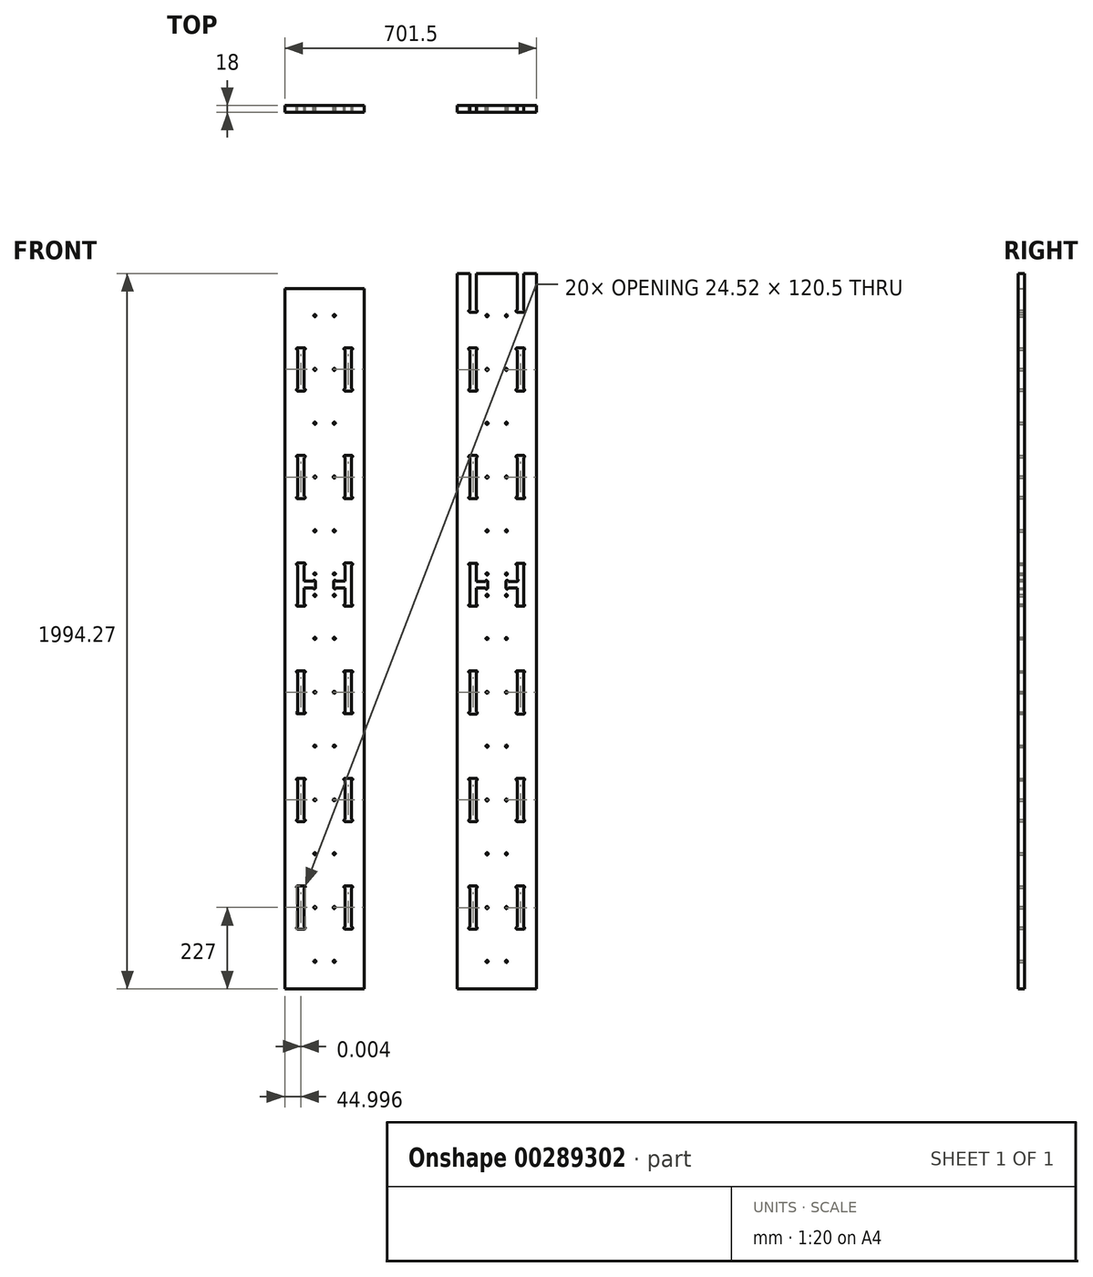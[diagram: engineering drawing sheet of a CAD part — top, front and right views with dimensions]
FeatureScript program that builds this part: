
annotation { "Feature Type Name" : "Feature", "Feature Type Description" : "" }
export const myFeature = defineFeature(function(context is Context, id is Id, definition is map)
    precondition{}
    {
        {
            var Q0;
            Q0=qCreatedBy(makeId("Front.planeOp"),FACE);
            var sketch = newSketch(context, id + "F0", { "sketchPlane" : qUnion([Q0])});
            skLineSegment(sketch, "E0", {"start": v(-600, -1200) * mm, "end": v(600, -1200) * mm});
            skLineSegment(sketch, "E1", {"start": v(600, -1200) * mm, "end": v(600, 1200) * mm});
            skLineSegment(sketch, "E2", {"start": v(600, 1200) * mm, "end": v(-600, 1200) * mm});
            skLineSegment(sketch, "E3", {"start": v(-600, 1200) * mm, "end": v(-600, -1200) * mm});
            skLineSegment(sketch, "E4", {"start": v(366, 819.27) * mm, "end": v(330.5, 819.27) * mm});
            skLineSegment(sketch, "E5", {"start": v(330.5, 819.27) * mm, "end": v(330.5, 717.52) * mm});
            skArc(sketch, "E6", {"start": v(330.5, 717.52) * mm, "mid": v(333.51, 714.51) * mm, "end": v(330.5, 711.5) * mm});
            skLineSegment(sketch, "E7", {"start": v(330.5, 711.5) * mm, "end": v(312, 711.5) * mm});
            skArc(sketch, "E8", {"start": v(312, 711.5) * mm, "mid": v(309, 714.51) * mm, "end": v(312, 717.52) * mm});
            skLineSegment(sketch, "E9", {"start": v(312, 717.52) * mm, "end": v(312, 819.27) * mm});
            skLineSegment(sketch, "E10", {"start": v(312, 819.27) * mm, "end": v(198.5, 819.27) * mm});
            skLineSegment(sketch, "E11", {"start": v(198.5, 819.27) * mm, "end": v(198.5, 717.52) * mm});
            skArc(sketch, "E12", {"start": v(198.5, 717.52) * mm, "mid": v(201.51, 714.51) * mm, "end": v(198.5, 711.5) * mm});
            skLineSegment(sketch, "E13", {"start": v(198.5, 711.5) * mm, "end": v(180, 711.5) * mm});
            skArc(sketch, "E14", {"start": v(180, 711.5) * mm, "mid": v(177, 714.51) * mm, "end": v(180, 717.52) * mm});
            skLineSegment(sketch, "E15", {"start": v(180, 717.52) * mm, "end": v(180, 819.27) * mm});
            skLineSegment(sketch, "E16", {"start": v(180, 819.27) * mm, "end": v(144.5, 819.27) * mm});
            skLineSegment(sketch, "E17", {"start": v(144.5, 819.27) * mm, "end": v(144.5, -1175) * mm});
            skLineSegment(sketch, "E18", {"start": v(144.5, -1175) * mm, "end": v(366, -1175) * mm});
            skLineSegment(sketch, "E19", {"start": v(366, -1175) * mm, "end": v(366, 819.27) * mm});
            skLineSegment(sketch, "E20", {"start": v(126.5, 819.27) * mm, "end": v(91, 819.27) * mm});
            skLineSegment(sketch, "E21", {"start": v(91, 819.27) * mm, "end": v(91, 717.52) * mm});
            skArc(sketch, "E22", {"start": v(91, 717.52) * mm, "mid": v(94.01, 714.51) * mm, "end": v(91, 711.5) * mm});
            skLineSegment(sketch, "E23", {"start": v(91, 711.5) * mm, "end": v(72.5, 711.5) * mm});
            skArc(sketch, "E24", {"start": v(72.5, 711.5) * mm, "mid": v(69.5, 714.51) * mm, "end": v(72.5, 717.52) * mm});
            skLineSegment(sketch, "E25", {"start": v(72.5, 717.52) * mm, "end": v(72.5, 819.27) * mm});
            skLineSegment(sketch, "E26", {"start": v(72.5, 819.27) * mm, "end": v(-41, 819.27) * mm});
            skLineSegment(sketch, "E27", {"start": v(-41, 819.27) * mm, "end": v(-41, 717.52) * mm});
            skArc(sketch, "E28", {"start": v(-41, 717.52) * mm, "mid": v(-37.99, 714.51) * mm, "end": v(-41, 711.5) * mm});
            skLineSegment(sketch, "E29", {"start": v(-41, 711.5) * mm, "end": v(-59.5, 711.5) * mm});
            skArc(sketch, "E30", {"start": v(-59.5, 711.5) * mm, "mid": v(-62.5, 714.51) * mm, "end": v(-59.5, 717.52) * mm});
            skLineSegment(sketch, "E31", {"start": v(-59.5, 717.52) * mm, "end": v(-59.5, 819.27) * mm});
            skLineSegment(sketch, "E32", {"start": v(-59.5, 819.27) * mm, "end": v(-95, 819.27) * mm});
            skLineSegment(sketch, "E33", {"start": v(-95, 819.27) * mm, "end": v(-95, -1175) * mm});
            skLineSegment(sketch, "E34", {"start": v(-95, -1175) * mm, "end": v(126.5, -1175) * mm});
            skLineSegment(sketch, "E35", {"start": v(126.5, -1175) * mm, "end": v(126.5, 819.27) * mm});
            skLineSegment(sketch, "E36", {"start": v(-353, 777.5) * mm, "end": v(-575, 777.5) * mm});
            skLineSegment(sketch, "E37", {"start": v(-575, 777.5) * mm, "end": v(-575, -1175) * mm});
            skLineSegment(sketch, "E38", {"start": v(-575, -1175) * mm, "end": v(-353, -1175) * mm});
            skLineSegment(sketch, "E39", {"start": v(-353, -1175) * mm, "end": v(-353, 777.5) * mm});
            skLineSegment(sketch, "E40", {"start": v(-113, 777.5) * mm, "end": v(-335, 777.5) * mm});
            skLineSegment(sketch, "E41", {"start": v(-335, 777.5) * mm, "end": v(-335, -1175) * mm});
            skLineSegment(sketch, "E42", {"start": v(-335, -1175) * mm, "end": v(-113, -1175) * mm});
            skLineSegment(sketch, "E43", {"start": v(-113, -1175) * mm, "end": v(-113, 777.5) * mm});
            skLineSegment(sketch, "E44", {"start": v(198.5, -888) * mm, "end": v(180, -888) * mm});
            skArc(sketch, "E45", {"start": v(180, -888) * mm, "mid": v(177, -891) * mm, "end": v(180, -894.02) * mm});
            skLineSegment(sketch, "E46", {"start": v(180, -894.02) * mm, "end": v(180, -1002.48) * mm});
            skArc(sketch, "E47", {"start": v(180, -1002.48) * mm, "mid": v(177, -1005.49) * mm, "end": v(180, -1008.5) * mm});
            skLineSegment(sketch, "E48", {"start": v(180, -1008.5) * mm, "end": v(198.5, -1008.5) * mm});
            skArc(sketch, "E49", {"start": v(198.5, -1008.5) * mm, "mid": v(201.51, -1005.49) * mm, "end": v(198.5, -1002.48) * mm});
            skLineSegment(sketch, "E50", {"start": v(198.5, -1002.48) * mm, "end": v(198.5, -894.02) * mm});
            skArc(sketch, "E51", {"start": v(198.5, -894.02) * mm, "mid": v(201.51, -891) * mm, "end": v(198.5, -888) * mm});
            skLineSegment(sketch, "E52", {"start": v(312, -948.25) * mm, "end": v(312, -1002.48) * mm});
            skArc(sketch, "E53", {"start": v(312, -1002.48) * mm, "mid": v(309, -1005.49) * mm, "end": v(312, -1008.5) * mm});
            skLineSegment(sketch, "E54", {"start": v(312, -1008.5) * mm, "end": v(330.5, -1008.5) * mm});
            skArc(sketch, "E55", {"start": v(330.5, -1008.5) * mm, "mid": v(333.51, -1005.49) * mm, "end": v(330.5, -1002.48) * mm});
            skLineSegment(sketch, "E56", {"start": v(330.5, -1002.48) * mm, "end": v(330.5, -894.02) * mm});
            skArc(sketch, "E57", {"start": v(330.5, -894.02) * mm, "mid": v(333.51, -891) * mm, "end": v(330.5, -888) * mm});
            skLineSegment(sketch, "E58", {"start": v(330.5, -888) * mm, "end": v(312, -888) * mm});
            skArc(sketch, "E59", {"start": v(312, -888) * mm, "mid": v(309, -891) * mm, "end": v(312, -894.02) * mm});
            skLineSegment(sketch, "E60", {"start": v(312, -894.02) * mm, "end": v(312, -948.25) * mm});
            skLineSegment(sketch, "E61", {"start": v(312, -594.02) * mm, "end": v(312, -702.48) * mm});
            skArc(sketch, "E62", {"start": v(312, -702.48) * mm, "mid": v(309, -705.49) * mm, "end": v(312, -708.5) * mm});
            skLineSegment(sketch, "E63", {"start": v(312, -708.5) * mm, "end": v(330.5, -708.5) * mm});
            skArc(sketch, "E64", {"start": v(330.5, -708.5) * mm, "mid": v(333.51, -705.49) * mm, "end": v(330.5, -702.48) * mm});
            skLineSegment(sketch, "E65", {"start": v(330.5, -702.48) * mm, "end": v(330.5, -594.02) * mm});
            skArc(sketch, "E66", {"start": v(330.5, -594.02) * mm, "mid": v(333.51, -591) * mm, "end": v(330.5, -588) * mm});
            skLineSegment(sketch, "E67", {"start": v(330.5, -588) * mm, "end": v(312, -588) * mm});
            skArc(sketch, "E68", {"start": v(312, -588) * mm, "mid": v(309, -591) * mm, "end": v(312, -594.02) * mm});
            skLineSegment(sketch, "E69", {"start": v(330.5, -402.48) * mm, "end": v(330.5, -294.02) * mm});
            skArc(sketch, "E70", {"start": v(330.5, -294.02) * mm, "mid": v(333.51, -291) * mm, "end": v(330.5, -288) * mm});
            skLineSegment(sketch, "E71", {"start": v(330.5, -288) * mm, "end": v(312, -288) * mm});
            skArc(sketch, "E72", {"start": v(312, -288) * mm, "mid": v(309, -291) * mm, "end": v(312, -294.02) * mm});
            skLineSegment(sketch, "E73", {"start": v(312, -294.02) * mm, "end": v(312, -402.48) * mm});
            skArc(sketch, "E74", {"start": v(312, -402.48) * mm, "mid": v(309, -405.49) * mm, "end": v(312, -408.5) * mm});
            skLineSegment(sketch, "E75", {"start": v(312, -408.5) * mm, "end": v(330.5, -408.5) * mm});
            skArc(sketch, "E76", {"start": v(330.5, -408.5) * mm, "mid": v(333.51, -405.49) * mm, "end": v(330.5, -402.48) * mm});
            skLineSegment(sketch, "E77", {"start": v(330.5, -102.48) * mm, "end": v(330.5, 5.98) * mm});
            skArc(sketch, "E78", {"start": v(330.5, 5.98) * mm, "mid": v(333.51, 9) * mm, "end": v(330.5, 12) * mm});
            skLineSegment(sketch, "E79", {"start": v(330.5, 12) * mm, "end": v(312, 12) * mm});
            skArc(sketch, "E80", {"start": v(312, 12) * mm, "mid": v(309, 9) * mm, "end": v(312, 5.98) * mm});
            skLineSegment(sketch, "E81", {"start": v(312, 5.98) * mm, "end": v(312, -32.98) * mm});
            skArc(sketch, "E82", {"start": v(312, -32.98) * mm, "mid": v(315.01, -35.99) * mm, "end": v(312, -39) * mm});
            skLineSegment(sketch, "E83", {"start": v(312, -39) * mm, "end": v(287.02, -39) * mm});
            skArc(sketch, "E84", {"start": v(287.02, -39) * mm, "mid": v(284.01, -35.99) * mm, "end": v(281, -39) * mm});
            skLineSegment(sketch, "E85", {"start": v(281, -39) * mm, "end": v(281, -57.5) * mm});
            skArc(sketch, "E86", {"start": v(281, -57.5) * mm, "mid": v(284.01, -60.5) * mm, "end": v(287.02, -57.5) * mm});
            skLineSegment(sketch, "E87", {"start": v(287.02, -57.5) * mm, "end": v(312, -57.5) * mm});
            skLineSegment(sketch, "E88", {"start": v(312, -57.5) * mm, "end": v(312, -102.48) * mm});
            skArc(sketch, "E89", {"start": v(312, -102.48) * mm, "mid": v(309, -105.49) * mm, "end": v(312, -108.5) * mm});
            skLineSegment(sketch, "E90", {"start": v(312, -108.5) * mm, "end": v(330.5, -108.5) * mm});
            skArc(sketch, "E91", {"start": v(330.5, -108.5) * mm, "mid": v(333.51, -105.49) * mm, "end": v(330.5, -102.48) * mm});
            skLineSegment(sketch, "E92", {"start": v(312, 305.98) * mm, "end": v(312, 197.52) * mm});
            skArc(sketch, "E93", {"start": v(312, 197.52) * mm, "mid": v(309, 194.51) * mm, "end": v(312, 191.5) * mm});
            skLineSegment(sketch, "E94", {"start": v(312, 191.5) * mm, "end": v(330.5, 191.5) * mm});
            skArc(sketch, "E95", {"start": v(330.5, 191.5) * mm, "mid": v(333.51, 194.51) * mm, "end": v(330.5, 197.52) * mm});
            skLineSegment(sketch, "E96", {"start": v(330.5, 197.52) * mm, "end": v(330.5, 305.98) * mm});
            skArc(sketch, "E97", {"start": v(330.5, 305.98) * mm, "mid": v(333.51, 309) * mm, "end": v(330.5, 312) * mm});
            skLineSegment(sketch, "E98", {"start": v(330.5, 312) * mm, "end": v(312, 312) * mm});
            skArc(sketch, "E99", {"start": v(312, 312) * mm, "mid": v(309, 309) * mm, "end": v(312, 305.98) * mm});
            skLineSegment(sketch, "E100", {"start": v(330.5, 497.52) * mm, "end": v(330.5, 605.98) * mm});
            skArc(sketch, "E101", {"start": v(330.5, 605.98) * mm, "mid": v(333.51, 609) * mm, "end": v(330.5, 612) * mm});
            skLineSegment(sketch, "E102", {"start": v(330.5, 612) * mm, "end": v(312, 612) * mm});
            skArc(sketch, "E103", {"start": v(312, 612) * mm, "mid": v(309, 609) * mm, "end": v(312, 605.98) * mm});
            skLineSegment(sketch, "E104", {"start": v(312, 605.98) * mm, "end": v(312, 497.52) * mm});
            skArc(sketch, "E105", {"start": v(312, 497.52) * mm, "mid": v(309, 494.51) * mm, "end": v(312, 491.5) * mm});
            skLineSegment(sketch, "E106", {"start": v(312, 491.5) * mm, "end": v(330.5, 491.5) * mm});
            skArc(sketch, "E107", {"start": v(330.5, 491.5) * mm, "mid": v(333.51, 494.51) * mm, "end": v(330.5, 497.52) * mm});
            skLineSegment(sketch, "E108", {"start": v(180, 605.98) * mm, "end": v(180, 497.52) * mm});
            skArc(sketch, "E109", {"start": v(180, 497.52) * mm, "mid": v(177, 494.51) * mm, "end": v(180, 491.5) * mm});
            skLineSegment(sketch, "E110", {"start": v(180, 491.5) * mm, "end": v(198.5, 491.5) * mm});
            skArc(sketch, "E111", {"start": v(198.5, 491.5) * mm, "mid": v(201.51, 494.51) * mm, "end": v(198.5, 497.52) * mm});
            skLineSegment(sketch, "E112", {"start": v(198.5, 497.52) * mm, "end": v(198.5, 605.98) * mm});
            skArc(sketch, "E113", {"start": v(198.5, 605.98) * mm, "mid": v(201.51, 609) * mm, "end": v(198.5, 612) * mm});
            skLineSegment(sketch, "E114", {"start": v(198.5, 612) * mm, "end": v(180, 612) * mm});
            skArc(sketch, "E115", {"start": v(180, 612) * mm, "mid": v(177, 609) * mm, "end": v(180, 605.98) * mm});
            skLineSegment(sketch, "E116", {"start": v(198.5, -702.48) * mm, "end": v(198.5, -594.02) * mm});
            skArc(sketch, "E117", {"start": v(198.5, -594.02) * mm, "mid": v(201.51, -591.01) * mm, "end": v(198.5, -588) * mm});
            skLineSegment(sketch, "E118", {"start": v(198.5, -588) * mm, "end": v(180, -588) * mm});
            skArc(sketch, "E119", {"start": v(180, -588) * mm, "mid": v(177, -591.01) * mm, "end": v(180, -594.02) * mm});
            skLineSegment(sketch, "E120", {"start": v(180, -594.02) * mm, "end": v(180, -702.48) * mm});
            skArc(sketch, "E121", {"start": v(180, -702.48) * mm, "mid": v(177, -705.5) * mm, "end": v(180, -708.5) * mm});
            skLineSegment(sketch, "E122", {"start": v(180, -708.5) * mm, "end": v(198.5, -708.5) * mm});
            skArc(sketch, "E123", {"start": v(198.5, -708.5) * mm, "mid": v(201.51, -705.5) * mm, "end": v(198.5, -702.48) * mm});
            skLineSegment(sketch, "E124", {"start": v(180, -294.02) * mm, "end": v(180, -402.48) * mm});
            skArc(sketch, "E125", {"start": v(180, -402.48) * mm, "mid": v(177, -405.5) * mm, "end": v(180, -408.5) * mm});
            skLineSegment(sketch, "E126", {"start": v(180, -408.5) * mm, "end": v(198.5, -408.5) * mm});
            skArc(sketch, "E127", {"start": v(198.5, -408.5) * mm, "mid": v(201.51, -405.5) * mm, "end": v(198.5, -402.48) * mm});
            skLineSegment(sketch, "E128", {"start": v(198.5, -402.48) * mm, "end": v(198.5, -294.02) * mm});
            skArc(sketch, "E129", {"start": v(198.5, -294.02) * mm, "mid": v(201.51, -291.01) * mm, "end": v(198.5, -288) * mm});
            skLineSegment(sketch, "E130", {"start": v(198.5, -288) * mm, "end": v(180, -288) * mm});
            skArc(sketch, "E131", {"start": v(180, -288) * mm, "mid": v(177, -291.01) * mm, "end": v(180, -294.02) * mm});
            skLineSegment(sketch, "E132", {"start": v(198.5, -39) * mm, "end": v(198.5, 5.98) * mm});
            skArc(sketch, "E133", {"start": v(198.5, 5.98) * mm, "mid": v(201.51, 9) * mm, "end": v(198.5, 12) * mm});
            skLineSegment(sketch, "E134", {"start": v(198.5, 12) * mm, "end": v(180, 12) * mm});
            skArc(sketch, "E135", {"start": v(180, 12) * mm, "mid": v(177, 9) * mm, "end": v(180, 5.98) * mm});
            skLineSegment(sketch, "E136", {"start": v(180, 5.98) * mm, "end": v(180, -102.48) * mm});
            skArc(sketch, "E137", {"start": v(180, -102.48) * mm, "mid": v(177, -105.49) * mm, "end": v(180, -108.5) * mm});
            skLineSegment(sketch, "E138", {"start": v(180, -108.5) * mm, "end": v(198.5, -108.5) * mm});
            skArc(sketch, "E139", {"start": v(198.5, -108.5) * mm, "mid": v(201.51, -105.49) * mm, "end": v(198.5, -102.48) * mm});
            skLineSegment(sketch, "E140", {"start": v(198.5, -102.48) * mm, "end": v(198.5, -57.5) * mm});
            skLineSegment(sketch, "E141", {"start": v(198.5, -57.5) * mm, "end": v(223.48, -57.5) * mm});
            skArc(sketch, "E142", {"start": v(223.48, -57.5) * mm, "mid": v(226.5, -60.5) * mm, "end": v(229.5, -57.5) * mm});
            skLineSegment(sketch, "E143", {"start": v(229.5, -57.5) * mm, "end": v(229.5, -39) * mm});
            skArc(sketch, "E144", {"start": v(229.5, -39) * mm, "mid": v(226.5, -35.99) * mm, "end": v(223.48, -39) * mm});
            skLineSegment(sketch, "E145", {"start": v(223.48, -39) * mm, "end": v(198.5, -39) * mm});
            skLineSegment(sketch, "E146", {"start": v(198.5, 197.52) * mm, "end": v(198.5, 305.98) * mm});
            skArc(sketch, "E147", {"start": v(198.5, 305.98) * mm, "mid": v(201.51, 309) * mm, "end": v(198.5, 312) * mm});
            skLineSegment(sketch, "E148", {"start": v(198.5, 312) * mm, "end": v(180, 312) * mm});
            skArc(sketch, "E149", {"start": v(180, 312) * mm, "mid": v(177, 309) * mm, "end": v(180, 305.98) * mm});
            skLineSegment(sketch, "E150", {"start": v(180, 305.98) * mm, "end": v(180, 197.52) * mm});
            skArc(sketch, "E151", {"start": v(180, 197.52) * mm, "mid": v(177, 194.51) * mm, "end": v(180, 191.5) * mm});
            skLineSegment(sketch, "E152", {"start": v(180, 191.5) * mm, "end": v(198.5, 191.5) * mm});
            skArc(sketch, "E153", {"start": v(198.5, 191.5) * mm, "mid": v(201.51, 194.51) * mm, "end": v(198.5, 197.52) * mm});
            skLineSegment(sketch, "E154", {"start": v(-41, -888) * mm, "end": v(-59.5, -888) * mm});
            skArc(sketch, "E155", {"start": v(-59.5, -888) * mm, "mid": v(-62.5, -891) * mm, "end": v(-59.5, -894.02) * mm});
            skLineSegment(sketch, "E156", {"start": v(-59.5, -894.02) * mm, "end": v(-59.5, -1002.48) * mm});
            skArc(sketch, "E157", {"start": v(-59.5, -1002.48) * mm, "mid": v(-62.5, -1005.49) * mm, "end": v(-59.5, -1008.5) * mm});
            skLineSegment(sketch, "E158", {"start": v(-59.5, -1008.5) * mm, "end": v(-41, -1008.5) * mm});
            skArc(sketch, "E159", {"start": v(-41, -1008.5) * mm, "mid": v(-37.99, -1005.49) * mm, "end": v(-41, -1002.48) * mm});
            skLineSegment(sketch, "E160", {"start": v(-41, -1002.48) * mm, "end": v(-41, -894.02) * mm});
            skArc(sketch, "E161", {"start": v(-41, -894.02) * mm, "mid": v(-37.99, -891) * mm, "end": v(-41, -888) * mm});
            skLineSegment(sketch, "E162", {"start": v(72.5, -948.25) * mm, "end": v(72.5, -1002.48) * mm});
            skArc(sketch, "E163", {"start": v(72.5, -1002.48) * mm, "mid": v(69.5, -1005.49) * mm, "end": v(72.5, -1008.5) * mm});
            skLineSegment(sketch, "E164", {"start": v(72.5, -1008.5) * mm, "end": v(91, -1008.5) * mm});
            skArc(sketch, "E165", {"start": v(91, -1008.5) * mm, "mid": v(94.01, -1005.49) * mm, "end": v(91, -1002.48) * mm});
            skLineSegment(sketch, "E166", {"start": v(91, -1002.48) * mm, "end": v(91, -894.02) * mm});
            skArc(sketch, "E167", {"start": v(91, -894.02) * mm, "mid": v(94.01, -891) * mm, "end": v(91, -888) * mm});
            skLineSegment(sketch, "E168", {"start": v(91, -888) * mm, "end": v(72.5, -888) * mm});
            skArc(sketch, "E169", {"start": v(72.5, -888) * mm, "mid": v(69.5, -891) * mm, "end": v(72.5, -894.02) * mm});
            skLineSegment(sketch, "E170", {"start": v(72.5, -894.02) * mm, "end": v(72.5, -948.25) * mm});
            skLineSegment(sketch, "E171", {"start": v(72.5, -594.02) * mm, "end": v(72.5, -702.48) * mm});
            skArc(sketch, "E172", {"start": v(72.5, -702.48) * mm, "mid": v(69.5, -705.49) * mm, "end": v(72.5, -708.5) * mm});
            skLineSegment(sketch, "E173", {"start": v(72.5, -708.5) * mm, "end": v(91, -708.5) * mm});
            skArc(sketch, "E174", {"start": v(91, -708.5) * mm, "mid": v(94.01, -705.49) * mm, "end": v(91, -702.48) * mm});
            skLineSegment(sketch, "E175", {"start": v(91, -702.48) * mm, "end": v(91, -594.02) * mm});
            skArc(sketch, "E176", {"start": v(91, -594.02) * mm, "mid": v(94.01, -591) * mm, "end": v(91, -588) * mm});
            skLineSegment(sketch, "E177", {"start": v(91, -588) * mm, "end": v(72.5, -588) * mm});
            skArc(sketch, "E178", {"start": v(72.5, -588) * mm, "mid": v(69.5, -591) * mm, "end": v(72.5, -594.02) * mm});
            skLineSegment(sketch, "E179", {"start": v(91, -402.48) * mm, "end": v(91, -294.02) * mm});
            skArc(sketch, "E180", {"start": v(91, -294.02) * mm, "mid": v(94.01, -291) * mm, "end": v(91, -288) * mm});
            skLineSegment(sketch, "E181", {"start": v(91, -288) * mm, "end": v(72.5, -288) * mm});
            skArc(sketch, "E182", {"start": v(72.5, -288) * mm, "mid": v(69.5, -291) * mm, "end": v(72.5, -294.02) * mm});
            skLineSegment(sketch, "E183", {"start": v(72.5, -294.02) * mm, "end": v(72.5, -402.48) * mm});
            skArc(sketch, "E184", {"start": v(72.5, -402.48) * mm, "mid": v(69.5, -405.49) * mm, "end": v(72.5, -408.5) * mm});
            skLineSegment(sketch, "E185", {"start": v(72.5, -408.5) * mm, "end": v(91, -408.5) * mm});
            skArc(sketch, "E186", {"start": v(91, -408.5) * mm, "mid": v(94.01, -405.49) * mm, "end": v(91, -402.48) * mm});
            skLineSegment(sketch, "E187", {"start": v(91, -102.48) * mm, "end": v(91, 5.98) * mm});
            skArc(sketch, "E188", {"start": v(91, 5.98) * mm, "mid": v(94.01, 9) * mm, "end": v(91, 12) * mm});
            skLineSegment(sketch, "E189", {"start": v(91, 12) * mm, "end": v(72.5, 12) * mm});
            skArc(sketch, "E190", {"start": v(72.5, 12) * mm, "mid": v(69.5, 9) * mm, "end": v(72.5, 5.98) * mm});
            skLineSegment(sketch, "E191", {"start": v(72.5, 5.98) * mm, "end": v(72.5, -32.98) * mm});
            skArc(sketch, "E192", {"start": v(72.5, -32.98) * mm, "mid": v(75.51, -35.99) * mm, "end": v(72.5, -39) * mm});
            skLineSegment(sketch, "E193", {"start": v(72.5, -39) * mm, "end": v(47.52, -39) * mm});
            skArc(sketch, "E194", {"start": v(47.52, -39) * mm, "mid": v(44.51, -35.99) * mm, "end": v(41.5, -39) * mm});
            skLineSegment(sketch, "E195", {"start": v(41.5, -39) * mm, "end": v(41.5, -57.5) * mm});
            skArc(sketch, "E196", {"start": v(41.5, -57.5) * mm, "mid": v(44.51, -60.5) * mm, "end": v(47.52, -57.5) * mm});
            skLineSegment(sketch, "E197", {"start": v(47.52, -57.5) * mm, "end": v(72.5, -57.5) * mm});
            skLineSegment(sketch, "E198", {"start": v(72.5, -57.5) * mm, "end": v(72.5, -102.48) * mm});
            skArc(sketch, "E199", {"start": v(72.5, -102.48) * mm, "mid": v(69.5, -105.49) * mm, "end": v(72.5, -108.5) * mm});
            skLineSegment(sketch, "E200", {"start": v(72.5, -108.5) * mm, "end": v(91, -108.5) * mm});
            skArc(sketch, "E201", {"start": v(91, -108.5) * mm, "mid": v(94.01, -105.49) * mm, "end": v(91, -102.48) * mm});
            skLineSegment(sketch, "E202", {"start": v(72.5, 305.98) * mm, "end": v(72.5, 197.52) * mm});
            skArc(sketch, "E203", {"start": v(72.5, 197.52) * mm, "mid": v(69.5, 194.51) * mm, "end": v(72.5, 191.5) * mm});
            skLineSegment(sketch, "E204", {"start": v(72.5, 191.5) * mm, "end": v(91, 191.5) * mm});
            skArc(sketch, "E205", {"start": v(91, 191.5) * mm, "mid": v(94.01, 194.51) * mm, "end": v(91, 197.52) * mm});
            skLineSegment(sketch, "E206", {"start": v(91, 197.52) * mm, "end": v(91, 305.98) * mm});
            skArc(sketch, "E207", {"start": v(91, 305.98) * mm, "mid": v(94.01, 309) * mm, "end": v(91, 312) * mm});
            skLineSegment(sketch, "E208", {"start": v(91, 312) * mm, "end": v(72.5, 312) * mm});
            skArc(sketch, "E209", {"start": v(72.5, 312) * mm, "mid": v(69.5, 309) * mm, "end": v(72.5, 305.98) * mm});
            skLineSegment(sketch, "E210", {"start": v(91, 497.52) * mm, "end": v(91, 605.98) * mm});
            skArc(sketch, "E211", {"start": v(91, 605.98) * mm, "mid": v(94.01, 609) * mm, "end": v(91, 612) * mm});
            skLineSegment(sketch, "E212", {"start": v(91, 612) * mm, "end": v(72.5, 612) * mm});
            skArc(sketch, "E213", {"start": v(72.5, 612) * mm, "mid": v(69.5, 609) * mm, "end": v(72.5, 605.98) * mm});
            skLineSegment(sketch, "E214", {"start": v(72.5, 605.98) * mm, "end": v(72.5, 497.52) * mm});
            skArc(sketch, "E215", {"start": v(72.5, 497.52) * mm, "mid": v(69.5, 494.51) * mm, "end": v(72.5, 491.5) * mm});
            skLineSegment(sketch, "E216", {"start": v(72.5, 491.5) * mm, "end": v(91, 491.5) * mm});
            skArc(sketch, "E217", {"start": v(91, 491.5) * mm, "mid": v(94.01, 494.51) * mm, "end": v(91, 497.52) * mm});
            skLineSegment(sketch, "E218", {"start": v(-59.5, 605.98) * mm, "end": v(-59.5, 497.52) * mm});
            skArc(sketch, "E219", {"start": v(-59.5, 497.52) * mm, "mid": v(-62.5, 494.51) * mm, "end": v(-59.5, 491.5) * mm});
            skLineSegment(sketch, "E220", {"start": v(-59.5, 491.5) * mm, "end": v(-41, 491.5) * mm});
            skArc(sketch, "E221", {"start": v(-41, 491.5) * mm, "mid": v(-37.99, 494.51) * mm, "end": v(-41, 497.52) * mm});
            skLineSegment(sketch, "E222", {"start": v(-41, 497.52) * mm, "end": v(-41, 605.98) * mm});
            skArc(sketch, "E223", {"start": v(-41, 605.98) * mm, "mid": v(-37.99, 609) * mm, "end": v(-41, 612) * mm});
            skLineSegment(sketch, "E224", {"start": v(-41, 612) * mm, "end": v(-59.5, 612) * mm});
            skArc(sketch, "E225", {"start": v(-59.5, 612) * mm, "mid": v(-62.5, 609) * mm, "end": v(-59.5, 605.98) * mm});
            skLineSegment(sketch, "E226", {"start": v(-41, -702.48) * mm, "end": v(-41, -594.02) * mm});
            skArc(sketch, "E227", {"start": v(-41, -594.02) * mm, "mid": v(-37.99, -591.01) * mm, "end": v(-41, -588) * mm});
            skLineSegment(sketch, "E228", {"start": v(-41, -588) * mm, "end": v(-59.5, -588) * mm});
            skArc(sketch, "E229", {"start": v(-59.5, -588) * mm, "mid": v(-62.5, -591.01) * mm, "end": v(-59.5, -594.02) * mm});
            skLineSegment(sketch, "E230", {"start": v(-59.5, -594.02) * mm, "end": v(-59.5, -702.48) * mm});
            skArc(sketch, "E231", {"start": v(-59.5, -702.48) * mm, "mid": v(-62.5, -705.5) * mm, "end": v(-59.5, -708.5) * mm});
            skLineSegment(sketch, "E232", {"start": v(-59.5, -708.5) * mm, "end": v(-41, -708.5) * mm});
            skArc(sketch, "E233", {"start": v(-41, -708.5) * mm, "mid": v(-37.99, -705.5) * mm, "end": v(-41, -702.48) * mm});
            skLineSegment(sketch, "E234", {"start": v(-59.5, -294.02) * mm, "end": v(-59.5, -402.48) * mm});
            skArc(sketch, "E235", {"start": v(-59.5, -402.48) * mm, "mid": v(-62.5, -405.5) * mm, "end": v(-59.5, -408.5) * mm});
            skLineSegment(sketch, "E236", {"start": v(-59.5, -408.5) * mm, "end": v(-41, -408.5) * mm});
            skArc(sketch, "E237", {"start": v(-41, -408.5) * mm, "mid": v(-37.99, -405.5) * mm, "end": v(-41, -402.48) * mm});
            skLineSegment(sketch, "E238", {"start": v(-41, -402.48) * mm, "end": v(-41, -294.02) * mm});
            skArc(sketch, "E239", {"start": v(-41, -294.02) * mm, "mid": v(-37.99, -291.01) * mm, "end": v(-41, -288) * mm});
            skLineSegment(sketch, "E240", {"start": v(-41, -288) * mm, "end": v(-59.5, -288) * mm});
            skArc(sketch, "E241", {"start": v(-59.5, -288) * mm, "mid": v(-62.5, -291.01) * mm, "end": v(-59.5, -294.02) * mm});
            skLineSegment(sketch, "E242", {"start": v(-41, -39) * mm, "end": v(-41, 5.98) * mm});
            skArc(sketch, "E243", {"start": v(-41, 5.98) * mm, "mid": v(-37.99, 9) * mm, "end": v(-41, 12) * mm});
            skLineSegment(sketch, "E244", {"start": v(-41, 12) * mm, "end": v(-59.5, 12) * mm});
            skArc(sketch, "E245", {"start": v(-59.5, 12) * mm, "mid": v(-62.5, 9) * mm, "end": v(-59.5, 5.98) * mm});
            skLineSegment(sketch, "E246", {"start": v(-59.5, 5.98) * mm, "end": v(-59.5, -102.48) * mm});
            skArc(sketch, "E247", {"start": v(-59.5, -102.48) * mm, "mid": v(-62.5, -105.49) * mm, "end": v(-59.5, -108.5) * mm});
            skLineSegment(sketch, "E248", {"start": v(-59.5, -108.5) * mm, "end": v(-41, -108.5) * mm});
            skArc(sketch, "E249", {"start": v(-41, -108.5) * mm, "mid": v(-37.99, -105.49) * mm, "end": v(-41, -102.48) * mm});
            skLineSegment(sketch, "E250", {"start": v(-41, -102.48) * mm, "end": v(-41, -57.5) * mm});
            skLineSegment(sketch, "E251", {"start": v(-41, -57.5) * mm, "end": v(-16.02, -57.5) * mm});
            skArc(sketch, "E252", {"start": v(-16.02, -57.5) * mm, "mid": v(-13, -60.5) * mm, "end": v(-10, -57.5) * mm});
            skLineSegment(sketch, "E253", {"start": v(-10, -57.5) * mm, "end": v(-10, -39) * mm});
            skArc(sketch, "E254", {"start": v(-10, -39) * mm, "mid": v(-13, -35.99) * mm, "end": v(-16.02, -39) * mm});
            skLineSegment(sketch, "E255", {"start": v(-16.02, -39) * mm, "end": v(-41, -39) * mm});
            skLineSegment(sketch, "E256", {"start": v(-41, 197.52) * mm, "end": v(-41, 305.98) * mm});
            skArc(sketch, "E257", {"start": v(-41, 305.98) * mm, "mid": v(-37.99, 309) * mm, "end": v(-41, 312) * mm});
            skLineSegment(sketch, "E258", {"start": v(-41, 312) * mm, "end": v(-59.5, 312) * mm});
            skArc(sketch, "E259", {"start": v(-59.5, 312) * mm, "mid": v(-62.5, 309) * mm, "end": v(-59.5, 305.98) * mm});
            skLineSegment(sketch, "E260", {"start": v(-59.5, 305.98) * mm, "end": v(-59.5, 197.52) * mm});
            skArc(sketch, "E261", {"start": v(-59.5, 197.52) * mm, "mid": v(-62.5, 194.51) * mm, "end": v(-59.5, 191.5) * mm});
            skLineSegment(sketch, "E262", {"start": v(-59.5, 191.5) * mm, "end": v(-41, 191.5) * mm});
            skArc(sketch, "E263", {"start": v(-41, 191.5) * mm, "mid": v(-37.99, 194.51) * mm, "end": v(-41, 197.52) * mm});
            skLineSegment(sketch, "E264", {"start": v(-388.75, -1002.23) * mm, "end": v(-388.75, -893.77) * mm});
            skArc(sketch, "E265", {"start": v(-388.75, -893.77) * mm, "mid": v(-385.74, -890.76) * mm, "end": v(-388.75, -887.75) * mm});
            skLineSegment(sketch, "E266", {"start": v(-388.75, -887.75) * mm, "end": v(-407.25, -887.75) * mm});
            skArc(sketch, "E267", {"start": v(-407.25, -887.75) * mm, "mid": v(-410.26, -890.76) * mm, "end": v(-407.25, -893.77) * mm});
            skLineSegment(sketch, "E268", {"start": v(-407.25, -893.77) * mm, "end": v(-407.25, -1002.23) * mm});
            skArc(sketch, "E269", {"start": v(-407.25, -1002.23) * mm, "mid": v(-410.26, -1005.24) * mm, "end": v(-407.25, -1008.25) * mm});
            skLineSegment(sketch, "E270", {"start": v(-407.25, -1008.25) * mm, "end": v(-388.75, -1008.25) * mm});
            skArc(sketch, "E271", {"start": v(-388.75, -1008.25) * mm, "mid": v(-385.74, -1005.24) * mm, "end": v(-388.75, -1002.23) * mm});
            skLineSegment(sketch, "E272", {"start": v(-388.75, 497.78) * mm, "end": v(-388.75, 606.24) * mm});
            skArc(sketch, "E273", {"start": v(-388.75, 606.24) * mm, "mid": v(-385.74, 609.25) * mm, "end": v(-388.75, 612.26) * mm});
            skLineSegment(sketch, "E274", {"start": v(-388.75, 612.26) * mm, "end": v(-407.25, 612.26) * mm});
            skArc(sketch, "E275", {"start": v(-407.25, 612.26) * mm, "mid": v(-410.26, 609.25) * mm, "end": v(-407.25, 606.24) * mm});
            skLineSegment(sketch, "E276", {"start": v(-407.25, 606.24) * mm, "end": v(-407.25, 497.78) * mm});
            skArc(sketch, "E277", {"start": v(-407.25, 497.78) * mm, "mid": v(-410.26, 494.77) * mm, "end": v(-407.25, 491.76) * mm});
            skLineSegment(sketch, "E278", {"start": v(-407.25, 491.76) * mm, "end": v(-388.75, 491.76) * mm});
            skArc(sketch, "E279", {"start": v(-388.75, 491.76) * mm, "mid": v(-385.74, 494.77) * mm, "end": v(-388.75, 497.78) * mm});
            skLineSegment(sketch, "E280", {"start": v(-539.25, 606.23) * mm, "end": v(-539.25, 497.77) * mm});
            skArc(sketch, "E281", {"start": v(-539.25, 497.77) * mm, "mid": v(-542.26, 494.76) * mm, "end": v(-539.25, 491.75) * mm});
            skLineSegment(sketch, "E282", {"start": v(-539.25, 491.75) * mm, "end": v(-520.75, 491.75) * mm});
            skArc(sketch, "E283", {"start": v(-520.75, 491.75) * mm, "mid": v(-517.74, 494.76) * mm, "end": v(-520.75, 497.77) * mm});
            skLineSegment(sketch, "E284", {"start": v(-520.75, 497.77) * mm, "end": v(-520.75, 606.23) * mm});
            skArc(sketch, "E285", {"start": v(-520.75, 606.23) * mm, "mid": v(-517.74, 609.24) * mm, "end": v(-520.75, 612.25) * mm});
            skLineSegment(sketch, "E286", {"start": v(-520.75, 612.25) * mm, "end": v(-539.25, 612.25) * mm});
            skArc(sketch, "E287", {"start": v(-539.25, 612.25) * mm, "mid": v(-542.26, 609.24) * mm, "end": v(-539.25, 606.23) * mm});
            skLineSegment(sketch, "E288", {"start": v(-520.75, 197.77) * mm, "end": v(-520.75, 306.23) * mm});
            skArc(sketch, "E289", {"start": v(-520.75, 306.23) * mm, "mid": v(-517.74, 309.24) * mm, "end": v(-520.75, 312.25) * mm});
            skLineSegment(sketch, "E290", {"start": v(-520.75, 312.25) * mm, "end": v(-539.25, 312.25) * mm});
            skArc(sketch, "E291", {"start": v(-539.25, 312.25) * mm, "mid": v(-542.26, 309.24) * mm, "end": v(-539.25, 306.23) * mm});
            skLineSegment(sketch, "E292", {"start": v(-539.25, 306.23) * mm, "end": v(-539.25, 197.77) * mm});
            skArc(sketch, "E293", {"start": v(-539.25, 197.77) * mm, "mid": v(-542.26, 194.76) * mm, "end": v(-539.25, 191.75) * mm});
            skLineSegment(sketch, "E294", {"start": v(-539.25, 191.75) * mm, "end": v(-520.75, 191.75) * mm});
            skArc(sketch, "E295", {"start": v(-520.75, 191.75) * mm, "mid": v(-517.74, 194.76) * mm, "end": v(-520.75, 197.77) * mm});
            skLineSegment(sketch, "E296", {"start": v(-520.75, -38.74) * mm, "end": v(-520.75, 6.24) * mm});
            skArc(sketch, "E297", {"start": v(-520.75, 6.24) * mm, "mid": v(-517.74, 9.25) * mm, "end": v(-520.75, 12.26) * mm});
            skLineSegment(sketch, "E298", {"start": v(-520.75, 12.26) * mm, "end": v(-539.25, 12.26) * mm});
            skArc(sketch, "E299", {"start": v(-539.25, 12.26) * mm, "mid": v(-542.26, 9.25) * mm, "end": v(-539.25, 6.24) * mm});
            skLineSegment(sketch, "E300", {"start": v(-539.25, 6.24) * mm, "end": v(-539.25, -102.22) * mm});
            skArc(sketch, "E301", {"start": v(-539.25, -102.22) * mm, "mid": v(-542.26, -105.23) * mm, "end": v(-539.25, -108.24) * mm});
            skLineSegment(sketch, "E302", {"start": v(-539.25, -108.24) * mm, "end": v(-520.75, -108.24) * mm});
            skArc(sketch, "E303", {"start": v(-520.75, -108.24) * mm, "mid": v(-517.74, -105.23) * mm, "end": v(-520.75, -102.22) * mm});
            skLineSegment(sketch, "E304", {"start": v(-520.75, -102.22) * mm, "end": v(-520.75, -57.24) * mm});
            skLineSegment(sketch, "E305", {"start": v(-520.75, -57.24) * mm, "end": v(-495.77, -57.24) * mm});
            skArc(sketch, "E306", {"start": v(-495.77, -57.24) * mm, "mid": v(-492.76, -60.25) * mm, "end": v(-489.75, -57.24) * mm});
            skLineSegment(sketch, "E307", {"start": v(-489.75, -57.24) * mm, "end": v(-489.75, -38.74) * mm});
            skArc(sketch, "E308", {"start": v(-489.75, -38.74) * mm, "mid": v(-492.76, -35.73) * mm, "end": v(-495.77, -38.74) * mm});
            skLineSegment(sketch, "E309", {"start": v(-495.77, -38.74) * mm, "end": v(-520.75, -38.74) * mm});
            skLineSegment(sketch, "E310", {"start": v(-520.75, -402.23) * mm, "end": v(-520.75, -293.77) * mm});
            skArc(sketch, "E311", {"start": v(-520.75, -293.77) * mm, "mid": v(-517.74, -290.76) * mm, "end": v(-520.75, -287.75) * mm});
            skLineSegment(sketch, "E312", {"start": v(-520.75, -287.75) * mm, "end": v(-539.25, -287.75) * mm});
            skArc(sketch, "E313", {"start": v(-539.25, -287.75) * mm, "mid": v(-542.26, -290.76) * mm, "end": v(-539.25, -293.77) * mm});
            skLineSegment(sketch, "E314", {"start": v(-539.25, -293.77) * mm, "end": v(-539.25, -402.23) * mm});
            skArc(sketch, "E315", {"start": v(-539.25, -402.23) * mm, "mid": v(-542.26, -405.24) * mm, "end": v(-539.25, -408.25) * mm});
            skLineSegment(sketch, "E316", {"start": v(-539.25, -408.25) * mm, "end": v(-520.75, -408.25) * mm});
            skArc(sketch, "E317", {"start": v(-520.75, -408.25) * mm, "mid": v(-517.74, -405.24) * mm, "end": v(-520.75, -402.23) * mm});
            skLineSegment(sketch, "E318", {"start": v(-520.75, -702.23) * mm, "end": v(-520.75, -593.77) * mm});
            skArc(sketch, "E319", {"start": v(-520.75, -593.77) * mm, "mid": v(-517.74, -590.76) * mm, "end": v(-520.75, -587.75) * mm});
            skLineSegment(sketch, "E320", {"start": v(-520.75, -587.75) * mm, "end": v(-539.25, -587.75) * mm});
            skArc(sketch, "E321", {"start": v(-539.25, -587.75) * mm, "mid": v(-542.26, -590.76) * mm, "end": v(-539.25, -593.77) * mm});
            skLineSegment(sketch, "E322", {"start": v(-539.25, -593.77) * mm, "end": v(-539.25, -702.23) * mm});
            skArc(sketch, "E323", {"start": v(-539.25, -702.23) * mm, "mid": v(-542.26, -705.24) * mm, "end": v(-539.25, -708.25) * mm});
            skLineSegment(sketch, "E324", {"start": v(-539.25, -708.25) * mm, "end": v(-520.75, -708.25) * mm});
            skArc(sketch, "E325", {"start": v(-520.75, -708.25) * mm, "mid": v(-517.74, -705.24) * mm, "end": v(-520.75, -702.23) * mm});
            skLineSegment(sketch, "E326", {"start": v(-388.75, -702.23) * mm, "end": v(-388.75, -593.77) * mm});
            skArc(sketch, "E327", {"start": v(-388.75, -593.77) * mm, "mid": v(-385.74, -590.76) * mm, "end": v(-388.75, -587.75) * mm});
            skLineSegment(sketch, "E328", {"start": v(-388.75, -587.75) * mm, "end": v(-407.25, -587.75) * mm});
            skArc(sketch, "E329", {"start": v(-407.25, -587.75) * mm, "mid": v(-410.26, -590.76) * mm, "end": v(-407.25, -593.77) * mm});
            skLineSegment(sketch, "E330", {"start": v(-407.25, -593.77) * mm, "end": v(-407.25, -702.23) * mm});
            skArc(sketch, "E331", {"start": v(-407.25, -702.23) * mm, "mid": v(-410.26, -705.24) * mm, "end": v(-407.25, -708.25) * mm});
            skLineSegment(sketch, "E332", {"start": v(-407.25, -708.25) * mm, "end": v(-388.75, -708.25) * mm});
            skArc(sketch, "E333", {"start": v(-388.75, -708.25) * mm, "mid": v(-385.74, -705.24) * mm, "end": v(-388.75, -702.23) * mm});
            skLineSegment(sketch, "E334", {"start": v(-407.25, -293.76) * mm, "end": v(-407.25, -402.23) * mm});
            skArc(sketch, "E335", {"start": v(-407.25, -402.23) * mm, "mid": v(-410.26, -405.24) * mm, "end": v(-407.25, -408.25) * mm});
            skLineSegment(sketch, "E336", {"start": v(-407.25, -408.25) * mm, "end": v(-388.75, -408.25) * mm});
            skArc(sketch, "E337", {"start": v(-388.75, -408.25) * mm, "mid": v(-385.74, -405.24) * mm, "end": v(-388.75, -402.23) * mm});
            skLineSegment(sketch, "E338", {"start": v(-388.75, -402.23) * mm, "end": v(-388.75, -293.76) * mm});
            skArc(sketch, "E339", {"start": v(-388.75, -293.76) * mm, "mid": v(-385.74, -290.75) * mm, "end": v(-388.75, -287.74) * mm});
            skLineSegment(sketch, "E340", {"start": v(-388.75, -287.74) * mm, "end": v(-407.25, -287.74) * mm});
            skArc(sketch, "E341", {"start": v(-407.25, -287.74) * mm, "mid": v(-410.26, -290.75) * mm, "end": v(-407.25, -293.76) * mm});
            skLineSegment(sketch, "E342", {"start": v(-407.25, 306.24) * mm, "end": v(-407.25, 197.78) * mm});
            skArc(sketch, "E343", {"start": v(-407.25, 197.78) * mm, "mid": v(-410.26, 194.77) * mm, "end": v(-407.25, 191.76) * mm});
            skLineSegment(sketch, "E344", {"start": v(-407.25, 191.76) * mm, "end": v(-388.75, 191.76) * mm});
            skArc(sketch, "E345", {"start": v(-388.75, 191.76) * mm, "mid": v(-385.74, 194.77) * mm, "end": v(-388.75, 197.78) * mm});
            skLineSegment(sketch, "E346", {"start": v(-388.75, 197.78) * mm, "end": v(-388.75, 306.24) * mm});
            skArc(sketch, "E347", {"start": v(-388.75, 306.24) * mm, "mid": v(-385.74, 309.25) * mm, "end": v(-388.75, 312.26) * mm});
            skLineSegment(sketch, "E348", {"start": v(-388.75, 312.26) * mm, "end": v(-407.25, 312.26) * mm});
            skArc(sketch, "E349", {"start": v(-407.25, 312.26) * mm, "mid": v(-410.26, 309.25) * mm, "end": v(-407.25, 306.24) * mm});
            skLineSegment(sketch, "E350", {"start": v(-539.25, -1008.25) * mm, "end": v(-520.75, -1008.25) * mm});
            skArc(sketch, "E351", {"start": v(-520.75, -1008.25) * mm, "mid": v(-517.74, -1005.24) * mm, "end": v(-520.75, -1002.23) * mm});
            skLineSegment(sketch, "E352", {"start": v(-520.75, -1002.23) * mm, "end": v(-520.75, -893.77) * mm});
            skArc(sketch, "E353", {"start": v(-520.75, -893.77) * mm, "mid": v(-517.74, -890.76) * mm, "end": v(-520.75, -887.75) * mm});
            skLineSegment(sketch, "E354", {"start": v(-520.75, -887.75) * mm, "end": v(-539.25, -887.75) * mm});
            skArc(sketch, "E355", {"start": v(-539.25, -887.75) * mm, "mid": v(-542.26, -890.76) * mm, "end": v(-539.25, -893.77) * mm});
            skLineSegment(sketch, "E356", {"start": v(-539.25, -893.77) * mm, "end": v(-539.25, -1002.23) * mm});
            skArc(sketch, "E357", {"start": v(-539.25, -1002.23) * mm, "mid": v(-542.26, -1005.24) * mm, "end": v(-539.25, -1008.25) * mm});
            skLineSegment(sketch, "E358", {"start": v(-388.75, -102.22) * mm, "end": v(-388.75, 6.24) * mm});
            skArc(sketch, "E359", {"start": v(-388.75, 6.24) * mm, "mid": v(-385.74, 9.25) * mm, "end": v(-388.75, 12.26) * mm});
            skLineSegment(sketch, "E360", {"start": v(-388.75, 12.26) * mm, "end": v(-407.25, 12.26) * mm});
            skArc(sketch, "E361", {"start": v(-407.25, 12.26) * mm, "mid": v(-410.26, 9.25) * mm, "end": v(-407.25, 6.24) * mm});
            skLineSegment(sketch, "E362", {"start": v(-407.25, 6.24) * mm, "end": v(-407.25, -38.74) * mm});
            skLineSegment(sketch, "E363", {"start": v(-407.25, -38.74) * mm, "end": v(-432.23, -38.74) * mm});
            skArc(sketch, "E364", {"start": v(-432.23, -38.74) * mm, "mid": v(-435.24, -35.73) * mm, "end": v(-438.25, -38.74) * mm});
            skLineSegment(sketch, "E365", {"start": v(-438.25, -38.74) * mm, "end": v(-438.25, -57.24) * mm});
            skArc(sketch, "E366", {"start": v(-438.25, -57.24) * mm, "mid": v(-435.24, -60.25) * mm, "end": v(-432.23, -57.24) * mm});
            skLineSegment(sketch, "E367", {"start": v(-432.23, -57.24) * mm, "end": v(-407.25, -57.24) * mm});
            skLineSegment(sketch, "E368", {"start": v(-407.25, -57.24) * mm, "end": v(-407.25, -102.22) * mm});
            skArc(sketch, "E369", {"start": v(-407.25, -102.22) * mm, "mid": v(-410.26, -105.23) * mm, "end": v(-407.25, -108.24) * mm});
            skLineSegment(sketch, "E370", {"start": v(-407.25, -108.24) * mm, "end": v(-388.75, -108.24) * mm});
            skArc(sketch, "E371", {"start": v(-388.75, -108.24) * mm, "mid": v(-385.74, -105.23) * mm, "end": v(-388.75, -102.22) * mm});
            skLineSegment(sketch, "E372", {"start": v(-148.75, -1002.23) * mm, "end": v(-148.75, -893.77) * mm});
            skArc(sketch, "E373", {"start": v(-148.75, -893.77) * mm, "mid": v(-145.74, -890.76) * mm, "end": v(-148.75, -887.75) * mm});
            skLineSegment(sketch, "E374", {"start": v(-148.75, -887.75) * mm, "end": v(-167.25, -887.75) * mm});
            skArc(sketch, "E375", {"start": v(-167.25, -887.75) * mm, "mid": v(-170.26, -890.76) * mm, "end": v(-167.25, -893.77) * mm});
            skLineSegment(sketch, "E376", {"start": v(-167.25, -893.77) * mm, "end": v(-167.25, -1002.23) * mm});
            skArc(sketch, "E377", {"start": v(-167.25, -1002.23) * mm, "mid": v(-170.26, -1005.24) * mm, "end": v(-167.25, -1008.25) * mm});
            skLineSegment(sketch, "E378", {"start": v(-167.25, -1008.25) * mm, "end": v(-148.75, -1008.25) * mm});
            skArc(sketch, "E379", {"start": v(-148.75, -1008.25) * mm, "mid": v(-145.74, -1005.24) * mm, "end": v(-148.75, -1002.23) * mm});
            skLineSegment(sketch, "E380", {"start": v(-148.75, 497.78) * mm, "end": v(-148.75, 606.24) * mm});
            skArc(sketch, "E381", {"start": v(-148.75, 606.24) * mm, "mid": v(-145.74, 609.25) * mm, "end": v(-148.75, 612.26) * mm});
            skLineSegment(sketch, "E382", {"start": v(-148.75, 612.26) * mm, "end": v(-167.25, 612.26) * mm});
            skArc(sketch, "E383", {"start": v(-167.25, 612.26) * mm, "mid": v(-170.26, 609.25) * mm, "end": v(-167.25, 606.24) * mm});
            skLineSegment(sketch, "E384", {"start": v(-167.25, 606.24) * mm, "end": v(-167.25, 497.78) * mm});
            skArc(sketch, "E385", {"start": v(-167.25, 497.78) * mm, "mid": v(-170.26, 494.77) * mm, "end": v(-167.25, 491.76) * mm});
            skLineSegment(sketch, "E386", {"start": v(-167.25, 491.76) * mm, "end": v(-148.75, 491.76) * mm});
            skArc(sketch, "E387", {"start": v(-148.75, 491.76) * mm, "mid": v(-145.74, 494.77) * mm, "end": v(-148.75, 497.78) * mm});
            skLineSegment(sketch, "E388", {"start": v(-299.25, 606.23) * mm, "end": v(-299.25, 497.77) * mm});
            skArc(sketch, "E389", {"start": v(-299.25, 497.77) * mm, "mid": v(-302.26, 494.76) * mm, "end": v(-299.25, 491.75) * mm});
            skLineSegment(sketch, "E390", {"start": v(-299.25, 491.75) * mm, "end": v(-280.75, 491.75) * mm});
            skArc(sketch, "E391", {"start": v(-280.75, 491.75) * mm, "mid": v(-277.74, 494.76) * mm, "end": v(-280.75, 497.77) * mm});
            skLineSegment(sketch, "E392", {"start": v(-280.75, 497.77) * mm, "end": v(-280.75, 606.23) * mm});
            skArc(sketch, "E393", {"start": v(-280.75, 606.23) * mm, "mid": v(-277.74, 609.24) * mm, "end": v(-280.75, 612.25) * mm});
            skLineSegment(sketch, "E394", {"start": v(-280.75, 612.25) * mm, "end": v(-299.25, 612.25) * mm});
            skArc(sketch, "E395", {"start": v(-299.25, 612.25) * mm, "mid": v(-302.26, 609.24) * mm, "end": v(-299.25, 606.23) * mm});
            skLineSegment(sketch, "E396", {"start": v(-280.75, 197.77) * mm, "end": v(-280.75, 306.23) * mm});
            skArc(sketch, "E397", {"start": v(-280.75, 306.23) * mm, "mid": v(-277.74, 309.24) * mm, "end": v(-280.75, 312.25) * mm});
            skLineSegment(sketch, "E398", {"start": v(-280.75, 312.25) * mm, "end": v(-299.25, 312.25) * mm});
            skArc(sketch, "E399", {"start": v(-299.25, 312.25) * mm, "mid": v(-302.26, 309.24) * mm, "end": v(-299.25, 306.23) * mm});
            skLineSegment(sketch, "E400", {"start": v(-299.25, 306.23) * mm, "end": v(-299.25, 197.77) * mm});
            skArc(sketch, "E401", {"start": v(-299.25, 197.77) * mm, "mid": v(-302.26, 194.76) * mm, "end": v(-299.25, 191.75) * mm});
            skLineSegment(sketch, "E402", {"start": v(-299.25, 191.75) * mm, "end": v(-280.75, 191.75) * mm});
            skArc(sketch, "E403", {"start": v(-280.75, 191.75) * mm, "mid": v(-277.74, 194.76) * mm, "end": v(-280.75, 197.77) * mm});
            skLineSegment(sketch, "E404", {"start": v(-280.75, -38.74) * mm, "end": v(-280.75, 6.24) * mm});
            skArc(sketch, "E405", {"start": v(-280.75, 6.24) * mm, "mid": v(-277.74, 9.25) * mm, "end": v(-280.75, 12.26) * mm});
            skLineSegment(sketch, "E406", {"start": v(-280.75, 12.26) * mm, "end": v(-299.25, 12.26) * mm});
            skArc(sketch, "E407", {"start": v(-299.25, 12.26) * mm, "mid": v(-302.26, 9.25) * mm, "end": v(-299.25, 6.24) * mm});
            skLineSegment(sketch, "E408", {"start": v(-299.25, 6.24) * mm, "end": v(-299.25, -102.22) * mm});
            skArc(sketch, "E409", {"start": v(-299.25, -102.22) * mm, "mid": v(-302.26, -105.23) * mm, "end": v(-299.25, -108.24) * mm});
            skLineSegment(sketch, "E410", {"start": v(-299.25, -108.24) * mm, "end": v(-280.75, -108.24) * mm});
            skArc(sketch, "E411", {"start": v(-280.75, -108.24) * mm, "mid": v(-277.74, -105.23) * mm, "end": v(-280.75, -102.22) * mm});
            skLineSegment(sketch, "E412", {"start": v(-280.75, -102.22) * mm, "end": v(-280.75, -57.24) * mm});
            skLineSegment(sketch, "E413", {"start": v(-280.75, -57.24) * mm, "end": v(-255.77, -57.24) * mm});
            skArc(sketch, "E414", {"start": v(-255.77, -57.24) * mm, "mid": v(-252.76, -60.25) * mm, "end": v(-249.75, -57.24) * mm});
            skLineSegment(sketch, "E415", {"start": v(-249.75, -57.24) * mm, "end": v(-249.75, -38.74) * mm});
            skArc(sketch, "E416", {"start": v(-249.75, -38.74) * mm, "mid": v(-252.76, -35.73) * mm, "end": v(-255.77, -38.74) * mm});
            skLineSegment(sketch, "E417", {"start": v(-255.77, -38.74) * mm, "end": v(-280.75, -38.74) * mm});
            skLineSegment(sketch, "E418", {"start": v(-280.75, -402.23) * mm, "end": v(-280.75, -293.77) * mm});
            skArc(sketch, "E419", {"start": v(-280.75, -293.77) * mm, "mid": v(-277.74, -290.76) * mm, "end": v(-280.75, -287.75) * mm});
            skLineSegment(sketch, "E420", {"start": v(-280.75, -287.75) * mm, "end": v(-299.25, -287.75) * mm});
            skArc(sketch, "E421", {"start": v(-299.25, -287.75) * mm, "mid": v(-302.26, -290.76) * mm, "end": v(-299.25, -293.77) * mm});
            skLineSegment(sketch, "E422", {"start": v(-299.25, -293.77) * mm, "end": v(-299.25, -402.23) * mm});
            skArc(sketch, "E423", {"start": v(-299.25, -402.23) * mm, "mid": v(-302.26, -405.24) * mm, "end": v(-299.25, -408.25) * mm});
            skLineSegment(sketch, "E424", {"start": v(-299.25, -408.25) * mm, "end": v(-280.75, -408.25) * mm});
            skArc(sketch, "E425", {"start": v(-280.75, -408.25) * mm, "mid": v(-277.74, -405.24) * mm, "end": v(-280.75, -402.23) * mm});
            skLineSegment(sketch, "E426", {"start": v(-280.75, -702.23) * mm, "end": v(-280.75, -593.77) * mm});
            skArc(sketch, "E427", {"start": v(-280.75, -593.77) * mm, "mid": v(-277.74, -590.76) * mm, "end": v(-280.75, -587.75) * mm});
            skLineSegment(sketch, "E428", {"start": v(-280.75, -587.75) * mm, "end": v(-299.25, -587.75) * mm});
            skArc(sketch, "E429", {"start": v(-299.25, -587.75) * mm, "mid": v(-302.26, -590.76) * mm, "end": v(-299.25, -593.77) * mm});
            skLineSegment(sketch, "E430", {"start": v(-299.25, -593.77) * mm, "end": v(-299.25, -702.23) * mm});
            skArc(sketch, "E431", {"start": v(-299.25, -702.23) * mm, "mid": v(-302.26, -705.24) * mm, "end": v(-299.25, -708.25) * mm});
            skLineSegment(sketch, "E432", {"start": v(-299.25, -708.25) * mm, "end": v(-280.75, -708.25) * mm});
            skArc(sketch, "E433", {"start": v(-280.75, -708.25) * mm, "mid": v(-277.74, -705.24) * mm, "end": v(-280.75, -702.23) * mm});
            skLineSegment(sketch, "E434", {"start": v(-148.75, -702.23) * mm, "end": v(-148.75, -593.77) * mm});
            skArc(sketch, "E435", {"start": v(-148.75, -593.77) * mm, "mid": v(-145.74, -590.76) * mm, "end": v(-148.75, -587.75) * mm});
            skLineSegment(sketch, "E436", {"start": v(-148.75, -587.75) * mm, "end": v(-167.25, -587.75) * mm});
            skArc(sketch, "E437", {"start": v(-167.25, -587.75) * mm, "mid": v(-170.26, -590.76) * mm, "end": v(-167.25, -593.77) * mm});
            skLineSegment(sketch, "E438", {"start": v(-167.25, -593.77) * mm, "end": v(-167.25, -702.23) * mm});
            skArc(sketch, "E439", {"start": v(-167.25, -702.23) * mm, "mid": v(-170.26, -705.24) * mm, "end": v(-167.25, -708.25) * mm});
            skLineSegment(sketch, "E440", {"start": v(-167.25, -708.25) * mm, "end": v(-148.75, -708.25) * mm});
            skArc(sketch, "E441", {"start": v(-148.75, -708.25) * mm, "mid": v(-145.74, -705.24) * mm, "end": v(-148.75, -702.23) * mm});
            skLineSegment(sketch, "E442", {"start": v(-167.25, -293.76) * mm, "end": v(-167.25, -402.23) * mm});
            skArc(sketch, "E443", {"start": v(-167.25, -402.23) * mm, "mid": v(-170.26, -405.24) * mm, "end": v(-167.25, -408.25) * mm});
            skLineSegment(sketch, "E444", {"start": v(-167.25, -408.25) * mm, "end": v(-148.75, -408.25) * mm});
            skArc(sketch, "E445", {"start": v(-148.75, -408.25) * mm, "mid": v(-145.74, -405.24) * mm, "end": v(-148.75, -402.23) * mm});
            skLineSegment(sketch, "E446", {"start": v(-148.75, -402.23) * mm, "end": v(-148.75, -293.76) * mm});
            skArc(sketch, "E447", {"start": v(-148.75, -293.76) * mm, "mid": v(-145.74, -290.75) * mm, "end": v(-148.75, -287.74) * mm});
            skLineSegment(sketch, "E448", {"start": v(-148.75, -287.74) * mm, "end": v(-167.25, -287.74) * mm});
            skArc(sketch, "E449", {"start": v(-167.25, -287.74) * mm, "mid": v(-170.26, -290.75) * mm, "end": v(-167.25, -293.76) * mm});
            skLineSegment(sketch, "E450", {"start": v(-167.25, 306.24) * mm, "end": v(-167.25, 197.78) * mm});
            skArc(sketch, "E451", {"start": v(-167.25, 197.78) * mm, "mid": v(-170.26, 194.77) * mm, "end": v(-167.25, 191.76) * mm});
            skLineSegment(sketch, "E452", {"start": v(-167.25, 191.76) * mm, "end": v(-148.75, 191.76) * mm});
            skArc(sketch, "E453", {"start": v(-148.75, 191.76) * mm, "mid": v(-145.74, 194.77) * mm, "end": v(-148.75, 197.78) * mm});
            skLineSegment(sketch, "E454", {"start": v(-148.75, 197.78) * mm, "end": v(-148.75, 306.24) * mm});
            skArc(sketch, "E455", {"start": v(-148.75, 306.24) * mm, "mid": v(-145.74, 309.25) * mm, "end": v(-148.75, 312.26) * mm});
            skLineSegment(sketch, "E456", {"start": v(-148.75, 312.26) * mm, "end": v(-167.25, 312.26) * mm});
            skArc(sketch, "E457", {"start": v(-167.25, 312.26) * mm, "mid": v(-170.26, 309.25) * mm, "end": v(-167.25, 306.24) * mm});
            skLineSegment(sketch, "E458", {"start": v(-299.25, -1008.25) * mm, "end": v(-280.75, -1008.25) * mm});
            skArc(sketch, "E459", {"start": v(-280.75, -1008.25) * mm, "mid": v(-277.74, -1005.24) * mm, "end": v(-280.75, -1002.23) * mm});
            skLineSegment(sketch, "E460", {"start": v(-280.75, -1002.23) * mm, "end": v(-280.75, -893.77) * mm});
            skArc(sketch, "E461", {"start": v(-280.75, -893.77) * mm, "mid": v(-277.74, -890.76) * mm, "end": v(-280.75, -887.75) * mm});
            skLineSegment(sketch, "E462", {"start": v(-280.75, -887.75) * mm, "end": v(-299.25, -887.75) * mm});
            skArc(sketch, "E463", {"start": v(-299.25, -887.75) * mm, "mid": v(-302.26, -890.76) * mm, "end": v(-299.25, -893.77) * mm});
            skLineSegment(sketch, "E464", {"start": v(-299.25, -893.77) * mm, "end": v(-299.25, -1002.23) * mm});
            skArc(sketch, "E465", {"start": v(-299.25, -1002.23) * mm, "mid": v(-302.26, -1005.24) * mm, "end": v(-299.25, -1008.25) * mm});
            skLineSegment(sketch, "E466", {"start": v(-148.75, -102.22) * mm, "end": v(-148.75, 6.24) * mm});
            skArc(sketch, "E467", {"start": v(-148.75, 6.24) * mm, "mid": v(-145.74, 9.25) * mm, "end": v(-148.75, 12.26) * mm});
            skLineSegment(sketch, "E468", {"start": v(-148.75, 12.26) * mm, "end": v(-167.25, 12.26) * mm});
            skArc(sketch, "E469", {"start": v(-167.25, 12.26) * mm, "mid": v(-170.26, 9.25) * mm, "end": v(-167.25, 6.24) * mm});
            skLineSegment(sketch, "E470", {"start": v(-167.25, 6.24) * mm, "end": v(-167.25, -38.74) * mm});
            skLineSegment(sketch, "E471", {"start": v(-167.25, -38.74) * mm, "end": v(-192.23, -38.74) * mm});
            skArc(sketch, "E472", {"start": v(-192.23, -38.74) * mm, "mid": v(-195.24, -35.73) * mm, "end": v(-198.25, -38.74) * mm});
            skLineSegment(sketch, "E473", {"start": v(-198.25, -38.74) * mm, "end": v(-198.25, -57.24) * mm});
            skArc(sketch, "E474", {"start": v(-198.25, -57.24) * mm, "mid": v(-195.24, -60.25) * mm, "end": v(-192.23, -57.24) * mm});
            skLineSegment(sketch, "E475", {"start": v(-192.23, -57.24) * mm, "end": v(-167.25, -57.24) * mm});
            skLineSegment(sketch, "E476", {"start": v(-167.25, -57.24) * mm, "end": v(-167.25, -102.22) * mm});
            skArc(sketch, "E477", {"start": v(-167.25, -102.22) * mm, "mid": v(-170.26, -105.23) * mm, "end": v(-167.25, -108.24) * mm});
            skLineSegment(sketch, "E478", {"start": v(-167.25, -108.24) * mm, "end": v(-148.75, -108.24) * mm});
            skArc(sketch, "E479", {"start": v(-148.75, -108.24) * mm, "mid": v(-145.74, -105.23) * mm, "end": v(-148.75, -102.22) * mm});
            skLineSegment(sketch, "E480", {"start": v(-286.06, 637.6) * mm, "end": v(-286.06, 672.56) * mm});
            skLineSegment(sketch, "E481", {"start": v(-286.06, 672.56) * mm, "end": v(-270.7, 672.56) * mm});
            skLineSegment(sketch, "E482", {"start": v(-270.7, 672.56) * mm, "end": v(-270.27, 672.56) * mm});
            skLineSegment(sketch, "E483", {"start": v(-270.27, 672.56) * mm, "end": v(-269.84, 672.53) * mm});
            skLineSegment(sketch, "E484", {"start": v(-269.84, 672.53) * mm, "end": v(-269.41, 672.48) * mm});
            skLineSegment(sketch, "E485", {"start": v(-269.41, 672.48) * mm, "end": v(-268.99, 672.42) * mm});
            skLineSegment(sketch, "E486", {"start": v(-268.99, 672.42) * mm, "end": v(-268.57, 672.33) * mm});
            skLineSegment(sketch, "E487", {"start": v(-268.57, 672.33) * mm, "end": v(-268.16, 672.21) * mm});
            skLineSegment(sketch, "E488", {"start": v(-268.16, 672.21) * mm, "end": v(-267.75, 672.08) * mm});
            skLineSegment(sketch, "E489", {"start": v(-267.75, 672.08) * mm, "end": v(-267.35, 671.93) * mm});
            skLineSegment(sketch, "E490", {"start": v(-267.35, 671.93) * mm, "end": v(-266.97, 671.76) * mm});
            skLineSegment(sketch, "E491", {"start": v(-266.97, 671.76) * mm, "end": v(-266.58, 671.57) * mm});
            skLineSegment(sketch, "E492", {"start": v(-266.58, 671.57) * mm, "end": v(-266.21, 671.35) * mm});
            skLineSegment(sketch, "E493", {"start": v(-266.21, 671.35) * mm, "end": v(-265.85, 671.12) * mm});
            skLineSegment(sketch, "E494", {"start": v(-265.85, 671.12) * mm, "end": v(-265.5, 670.88) * mm});
            skLineSegment(sketch, "E495", {"start": v(-265.5, 670.88) * mm, "end": v(-265.17, 670.6) * mm});
            skLineSegment(sketch, "E496", {"start": v(-265.17, 670.6) * mm, "end": v(-264.85, 670.32) * mm});
            skLineSegment(sketch, "E497", {"start": v(-264.85, 670.32) * mm, "end": v(-264.54, 670.02) * mm});
            skLineSegment(sketch, "E498", {"start": v(-264.54, 670.02) * mm, "end": v(-264.24, 669.71) * mm});
            skLineSegment(sketch, "E499", {"start": v(-264.24, 669.71) * mm, "end": v(-263.96, 669.4) * mm});
            skLineSegment(sketch, "E500", {"start": v(-263.96, 669.4) * mm, "end": v(-263.7, 669.06) * mm});
            skLineSegment(sketch, "E501", {"start": v(-263.7, 669.06) * mm, "end": v(-263.45, 668.71) * mm});
            skLineSegment(sketch, "E502", {"start": v(-263.45, 668.71) * mm, "end": v(-263.22, 668.36) * mm});
            skLineSegment(sketch, "E503", {"start": v(-263.22, 668.36) * mm, "end": v(-263.01, 667.99) * mm});
            skLineSegment(sketch, "E504", {"start": v(-263.01, 667.99) * mm, "end": v(-262.82, 667.61) * mm});
            skLineSegment(sketch, "E505", {"start": v(-262.82, 667.61) * mm, "end": v(-262.65, 667.23) * mm});
            skLineSegment(sketch, "E506", {"start": v(-262.65, 667.23) * mm, "end": v(-262.5, 666.83) * mm});
            skLineSegment(sketch, "E507", {"start": v(-262.5, 666.83) * mm, "end": v(-262.36, 666.43) * mm});
            skLineSegment(sketch, "E508", {"start": v(-262.36, 666.43) * mm, "end": v(-262.25, 666.02) * mm});
            skLineSegment(sketch, "E509", {"start": v(-262.25, 666.02) * mm, "end": v(-262.15, 665.61) * mm});
            skLineSegment(sketch, "E510", {"start": v(-262.15, 665.61) * mm, "end": v(-262.08, 665.2) * mm});
            skLineSegment(sketch, "E511", {"start": v(-262.08, 665.2) * mm, "end": v(-262.03, 664.77) * mm});
            skLineSegment(sketch, "E512", {"start": v(-262.03, 664.77) * mm, "end": v(-262, 664.35) * mm});
            skLineSegment(sketch, "E513", {"start": v(-262, 664.35) * mm, "end": v(-261.98, 663.92) * mm});
            skLineSegment(sketch, "E514", {"start": v(-261.98, 663.92) * mm, "end": v(-261.98, 663.48) * mm});
            skLineSegment(sketch, "E515", {"start": v(-261.98, 663.48) * mm, "end": v(-262, 663.04) * mm});
            skLineSegment(sketch, "E516", {"start": v(-262, 663.04) * mm, "end": v(-262.04, 662.6) * mm});
            skLineSegment(sketch, "E517", {"start": v(-262.04, 662.6) * mm, "end": v(-262.1, 662.18) * mm});
            skLineSegment(sketch, "E518", {"start": v(-262.1, 662.18) * mm, "end": v(-262.2, 661.75) * mm});
            skLineSegment(sketch, "E519", {"start": v(-262.2, 661.75) * mm, "end": v(-262.3, 661.33) * mm});
            skLineSegment(sketch, "E520", {"start": v(-262.3, 661.33) * mm, "end": v(-262.43, 660.92) * mm});
            skLineSegment(sketch, "E521", {"start": v(-262.43, 660.92) * mm, "end": v(-262.58, 660.51) * mm});
            skLineSegment(sketch, "E522", {"start": v(-262.58, 660.51) * mm, "end": v(-262.75, 660.12) * mm});
            skLineSegment(sketch, "E523", {"start": v(-262.75, 660.12) * mm, "end": v(-262.93, 659.73) * mm});
            skLineSegment(sketch, "E524", {"start": v(-262.93, 659.73) * mm, "end": v(-263.14, 659.35) * mm});
            skLineSegment(sketch, "E525", {"start": v(-263.14, 659.35) * mm, "end": v(-263.37, 658.98) * mm});
            skLineSegment(sketch, "E526", {"start": v(-263.37, 658.98) * mm, "end": v(-263.62, 658.62) * mm});
            skLineSegment(sketch, "E527", {"start": v(-263.62, 658.62) * mm, "end": v(-263.88, 658.27) * mm});
            skLineSegment(sketch, "E528", {"start": v(-263.88, 658.27) * mm, "end": v(-264.17, 657.94) * mm});
            skLineSegment(sketch, "E529", {"start": v(-264.17, 657.94) * mm, "end": v(-264.47, 657.62) * mm});
            skLineSegment(sketch, "E530", {"start": v(-264.47, 657.62) * mm, "end": v(-264.78, 657.32) * mm});
            skLineSegment(sketch, "E531", {"start": v(-264.78, 657.32) * mm, "end": v(-265.11, 657.04) * mm});
            skLineSegment(sketch, "E532", {"start": v(-265.11, 657.04) * mm, "end": v(-265.45, 656.77) * mm});
            skLineSegment(sketch, "E533", {"start": v(-265.45, 656.77) * mm, "end": v(-265.8, 656.52) * mm});
            skLineSegment(sketch, "E534", {"start": v(-265.8, 656.52) * mm, "end": v(-266.17, 656.3) * mm});
            skLineSegment(sketch, "E535", {"start": v(-266.17, 656.3) * mm, "end": v(-266.55, 656.08) * mm});
            skLineSegment(sketch, "E536", {"start": v(-266.55, 656.08) * mm, "end": v(-266.93, 655.9) * mm});
            skLineSegment(sketch, "E537", {"start": v(-266.93, 655.9) * mm, "end": v(-267.33, 655.72) * mm});
            skLineSegment(sketch, "E538", {"start": v(-267.33, 655.72) * mm, "end": v(-267.73, 655.57) * mm});
            skLineSegment(sketch, "E539", {"start": v(-267.73, 655.57) * mm, "end": v(-268.14, 655.44) * mm});
            skLineSegment(sketch, "E540", {"start": v(-268.14, 655.44) * mm, "end": v(-268.55, 655.33) * mm});
            skLineSegment(sketch, "E541", {"start": v(-268.55, 655.33) * mm, "end": v(-268.97, 655.24) * mm});
            skLineSegment(sketch, "E542", {"start": v(-268.97, 655.24) * mm, "end": v(-269.4, 655.17) * mm});
            skLineSegment(sketch, "E543", {"start": v(-269.4, 655.17) * mm, "end": v(-269.83, 655.12) * mm});
            skLineSegment(sketch, "E544", {"start": v(-269.83, 655.12) * mm, "end": v(-270.26, 655.1) * mm});
            skLineSegment(sketch, "E545", {"start": v(-270.26, 655.1) * mm, "end": v(-270.7, 655.09) * mm});
            skLineSegment(sketch, "E546", {"start": v(-270.7, 655.09) * mm, "end": v(-286.06, 655.09) * mm});
            skLineSegment(sketch, "E547", {"start": v(-270.7, 655.09) * mm, "end": v(-270.34, 655.08) * mm});
            skLineSegment(sketch, "E548", {"start": v(-270.34, 655.08) * mm, "end": v(-269.98, 655.06) * mm});
            skLineSegment(sketch, "E549", {"start": v(-269.98, 655.06) * mm, "end": v(-269.63, 655.03) * mm});
            skLineSegment(sketch, "E550", {"start": v(-269.63, 655.03) * mm, "end": v(-269.28, 654.97) * mm});
            skLineSegment(sketch, "E551", {"start": v(-269.28, 654.97) * mm, "end": v(-268.93, 654.9) * mm});
            skLineSegment(sketch, "E552", {"start": v(-268.93, 654.9) * mm, "end": v(-268.6, 654.8) * mm});
            skLineSegment(sketch, "E553", {"start": v(-268.6, 654.8) * mm, "end": v(-268.25, 654.7) * mm});
            skLineSegment(sketch, "E554", {"start": v(-268.25, 654.7) * mm, "end": v(-267.92, 654.57) * mm});
            skLineSegment(sketch, "E555", {"start": v(-267.92, 654.57) * mm, "end": v(-267.6, 654.43) * mm});
            skLineSegment(sketch, "E556", {"start": v(-267.6, 654.43) * mm, "end": v(-267.28, 654.27) * mm});
            skLineSegment(sketch, "E557", {"start": v(-267.28, 654.27) * mm, "end": v(-266.98, 654.1) * mm});
            skLineSegment(sketch, "E558", {"start": v(-266.98, 654.1) * mm, "end": v(-266.68, 653.9) * mm});
            skLineSegment(sketch, "E559", {"start": v(-266.68, 653.9) * mm, "end": v(-266.39, 653.7) * mm});
            skLineSegment(sketch, "E560", {"start": v(-266.39, 653.7) * mm, "end": v(-266.1, 653.48) * mm});
            skLineSegment(sketch, "E561", {"start": v(-266.1, 653.48) * mm, "end": v(-265.84, 653.25) * mm});
            skLineSegment(sketch, "E562", {"start": v(-265.84, 653.25) * mm, "end": v(-265.58, 653) * mm});
            skLineSegment(sketch, "E563", {"start": v(-265.58, 653) * mm, "end": v(-265.28, 652.56) * mm});
            skLineSegment(sketch, "E564", {"start": v(-265.28, 652.56) * mm, "end": v(-265, 652.11) * mm});
            skLineSegment(sketch, "E565", {"start": v(-265, 652.11) * mm, "end": v(-264.75, 651.65) * mm});
            skLineSegment(sketch, "E566", {"start": v(-264.75, 651.65) * mm, "end": v(-264.51, 651.18) * mm});
            skLineSegment(sketch, "E567", {"start": v(-264.51, 651.18) * mm, "end": v(-264.3, 650.7) * mm});
            skLineSegment(sketch, "E568", {"start": v(-264.3, 650.7) * mm, "end": v(-264.1, 650.22) * mm});
            skLineSegment(sketch, "E569", {"start": v(-264.1, 650.22) * mm, "end": v(-263.94, 649.72) * mm});
            skLineSegment(sketch, "E570", {"start": v(-263.94, 649.72) * mm, "end": v(-263.79, 649.22) * mm});
            skLineSegment(sketch, "E571", {"start": v(-263.79, 649.22) * mm, "end": v(-263.66, 648.71) * mm});
            skLineSegment(sketch, "E572", {"start": v(-263.66, 648.71) * mm, "end": v(-263.56, 648.2) * mm});
            skLineSegment(sketch, "E573", {"start": v(-263.56, 648.2) * mm, "end": v(-263.48, 647.68) * mm});
            skLineSegment(sketch, "E574", {"start": v(-263.48, 647.68) * mm, "end": v(-263.42, 647.16) * mm});
            skLineSegment(sketch, "E575", {"start": v(-263.42, 647.16) * mm, "end": v(-263.39, 646.63) * mm});
            skLineSegment(sketch, "E576", {"start": v(-263.39, 646.63) * mm, "end": v(-263.38, 646.1) * mm});
            skLineSegment(sketch, "E577", {"start": v(-263.38, 646.1) * mm, "end": v(-263.39, 645.58) * mm});
            skLineSegment(sketch, "E578", {"start": v(-263.39, 645.58) * mm, "end": v(-263.43, 645.05) * mm});
            skLineSegment(sketch, "E579", {"start": v(-263.43, 645.05) * mm, "end": v(-263.43, 644.58) * mm});
            skLineSegment(sketch, "E580", {"start": v(-263.43, 644.58) * mm, "end": v(-263.43, 644.1) * mm});
            skLineSegment(sketch, "E581", {"start": v(-263.43, 644.1) * mm, "end": v(-263.42, 643.64) * mm});
            skLineSegment(sketch, "E582", {"start": v(-263.42, 643.64) * mm, "end": v(-263.4, 643.17) * mm});
            skLineSegment(sketch, "E583", {"start": v(-263.4, 643.17) * mm, "end": v(-263.38, 642.7) * mm});
            skLineSegment(sketch, "E584", {"start": v(-263.38, 642.7) * mm, "end": v(-263.34, 642.23) * mm});
            skLineSegment(sketch, "E585", {"start": v(-263.34, 642.23) * mm, "end": v(-263.3, 641.76) * mm});
            skLineSegment(sketch, "E586", {"start": v(-263.3, 641.76) * mm, "end": v(-263.24, 641.3) * mm});
            skLineSegment(sketch, "E587", {"start": v(-263.24, 641.3) * mm, "end": v(-263.18, 640.82) * mm});
            skLineSegment(sketch, "E588", {"start": v(-263.18, 640.82) * mm, "end": v(-263.11, 640.36) * mm});
            skLineSegment(sketch, "E589", {"start": v(-263.11, 640.36) * mm, "end": v(-263.04, 639.9) * mm});
            skLineSegment(sketch, "E590", {"start": v(-263.04, 639.9) * mm, "end": v(-262.95, 639.43) * mm});
            skLineSegment(sketch, "E591", {"start": v(-262.95, 639.43) * mm, "end": v(-262.86, 638.97) * mm});
            skLineSegment(sketch, "E592", {"start": v(-262.86, 638.97) * mm, "end": v(-262.75, 638.5) * mm});
            skLineSegment(sketch, "E593", {"start": v(-262.75, 638.5) * mm, "end": v(-262.64, 638.05) * mm});
            skLineSegment(sketch, "E594", {"start": v(-262.64, 638.05) * mm, "end": v(-262.52, 637.6) * mm});
            skLineSegment(sketch, "E595", {"start": v(-239.86, 637.1) * mm, "end": v(-240.22, 637.1) * mm});
            skLineSegment(sketch, "E596", {"start": v(-240.22, 637.1) * mm, "end": v(-240.6, 637.1) * mm});
            skLineSegment(sketch, "E597", {"start": v(-240.6, 637.1) * mm, "end": v(-240.96, 637.12) * mm});
            skLineSegment(sketch, "E598", {"start": v(-240.96, 637.12) * mm, "end": v(-241.32, 637.15) * mm});
            skLineSegment(sketch, "E599", {"start": v(-241.32, 637.15) * mm, "end": v(-241.68, 637.18) * mm});
            skLineSegment(sketch, "E600", {"start": v(-241.68, 637.18) * mm, "end": v(-242.05, 637.23) * mm});
            skLineSegment(sketch, "E601", {"start": v(-242.05, 637.23) * mm, "end": v(-242.4, 637.28) * mm});
            skLineSegment(sketch, "E602", {"start": v(-242.4, 637.28) * mm, "end": v(-242.77, 637.34) * mm});
            skLineSegment(sketch, "E603", {"start": v(-242.77, 637.34) * mm, "end": v(-243.12, 637.4) * mm});
            skLineSegment(sketch, "E604", {"start": v(-243.12, 637.4) * mm, "end": v(-243.48, 637.49) * mm});
            skLineSegment(sketch, "E605", {"start": v(-243.48, 637.49) * mm, "end": v(-243.83, 637.57) * mm});
            skLineSegment(sketch, "E606", {"start": v(-243.83, 637.57) * mm, "end": v(-244.18, 637.67) * mm});
            skLineSegment(sketch, "E607", {"start": v(-244.18, 637.67) * mm, "end": v(-244.52, 637.77) * mm});
            skLineSegment(sketch, "E608", {"start": v(-244.52, 637.77) * mm, "end": v(-244.87, 637.89) * mm});
            skLineSegment(sketch, "E609", {"start": v(-244.87, 637.89) * mm, "end": v(-245.2, 638) * mm});
            skLineSegment(sketch, "E610", {"start": v(-245.2, 638) * mm, "end": v(-245.55, 638.14) * mm});
            skLineSegment(sketch, "E611", {"start": v(-245.55, 638.14) * mm, "end": v(-245.88, 638.28) * mm});
            skLineSegment(sketch, "E612", {"start": v(-245.88, 638.28) * mm, "end": v(-246.21, 638.42) * mm});
            skLineSegment(sketch, "E613", {"start": v(-246.21, 638.42) * mm, "end": v(-246.54, 638.58) * mm});
            skLineSegment(sketch, "E614", {"start": v(-246.54, 638.58) * mm, "end": v(-246.86, 638.74) * mm});
            skLineSegment(sketch, "E615", {"start": v(-246.86, 638.74) * mm, "end": v(-247.18, 638.91) * mm});
            skLineSegment(sketch, "E616", {"start": v(-247.18, 638.91) * mm, "end": v(-247.5, 639.09) * mm});
            skLineSegment(sketch, "E617", {"start": v(-247.5, 639.09) * mm, "end": v(-247.8, 639.28) * mm});
            skLineSegment(sketch, "E618", {"start": v(-247.8, 639.28) * mm, "end": v(-248.12, 639.47) * mm});
            skLineSegment(sketch, "E619", {"start": v(-248.12, 639.47) * mm, "end": v(-248.42, 639.67) * mm});
            skLineSegment(sketch, "E620", {"start": v(-248.42, 639.67) * mm, "end": v(-248.72, 639.88) * mm});
            skLineSegment(sketch, "E621", {"start": v(-248.72, 639.88) * mm, "end": v(-249, 640.1) * mm});
            skLineSegment(sketch, "E622", {"start": v(-249, 640.1) * mm, "end": v(-249.3, 640.33) * mm});
            skLineSegment(sketch, "E623", {"start": v(-249.3, 640.33) * mm, "end": v(-249.58, 640.56) * mm});
            skLineSegment(sketch, "E624", {"start": v(-249.58, 640.56) * mm, "end": v(-249.85, 640.8) * mm});
            skLineSegment(sketch, "E625", {"start": v(-249.85, 640.8) * mm, "end": v(-250.12, 641.05) * mm});
            skLineSegment(sketch, "E626", {"start": v(-250.12, 641.05) * mm, "end": v(-250.39, 641.3) * mm});
            skLineSegment(sketch, "E627", {"start": v(-250.39, 641.3) * mm, "end": v(-250.7, 641.63) * mm});
            skLineSegment(sketch, "E628", {"start": v(-250.7, 641.63) * mm, "end": v(-251, 641.97) * mm});
            skLineSegment(sketch, "E629", {"start": v(-251, 641.97) * mm, "end": v(-251.28, 642.32) * mm});
            skLineSegment(sketch, "E630", {"start": v(-251.28, 642.32) * mm, "end": v(-251.56, 642.67) * mm});
            skLineSegment(sketch, "E631", {"start": v(-251.56, 642.67) * mm, "end": v(-251.83, 643.03) * mm});
            skLineSegment(sketch, "E632", {"start": v(-251.83, 643.03) * mm, "end": v(-252.09, 643.4) * mm});
            skLineSegment(sketch, "E633", {"start": v(-252.09, 643.4) * mm, "end": v(-252.34, 643.77) * mm});
            skLineSegment(sketch, "E634", {"start": v(-252.34, 643.77) * mm, "end": v(-252.58, 644.14) * mm});
            skLineSegment(sketch, "E635", {"start": v(-252.58, 644.14) * mm, "end": v(-252.81, 644.53) * mm});
            skLineSegment(sketch, "E636", {"start": v(-252.81, 644.53) * mm, "end": v(-253.03, 644.91) * mm});
            skLineSegment(sketch, "E637", {"start": v(-253.03, 644.91) * mm, "end": v(-253.24, 645.3) * mm});
            skLineSegment(sketch, "E638", {"start": v(-253.24, 645.3) * mm, "end": v(-253.45, 645.7) * mm});
            skLineSegment(sketch, "E639", {"start": v(-253.45, 645.7) * mm, "end": v(-253.64, 646.1) * mm});
            skLineSegment(sketch, "E640", {"start": v(-253.64, 646.1) * mm, "end": v(-253.82, 646.51) * mm});
            skLineSegment(sketch, "E641", {"start": v(-253.82, 646.51) * mm, "end": v(-254, 646.93) * mm});
            skLineSegment(sketch, "E642", {"start": v(-254, 646.93) * mm, "end": v(-254.16, 647.34) * mm});
            skLineSegment(sketch, "E643", {"start": v(-254.16, 647.34) * mm, "end": v(-254.3, 647.76) * mm});
            skLineSegment(sketch, "E644", {"start": v(-254.3, 647.76) * mm, "end": v(-254.45, 648.18) * mm});
            skLineSegment(sketch, "E645", {"start": v(-254.45, 648.18) * mm, "end": v(-254.58, 648.6) * mm});
            skLineSegment(sketch, "E646", {"start": v(-254.58, 648.6) * mm, "end": v(-254.7, 649.04) * mm});
            skLineSegment(sketch, "E647", {"start": v(-254.7, 649.04) * mm, "end": v(-254.81, 649.47) * mm});
            skLineSegment(sketch, "E648", {"start": v(-254.81, 649.47) * mm, "end": v(-254.91, 649.9) * mm});
            skLineSegment(sketch, "E649", {"start": v(-254.91, 649.9) * mm, "end": v(-255, 650.34) * mm});
            skLineSegment(sketch, "E650", {"start": v(-255, 650.34) * mm, "end": v(-255.08, 650.78) * mm});
            skLineSegment(sketch, "E651", {"start": v(-255.08, 650.78) * mm, "end": v(-255.15, 651.22) * mm});
            skLineSegment(sketch, "E652", {"start": v(-255.15, 651.22) * mm, "end": v(-255.2, 651.67) * mm});
            skLineSegment(sketch, "E653", {"start": v(-255.2, 651.67) * mm, "end": v(-255.25, 652.11) * mm});
            skLineSegment(sketch, "E654", {"start": v(-255.25, 652.11) * mm, "end": v(-255.29, 652.56) * mm});
            skLineSegment(sketch, "E655", {"start": v(-255.29, 652.56) * mm, "end": v(-255.3, 653.01) * mm});
            skLineSegment(sketch, "E656", {"start": v(-255.3, 653.01) * mm, "end": v(-255.32, 653.46) * mm});
            skLineSegment(sketch, "E657", {"start": v(-255.32, 653.46) * mm, "end": v(-255.32, 653.91) * mm});
            skLineSegment(sketch, "E658", {"start": v(-255.32, 653.91) * mm, "end": v(-255.31, 654.37) * mm});
            skLineSegment(sketch, "E659", {"start": v(-255.31, 654.37) * mm, "end": v(-255.33, 654.86) * mm});
            skLineSegment(sketch, "E660", {"start": v(-255.33, 654.86) * mm, "end": v(-255.33, 655.35) * mm});
            skLineSegment(sketch, "E661", {"start": v(-255.33, 655.35) * mm, "end": v(-255.32, 655.84) * mm});
            skLineSegment(sketch, "E662", {"start": v(-255.32, 655.84) * mm, "end": v(-255.3, 656.32) * mm});
            skLineSegment(sketch, "E663", {"start": v(-255.3, 656.32) * mm, "end": v(-255.26, 656.8) * mm});
            skLineSegment(sketch, "E664", {"start": v(-255.26, 656.8) * mm, "end": v(-255.2, 657.3) * mm});
            skLineSegment(sketch, "E665", {"start": v(-255.2, 657.3) * mm, "end": v(-255.15, 657.78) * mm});
            skLineSegment(sketch, "E666", {"start": v(-255.15, 657.78) * mm, "end": v(-255.08, 658.26) * mm});
            skLineSegment(sketch, "E667", {"start": v(-255.08, 658.26) * mm, "end": v(-255, 658.74) * mm});
            skLineSegment(sketch, "E668", {"start": v(-255, 658.74) * mm, "end": v(-254.9, 659.21) * mm});
            skLineSegment(sketch, "E669", {"start": v(-254.9, 659.21) * mm, "end": v(-254.8, 659.68) * mm});
            skLineSegment(sketch, "E670", {"start": v(-254.8, 659.68) * mm, "end": v(-254.67, 660.15) * mm});
            skLineSegment(sketch, "E671", {"start": v(-254.67, 660.15) * mm, "end": v(-254.54, 660.62) * mm});
            skLineSegment(sketch, "E672", {"start": v(-254.54, 660.62) * mm, "end": v(-254.4, 661.08) * mm});
            skLineSegment(sketch, "E673", {"start": v(-254.4, 661.08) * mm, "end": v(-254.25, 661.54) * mm});
            skLineSegment(sketch, "E674", {"start": v(-254.25, 661.54) * mm, "end": v(-254.08, 662) * mm});
            skLineSegment(sketch, "E675", {"start": v(-254.08, 662) * mm, "end": v(-253.9, 662.45) * mm});
            skLineSegment(sketch, "E676", {"start": v(-253.9, 662.45) * mm, "end": v(-253.72, 662.9) * mm});
            skLineSegment(sketch, "E677", {"start": v(-253.72, 662.9) * mm, "end": v(-253.52, 663.33) * mm});
            skLineSegment(sketch, "E678", {"start": v(-253.52, 663.33) * mm, "end": v(-253.31, 663.77) * mm});
            skLineSegment(sketch, "E679", {"start": v(-253.31, 663.77) * mm, "end": v(-253.1, 664.2) * mm});
            skLineSegment(sketch, "E680", {"start": v(-253.1, 664.2) * mm, "end": v(-252.86, 664.63) * mm});
            skLineSegment(sketch, "E681", {"start": v(-252.86, 664.63) * mm, "end": v(-252.62, 665.05) * mm});
            skLineSegment(sketch, "E682", {"start": v(-252.62, 665.05) * mm, "end": v(-252.37, 665.46) * mm});
            skLineSegment(sketch, "E683", {"start": v(-252.37, 665.46) * mm, "end": v(-252.1, 665.87) * mm});
            skLineSegment(sketch, "E684", {"start": v(-252.1, 665.87) * mm, "end": v(-251.83, 666.28) * mm});
            skLineSegment(sketch, "E685", {"start": v(-251.83, 666.28) * mm, "end": v(-251.55, 666.67) * mm});
            skLineSegment(sketch, "E686", {"start": v(-251.55, 666.67) * mm, "end": v(-251.26, 667.06) * mm});
            skLineSegment(sketch, "E687", {"start": v(-251.26, 667.06) * mm, "end": v(-250.95, 667.44) * mm});
            skLineSegment(sketch, "E688", {"start": v(-250.95, 667.44) * mm, "end": v(-250.64, 667.82) * mm});
            skLineSegment(sketch, "E689", {"start": v(-250.64, 667.82) * mm, "end": v(-250.32, 668.19) * mm});
            skLineSegment(sketch, "E690", {"start": v(-250.32, 668.19) * mm, "end": v(-249.98, 668.55) * mm});
            skLineSegment(sketch, "E691", {"start": v(-249.98, 668.55) * mm, "end": v(-249.73, 668.8) * mm});
            skLineSegment(sketch, "E692", {"start": v(-249.73, 668.8) * mm, "end": v(-249.48, 669.05) * mm});
            skLineSegment(sketch, "E693", {"start": v(-249.48, 669.05) * mm, "end": v(-249.21, 669.29) * mm});
            skLineSegment(sketch, "E694", {"start": v(-249.21, 669.29) * mm, "end": v(-248.95, 669.52) * mm});
            skLineSegment(sketch, "E695", {"start": v(-248.95, 669.52) * mm, "end": v(-248.67, 669.75) * mm});
            skLineSegment(sketch, "E696", {"start": v(-248.67, 669.75) * mm, "end": v(-248.4, 669.96) * mm});
            skLineSegment(sketch, "E697", {"start": v(-248.4, 669.96) * mm, "end": v(-248.11, 670.17) * mm});
            skLineSegment(sketch, "E698", {"start": v(-248.11, 670.17) * mm, "end": v(-247.82, 670.38) * mm});
            skLineSegment(sketch, "E699", {"start": v(-247.82, 670.38) * mm, "end": v(-247.53, 670.57) * mm});
            skLineSegment(sketch, "E700", {"start": v(-247.53, 670.57) * mm, "end": v(-247.23, 670.76) * mm});
            skLineSegment(sketch, "E701", {"start": v(-247.23, 670.76) * mm, "end": v(-246.93, 670.94) * mm});
            skLineSegment(sketch, "E702", {"start": v(-246.93, 670.94) * mm, "end": v(-246.62, 671.1) * mm});
            skLineSegment(sketch, "E703", {"start": v(-246.62, 671.1) * mm, "end": v(-246.31, 671.27) * mm});
            skLineSegment(sketch, "E704", {"start": v(-246.31, 671.27) * mm, "end": v(-246, 671.43) * mm});
            skLineSegment(sketch, "E705", {"start": v(-246, 671.43) * mm, "end": v(-245.68, 671.58) * mm});
            skLineSegment(sketch, "E706", {"start": v(-245.68, 671.58) * mm, "end": v(-245.36, 671.71) * mm});
            skLineSegment(sketch, "E707", {"start": v(-245.36, 671.71) * mm, "end": v(-245.03, 671.85) * mm});
            skLineSegment(sketch, "E708", {"start": v(-245.03, 671.85) * mm, "end": v(-244.7, 671.97) * mm});
            skLineSegment(sketch, "E709", {"start": v(-244.7, 671.97) * mm, "end": v(-244.37, 672.08) * mm});
            skLineSegment(sketch, "E710", {"start": v(-244.37, 672.08) * mm, "end": v(-244.03, 672.19) * mm});
            skLineSegment(sketch, "E711", {"start": v(-244.03, 672.19) * mm, "end": v(-243.7, 672.29) * mm});
            skLineSegment(sketch, "E712", {"start": v(-243.7, 672.29) * mm, "end": v(-243.36, 672.37) * mm});
            skLineSegment(sketch, "E713", {"start": v(-243.36, 672.37) * mm, "end": v(-243.01, 672.45) * mm});
            skLineSegment(sketch, "E714", {"start": v(-243.01, 672.45) * mm, "end": v(-242.67, 672.52) * mm});
            skLineSegment(sketch, "E715", {"start": v(-242.67, 672.52) * mm, "end": v(-242.32, 672.59) * mm});
            skLineSegment(sketch, "E716", {"start": v(-242.32, 672.59) * mm, "end": v(-241.97, 672.64) * mm});
            skLineSegment(sketch, "E717", {"start": v(-241.97, 672.64) * mm, "end": v(-241.62, 672.69) * mm});
            skLineSegment(sketch, "E718", {"start": v(-241.62, 672.69) * mm, "end": v(-241.27, 672.72) * mm});
            skLineSegment(sketch, "E719", {"start": v(-241.27, 672.72) * mm, "end": v(-240.92, 672.75) * mm});
            skLineSegment(sketch, "E720", {"start": v(-240.92, 672.75) * mm, "end": v(-240.56, 672.76) * mm});
            skLineSegment(sketch, "E721", {"start": v(-240.56, 672.76) * mm, "end": v(-240.2, 672.77) * mm});
            skLineSegment(sketch, "E722", {"start": v(-240.2, 672.77) * mm, "end": v(-239.85, 672.77) * mm});
            skLineSegment(sketch, "E723", {"start": v(-239.85, 672.77) * mm, "end": v(-239.49, 672.77) * mm});
            skLineSegment(sketch, "E724", {"start": v(-239.49, 672.77) * mm, "end": v(-239.13, 672.75) * mm});
            skLineSegment(sketch, "E725", {"start": v(-239.13, 672.75) * mm, "end": v(-238.77, 672.73) * mm});
            skLineSegment(sketch, "E726", {"start": v(-238.77, 672.73) * mm, "end": v(-238.4, 672.7) * mm});
            skLineSegment(sketch, "E727", {"start": v(-238.4, 672.7) * mm, "end": v(-238.05, 672.66) * mm});
            skLineSegment(sketch, "E728", {"start": v(-238.05, 672.66) * mm, "end": v(-237.7, 672.61) * mm});
            skLineSegment(sketch, "E729", {"start": v(-237.7, 672.61) * mm, "end": v(-237.34, 672.55) * mm});
            skLineSegment(sketch, "E730", {"start": v(-237.34, 672.55) * mm, "end": v(-236.99, 672.48) * mm});
            skLineSegment(sketch, "E731", {"start": v(-236.99, 672.48) * mm, "end": v(-236.64, 672.4) * mm});
            skLineSegment(sketch, "E732", {"start": v(-236.64, 672.4) * mm, "end": v(-236.3, 672.32) * mm});
            skLineSegment(sketch, "E733", {"start": v(-236.3, 672.32) * mm, "end": v(-235.95, 672.23) * mm});
            skLineSegment(sketch, "E734", {"start": v(-235.95, 672.23) * mm, "end": v(-235.6, 672.12) * mm});
            skLineSegment(sketch, "E735", {"start": v(-235.6, 672.12) * mm, "end": v(-235.27, 672.01) * mm});
            skLineSegment(sketch, "E736", {"start": v(-235.27, 672.01) * mm, "end": v(-234.93, 671.9) * mm});
            skLineSegment(sketch, "E737", {"start": v(-234.93, 671.9) * mm, "end": v(-234.6, 671.76) * mm});
            skLineSegment(sketch, "E738", {"start": v(-234.6, 671.76) * mm, "end": v(-234.27, 671.63) * mm});
            skLineSegment(sketch, "E739", {"start": v(-234.27, 671.63) * mm, "end": v(-233.94, 671.48) * mm});
            skLineSegment(sketch, "E740", {"start": v(-233.94, 671.48) * mm, "end": v(-233.62, 671.33) * mm});
            skLineSegment(sketch, "E741", {"start": v(-233.62, 671.33) * mm, "end": v(-233.3, 671.17) * mm});
            skLineSegment(sketch, "E742", {"start": v(-233.3, 671.17) * mm, "end": v(-232.99, 671) * mm});
            skLineSegment(sketch, "E743", {"start": v(-232.99, 671) * mm, "end": v(-232.68, 670.82) * mm});
            skLineSegment(sketch, "E744", {"start": v(-232.68, 670.82) * mm, "end": v(-232.37, 670.63) * mm});
            skLineSegment(sketch, "E745", {"start": v(-232.37, 670.63) * mm, "end": v(-232.07, 670.44) * mm});
            skLineSegment(sketch, "E746", {"start": v(-232.07, 670.44) * mm, "end": v(-231.78, 670.24) * mm});
            skLineSegment(sketch, "E747", {"start": v(-231.78, 670.24) * mm, "end": v(-231.49, 670.03) * mm});
            skLineSegment(sketch, "E748", {"start": v(-231.49, 670.03) * mm, "end": v(-231.2, 669.81) * mm});
            skLineSegment(sketch, "E749", {"start": v(-231.2, 669.81) * mm, "end": v(-230.92, 669.59) * mm});
            skLineSegment(sketch, "E750", {"start": v(-230.92, 669.59) * mm, "end": v(-230.65, 669.35) * mm});
            skLineSegment(sketch, "E751", {"start": v(-230.65, 669.35) * mm, "end": v(-230.38, 669.11) * mm});
            skLineSegment(sketch, "E752", {"start": v(-230.38, 669.11) * mm, "end": v(-230.11, 668.87) * mm});
            skLineSegment(sketch, "E753", {"start": v(-230.11, 668.87) * mm, "end": v(-229.86, 668.61) * mm});
            skLineSegment(sketch, "E754", {"start": v(-229.86, 668.61) * mm, "end": v(-229.6, 668.35) * mm});
            skLineSegment(sketch, "E755", {"start": v(-229.6, 668.35) * mm, "end": v(-229.28, 668) * mm});
            skLineSegment(sketch, "E756", {"start": v(-229.28, 668) * mm, "end": v(-228.97, 667.63) * mm});
            skLineSegment(sketch, "E757", {"start": v(-228.97, 667.63) * mm, "end": v(-228.66, 667.25) * mm});
            skLineSegment(sketch, "E758", {"start": v(-228.66, 667.25) * mm, "end": v(-228.37, 666.87) * mm});
            skLineSegment(sketch, "E759", {"start": v(-228.37, 666.87) * mm, "end": v(-228.08, 666.49) * mm});
            skLineSegment(sketch, "E760", {"start": v(-228.08, 666.49) * mm, "end": v(-227.8, 666.1) * mm});
            skLineSegment(sketch, "E761", {"start": v(-227.8, 666.1) * mm, "end": v(-227.55, 665.7) * mm});
            skLineSegment(sketch, "E762", {"start": v(-227.55, 665.7) * mm, "end": v(-227.3, 665.3) * mm});
            skLineSegment(sketch, "E763", {"start": v(-227.3, 665.3) * mm, "end": v(-227.05, 664.88) * mm});
            skLineSegment(sketch, "E764", {"start": v(-227.05, 664.88) * mm, "end": v(-226.82, 664.46) * mm});
            skLineSegment(sketch, "E765", {"start": v(-226.82, 664.46) * mm, "end": v(-226.6, 664.04) * mm});
            skLineSegment(sketch, "E766", {"start": v(-226.6, 664.04) * mm, "end": v(-226.38, 663.62) * mm});
            skLineSegment(sketch, "E767", {"start": v(-226.38, 663.62) * mm, "end": v(-226.18, 663.18) * mm});
            skLineSegment(sketch, "E768", {"start": v(-226.18, 663.18) * mm, "end": v(-226, 662.75) * mm});
            skLineSegment(sketch, "E769", {"start": v(-226, 662.75) * mm, "end": v(-225.81, 662.3) * mm});
            skLineSegment(sketch, "E770", {"start": v(-225.81, 662.3) * mm, "end": v(-225.64, 661.86) * mm});
            skLineSegment(sketch, "E771", {"start": v(-225.64, 661.86) * mm, "end": v(-225.49, 661.41) * mm});
            skLineSegment(sketch, "E772", {"start": v(-225.49, 661.41) * mm, "end": v(-225.34, 660.96) * mm});
            skLineSegment(sketch, "E773", {"start": v(-225.34, 660.96) * mm, "end": v(-225.2, 660.5) * mm});
            skLineSegment(sketch, "E774", {"start": v(-225.2, 660.5) * mm, "end": v(-225.08, 660.04) * mm});
            skLineSegment(sketch, "E775", {"start": v(-225.08, 660.04) * mm, "end": v(-224.97, 659.58) * mm});
            skLineSegment(sketch, "E776", {"start": v(-224.97, 659.58) * mm, "end": v(-224.87, 659.11) * mm});
            skLineSegment(sketch, "E777", {"start": v(-224.87, 659.11) * mm, "end": v(-224.78, 658.65) * mm});
            skLineSegment(sketch, "E778", {"start": v(-224.78, 658.65) * mm, "end": v(-224.7, 658.17) * mm});
            skLineSegment(sketch, "E779", {"start": v(-224.7, 658.17) * mm, "end": v(-224.63, 657.7) * mm});
            skLineSegment(sketch, "E780", {"start": v(-224.63, 657.7) * mm, "end": v(-224.58, 657.23) * mm});
            skLineSegment(sketch, "E781", {"start": v(-224.58, 657.23) * mm, "end": v(-224.53, 656.75) * mm});
            skLineSegment(sketch, "E782", {"start": v(-224.53, 656.75) * mm, "end": v(-224.5, 656.27) * mm});
            skLineSegment(sketch, "E783", {"start": v(-224.5, 656.27) * mm, "end": v(-224.48, 655.79) * mm});
            skLineSegment(sketch, "E784", {"start": v(-224.48, 655.79) * mm, "end": v(-224.48, 655.3) * mm});
            skLineSegment(sketch, "E785", {"start": v(-224.48, 655.3) * mm, "end": v(-224.48, 654.83) * mm});
            skLineSegment(sketch, "E786", {"start": v(-224.48, 654.83) * mm, "end": v(-224.5, 654.34) * mm});
            skLineSegment(sketch, "E787", {"start": v(-224.5, 654.34) * mm, "end": v(-224.5, 653.9) * mm});
            skLineSegment(sketch, "E788", {"start": v(-224.5, 653.9) * mm, "end": v(-224.5, 653.44) * mm});
            skLineSegment(sketch, "E789", {"start": v(-224.5, 653.44) * mm, "end": v(-224.51, 653) * mm});
            skLineSegment(sketch, "E790", {"start": v(-224.51, 653) * mm, "end": v(-224.54, 652.55) * mm});
            skLineSegment(sketch, "E791", {"start": v(-224.54, 652.55) * mm, "end": v(-224.58, 652.1) * mm});
            skLineSegment(sketch, "E792", {"start": v(-224.58, 652.1) * mm, "end": v(-224.63, 651.66) * mm});
            skLineSegment(sketch, "E793", {"start": v(-224.63, 651.66) * mm, "end": v(-224.69, 651.22) * mm});
            skLineSegment(sketch, "E794", {"start": v(-224.69, 651.22) * mm, "end": v(-224.76, 650.78) * mm});
            skLineSegment(sketch, "E795", {"start": v(-224.76, 650.78) * mm, "end": v(-224.84, 650.34) * mm});
            skLineSegment(sketch, "E796", {"start": v(-224.84, 650.34) * mm, "end": v(-224.93, 649.9) * mm});
            skLineSegment(sketch, "E797", {"start": v(-224.93, 649.9) * mm, "end": v(-225.03, 649.47) * mm});
            skLineSegment(sketch, "E798", {"start": v(-225.03, 649.47) * mm, "end": v(-225.15, 649.04) * mm});
            skLineSegment(sketch, "E799", {"start": v(-225.15, 649.04) * mm, "end": v(-225.27, 648.62) * mm});
            skLineSegment(sketch, "E800", {"start": v(-225.27, 648.62) * mm, "end": v(-225.4, 648.2) * mm});
            skLineSegment(sketch, "E801", {"start": v(-225.4, 648.2) * mm, "end": v(-225.55, 647.77) * mm});
            skLineSegment(sketch, "E802", {"start": v(-225.55, 647.77) * mm, "end": v(-225.7, 647.36) * mm});
            skLineSegment(sketch, "E803", {"start": v(-225.7, 647.36) * mm, "end": v(-225.88, 646.95) * mm});
            skLineSegment(sketch, "E804", {"start": v(-225.88, 646.95) * mm, "end": v(-226.05, 646.54) * mm});
            skLineSegment(sketch, "E805", {"start": v(-226.05, 646.54) * mm, "end": v(-226.24, 646.14) * mm});
            skLineSegment(sketch, "E806", {"start": v(-226.24, 646.14) * mm, "end": v(-226.43, 645.74) * mm});
            skLineSegment(sketch, "E807", {"start": v(-226.43, 645.74) * mm, "end": v(-226.64, 645.34) * mm});
            skLineSegment(sketch, "E808", {"start": v(-226.64, 645.34) * mm, "end": v(-226.86, 644.96) * mm});
            skLineSegment(sketch, "E809", {"start": v(-226.86, 644.96) * mm, "end": v(-227.08, 644.57) * mm});
            skLineSegment(sketch, "E810", {"start": v(-227.08, 644.57) * mm, "end": v(-227.32, 644.2) * mm});
            skLineSegment(sketch, "E811", {"start": v(-227.32, 644.2) * mm, "end": v(-227.56, 643.82) * mm});
            skLineSegment(sketch, "E812", {"start": v(-227.56, 643.82) * mm, "end": v(-227.82, 643.46) * mm});
            skLineSegment(sketch, "E813", {"start": v(-227.82, 643.46) * mm, "end": v(-228.08, 643.1) * mm});
            skLineSegment(sketch, "E814", {"start": v(-228.08, 643.1) * mm, "end": v(-228.36, 642.74) * mm});
            skLineSegment(sketch, "E815", {"start": v(-228.36, 642.74) * mm, "end": v(-228.64, 642.4) * mm});
            skLineSegment(sketch, "E816", {"start": v(-228.64, 642.4) * mm, "end": v(-228.93, 642.05) * mm});
            skLineSegment(sketch, "E817", {"start": v(-228.93, 642.05) * mm, "end": v(-229.23, 641.72) * mm});
            skLineSegment(sketch, "E818", {"start": v(-229.23, 641.72) * mm, "end": v(-229.54, 641.4) * mm});
            skLineSegment(sketch, "E819", {"start": v(-229.54, 641.4) * mm, "end": v(-229.8, 641.14) * mm});
            skLineSegment(sketch, "E820", {"start": v(-229.8, 641.14) * mm, "end": v(-230.06, 640.89) * mm});
            skLineSegment(sketch, "E821", {"start": v(-230.06, 640.89) * mm, "end": v(-230.33, 640.65) * mm});
            skLineSegment(sketch, "E822", {"start": v(-230.33, 640.65) * mm, "end": v(-230.6, 640.42) * mm});
            skLineSegment(sketch, "E823", {"start": v(-230.6, 640.42) * mm, "end": v(-230.88, 640.19) * mm});
            skLineSegment(sketch, "E824", {"start": v(-230.88, 640.19) * mm, "end": v(-231.17, 639.97) * mm});
            skLineSegment(sketch, "E825", {"start": v(-231.17, 639.97) * mm, "end": v(-231.46, 639.76) * mm});
            skLineSegment(sketch, "E826", {"start": v(-231.46, 639.76) * mm, "end": v(-231.75, 639.56) * mm});
            skLineSegment(sketch, "E827", {"start": v(-231.75, 639.56) * mm, "end": v(-232.05, 639.36) * mm});
            skLineSegment(sketch, "E828", {"start": v(-232.05, 639.36) * mm, "end": v(-232.36, 639.17) * mm});
            skLineSegment(sketch, "E829", {"start": v(-232.36, 639.17) * mm, "end": v(-232.67, 639) * mm});
            skLineSegment(sketch, "E830", {"start": v(-232.67, 639) * mm, "end": v(-232.98, 638.82) * mm});
            skLineSegment(sketch, "E831", {"start": v(-232.98, 638.82) * mm, "end": v(-233.3, 638.65) * mm});
            skLineSegment(sketch, "E832", {"start": v(-233.3, 638.65) * mm, "end": v(-233.61, 638.5) * mm});
            skLineSegment(sketch, "E833", {"start": v(-233.61, 638.5) * mm, "end": v(-233.94, 638.35) * mm});
            skLineSegment(sketch, "E834", {"start": v(-233.94, 638.35) * mm, "end": v(-234.27, 638.2) * mm});
            skLineSegment(sketch, "E835", {"start": v(-234.27, 638.2) * mm, "end": v(-234.6, 638.07) * mm});
            skLineSegment(sketch, "E836", {"start": v(-234.6, 638.07) * mm, "end": v(-234.93, 637.95) * mm});
            skLineSegment(sketch, "E837", {"start": v(-234.93, 637.95) * mm, "end": v(-235.27, 637.83) * mm});
            skLineSegment(sketch, "E838", {"start": v(-235.27, 637.83) * mm, "end": v(-235.6, 637.72) * mm});
            skLineSegment(sketch, "E839", {"start": v(-235.6, 637.72) * mm, "end": v(-235.95, 637.63) * mm});
            skLineSegment(sketch, "E840", {"start": v(-235.95, 637.63) * mm, "end": v(-236.3, 637.53) * mm});
            skLineSegment(sketch, "E841", {"start": v(-236.3, 637.53) * mm, "end": v(-236.65, 637.45) * mm});
            skLineSegment(sketch, "E842", {"start": v(-236.65, 637.45) * mm, "end": v(-237, 637.38) * mm});
            skLineSegment(sketch, "E843", {"start": v(-237, 637.38) * mm, "end": v(-237.35, 637.31) * mm});
            skLineSegment(sketch, "E844", {"start": v(-237.35, 637.31) * mm, "end": v(-237.7, 637.26) * mm});
            skLineSegment(sketch, "E845", {"start": v(-237.7, 637.26) * mm, "end": v(-238.06, 637.2) * mm});
            skLineSegment(sketch, "E846", {"start": v(-238.06, 637.2) * mm, "end": v(-238.42, 637.17) * mm});
            skLineSegment(sketch, "E847", {"start": v(-238.42, 637.17) * mm, "end": v(-238.77, 637.14) * mm});
            skLineSegment(sketch, "E848", {"start": v(-238.77, 637.14) * mm, "end": v(-239.13, 637.12) * mm});
            skLineSegment(sketch, "E849", {"start": v(-239.13, 637.12) * mm, "end": v(-239.5, 637.1) * mm});
            skLineSegment(sketch, "E850", {"start": v(-239.5, 637.1) * mm, "end": v(-239.86, 637.1) * mm});
            skLineSegment(sketch, "E851", {"start": v(-201.14, 637.1) * mm, "end": v(-201.51, 637.1) * mm});
            skLineSegment(sketch, "E852", {"start": v(-201.51, 637.1) * mm, "end": v(-201.88, 637.1) * mm});
            skLineSegment(sketch, "E853", {"start": v(-201.88, 637.1) * mm, "end": v(-202.24, 637.12) * mm});
            skLineSegment(sketch, "E854", {"start": v(-202.24, 637.12) * mm, "end": v(-202.6, 637.15) * mm});
            skLineSegment(sketch, "E855", {"start": v(-202.6, 637.15) * mm, "end": v(-202.97, 637.18) * mm});
            skLineSegment(sketch, "E856", {"start": v(-202.97, 637.18) * mm, "end": v(-203.33, 637.23) * mm});
            skLineSegment(sketch, "E857", {"start": v(-203.33, 637.23) * mm, "end": v(-203.7, 637.28) * mm});
            skLineSegment(sketch, "E858", {"start": v(-203.7, 637.28) * mm, "end": v(-204.05, 637.34) * mm});
            skLineSegment(sketch, "E859", {"start": v(-204.05, 637.34) * mm, "end": v(-204.4, 637.4) * mm});
            skLineSegment(sketch, "E860", {"start": v(-204.4, 637.4) * mm, "end": v(-204.76, 637.49) * mm});
            skLineSegment(sketch, "E861", {"start": v(-204.76, 637.49) * mm, "end": v(-205.11, 637.57) * mm});
            skLineSegment(sketch, "E862", {"start": v(-205.11, 637.57) * mm, "end": v(-205.46, 637.67) * mm});
            skLineSegment(sketch, "E863", {"start": v(-205.46, 637.67) * mm, "end": v(-205.8, 637.77) * mm});
            skLineSegment(sketch, "E864", {"start": v(-205.8, 637.77) * mm, "end": v(-206.15, 637.89) * mm});
            skLineSegment(sketch, "E865", {"start": v(-206.15, 637.89) * mm, "end": v(-206.5, 638) * mm});
            skLineSegment(sketch, "E866", {"start": v(-206.5, 638) * mm, "end": v(-206.83, 638.14) * mm});
            skLineSegment(sketch, "E867", {"start": v(-206.83, 638.14) * mm, "end": v(-207.17, 638.28) * mm});
            skLineSegment(sketch, "E868", {"start": v(-207.17, 638.28) * mm, "end": v(-207.5, 638.42) * mm});
            skLineSegment(sketch, "E869", {"start": v(-207.5, 638.42) * mm, "end": v(-207.83, 638.58) * mm});
            skLineSegment(sketch, "E870", {"start": v(-207.83, 638.58) * mm, "end": v(-208.15, 638.74) * mm});
            skLineSegment(sketch, "E871", {"start": v(-208.15, 638.74) * mm, "end": v(-208.47, 638.91) * mm});
            skLineSegment(sketch, "E872", {"start": v(-208.47, 638.91) * mm, "end": v(-208.78, 639.09) * mm});
            skLineSegment(sketch, "E873", {"start": v(-208.78, 639.09) * mm, "end": v(-209.1, 639.28) * mm});
            skLineSegment(sketch, "E874", {"start": v(-209.1, 639.28) * mm, "end": v(-209.4, 639.47) * mm});
            skLineSegment(sketch, "E875", {"start": v(-209.4, 639.47) * mm, "end": v(-209.7, 639.67) * mm});
            skLineSegment(sketch, "E876", {"start": v(-209.7, 639.67) * mm, "end": v(-210, 639.88) * mm});
            skLineSegment(sketch, "E877", {"start": v(-210, 639.88) * mm, "end": v(-210.3, 640.1) * mm});
            skLineSegment(sketch, "E878", {"start": v(-210.3, 640.1) * mm, "end": v(-210.58, 640.33) * mm});
            skLineSegment(sketch, "E879", {"start": v(-210.58, 640.33) * mm, "end": v(-210.86, 640.56) * mm});
            skLineSegment(sketch, "E880", {"start": v(-210.86, 640.56) * mm, "end": v(-211.14, 640.8) * mm});
            skLineSegment(sketch, "E881", {"start": v(-211.14, 640.8) * mm, "end": v(-211.4, 641.05) * mm});
            skLineSegment(sketch, "E882", {"start": v(-211.4, 641.05) * mm, "end": v(-211.67, 641.3) * mm});
            skLineSegment(sketch, "E883", {"start": v(-211.67, 641.3) * mm, "end": v(-211.98, 641.63) * mm});
            skLineSegment(sketch, "E884", {"start": v(-211.98, 641.63) * mm, "end": v(-212.28, 641.97) * mm});
            skLineSegment(sketch, "E885", {"start": v(-212.28, 641.97) * mm, "end": v(-212.56, 642.32) * mm});
            skLineSegment(sketch, "E886", {"start": v(-212.56, 642.32) * mm, "end": v(-212.84, 642.67) * mm});
            skLineSegment(sketch, "E887", {"start": v(-212.84, 642.67) * mm, "end": v(-213.11, 643.03) * mm});
            skLineSegment(sketch, "E888", {"start": v(-213.11, 643.03) * mm, "end": v(-213.37, 643.4) * mm});
            skLineSegment(sketch, "E889", {"start": v(-213.37, 643.4) * mm, "end": v(-213.62, 643.77) * mm});
            skLineSegment(sketch, "E890", {"start": v(-213.62, 643.77) * mm, "end": v(-213.86, 644.14) * mm});
            skLineSegment(sketch, "E891", {"start": v(-213.86, 644.14) * mm, "end": v(-214.1, 644.53) * mm});
            skLineSegment(sketch, "E892", {"start": v(-214.1, 644.53) * mm, "end": v(-214.32, 644.91) * mm});
            skLineSegment(sketch, "E893", {"start": v(-214.32, 644.91) * mm, "end": v(-214.53, 645.3) * mm});
            skLineSegment(sketch, "E894", {"start": v(-214.53, 645.3) * mm, "end": v(-214.73, 645.7) * mm});
            skLineSegment(sketch, "E895", {"start": v(-214.73, 645.7) * mm, "end": v(-214.92, 646.1) * mm});
            skLineSegment(sketch, "E896", {"start": v(-214.92, 646.1) * mm, "end": v(-215.1, 646.51) * mm});
            skLineSegment(sketch, "E897", {"start": v(-215.1, 646.51) * mm, "end": v(-215.28, 646.93) * mm});
            skLineSegment(sketch, "E898", {"start": v(-215.28, 646.93) * mm, "end": v(-215.44, 647.34) * mm});
            skLineSegment(sketch, "E899", {"start": v(-215.44, 647.34) * mm, "end": v(-215.6, 647.76) * mm});
            skLineSegment(sketch, "E900", {"start": v(-215.6, 647.76) * mm, "end": v(-215.74, 648.18) * mm});
            skLineSegment(sketch, "E901", {"start": v(-215.74, 648.18) * mm, "end": v(-215.87, 648.6) * mm});
            skLineSegment(sketch, "E902", {"start": v(-215.87, 648.6) * mm, "end": v(-215.99, 649.04) * mm});
            skLineSegment(sketch, "E903", {"start": v(-215.99, 649.04) * mm, "end": v(-216.1, 649.47) * mm});
            skLineSegment(sketch, "E904", {"start": v(-216.1, 649.47) * mm, "end": v(-216.2, 649.9) * mm});
            skLineSegment(sketch, "E905", {"start": v(-216.2, 649.9) * mm, "end": v(-216.29, 650.34) * mm});
            skLineSegment(sketch, "E906", {"start": v(-216.29, 650.34) * mm, "end": v(-216.37, 650.78) * mm});
            skLineSegment(sketch, "E907", {"start": v(-216.37, 650.78) * mm, "end": v(-216.43, 651.22) * mm});
            skLineSegment(sketch, "E908", {"start": v(-216.43, 651.22) * mm, "end": v(-216.5, 651.67) * mm});
            skLineSegment(sketch, "E909", {"start": v(-216.5, 651.67) * mm, "end": v(-216.54, 652.11) * mm});
            skLineSegment(sketch, "E910", {"start": v(-216.54, 652.11) * mm, "end": v(-216.57, 652.56) * mm});
            skLineSegment(sketch, "E911", {"start": v(-216.57, 652.56) * mm, "end": v(-216.6, 653.01) * mm});
            skLineSegment(sketch, "E912", {"start": v(-216.6, 653.01) * mm, "end": v(-216.6, 653.46) * mm});
            skLineSegment(sketch, "E913", {"start": v(-216.6, 653.46) * mm, "end": v(-216.6, 653.91) * mm});
            skLineSegment(sketch, "E914", {"start": v(-216.6, 653.91) * mm, "end": v(-216.6, 654.37) * mm});
            skLineSegment(sketch, "E915", {"start": v(-216.6, 654.37) * mm, "end": v(-216.61, 654.86) * mm});
            skLineSegment(sketch, "E916", {"start": v(-216.61, 654.86) * mm, "end": v(-216.61, 655.35) * mm});
            skLineSegment(sketch, "E917", {"start": v(-216.61, 655.35) * mm, "end": v(-216.6, 655.84) * mm});
            skLineSegment(sketch, "E918", {"start": v(-216.6, 655.84) * mm, "end": v(-216.58, 656.32) * mm});
            skLineSegment(sketch, "E919", {"start": v(-216.58, 656.32) * mm, "end": v(-216.54, 656.8) * mm});
            skLineSegment(sketch, "E920", {"start": v(-216.54, 656.8) * mm, "end": v(-216.5, 657.3) * mm});
            skLineSegment(sketch, "E921", {"start": v(-216.5, 657.3) * mm, "end": v(-216.44, 657.78) * mm});
            skLineSegment(sketch, "E922", {"start": v(-216.44, 657.78) * mm, "end": v(-216.36, 658.26) * mm});
            skLineSegment(sketch, "E923", {"start": v(-216.36, 658.26) * mm, "end": v(-216.28, 658.74) * mm});
            skLineSegment(sketch, "E924", {"start": v(-216.28, 658.74) * mm, "end": v(-216.18, 659.21) * mm});
            skLineSegment(sketch, "E925", {"start": v(-216.18, 659.21) * mm, "end": v(-216.08, 659.68) * mm});
            skLineSegment(sketch, "E926", {"start": v(-216.08, 659.68) * mm, "end": v(-215.96, 660.15) * mm});
            skLineSegment(sketch, "E927", {"start": v(-215.96, 660.15) * mm, "end": v(-215.83, 660.62) * mm});
            skLineSegment(sketch, "E928", {"start": v(-215.83, 660.62) * mm, "end": v(-215.69, 661.08) * mm});
            skLineSegment(sketch, "E929", {"start": v(-215.69, 661.08) * mm, "end": v(-215.53, 661.54) * mm});
            skLineSegment(sketch, "E930", {"start": v(-215.53, 661.54) * mm, "end": v(-215.37, 662) * mm});
            skLineSegment(sketch, "E931", {"start": v(-215.37, 662) * mm, "end": v(-215.2, 662.45) * mm});
            skLineSegment(sketch, "E932", {"start": v(-215.2, 662.45) * mm, "end": v(-215, 662.9) * mm});
            skLineSegment(sketch, "E933", {"start": v(-215, 662.9) * mm, "end": v(-214.8, 663.33) * mm});
            skLineSegment(sketch, "E934", {"start": v(-214.8, 663.33) * mm, "end": v(-214.6, 663.77) * mm});
            skLineSegment(sketch, "E935", {"start": v(-214.6, 663.77) * mm, "end": v(-214.38, 664.2) * mm});
            skLineSegment(sketch, "E936", {"start": v(-214.38, 664.2) * mm, "end": v(-214.15, 664.63) * mm});
            skLineSegment(sketch, "E937", {"start": v(-214.15, 664.63) * mm, "end": v(-213.9, 665.05) * mm});
            skLineSegment(sketch, "E938", {"start": v(-213.9, 665.05) * mm, "end": v(-213.66, 665.46) * mm});
            skLineSegment(sketch, "E939", {"start": v(-213.66, 665.46) * mm, "end": v(-213.4, 665.87) * mm});
            skLineSegment(sketch, "E940", {"start": v(-213.4, 665.87) * mm, "end": v(-213.12, 666.28) * mm});
            skLineSegment(sketch, "E941", {"start": v(-213.12, 666.28) * mm, "end": v(-212.84, 666.67) * mm});
            skLineSegment(sketch, "E942", {"start": v(-212.84, 666.67) * mm, "end": v(-212.54, 667.06) * mm});
            skLineSegment(sketch, "E943", {"start": v(-212.54, 667.06) * mm, "end": v(-212.24, 667.44) * mm});
            skLineSegment(sketch, "E944", {"start": v(-212.24, 667.44) * mm, "end": v(-211.92, 667.82) * mm});
            skLineSegment(sketch, "E945", {"start": v(-211.92, 667.82) * mm, "end": v(-211.6, 668.19) * mm});
            skLineSegment(sketch, "E946", {"start": v(-211.6, 668.19) * mm, "end": v(-211.27, 668.55) * mm});
            skLineSegment(sketch, "E947", {"start": v(-211.27, 668.55) * mm, "end": v(-211.02, 668.8) * mm});
            skLineSegment(sketch, "E948", {"start": v(-211.02, 668.8) * mm, "end": v(-210.76, 669.05) * mm});
            skLineSegment(sketch, "E949", {"start": v(-210.76, 669.05) * mm, "end": v(-210.5, 669.29) * mm});
            skLineSegment(sketch, "E950", {"start": v(-210.5, 669.29) * mm, "end": v(-210.23, 669.52) * mm});
            skLineSegment(sketch, "E951", {"start": v(-210.23, 669.52) * mm, "end": v(-209.96, 669.75) * mm});
            skLineSegment(sketch, "E952", {"start": v(-209.96, 669.75) * mm, "end": v(-209.68, 669.96) * mm});
            skLineSegment(sketch, "E953", {"start": v(-209.68, 669.96) * mm, "end": v(-209.4, 670.17) * mm});
            skLineSegment(sketch, "E954", {"start": v(-209.4, 670.17) * mm, "end": v(-209.1, 670.38) * mm});
            skLineSegment(sketch, "E955", {"start": v(-209.1, 670.38) * mm, "end": v(-208.81, 670.57) * mm});
            skLineSegment(sketch, "E956", {"start": v(-208.81, 670.57) * mm, "end": v(-208.52, 670.76) * mm});
            skLineSegment(sketch, "E957", {"start": v(-208.52, 670.76) * mm, "end": v(-208.21, 670.94) * mm});
            skLineSegment(sketch, "E958", {"start": v(-208.21, 670.94) * mm, "end": v(-207.9, 671.1) * mm});
            skLineSegment(sketch, "E959", {"start": v(-207.9, 671.1) * mm, "end": v(-207.6, 671.27) * mm});
            skLineSegment(sketch, "E960", {"start": v(-207.6, 671.27) * mm, "end": v(-207.28, 671.43) * mm});
            skLineSegment(sketch, "E961", {"start": v(-207.28, 671.43) * mm, "end": v(-206.96, 671.58) * mm});
            skLineSegment(sketch, "E962", {"start": v(-206.96, 671.58) * mm, "end": v(-206.64, 671.71) * mm});
            skLineSegment(sketch, "E963", {"start": v(-206.64, 671.71) * mm, "end": v(-206.32, 671.85) * mm});
            skLineSegment(sketch, "E964", {"start": v(-206.32, 671.85) * mm, "end": v(-205.99, 671.97) * mm});
            skLineSegment(sketch, "E965", {"start": v(-205.99, 671.97) * mm, "end": v(-205.66, 672.08) * mm});
            skLineSegment(sketch, "E966", {"start": v(-205.66, 672.08) * mm, "end": v(-205.32, 672.19) * mm});
            skLineSegment(sketch, "E967", {"start": v(-205.32, 672.19) * mm, "end": v(-204.98, 672.29) * mm});
            skLineSegment(sketch, "E968", {"start": v(-204.98, 672.29) * mm, "end": v(-204.64, 672.37) * mm});
            skLineSegment(sketch, "E969", {"start": v(-204.64, 672.37) * mm, "end": v(-204.3, 672.45) * mm});
            skLineSegment(sketch, "E970", {"start": v(-204.3, 672.45) * mm, "end": v(-203.95, 672.52) * mm});
            skLineSegment(sketch, "E971", {"start": v(-203.95, 672.52) * mm, "end": v(-203.6, 672.59) * mm});
            skLineSegment(sketch, "E972", {"start": v(-203.6, 672.59) * mm, "end": v(-203.26, 672.64) * mm});
            skLineSegment(sketch, "E973", {"start": v(-203.26, 672.64) * mm, "end": v(-202.9, 672.69) * mm});
            skLineSegment(sketch, "E974", {"start": v(-202.9, 672.69) * mm, "end": v(-202.56, 672.72) * mm});
            skLineSegment(sketch, "E975", {"start": v(-202.56, 672.72) * mm, "end": v(-202.2, 672.75) * mm});
            skLineSegment(sketch, "E976", {"start": v(-202.2, 672.75) * mm, "end": v(-201.85, 672.76) * mm});
            skLineSegment(sketch, "E977", {"start": v(-201.85, 672.76) * mm, "end": v(-201.5, 672.77) * mm});
            skLineSegment(sketch, "E978", {"start": v(-201.5, 672.77) * mm, "end": v(-201.14, 672.77) * mm});
            skLineSegment(sketch, "E979", {"start": v(-201.14, 672.77) * mm, "end": v(-200.77, 672.77) * mm});
            skLineSegment(sketch, "E980", {"start": v(-200.77, 672.77) * mm, "end": v(-200.41, 672.75) * mm});
            skLineSegment(sketch, "E981", {"start": v(-200.41, 672.75) * mm, "end": v(-200.05, 672.73) * mm});
            skLineSegment(sketch, "E982", {"start": v(-200.05, 672.73) * mm, "end": v(-199.7, 672.7) * mm});
            skLineSegment(sketch, "E983", {"start": v(-199.7, 672.7) * mm, "end": v(-199.34, 672.66) * mm});
            skLineSegment(sketch, "E984", {"start": v(-199.34, 672.66) * mm, "end": v(-198.98, 672.61) * mm});
            skLineSegment(sketch, "E985", {"start": v(-198.98, 672.61) * mm, "end": v(-198.63, 672.55) * mm});
            skLineSegment(sketch, "E986", {"start": v(-198.63, 672.55) * mm, "end": v(-198.27, 672.48) * mm});
            skLineSegment(sketch, "E987", {"start": v(-198.27, 672.48) * mm, "end": v(-197.92, 672.4) * mm});
            skLineSegment(sketch, "E988", {"start": v(-197.92, 672.4) * mm, "end": v(-197.58, 672.32) * mm});
            skLineSegment(sketch, "E989", {"start": v(-197.58, 672.32) * mm, "end": v(-197.23, 672.23) * mm});
            skLineSegment(sketch, "E990", {"start": v(-197.23, 672.23) * mm, "end": v(-196.89, 672.12) * mm});
            skLineSegment(sketch, "E991", {"start": v(-196.89, 672.12) * mm, "end": v(-196.55, 672.01) * mm});
            skLineSegment(sketch, "E992", {"start": v(-196.55, 672.01) * mm, "end": v(-196.21, 671.9) * mm});
            skLineSegment(sketch, "E993", {"start": v(-196.21, 671.9) * mm, "end": v(-195.88, 671.76) * mm});
            skLineSegment(sketch, "E994", {"start": v(-195.88, 671.76) * mm, "end": v(-195.55, 671.63) * mm});
            skLineSegment(sketch, "E995", {"start": v(-195.55, 671.63) * mm, "end": v(-195.23, 671.48) * mm});
            skLineSegment(sketch, "E996", {"start": v(-195.23, 671.48) * mm, "end": v(-194.9, 671.33) * mm});
            skLineSegment(sketch, "E997", {"start": v(-194.9, 671.33) * mm, "end": v(-194.59, 671.17) * mm});
            skLineSegment(sketch, "E998", {"start": v(-194.59, 671.17) * mm, "end": v(-194.27, 671) * mm});
            skLineSegment(sketch, "E999", {"start": v(-194.27, 671) * mm, "end": v(-193.96, 670.82) * mm});
            skLineSegment(sketch, "E1000", {"start": v(-193.96, 670.82) * mm, "end": v(-193.66, 670.63) * mm});
            skLineSegment(sketch, "E1001", {"start": v(-193.66, 670.63) * mm, "end": v(-193.36, 670.44) * mm});
            skLineSegment(sketch, "E1002", {"start": v(-193.36, 670.44) * mm, "end": v(-193.06, 670.24) * mm});
            skLineSegment(sketch, "E1003", {"start": v(-193.06, 670.24) * mm, "end": v(-192.77, 670.03) * mm});
            skLineSegment(sketch, "E1004", {"start": v(-192.77, 670.03) * mm, "end": v(-192.49, 669.81) * mm});
            skLineSegment(sketch, "E1005", {"start": v(-192.49, 669.81) * mm, "end": v(-192.2, 669.59) * mm});
            skLineSegment(sketch, "E1006", {"start": v(-192.2, 669.59) * mm, "end": v(-191.93, 669.35) * mm});
            skLineSegment(sketch, "E1007", {"start": v(-191.93, 669.35) * mm, "end": v(-191.66, 669.11) * mm});
            skLineSegment(sketch, "E1008", {"start": v(-191.66, 669.11) * mm, "end": v(-191.4, 668.87) * mm});
            skLineSegment(sketch, "E1009", {"start": v(-191.4, 668.87) * mm, "end": v(-191.14, 668.61) * mm});
            skLineSegment(sketch, "E1010", {"start": v(-191.14, 668.61) * mm, "end": v(-190.9, 668.35) * mm});
            skLineSegment(sketch, "E1011", {"start": v(-190.9, 668.35) * mm, "end": v(-190.57, 668) * mm});
            skLineSegment(sketch, "E1012", {"start": v(-190.57, 668) * mm, "end": v(-190.25, 667.63) * mm});
            skLineSegment(sketch, "E1013", {"start": v(-190.25, 667.63) * mm, "end": v(-189.95, 667.25) * mm});
            skLineSegment(sketch, "E1014", {"start": v(-189.95, 667.25) * mm, "end": v(-189.65, 666.87) * mm});
            skLineSegment(sketch, "E1015", {"start": v(-189.65, 666.87) * mm, "end": v(-189.37, 666.49) * mm});
            skLineSegment(sketch, "E1016", {"start": v(-189.37, 666.49) * mm, "end": v(-189.1, 666.1) * mm});
            skLineSegment(sketch, "E1017", {"start": v(-189.1, 666.1) * mm, "end": v(-188.83, 665.7) * mm});
            skLineSegment(sketch, "E1018", {"start": v(-188.83, 665.7) * mm, "end": v(-188.58, 665.3) * mm});
            skLineSegment(sketch, "E1019", {"start": v(-188.58, 665.3) * mm, "end": v(-188.33, 664.88) * mm});
            skLineSegment(sketch, "E1020", {"start": v(-188.33, 664.88) * mm, "end": v(-188.1, 664.46) * mm});
            skLineSegment(sketch, "E1021", {"start": v(-188.1, 664.46) * mm, "end": v(-187.88, 664.04) * mm});
            skLineSegment(sketch, "E1022", {"start": v(-187.88, 664.04) * mm, "end": v(-187.67, 663.62) * mm});
            skLineSegment(sketch, "E1023", {"start": v(-187.67, 663.62) * mm, "end": v(-187.47, 663.18) * mm});
            skLineSegment(sketch, "E1024", {"start": v(-187.47, 663.18) * mm, "end": v(-187.28, 662.75) * mm});
            skLineSegment(sketch, "E1025", {"start": v(-187.28, 662.75) * mm, "end": v(-187.1, 662.3) * mm});
            skLineSegment(sketch, "E1026", {"start": v(-187.1, 662.3) * mm, "end": v(-186.93, 661.86) * mm});
            skLineSegment(sketch, "E1027", {"start": v(-186.93, 661.86) * mm, "end": v(-186.77, 661.41) * mm});
            skLineSegment(sketch, "E1028", {"start": v(-186.77, 661.41) * mm, "end": v(-186.62, 660.96) * mm});
            skLineSegment(sketch, "E1029", {"start": v(-186.62, 660.96) * mm, "end": v(-186.49, 660.5) * mm});
            skLineSegment(sketch, "E1030", {"start": v(-186.49, 660.5) * mm, "end": v(-186.37, 660.04) * mm});
            skLineSegment(sketch, "E1031", {"start": v(-186.37, 660.04) * mm, "end": v(-186.25, 659.58) * mm});
            skLineSegment(sketch, "E1032", {"start": v(-186.25, 659.58) * mm, "end": v(-186.15, 659.11) * mm});
            skLineSegment(sketch, "E1033", {"start": v(-186.15, 659.11) * mm, "end": v(-186.06, 658.65) * mm});
            skLineSegment(sketch, "E1034", {"start": v(-186.06, 658.65) * mm, "end": v(-185.98, 658.17) * mm});
            skLineSegment(sketch, "E1035", {"start": v(-185.98, 658.17) * mm, "end": v(-185.92, 657.7) * mm});
            skLineSegment(sketch, "E1036", {"start": v(-185.92, 657.7) * mm, "end": v(-185.86, 657.23) * mm});
            skLineSegment(sketch, "E1037", {"start": v(-185.86, 657.23) * mm, "end": v(-185.82, 656.75) * mm});
            skLineSegment(sketch, "E1038", {"start": v(-185.82, 656.75) * mm, "end": v(-185.79, 656.27) * mm});
            skLineSegment(sketch, "E1039", {"start": v(-185.79, 656.27) * mm, "end": v(-185.77, 655.79) * mm});
            skLineSegment(sketch, "E1040", {"start": v(-185.77, 655.79) * mm, "end": v(-185.76, 655.3) * mm});
            skLineSegment(sketch, "E1041", {"start": v(-185.76, 655.3) * mm, "end": v(-185.77, 654.83) * mm});
            skLineSegment(sketch, "E1042", {"start": v(-185.77, 654.83) * mm, "end": v(-185.78, 654.34) * mm});
            skLineSegment(sketch, "E1043", {"start": v(-185.78, 654.34) * mm, "end": v(-185.78, 653.9) * mm});
            skLineSegment(sketch, "E1044", {"start": v(-185.78, 653.9) * mm, "end": v(-185.78, 653.44) * mm});
            skLineSegment(sketch, "E1045", {"start": v(-185.78, 653.44) * mm, "end": v(-185.8, 653) * mm});
            skLineSegment(sketch, "E1046", {"start": v(-185.8, 653) * mm, "end": v(-185.82, 652.55) * mm});
            skLineSegment(sketch, "E1047", {"start": v(-185.82, 652.55) * mm, "end": v(-185.86, 652.1) * mm});
            skLineSegment(sketch, "E1048", {"start": v(-185.86, 652.1) * mm, "end": v(-185.91, 651.66) * mm});
            skLineSegment(sketch, "E1049", {"start": v(-185.91, 651.66) * mm, "end": v(-185.97, 651.22) * mm});
            skLineSegment(sketch, "E1050", {"start": v(-185.97, 651.22) * mm, "end": v(-186.04, 650.78) * mm});
            skLineSegment(sketch, "E1051", {"start": v(-186.04, 650.78) * mm, "end": v(-186.12, 650.34) * mm});
            skLineSegment(sketch, "E1052", {"start": v(-186.12, 650.34) * mm, "end": v(-186.22, 649.9) * mm});
            skLineSegment(sketch, "E1053", {"start": v(-186.22, 649.9) * mm, "end": v(-186.32, 649.47) * mm});
            skLineSegment(sketch, "E1054", {"start": v(-186.32, 649.47) * mm, "end": v(-186.43, 649.04) * mm});
            skLineSegment(sketch, "E1055", {"start": v(-186.43, 649.04) * mm, "end": v(-186.56, 648.62) * mm});
            skLineSegment(sketch, "E1056", {"start": v(-186.56, 648.62) * mm, "end": v(-186.7, 648.2) * mm});
            skLineSegment(sketch, "E1057", {"start": v(-186.7, 648.2) * mm, "end": v(-186.84, 647.77) * mm});
            skLineSegment(sketch, "E1058", {"start": v(-186.84, 647.77) * mm, "end": v(-187, 647.36) * mm});
            skLineSegment(sketch, "E1059", {"start": v(-187, 647.36) * mm, "end": v(-187.16, 646.95) * mm});
            skLineSegment(sketch, "E1060", {"start": v(-187.16, 646.95) * mm, "end": v(-187.34, 646.54) * mm});
            skLineSegment(sketch, "E1061", {"start": v(-187.34, 646.54) * mm, "end": v(-187.52, 646.14) * mm});
            skLineSegment(sketch, "E1062", {"start": v(-187.52, 646.14) * mm, "end": v(-187.72, 645.74) * mm});
            skLineSegment(sketch, "E1063", {"start": v(-187.72, 645.74) * mm, "end": v(-187.93, 645.34) * mm});
            skLineSegment(sketch, "E1064", {"start": v(-187.93, 645.34) * mm, "end": v(-188.14, 644.96) * mm});
            skLineSegment(sketch, "E1065", {"start": v(-188.14, 644.96) * mm, "end": v(-188.37, 644.57) * mm});
            skLineSegment(sketch, "E1066", {"start": v(-188.37, 644.57) * mm, "end": v(-188.6, 644.2) * mm});
            skLineSegment(sketch, "E1067", {"start": v(-188.6, 644.2) * mm, "end": v(-188.85, 643.82) * mm});
            skLineSegment(sketch, "E1068", {"start": v(-188.85, 643.82) * mm, "end": v(-189.1, 643.46) * mm});
            skLineSegment(sketch, "E1069", {"start": v(-189.1, 643.46) * mm, "end": v(-189.37, 643.1) * mm});
            skLineSegment(sketch, "E1070", {"start": v(-189.37, 643.1) * mm, "end": v(-189.64, 642.74) * mm});
            skLineSegment(sketch, "E1071", {"start": v(-189.64, 642.74) * mm, "end": v(-189.92, 642.4) * mm});
            skLineSegment(sketch, "E1072", {"start": v(-189.92, 642.4) * mm, "end": v(-190.22, 642.05) * mm});
            skLineSegment(sketch, "E1073", {"start": v(-190.22, 642.05) * mm, "end": v(-190.52, 641.72) * mm});
            skLineSegment(sketch, "E1074", {"start": v(-190.52, 641.72) * mm, "end": v(-190.83, 641.4) * mm});
            skLineSegment(sketch, "E1075", {"start": v(-190.83, 641.4) * mm, "end": v(-191.08, 641.14) * mm});
            skLineSegment(sketch, "E1076", {"start": v(-191.08, 641.14) * mm, "end": v(-191.35, 640.89) * mm});
            skLineSegment(sketch, "E1077", {"start": v(-191.35, 640.89) * mm, "end": v(-191.62, 640.65) * mm});
            skLineSegment(sketch, "E1078", {"start": v(-191.62, 640.65) * mm, "end": v(-191.9, 640.42) * mm});
            skLineSegment(sketch, "E1079", {"start": v(-191.9, 640.42) * mm, "end": v(-192.17, 640.19) * mm});
            skLineSegment(sketch, "E1080", {"start": v(-192.17, 640.19) * mm, "end": v(-192.45, 639.97) * mm});
            skLineSegment(sketch, "E1081", {"start": v(-192.45, 639.97) * mm, "end": v(-192.74, 639.76) * mm});
            skLineSegment(sketch, "E1082", {"start": v(-192.74, 639.76) * mm, "end": v(-193.04, 639.56) * mm});
            skLineSegment(sketch, "E1083", {"start": v(-193.04, 639.56) * mm, "end": v(-193.34, 639.36) * mm});
            skLineSegment(sketch, "E1084", {"start": v(-193.34, 639.36) * mm, "end": v(-193.64, 639.17) * mm});
            skLineSegment(sketch, "E1085", {"start": v(-193.64, 639.17) * mm, "end": v(-193.95, 639) * mm});
            skLineSegment(sketch, "E1086", {"start": v(-193.95, 639) * mm, "end": v(-194.26, 638.82) * mm});
            skLineSegment(sketch, "E1087", {"start": v(-194.26, 638.82) * mm, "end": v(-194.58, 638.65) * mm});
            skLineSegment(sketch, "E1088", {"start": v(-194.58, 638.65) * mm, "end": v(-194.9, 638.5) * mm});
            skLineSegment(sketch, "E1089", {"start": v(-194.9, 638.5) * mm, "end": v(-195.22, 638.35) * mm});
            skLineSegment(sketch, "E1090", {"start": v(-195.22, 638.35) * mm, "end": v(-195.55, 638.2) * mm});
            skLineSegment(sketch, "E1091", {"start": v(-195.55, 638.2) * mm, "end": v(-195.88, 638.07) * mm});
            skLineSegment(sketch, "E1092", {"start": v(-195.88, 638.07) * mm, "end": v(-196.22, 637.95) * mm});
            skLineSegment(sketch, "E1093", {"start": v(-196.22, 637.95) * mm, "end": v(-196.55, 637.83) * mm});
            skLineSegment(sketch, "E1094", {"start": v(-196.55, 637.83) * mm, "end": v(-196.9, 637.72) * mm});
            skLineSegment(sketch, "E1095", {"start": v(-196.9, 637.72) * mm, "end": v(-197.24, 637.63) * mm});
            skLineSegment(sketch, "E1096", {"start": v(-197.24, 637.63) * mm, "end": v(-197.58, 637.53) * mm});
            skLineSegment(sketch, "E1097", {"start": v(-197.58, 637.53) * mm, "end": v(-197.93, 637.45) * mm});
            skLineSegment(sketch, "E1098", {"start": v(-197.93, 637.45) * mm, "end": v(-198.28, 637.38) * mm});
            skLineSegment(sketch, "E1099", {"start": v(-198.28, 637.38) * mm, "end": v(-198.63, 637.31) * mm});
            skLineSegment(sketch, "E1100", {"start": v(-198.63, 637.31) * mm, "end": v(-198.99, 637.26) * mm});
            skLineSegment(sketch, "E1101", {"start": v(-198.99, 637.26) * mm, "end": v(-199.34, 637.2) * mm});
            skLineSegment(sketch, "E1102", {"start": v(-199.34, 637.2) * mm, "end": v(-199.7, 637.17) * mm});
            skLineSegment(sketch, "E1103", {"start": v(-199.7, 637.17) * mm, "end": v(-200.06, 637.14) * mm});
            skLineSegment(sketch, "E1104", {"start": v(-200.06, 637.14) * mm, "end": v(-200.42, 637.12) * mm});
            skLineSegment(sketch, "E1105", {"start": v(-200.42, 637.12) * mm, "end": v(-200.78, 637.1) * mm});
            skLineSegment(sketch, "E1106", {"start": v(-200.78, 637.1) * mm, "end": v(-201.14, 637.1) * mm});
            skLineSegment(sketch, "E1107", {"start": v(-177.89, 637.57) * mm, "end": v(-177.89, 672.57) * mm});
            skLineSegment(sketch, "E1108", {"start": v(-177.89, 672.57) * mm, "end": v(-156.13, 672.57) * mm});
            skLineSegment(sketch, "E1109", {"start": v(-177.89, 655.85) * mm, "end": v(-157.7, 655.85) * mm});
            skLineSegment(sketch, "E1110", {"start": v(304.8, 662.71) * mm, "end": v(304.67, 663.1) * mm});
            skLineSegment(sketch, "E1111", {"start": v(304.67, 663.1) * mm, "end": v(304.53, 663.49) * mm});
            skLineSegment(sketch, "E1112", {"start": v(304.53, 663.49) * mm, "end": v(304.38, 663.87) * mm});
            skLineSegment(sketch, "E1113", {"start": v(304.38, 663.87) * mm, "end": v(304.2, 664.25) * mm});
            skLineSegment(sketch, "E1114", {"start": v(304.2, 664.25) * mm, "end": v(304.03, 664.62) * mm});
            skLineSegment(sketch, "E1115", {"start": v(304.03, 664.62) * mm, "end": v(303.84, 664.99) * mm});
            skLineSegment(sketch, "E1116", {"start": v(303.84, 664.99) * mm, "end": v(303.63, 665.34) * mm});
            skLineSegment(sketch, "E1117", {"start": v(303.63, 665.34) * mm, "end": v(303.42, 665.7) * mm});
            skLineSegment(sketch, "E1118", {"start": v(303.42, 665.7) * mm, "end": v(303.2, 666.04) * mm});
            skLineSegment(sketch, "E1119", {"start": v(303.2, 666.04) * mm, "end": v(302.96, 666.38) * mm});
            skLineSegment(sketch, "E1120", {"start": v(302.96, 666.38) * mm, "end": v(302.71, 666.71) * mm});
            skLineSegment(sketch, "E1121", {"start": v(302.71, 666.71) * mm, "end": v(302.46, 667.03) * mm});
            skLineSegment(sketch, "E1122", {"start": v(302.46, 667.03) * mm, "end": v(302.19, 667.35) * mm});
            skLineSegment(sketch, "E1123", {"start": v(302.19, 667.35) * mm, "end": v(301.91, 667.65) * mm});
            skLineSegment(sketch, "E1124", {"start": v(301.91, 667.65) * mm, "end": v(301.63, 667.95) * mm});
            skLineSegment(sketch, "E1125", {"start": v(301.63, 667.95) * mm, "end": v(301.33, 668.24) * mm});
            skLineSegment(sketch, "E1126", {"start": v(301.33, 668.24) * mm, "end": v(301.08, 668.47) * mm});
            skLineSegment(sketch, "E1127", {"start": v(301.08, 668.47) * mm, "end": v(300.83, 668.7) * mm});
            skLineSegment(sketch, "E1128", {"start": v(300.83, 668.7) * mm, "end": v(300.57, 668.9) * mm});
            skLineSegment(sketch, "E1129", {"start": v(300.57, 668.9) * mm, "end": v(300.31, 669.12) * mm});
            skLineSegment(sketch, "E1130", {"start": v(300.31, 669.12) * mm, "end": v(300.04, 669.32) * mm});
            skLineSegment(sketch, "E1131", {"start": v(300.04, 669.32) * mm, "end": v(299.77, 669.51) * mm});
            skLineSegment(sketch, "E1132", {"start": v(299.77, 669.51) * mm, "end": v(299.5, 669.7) * mm});
            skLineSegment(sketch, "E1133", {"start": v(299.5, 669.7) * mm, "end": v(299.22, 669.88) * mm});
            skLineSegment(sketch, "E1134", {"start": v(299.22, 669.88) * mm, "end": v(298.93, 670.05) * mm});
            skLineSegment(sketch, "E1135", {"start": v(298.93, 670.05) * mm, "end": v(298.64, 670.22) * mm});
            skLineSegment(sketch, "E1136", {"start": v(298.64, 670.22) * mm, "end": v(298.35, 670.37) * mm});
            skLineSegment(sketch, "E1137", {"start": v(298.35, 670.37) * mm, "end": v(298.05, 670.52) * mm});
            skLineSegment(sketch, "E1138", {"start": v(298.05, 670.52) * mm, "end": v(297.75, 670.67) * mm});
            skLineSegment(sketch, "E1139", {"start": v(297.75, 670.67) * mm, "end": v(297.45, 670.8) * mm});
            skLineSegment(sketch, "E1140", {"start": v(297.45, 670.8) * mm, "end": v(297.14, 670.93) * mm});
            skLineSegment(sketch, "E1141", {"start": v(297.14, 670.93) * mm, "end": v(296.83, 671.05) * mm});
            skLineSegment(sketch, "E1142", {"start": v(296.83, 671.05) * mm, "end": v(296.52, 671.16) * mm});
            skLineSegment(sketch, "E1143", {"start": v(296.52, 671.16) * mm, "end": v(296.2, 671.26) * mm});
            skLineSegment(sketch, "E1144", {"start": v(296.2, 671.26) * mm, "end": v(295.89, 671.35) * mm});
            skLineSegment(sketch, "E1145", {"start": v(295.89, 671.35) * mm, "end": v(295.57, 671.44) * mm});
            skLineSegment(sketch, "E1146", {"start": v(295.57, 671.44) * mm, "end": v(295.24, 671.52) * mm});
            skLineSegment(sketch, "E1147", {"start": v(295.24, 671.52) * mm, "end": v(294.92, 671.59) * mm});
            skLineSegment(sketch, "E1148", {"start": v(294.92, 671.59) * mm, "end": v(294.6, 671.65) * mm});
            skLineSegment(sketch, "E1149", {"start": v(294.6, 671.65) * mm, "end": v(294.26, 671.7) * mm});
            skLineSegment(sketch, "E1150", {"start": v(294.26, 671.7) * mm, "end": v(293.93, 671.75) * mm});
            skLineSegment(sketch, "E1151", {"start": v(293.93, 671.75) * mm, "end": v(293.6, 671.79) * mm});
            skLineSegment(sketch, "E1152", {"start": v(293.6, 671.79) * mm, "end": v(293.27, 671.82) * mm});
            skLineSegment(sketch, "E1153", {"start": v(293.27, 671.82) * mm, "end": v(292.93, 671.84) * mm});
            skLineSegment(sketch, "E1154", {"start": v(292.93, 671.84) * mm, "end": v(292.6, 671.85) * mm});
            skLineSegment(sketch, "E1155", {"start": v(292.6, 671.85) * mm, "end": v(292.26, 671.85) * mm});
            skLineSegment(sketch, "E1156", {"start": v(292.26, 671.85) * mm, "end": v(291.93, 671.84) * mm});
            skLineSegment(sketch, "E1157", {"start": v(291.93, 671.84) * mm, "end": v(291.59, 671.83) * mm});
            skLineSegment(sketch, "E1158", {"start": v(291.59, 671.83) * mm, "end": v(291.28, 671.84) * mm});
            skLineSegment(sketch, "E1159", {"start": v(291.28, 671.84) * mm, "end": v(290.97, 671.84) * mm});
            skLineSegment(sketch, "E1160", {"start": v(290.97, 671.84) * mm, "end": v(290.66, 671.83) * mm});
            skLineSegment(sketch, "E1161", {"start": v(290.66, 671.83) * mm, "end": v(290.35, 671.82) * mm});
            skLineSegment(sketch, "E1162", {"start": v(290.35, 671.82) * mm, "end": v(290.05, 671.8) * mm});
            skLineSegment(sketch, "E1163", {"start": v(290.05, 671.8) * mm, "end": v(289.74, 671.76) * mm});
            skLineSegment(sketch, "E1164", {"start": v(289.74, 671.76) * mm, "end": v(289.44, 671.73) * mm});
            skLineSegment(sketch, "E1165", {"start": v(289.44, 671.73) * mm, "end": v(289.14, 671.68) * mm});
            skLineSegment(sketch, "E1166", {"start": v(289.14, 671.68) * mm, "end": v(288.83, 671.63) * mm});
            skLineSegment(sketch, "E1167", {"start": v(288.83, 671.63) * mm, "end": v(288.54, 671.56) * mm});
            skLineSegment(sketch, "E1168", {"start": v(288.54, 671.56) * mm, "end": v(288.24, 671.5) * mm});
            skLineSegment(sketch, "E1169", {"start": v(288.24, 671.5) * mm, "end": v(287.94, 671.42) * mm});
            skLineSegment(sketch, "E1170", {"start": v(287.94, 671.42) * mm, "end": v(287.65, 671.33) * mm});
            skLineSegment(sketch, "E1171", {"start": v(287.65, 671.33) * mm, "end": v(287.36, 671.24) * mm});
            skLineSegment(sketch, "E1172", {"start": v(287.36, 671.24) * mm, "end": v(287.07, 671.14) * mm});
            skLineSegment(sketch, "E1173", {"start": v(287.07, 671.14) * mm, "end": v(286.78, 671.04) * mm});
            skLineSegment(sketch, "E1174", {"start": v(286.78, 671.04) * mm, "end": v(286.5, 670.92) * mm});
            skLineSegment(sketch, "E1175", {"start": v(286.5, 670.92) * mm, "end": v(286.22, 670.8) * mm});
            skLineSegment(sketch, "E1176", {"start": v(286.22, 670.8) * mm, "end": v(285.94, 670.68) * mm});
            skLineSegment(sketch, "E1177", {"start": v(285.94, 670.68) * mm, "end": v(285.67, 670.54) * mm});
            skLineSegment(sketch, "E1178", {"start": v(285.67, 670.54) * mm, "end": v(285.4, 670.4) * mm});
            skLineSegment(sketch, "E1179", {"start": v(285.4, 670.4) * mm, "end": v(285.13, 670.25) * mm});
            skLineSegment(sketch, "E1180", {"start": v(285.13, 670.25) * mm, "end": v(284.87, 670.1) * mm});
            skLineSegment(sketch, "E1181", {"start": v(284.87, 670.1) * mm, "end": v(284.61, 669.93) * mm});
            skLineSegment(sketch, "E1182", {"start": v(284.61, 669.93) * mm, "end": v(284.36, 669.76) * mm});
            skLineSegment(sketch, "E1183", {"start": v(284.36, 669.76) * mm, "end": v(284.1, 669.59) * mm});
            skLineSegment(sketch, "E1184", {"start": v(284.1, 669.59) * mm, "end": v(283.86, 669.4) * mm});
            skLineSegment(sketch, "E1185", {"start": v(283.86, 669.4) * mm, "end": v(283.61, 669.22) * mm});
            skLineSegment(sketch, "E1186", {"start": v(283.61, 669.22) * mm, "end": v(283.38, 669.02) * mm});
            skLineSegment(sketch, "E1187", {"start": v(283.38, 669.02) * mm, "end": v(283.14, 668.82) * mm});
            skLineSegment(sketch, "E1188", {"start": v(283.14, 668.82) * mm, "end": v(282.92, 668.6) * mm});
            skLineSegment(sketch, "E1189", {"start": v(282.92, 668.6) * mm, "end": v(282.7, 668.4) * mm});
            skLineSegment(sketch, "E1190", {"start": v(282.7, 668.4) * mm, "end": v(282.4, 668.1) * mm});
            skLineSegment(sketch, "E1191", {"start": v(282.4, 668.1) * mm, "end": v(282.1, 667.78) * mm});
            skLineSegment(sketch, "E1192", {"start": v(282.1, 667.78) * mm, "end": v(281.84, 667.46) * mm});
            skLineSegment(sketch, "E1193", {"start": v(281.84, 667.46) * mm, "end": v(281.59, 667.13) * mm});
            skLineSegment(sketch, "E1194", {"start": v(281.59, 667.13) * mm, "end": v(281.35, 666.8) * mm});
            skLineSegment(sketch, "E1195", {"start": v(281.35, 666.8) * mm, "end": v(281.14, 666.44) * mm});
            skLineSegment(sketch, "E1196", {"start": v(281.14, 666.44) * mm, "end": v(280.94, 666.09) * mm});
            skLineSegment(sketch, "E1197", {"start": v(280.94, 666.09) * mm, "end": v(280.76, 665.72) * mm});
            skLineSegment(sketch, "E1198", {"start": v(280.76, 665.72) * mm, "end": v(280.6, 665.35) * mm});
            skLineSegment(sketch, "E1199", {"start": v(280.6, 665.35) * mm, "end": v(280.45, 664.97) * mm});
            skLineSegment(sketch, "E1200", {"start": v(280.45, 664.97) * mm, "end": v(280.32, 664.6) * mm});
            skLineSegment(sketch, "E1201", {"start": v(280.32, 664.6) * mm, "end": v(280.21, 664.2) * mm});
            skLineSegment(sketch, "E1202", {"start": v(280.21, 664.2) * mm, "end": v(280.12, 663.81) * mm});
            skLineSegment(sketch, "E1203", {"start": v(280.12, 663.81) * mm, "end": v(280.05, 663.42) * mm});
            skLineSegment(sketch, "E1204", {"start": v(280.05, 663.42) * mm, "end": v(280, 663.02) * mm});
            skLineSegment(sketch, "E1205", {"start": v(280, 663.02) * mm, "end": v(279.96, 662.62) * mm});
            skLineSegment(sketch, "E1206", {"start": v(279.96, 662.62) * mm, "end": v(279.94, 662.22) * mm});
            skLineSegment(sketch, "E1207", {"start": v(279.94, 662.22) * mm, "end": v(279.93, 661.82) * mm});
            skLineSegment(sketch, "E1208", {"start": v(279.93, 661.82) * mm, "end": v(279.95, 661.42) * mm});
            skLineSegment(sketch, "E1209", {"start": v(279.95, 661.42) * mm, "end": v(279.98, 661.02) * mm});
            skLineSegment(sketch, "E1210", {"start": v(279.98, 661.02) * mm, "end": v(280.04, 660.62) * mm});
            skLineSegment(sketch, "E1211", {"start": v(280.04, 660.62) * mm, "end": v(280.1, 660.23) * mm});
            skLineSegment(sketch, "E1212", {"start": v(280.1, 660.23) * mm, "end": v(280.2, 659.83) * mm});
            skLineSegment(sketch, "E1213", {"start": v(280.2, 659.83) * mm, "end": v(280.3, 659.44) * mm});
            skLineSegment(sketch, "E1214", {"start": v(280.3, 659.44) * mm, "end": v(280.43, 659.05) * mm});
            skLineSegment(sketch, "E1215", {"start": v(280.43, 659.05) * mm, "end": v(280.58, 658.67) * mm});
            skLineSegment(sketch, "E1216", {"start": v(280.58, 658.67) * mm, "end": v(280.74, 658.3) * mm});
            skLineSegment(sketch, "E1217", {"start": v(280.74, 658.3) * mm, "end": v(280.92, 657.93) * mm});
            skLineSegment(sketch, "E1218", {"start": v(280.92, 657.93) * mm, "end": v(281.12, 657.56) * mm});
            skLineSegment(sketch, "E1219", {"start": v(281.12, 657.56) * mm, "end": v(281.34, 657.2) * mm});
            skLineSegment(sketch, "E1220", {"start": v(281.34, 657.2) * mm, "end": v(281.58, 656.86) * mm});
            skLineSegment(sketch, "E1221", {"start": v(281.58, 656.86) * mm, "end": v(281.83, 656.52) * mm});
            skLineSegment(sketch, "E1222", {"start": v(281.83, 656.52) * mm, "end": v(282.1, 656.25) * mm});
            skLineSegment(sketch, "E1223", {"start": v(282.1, 656.25) * mm, "end": v(282.36, 656) * mm});
            skLineSegment(sketch, "E1224", {"start": v(282.36, 656) * mm, "end": v(282.63, 655.75) * mm});
            skLineSegment(sketch, "E1225", {"start": v(282.63, 655.75) * mm, "end": v(282.9, 655.51) * mm});
            skLineSegment(sketch, "E1226", {"start": v(282.9, 655.51) * mm, "end": v(283.19, 655.28) * mm});
            skLineSegment(sketch, "E1227", {"start": v(283.19, 655.28) * mm, "end": v(283.47, 655.06) * mm});
            skLineSegment(sketch, "E1228", {"start": v(283.47, 655.06) * mm, "end": v(283.77, 654.84) * mm});
            skLineSegment(sketch, "E1229", {"start": v(283.77, 654.84) * mm, "end": v(284.07, 654.64) * mm});
            skLineSegment(sketch, "E1230", {"start": v(284.07, 654.64) * mm, "end": v(284.37, 654.44) * mm});
            skLineSegment(sketch, "E1231", {"start": v(284.37, 654.44) * mm, "end": v(284.68, 654.25) * mm});
            skLineSegment(sketch, "E1232", {"start": v(284.68, 654.25) * mm, "end": v(285, 654.07) * mm});
            skLineSegment(sketch, "E1233", {"start": v(285, 654.07) * mm, "end": v(285.31, 653.9) * mm});
            skLineSegment(sketch, "E1234", {"start": v(285.31, 653.9) * mm, "end": v(285.64, 653.73) * mm});
            skLineSegment(sketch, "E1235", {"start": v(285.64, 653.73) * mm, "end": v(285.96, 653.58) * mm});
            skLineSegment(sketch, "E1236", {"start": v(285.96, 653.58) * mm, "end": v(286.3, 653.43) * mm});
            skLineSegment(sketch, "E1237", {"start": v(286.3, 653.43) * mm, "end": v(286.63, 653.3) * mm});
            skLineSegment(sketch, "E1238", {"start": v(286.63, 653.3) * mm, "end": v(286.97, 653.16) * mm});
            skLineSegment(sketch, "E1239", {"start": v(286.97, 653.16) * mm, "end": v(287.3, 653.05) * mm});
            skLineSegment(sketch, "E1240", {"start": v(287.3, 653.05) * mm, "end": v(287.65, 652.93) * mm});
            skLineSegment(sketch, "E1241", {"start": v(287.65, 652.93) * mm, "end": v(288, 652.83) * mm});
            skLineSegment(sketch, "E1242", {"start": v(288, 652.83) * mm, "end": v(288.35, 652.74) * mm});
            skLineSegment(sketch, "E1243", {"start": v(288.35, 652.74) * mm, "end": v(288.7, 652.66) * mm});
            skLineSegment(sketch, "E1244", {"start": v(288.7, 652.66) * mm, "end": v(289.06, 652.59) * mm});
            skLineSegment(sketch, "E1245", {"start": v(289.06, 652.59) * mm, "end": v(289.42, 652.52) * mm});
            skLineSegment(sketch, "E1246", {"start": v(289.42, 652.52) * mm, "end": v(289.78, 652.47) * mm});
            skLineSegment(sketch, "E1247", {"start": v(289.78, 652.47) * mm, "end": v(290.14, 652.42) * mm});
            skLineSegment(sketch, "E1248", {"start": v(290.14, 652.42) * mm, "end": v(290.5, 652.39) * mm});
            skLineSegment(sketch, "E1249", {"start": v(290.5, 652.39) * mm, "end": v(290.87, 652.36) * mm});
            skLineSegment(sketch, "E1250", {"start": v(290.87, 652.36) * mm, "end": v(291.23, 652.35) * mm});
            skLineSegment(sketch, "E1251", {"start": v(291.23, 652.35) * mm, "end": v(291.6, 652.34) * mm});
            skLineSegment(sketch, "E1252", {"start": v(291.6, 652.34) * mm, "end": v(291.97, 652.35) * mm});
            skLineSegment(sketch, "E1253", {"start": v(291.97, 652.35) * mm, "end": v(292.33, 652.36) * mm});
            skLineSegment(sketch, "E1254", {"start": v(292.33, 652.36) * mm, "end": v(292.83, 652.42) * mm});
            skLineSegment(sketch, "E1255", {"start": v(292.83, 652.42) * mm, "end": v(293.31, 652.45) * mm});
            skLineSegment(sketch, "E1256", {"start": v(293.31, 652.45) * mm, "end": v(293.8, 652.46) * mm});
            skLineSegment(sketch, "E1257", {"start": v(293.8, 652.46) * mm, "end": v(294.28, 652.44) * mm});
            skLineSegment(sketch, "E1258", {"start": v(294.28, 652.44) * mm, "end": v(294.76, 652.4) * mm});
            skLineSegment(sketch, "E1259", {"start": v(294.76, 652.4) * mm, "end": v(295.23, 652.34) * mm});
            skLineSegment(sketch, "E1260", {"start": v(295.23, 652.34) * mm, "end": v(295.7, 652.25) * mm});
            skLineSegment(sketch, "E1261", {"start": v(295.7, 652.25) * mm, "end": v(296.16, 652.15) * mm});
            skLineSegment(sketch, "E1262", {"start": v(296.16, 652.15) * mm, "end": v(296.6, 652.02) * mm});
            skLineSegment(sketch, "E1263", {"start": v(296.6, 652.02) * mm, "end": v(297.05, 651.87) * mm});
            skLineSegment(sketch, "E1264", {"start": v(297.05, 651.87) * mm, "end": v(297.49, 651.7) * mm});
            skLineSegment(sketch, "E1265", {"start": v(297.49, 651.7) * mm, "end": v(297.91, 651.52) * mm});
            skLineSegment(sketch, "E1266", {"start": v(297.91, 651.52) * mm, "end": v(298.33, 651.31) * mm});
            skLineSegment(sketch, "E1267", {"start": v(298.33, 651.31) * mm, "end": v(298.74, 651.08) * mm});
            skLineSegment(sketch, "E1268", {"start": v(298.74, 651.08) * mm, "end": v(299.13, 650.84) * mm});
            skLineSegment(sketch, "E1269", {"start": v(299.13, 650.84) * mm, "end": v(299.52, 650.58) * mm});
            skLineSegment(sketch, "E1270", {"start": v(299.52, 650.58) * mm, "end": v(299.89, 650.3) * mm});
            skLineSegment(sketch, "E1271", {"start": v(299.89, 650.3) * mm, "end": v(300.25, 650) * mm});
            skLineSegment(sketch, "E1272", {"start": v(300.25, 650) * mm, "end": v(300.6, 649.7) * mm});
            skLineSegment(sketch, "E1273", {"start": v(300.6, 649.7) * mm, "end": v(300.92, 649.36) * mm});
            skLineSegment(sketch, "E1274", {"start": v(300.92, 649.36) * mm, "end": v(301.24, 649.02) * mm});
            skLineSegment(sketch, "E1275", {"start": v(301.24, 649.02) * mm, "end": v(301.54, 648.66) * mm});
            skLineSegment(sketch, "E1276", {"start": v(301.54, 648.66) * mm, "end": v(301.82, 648.29) * mm});
            skLineSegment(sketch, "E1277", {"start": v(301.82, 648.29) * mm, "end": v(302.08, 647.9) * mm});
            skLineSegment(sketch, "E1278", {"start": v(302.08, 647.9) * mm, "end": v(302.33, 647.5) * mm});
            skLineSegment(sketch, "E1279", {"start": v(302.33, 647.5) * mm, "end": v(302.56, 647.08) * mm});
            skLineSegment(sketch, "E1280", {"start": v(302.56, 647.08) * mm, "end": v(302.77, 646.66) * mm});
            skLineSegment(sketch, "E1281", {"start": v(302.77, 646.66) * mm, "end": v(302.96, 646.22) * mm});
            skLineSegment(sketch, "E1282", {"start": v(302.96, 646.22) * mm, "end": v(303.13, 645.77) * mm});
            skLineSegment(sketch, "E1283", {"start": v(303.13, 645.77) * mm, "end": v(303.28, 645.3) * mm});
            skLineSegment(sketch, "E1284", {"start": v(303.28, 645.3) * mm, "end": v(303.41, 644.83) * mm});
            skLineSegment(sketch, "E1285", {"start": v(303.41, 644.83) * mm, "end": v(303.52, 644.35) * mm});
            skLineSegment(sketch, "E1286", {"start": v(303.52, 644.35) * mm, "end": v(303.52, 643.95) * mm});
            skLineSegment(sketch, "E1287", {"start": v(303.52, 643.95) * mm, "end": v(303.5, 643.55) * mm});
            skLineSegment(sketch, "E1288", {"start": v(303.5, 643.55) * mm, "end": v(303.45, 643.16) * mm});
            skLineSegment(sketch, "E1289", {"start": v(303.45, 643.16) * mm, "end": v(303.38, 642.77) * mm});
            skLineSegment(sketch, "E1290", {"start": v(303.38, 642.77) * mm, "end": v(303.3, 642.39) * mm});
            skLineSegment(sketch, "E1291", {"start": v(303.3, 642.39) * mm, "end": v(303.18, 642.01) * mm});
            skLineSegment(sketch, "E1292", {"start": v(303.18, 642.01) * mm, "end": v(303.05, 641.64) * mm});
            skLineSegment(sketch, "E1293", {"start": v(303.05, 641.64) * mm, "end": v(302.9, 641.28) * mm});
            skLineSegment(sketch, "E1294", {"start": v(302.9, 641.28) * mm, "end": v(302.73, 640.93) * mm});
            skLineSegment(sketch, "E1295", {"start": v(302.73, 640.93) * mm, "end": v(302.54, 640.58) * mm});
            skLineSegment(sketch, "E1296", {"start": v(302.54, 640.58) * mm, "end": v(302.33, 640.25) * mm});
            skLineSegment(sketch, "E1297", {"start": v(302.33, 640.25) * mm, "end": v(302.1, 639.93) * mm});
            skLineSegment(sketch, "E1298", {"start": v(302.1, 639.93) * mm, "end": v(301.86, 639.62) * mm});
            skLineSegment(sketch, "E1299", {"start": v(301.86, 639.62) * mm, "end": v(301.6, 639.32) * mm});
            skLineSegment(sketch, "E1300", {"start": v(301.6, 639.32) * mm, "end": v(301.31, 639.04) * mm});
            skLineSegment(sketch, "E1301", {"start": v(301.31, 639.04) * mm, "end": v(301.02, 638.77) * mm});
            skLineSegment(sketch, "E1302", {"start": v(301.02, 638.77) * mm, "end": v(300.77, 638.56) * mm});
            skLineSegment(sketch, "E1303", {"start": v(300.77, 638.56) * mm, "end": v(300.52, 638.35) * mm});
            skLineSegment(sketch, "E1304", {"start": v(300.52, 638.35) * mm, "end": v(300.27, 638.14) * mm});
            skLineSegment(sketch, "E1305", {"start": v(300.27, 638.14) * mm, "end": v(300.01, 637.95) * mm});
            skLineSegment(sketch, "E1306", {"start": v(300.01, 637.95) * mm, "end": v(299.75, 637.76) * mm});
            skLineSegment(sketch, "E1307", {"start": v(299.75, 637.76) * mm, "end": v(299.48, 637.57) * mm});
            skLineSegment(sketch, "E1308", {"start": v(299.48, 637.57) * mm, "end": v(299.2, 637.4) * mm});
            skLineSegment(sketch, "E1309", {"start": v(299.2, 637.4) * mm, "end": v(298.93, 637.23) * mm});
            skLineSegment(sketch, "E1310", {"start": v(298.93, 637.23) * mm, "end": v(298.65, 637.07) * mm});
            skLineSegment(sketch, "E1311", {"start": v(298.65, 637.07) * mm, "end": v(298.37, 636.91) * mm});
            skLineSegment(sketch, "E1312", {"start": v(298.37, 636.91) * mm, "end": v(298.08, 636.76) * mm});
            skLineSegment(sketch, "E1313", {"start": v(298.08, 636.76) * mm, "end": v(297.8, 636.62) * mm});
            skLineSegment(sketch, "E1314", {"start": v(297.8, 636.62) * mm, "end": v(297.5, 636.5) * mm});
            skLineSegment(sketch, "E1315", {"start": v(297.5, 636.5) * mm, "end": v(297.2, 636.37) * mm});
            skLineSegment(sketch, "E1316", {"start": v(297.2, 636.37) * mm, "end": v(296.9, 636.25) * mm});
            skLineSegment(sketch, "E1317", {"start": v(296.9, 636.25) * mm, "end": v(296.6, 636.14) * mm});
            skLineSegment(sketch, "E1318", {"start": v(296.6, 636.14) * mm, "end": v(296.3, 636.03) * mm});
            skLineSegment(sketch, "E1319", {"start": v(296.3, 636.03) * mm, "end": v(295.99, 635.94) * mm});
            skLineSegment(sketch, "E1320", {"start": v(295.99, 635.94) * mm, "end": v(295.68, 635.85) * mm});
            skLineSegment(sketch, "E1321", {"start": v(295.68, 635.85) * mm, "end": v(295.36, 635.77) * mm});
            skLineSegment(sketch, "E1322", {"start": v(295.36, 635.77) * mm, "end": v(295.05, 635.7) * mm});
            skLineSegment(sketch, "E1323", {"start": v(295.05, 635.7) * mm, "end": v(294.73, 635.64) * mm});
            skLineSegment(sketch, "E1324", {"start": v(294.73, 635.64) * mm, "end": v(294.42, 635.58) * mm});
            skLineSegment(sketch, "E1325", {"start": v(294.42, 635.58) * mm, "end": v(294.1, 635.53) * mm});
            skLineSegment(sketch, "E1326", {"start": v(294.1, 635.53) * mm, "end": v(293.78, 635.5) * mm});
            skLineSegment(sketch, "E1327", {"start": v(293.78, 635.5) * mm, "end": v(293.45, 635.46) * mm});
            skLineSegment(sketch, "E1328", {"start": v(293.45, 635.46) * mm, "end": v(293.13, 635.43) * mm});
            skLineSegment(sketch, "E1329", {"start": v(293.13, 635.43) * mm, "end": v(292.8, 635.42) * mm});
            skLineSegment(sketch, "E1330", {"start": v(292.8, 635.42) * mm, "end": v(292.48, 635.4) * mm});
            skLineSegment(sketch, "E1331", {"start": v(292.48, 635.4) * mm, "end": v(292.16, 635.41) * mm});
            skLineSegment(sketch, "E1332", {"start": v(292.16, 635.41) * mm, "end": v(291.83, 635.42) * mm});
            skLineSegment(sketch, "E1333", {"start": v(291.83, 635.42) * mm, "end": v(291.5, 635.44) * mm});
            skLineSegment(sketch, "E1334", {"start": v(291.5, 635.44) * mm, "end": v(290.93, 635.44) * mm});
            skLineSegment(sketch, "E1335", {"start": v(290.93, 635.44) * mm, "end": v(290.36, 635.46) * mm});
            skLineSegment(sketch, "E1336", {"start": v(290.36, 635.46) * mm, "end": v(289.79, 635.52) * mm});
            skLineSegment(sketch, "E1337", {"start": v(289.79, 635.52) * mm, "end": v(289.23, 635.6) * mm});
            skLineSegment(sketch, "E1338", {"start": v(289.23, 635.6) * mm, "end": v(288.67, 635.71) * mm});
            skLineSegment(sketch, "E1339", {"start": v(288.67, 635.71) * mm, "end": v(288.12, 635.85) * mm});
            skLineSegment(sketch, "E1340", {"start": v(288.12, 635.85) * mm, "end": v(287.57, 636) * mm});
            skLineSegment(sketch, "E1341", {"start": v(287.57, 636) * mm, "end": v(287.04, 636.2) * mm});
            skLineSegment(sketch, "E1342", {"start": v(287.04, 636.2) * mm, "end": v(286.51, 636.4) * mm});
            skLineSegment(sketch, "E1343", {"start": v(286.51, 636.4) * mm, "end": v(286, 636.65) * mm});
            skLineSegment(sketch, "E1344", {"start": v(286, 636.65) * mm, "end": v(285.5, 636.9) * mm});
            skLineSegment(sketch, "E1345", {"start": v(285.5, 636.9) * mm, "end": v(285, 637.2) * mm});
            skLineSegment(sketch, "E1346", {"start": v(285, 637.2) * mm, "end": v(284.52, 637.5) * mm});
            skLineSegment(sketch, "E1347", {"start": v(284.52, 637.5) * mm, "end": v(284.06, 637.84) * mm});
            skLineSegment(sketch, "E1348", {"start": v(284.06, 637.84) * mm, "end": v(283.61, 638.2) * mm});
            skLineSegment(sketch, "E1349", {"start": v(283.61, 638.2) * mm, "end": v(283.18, 638.58) * mm});
            skLineSegment(sketch, "E1350", {"start": v(283.18, 638.58) * mm, "end": v(282.92, 638.86) * mm});
            skLineSegment(sketch, "E1351", {"start": v(282.92, 638.86) * mm, "end": v(282.67, 639.16) * mm});
            skLineSegment(sketch, "E1352", {"start": v(282.67, 639.16) * mm, "end": v(282.43, 639.46) * mm});
            skLineSegment(sketch, "E1353", {"start": v(282.43, 639.46) * mm, "end": v(282.2, 639.77) * mm});
            skLineSegment(sketch, "E1354", {"start": v(282.2, 639.77) * mm, "end": v(281.98, 640.1) * mm});
            skLineSegment(sketch, "E1355", {"start": v(281.98, 640.1) * mm, "end": v(281.78, 640.42) * mm});
            skLineSegment(sketch, "E1356", {"start": v(281.78, 640.42) * mm, "end": v(281.58, 640.75) * mm});
            skLineSegment(sketch, "E1357", {"start": v(281.58, 640.75) * mm, "end": v(281.4, 641.09) * mm});
            skLineSegment(sketch, "E1358", {"start": v(281.4, 641.09) * mm, "end": v(281.23, 641.43) * mm});
            skLineSegment(sketch, "E1359", {"start": v(281.23, 641.43) * mm, "end": v(281.07, 641.78) * mm});
            skLineSegment(sketch, "E1360", {"start": v(281.07, 641.78) * mm, "end": v(280.92, 642.14) * mm});
            skLineSegment(sketch, "E1361", {"start": v(280.92, 642.14) * mm, "end": v(280.79, 642.5) * mm});
            skLineSegment(sketch, "E1362", {"start": v(280.79, 642.5) * mm, "end": v(280.66, 642.87) * mm});
            skLineSegment(sketch, "E1363", {"start": v(280.66, 642.87) * mm, "end": v(280.55, 643.24) * mm});
            skLineSegment(sketch, "E1364", {"start": v(280.55, 643.24) * mm, "end": v(280.46, 643.61) * mm});
            skLineSegment(sketch, "E1365", {"start": v(280.46, 643.61) * mm, "end": v(280.37, 643.99) * mm});
            skLineSegment(sketch, "E1366", {"start": v(272.09, 671.1) * mm, "end": v(272.09, 636.15) * mm});
            skLineSegment(sketch, "E1367", {"start": v(264.39, 671.1) * mm, "end": v(264.39, 636.13) * mm});
            skLineSegment(sketch, "E1368", {"start": v(264.39, 636.13) * mm, "end": v(251.56, 636.13) * mm});
            skLineSegment(sketch, "E1369", {"start": v(251.56, 636.13) * mm, "end": v(251.26, 636.14) * mm});
            skLineSegment(sketch, "E1370", {"start": v(251.26, 636.14) * mm, "end": v(250.95, 636.17) * mm});
            skLineSegment(sketch, "E1371", {"start": v(250.95, 636.17) * mm, "end": v(250.65, 636.2) * mm});
            skLineSegment(sketch, "E1372", {"start": v(250.65, 636.2) * mm, "end": v(250.35, 636.23) * mm});
            skLineSegment(sketch, "E1373", {"start": v(250.35, 636.23) * mm, "end": v(250.05, 636.28) * mm});
            skLineSegment(sketch, "E1374", {"start": v(250.05, 636.28) * mm, "end": v(249.76, 636.33) * mm});
            skLineSegment(sketch, "E1375", {"start": v(249.76, 636.33) * mm, "end": v(249.46, 636.39) * mm});
            skLineSegment(sketch, "E1376", {"start": v(249.46, 636.39) * mm, "end": v(249.17, 636.46) * mm});
            skLineSegment(sketch, "E1377", {"start": v(249.17, 636.46) * mm, "end": v(248.88, 636.53) * mm});
            skLineSegment(sketch, "E1378", {"start": v(248.88, 636.53) * mm, "end": v(248.59, 636.61) * mm});
            skLineSegment(sketch, "E1379", {"start": v(248.59, 636.61) * mm, "end": v(248.3, 636.7) * mm});
            skLineSegment(sketch, "E1380", {"start": v(248.3, 636.7) * mm, "end": v(248.02, 636.8) * mm});
            skLineSegment(sketch, "E1381", {"start": v(248.02, 636.8) * mm, "end": v(247.46, 637.01) * mm});
            skLineSegment(sketch, "E1382", {"start": v(247.46, 637.01) * mm, "end": v(246.9, 637.25) * mm});
            skLineSegment(sketch, "E1383", {"start": v(246.9, 637.25) * mm, "end": v(246.37, 637.52) * mm});
            skLineSegment(sketch, "E1384", {"start": v(246.37, 637.52) * mm, "end": v(245.85, 637.81) * mm});
            skLineSegment(sketch, "E1385", {"start": v(245.85, 637.81) * mm, "end": v(245.6, 637.97) * mm});
            skLineSegment(sketch, "E1386", {"start": v(245.6, 637.97) * mm, "end": v(245.34, 638.13) * mm});
            skLineSegment(sketch, "E1387", {"start": v(245.34, 638.13) * mm, "end": v(245.1, 638.3) * mm});
            skLineSegment(sketch, "E1388", {"start": v(245.1, 638.3) * mm, "end": v(244.85, 638.48) * mm});
            skLineSegment(sketch, "E1389", {"start": v(244.85, 638.48) * mm, "end": v(244.61, 638.66) * mm});
            skLineSegment(sketch, "E1390", {"start": v(244.61, 638.66) * mm, "end": v(244.38, 638.85) * mm});
            skLineSegment(sketch, "E1391", {"start": v(244.38, 638.85) * mm, "end": v(244.15, 639.04) * mm});
            skLineSegment(sketch, "E1392", {"start": v(244.15, 639.04) * mm, "end": v(243.92, 639.25) * mm});
            skLineSegment(sketch, "E1393", {"start": v(243.92, 639.25) * mm, "end": v(243.7, 639.45) * mm});
            skLineSegment(sketch, "E1394", {"start": v(243.7, 639.45) * mm, "end": v(243.48, 639.66) * mm});
            skLineSegment(sketch, "E1395", {"start": v(243.48, 639.66) * mm, "end": v(243.27, 639.88) * mm});
            skLineSegment(sketch, "E1396", {"start": v(243.27, 639.88) * mm, "end": v(243.07, 640.1) * mm});
            skLineSegment(sketch, "E1397", {"start": v(243.07, 640.1) * mm, "end": v(242.72, 640.47) * mm});
            skLineSegment(sketch, "E1398", {"start": v(242.72, 640.47) * mm, "end": v(242.37, 640.84) * mm});
            skLineSegment(sketch, "E1399", {"start": v(242.37, 640.84) * mm, "end": v(242.04, 641.21) * mm});
            skLineSegment(sketch, "E1400", {"start": v(242.04, 641.21) * mm, "end": v(241.72, 641.6) * mm});
            skLineSegment(sketch, "E1401", {"start": v(241.72, 641.6) * mm, "end": v(241.41, 641.99) * mm});
            skLineSegment(sketch, "E1402", {"start": v(241.41, 641.99) * mm, "end": v(241.11, 642.39) * mm});
            skLineSegment(sketch, "E1403", {"start": v(241.11, 642.39) * mm, "end": v(240.82, 642.8) * mm});
            skLineSegment(sketch, "E1404", {"start": v(240.82, 642.8) * mm, "end": v(240.55, 643.2) * mm});
            skLineSegment(sketch, "E1405", {"start": v(240.55, 643.2) * mm, "end": v(240.28, 643.63) * mm});
            skLineSegment(sketch, "E1406", {"start": v(240.28, 643.63) * mm, "end": v(240.02, 644.05) * mm});
            skLineSegment(sketch, "E1407", {"start": v(240.02, 644.05) * mm, "end": v(239.77, 644.48) * mm});
            skLineSegment(sketch, "E1408", {"start": v(239.77, 644.48) * mm, "end": v(239.54, 644.92) * mm});
            skLineSegment(sketch, "E1409", {"start": v(239.54, 644.92) * mm, "end": v(239.32, 645.36) * mm});
            skLineSegment(sketch, "E1410", {"start": v(239.32, 645.36) * mm, "end": v(239.1, 645.8) * mm});
            skLineSegment(sketch, "E1411", {"start": v(239.1, 645.8) * mm, "end": v(238.9, 646.26) * mm});
            skLineSegment(sketch, "E1412", {"start": v(238.9, 646.26) * mm, "end": v(238.7, 646.72) * mm});
            skLineSegment(sketch, "E1413", {"start": v(238.7, 646.72) * mm, "end": v(238.53, 647.18) * mm});
            skLineSegment(sketch, "E1414", {"start": v(238.53, 647.18) * mm, "end": v(238.36, 647.65) * mm});
            skLineSegment(sketch, "E1415", {"start": v(238.36, 647.65) * mm, "end": v(238.2, 648.12) * mm});
            skLineSegment(sketch, "E1416", {"start": v(238.2, 648.12) * mm, "end": v(238.06, 648.6) * mm});
            skLineSegment(sketch, "E1417", {"start": v(238.06, 648.6) * mm, "end": v(237.93, 649.07) * mm});
            skLineSegment(sketch, "E1418", {"start": v(237.93, 649.07) * mm, "end": v(237.8, 649.55) * mm});
            skLineSegment(sketch, "E1419", {"start": v(237.8, 649.55) * mm, "end": v(237.7, 650.04) * mm});
            skLineSegment(sketch, "E1420", {"start": v(237.7, 650.04) * mm, "end": v(237.6, 650.52) * mm});
            skLineSegment(sketch, "E1421", {"start": v(237.6, 650.52) * mm, "end": v(237.52, 651.01) * mm});
            skLineSegment(sketch, "E1422", {"start": v(237.52, 651.01) * mm, "end": v(237.45, 651.5) * mm});
            skLineSegment(sketch, "E1423", {"start": v(237.45, 651.5) * mm, "end": v(237.39, 652) * mm});
            skLineSegment(sketch, "E1424", {"start": v(237.39, 652) * mm, "end": v(237.34, 652.5) * mm});
            skLineSegment(sketch, "E1425", {"start": v(237.34, 652.5) * mm, "end": v(237.3, 653) * mm});
            skLineSegment(sketch, "E1426", {"start": v(237.3, 653) * mm, "end": v(237.28, 653.5) * mm});
            skLineSegment(sketch, "E1427", {"start": v(237.28, 653.5) * mm, "end": v(237.27, 654) * mm});
            skLineSegment(sketch, "E1428", {"start": v(237.27, 654) * mm, "end": v(237.28, 654.5) * mm});
            skLineSegment(sketch, "E1429", {"start": v(237.28, 654.5) * mm, "end": v(237.27, 654.93) * mm});
            skLineSegment(sketch, "E1430", {"start": v(237.27, 654.93) * mm, "end": v(237.27, 655.35) * mm});
            skLineSegment(sketch, "E1431", {"start": v(237.27, 655.35) * mm, "end": v(237.28, 655.77) * mm});
            skLineSegment(sketch, "E1432", {"start": v(237.28, 655.77) * mm, "end": v(237.3, 656.19) * mm});
            skLineSegment(sketch, "E1433", {"start": v(237.3, 656.19) * mm, "end": v(237.33, 656.6) * mm});
            skLineSegment(sketch, "E1434", {"start": v(237.33, 656.6) * mm, "end": v(237.37, 657.02) * mm});
            skLineSegment(sketch, "E1435", {"start": v(237.37, 657.02) * mm, "end": v(237.42, 657.44) * mm});
            skLineSegment(sketch, "E1436", {"start": v(237.42, 657.44) * mm, "end": v(237.49, 657.85) * mm});
            skLineSegment(sketch, "E1437", {"start": v(237.49, 657.85) * mm, "end": v(237.56, 658.26) * mm});
            skLineSegment(sketch, "E1438", {"start": v(237.56, 658.26) * mm, "end": v(237.64, 658.67) * mm});
            skLineSegment(sketch, "E1439", {"start": v(237.64, 658.67) * mm, "end": v(237.73, 659.07) * mm});
            skLineSegment(sketch, "E1440", {"start": v(237.73, 659.07) * mm, "end": v(237.84, 659.48) * mm});
            skLineSegment(sketch, "E1441", {"start": v(237.84, 659.48) * mm, "end": v(237.95, 659.88) * mm});
            skLineSegment(sketch, "E1442", {"start": v(237.95, 659.88) * mm, "end": v(238.07, 660.28) * mm});
            skLineSegment(sketch, "E1443", {"start": v(238.07, 660.28) * mm, "end": v(238.2, 660.67) * mm});
            skLineSegment(sketch, "E1444", {"start": v(238.2, 660.67) * mm, "end": v(238.34, 661.06) * mm});
            skLineSegment(sketch, "E1445", {"start": v(238.34, 661.06) * mm, "end": v(238.5, 661.45) * mm});
            skLineSegment(sketch, "E1446", {"start": v(238.5, 661.45) * mm, "end": v(238.65, 661.83) * mm});
            skLineSegment(sketch, "E1447", {"start": v(238.65, 661.83) * mm, "end": v(238.82, 662.21) * mm});
            skLineSegment(sketch, "E1448", {"start": v(238.82, 662.21) * mm, "end": v(239, 662.59) * mm});
            skLineSegment(sketch, "E1449", {"start": v(239, 662.59) * mm, "end": v(239.19, 662.96) * mm});
            skLineSegment(sketch, "E1450", {"start": v(239.19, 662.96) * mm, "end": v(239.38, 663.33) * mm});
            skLineSegment(sketch, "E1451", {"start": v(239.38, 663.33) * mm, "end": v(239.59, 663.7) * mm});
            skLineSegment(sketch, "E1452", {"start": v(239.59, 663.7) * mm, "end": v(239.8, 664.05) * mm});
            skLineSegment(sketch, "E1453", {"start": v(239.8, 664.05) * mm, "end": v(240.03, 664.4) * mm});
            skLineSegment(sketch, "E1454", {"start": v(240.03, 664.4) * mm, "end": v(240.26, 664.75) * mm});
            skLineSegment(sketch, "E1455", {"start": v(240.26, 664.75) * mm, "end": v(240.5, 665.09) * mm});
            skLineSegment(sketch, "E1456", {"start": v(240.5, 665.09) * mm, "end": v(240.75, 665.43) * mm});
            skLineSegment(sketch, "E1457", {"start": v(240.75, 665.43) * mm, "end": v(241, 665.76) * mm});
            skLineSegment(sketch, "E1458", {"start": v(241, 665.76) * mm, "end": v(241.28, 666.08) * mm});
            skLineSegment(sketch, "E1459", {"start": v(241.28, 666.08) * mm, "end": v(241.55, 666.4) * mm});
            skLineSegment(sketch, "E1460", {"start": v(241.55, 666.4) * mm, "end": v(241.84, 666.7) * mm});
            skLineSegment(sketch, "E1461", {"start": v(241.84, 666.7) * mm, "end": v(242.08, 666.96) * mm});
            skLineSegment(sketch, "E1462", {"start": v(242.08, 666.96) * mm, "end": v(242.32, 667.2) * mm});
            skLineSegment(sketch, "E1463", {"start": v(242.32, 667.2) * mm, "end": v(242.57, 667.44) * mm});
            skLineSegment(sketch, "E1464", {"start": v(242.57, 667.44) * mm, "end": v(242.83, 667.67) * mm});
            skLineSegment(sketch, "E1465", {"start": v(242.83, 667.67) * mm, "end": v(243.09, 667.89) * mm});
            skLineSegment(sketch, "E1466", {"start": v(243.09, 667.89) * mm, "end": v(243.36, 668.1) * mm});
            skLineSegment(sketch, "E1467", {"start": v(243.36, 668.1) * mm, "end": v(243.63, 668.31) * mm});
            skLineSegment(sketch, "E1468", {"start": v(243.63, 668.31) * mm, "end": v(243.9, 668.51) * mm});
            skLineSegment(sketch, "E1469", {"start": v(243.9, 668.51) * mm, "end": v(244.18, 668.7) * mm});
            skLineSegment(sketch, "E1470", {"start": v(244.18, 668.7) * mm, "end": v(244.47, 668.9) * mm});
            skLineSegment(sketch, "E1471", {"start": v(244.47, 668.9) * mm, "end": v(244.76, 669.08) * mm});
            skLineSegment(sketch, "E1472", {"start": v(244.76, 669.08) * mm, "end": v(245.05, 669.25) * mm});
            skLineSegment(sketch, "E1473", {"start": v(245.05, 669.25) * mm, "end": v(245.35, 669.42) * mm});
            skLineSegment(sketch, "E1474", {"start": v(245.35, 669.42) * mm, "end": v(245.65, 669.58) * mm});
            skLineSegment(sketch, "E1475", {"start": v(245.65, 669.58) * mm, "end": v(245.95, 669.73) * mm});
            skLineSegment(sketch, "E1476", {"start": v(245.95, 669.73) * mm, "end": v(246.26, 669.87) * mm});
            skLineSegment(sketch, "E1477", {"start": v(246.26, 669.87) * mm, "end": v(246.58, 670) * mm});
            skLineSegment(sketch, "E1478", {"start": v(246.58, 670) * mm, "end": v(246.9, 670.14) * mm});
            skLineSegment(sketch, "E1479", {"start": v(246.9, 670.14) * mm, "end": v(247.2, 670.26) * mm});
            skLineSegment(sketch, "E1480", {"start": v(247.2, 670.26) * mm, "end": v(247.53, 670.37) * mm});
            skLineSegment(sketch, "E1481", {"start": v(247.53, 670.37) * mm, "end": v(247.85, 670.48) * mm});
            skLineSegment(sketch, "E1482", {"start": v(247.85, 670.48) * mm, "end": v(248.18, 670.58) * mm});
            skLineSegment(sketch, "E1483", {"start": v(248.18, 670.58) * mm, "end": v(248.51, 670.67) * mm});
            skLineSegment(sketch, "E1484", {"start": v(248.51, 670.67) * mm, "end": v(248.84, 670.75) * mm});
            skLineSegment(sketch, "E1485", {"start": v(248.84, 670.75) * mm, "end": v(249.18, 670.82) * mm});
            skLineSegment(sketch, "E1486", {"start": v(249.18, 670.82) * mm, "end": v(249.51, 670.89) * mm});
            skLineSegment(sketch, "E1487", {"start": v(249.51, 670.89) * mm, "end": v(249.85, 670.94) * mm});
            skLineSegment(sketch, "E1488", {"start": v(249.85, 670.94) * mm, "end": v(250.19, 671) * mm});
            skLineSegment(sketch, "E1489", {"start": v(250.19, 671) * mm, "end": v(250.53, 671.04) * mm});
            skLineSegment(sketch, "E1490", {"start": v(250.53, 671.04) * mm, "end": v(250.87, 671.07) * mm});
            skLineSegment(sketch, "E1491", {"start": v(250.87, 671.07) * mm, "end": v(251.22, 671.1) * mm});
            skLineSegment(sketch, "E1492", {"start": v(251.22, 671.1) * mm, "end": v(251.56, 671.1) * mm});
            skLineSegment(sketch, "E1493", {"start": v(251.56, 671.1) * mm, "end": v(264.39, 671.1) * mm});
            skLineSegment(sketch, "E1494", {"start": v(206.35, 671.1) * mm, "end": v(229.38, 671.1) * mm});
            skLineSegment(sketch, "E1495", {"start": v(229.38, 671.1) * mm, "end": v(229.38, 636.14) * mm});
            skLineSegment(sketch, "E1496", {"start": v(229.38, 636.14) * mm, "end": v(206.35, 636.14) * mm});
            skLineSegment(sketch, "E1497", {"start": v(229.38, 652.99) * mm, "end": v(209.24, 652.99) * mm});
            skLineSegment(sketch, "E1498", {"start": v(-522.34, 637.6) * mm, "end": v(-522.34, 672.56) * mm});
            skLineSegment(sketch, "E1499", {"start": v(-522.34, 672.56) * mm, "end": v(-506.97, 672.56) * mm});
            skLineSegment(sketch, "E1500", {"start": v(-506.97, 672.56) * mm, "end": v(-506.54, 672.56) * mm});
            skLineSegment(sketch, "E1501", {"start": v(-506.54, 672.56) * mm, "end": v(-506.11, 672.53) * mm});
            skLineSegment(sketch, "E1502", {"start": v(-506.11, 672.53) * mm, "end": v(-505.68, 672.48) * mm});
            skLineSegment(sketch, "E1503", {"start": v(-505.68, 672.48) * mm, "end": v(-505.26, 672.42) * mm});
            skLineSegment(sketch, "E1504", {"start": v(-505.26, 672.42) * mm, "end": v(-504.84, 672.33) * mm});
            skLineSegment(sketch, "E1505", {"start": v(-504.84, 672.33) * mm, "end": v(-504.43, 672.21) * mm});
            skLineSegment(sketch, "E1506", {"start": v(-504.43, 672.21) * mm, "end": v(-504.03, 672.08) * mm});
            skLineSegment(sketch, "E1507", {"start": v(-504.03, 672.08) * mm, "end": v(-503.63, 671.93) * mm});
            skLineSegment(sketch, "E1508", {"start": v(-503.63, 671.93) * mm, "end": v(-503.24, 671.76) * mm});
            skLineSegment(sketch, "E1509", {"start": v(-503.24, 671.76) * mm, "end": v(-502.86, 671.57) * mm});
            skLineSegment(sketch, "E1510", {"start": v(-502.86, 671.57) * mm, "end": v(-502.49, 671.35) * mm});
            skLineSegment(sketch, "E1511", {"start": v(-502.49, 671.35) * mm, "end": v(-502.13, 671.12) * mm});
            skLineSegment(sketch, "E1512", {"start": v(-502.13, 671.12) * mm, "end": v(-501.78, 670.88) * mm});
            skLineSegment(sketch, "E1513", {"start": v(-501.78, 670.88) * mm, "end": v(-501.44, 670.6) * mm});
            skLineSegment(sketch, "E1514", {"start": v(-501.44, 670.6) * mm, "end": v(-501.12, 670.32) * mm});
            skLineSegment(sketch, "E1515", {"start": v(-501.12, 670.32) * mm, "end": v(-500.81, 670.02) * mm});
            skLineSegment(sketch, "E1516", {"start": v(-500.81, 670.02) * mm, "end": v(-500.51, 669.71) * mm});
            skLineSegment(sketch, "E1517", {"start": v(-500.51, 669.71) * mm, "end": v(-500.23, 669.4) * mm});
            skLineSegment(sketch, "E1518", {"start": v(-500.23, 669.4) * mm, "end": v(-499.97, 669.06) * mm});
            skLineSegment(sketch, "E1519", {"start": v(-499.97, 669.06) * mm, "end": v(-499.72, 668.71) * mm});
            skLineSegment(sketch, "E1520", {"start": v(-499.72, 668.71) * mm, "end": v(-499.5, 668.36) * mm});
            skLineSegment(sketch, "E1521", {"start": v(-499.5, 668.36) * mm, "end": v(-499.28, 667.99) * mm});
            skLineSegment(sketch, "E1522", {"start": v(-499.28, 667.99) * mm, "end": v(-499.1, 667.61) * mm});
            skLineSegment(sketch, "E1523", {"start": v(-499.1, 667.61) * mm, "end": v(-498.92, 667.23) * mm});
            skLineSegment(sketch, "E1524", {"start": v(-498.92, 667.23) * mm, "end": v(-498.77, 666.83) * mm});
            skLineSegment(sketch, "E1525", {"start": v(-498.77, 666.83) * mm, "end": v(-498.63, 666.43) * mm});
            skLineSegment(sketch, "E1526", {"start": v(-498.63, 666.43) * mm, "end": v(-498.52, 666.02) * mm});
            skLineSegment(sketch, "E1527", {"start": v(-498.52, 666.02) * mm, "end": v(-498.43, 665.61) * mm});
            skLineSegment(sketch, "E1528", {"start": v(-498.43, 665.61) * mm, "end": v(-498.35, 665.2) * mm});
            skLineSegment(sketch, "E1529", {"start": v(-498.35, 665.2) * mm, "end": v(-498.3, 664.77) * mm});
            skLineSegment(sketch, "E1530", {"start": v(-498.3, 664.77) * mm, "end": v(-498.27, 664.35) * mm});
            skLineSegment(sketch, "E1531", {"start": v(-498.27, 664.35) * mm, "end": v(-498.26, 663.92) * mm});
            skLineSegment(sketch, "E1532", {"start": v(-498.26, 663.92) * mm, "end": v(-498.26, 663.48) * mm});
            skLineSegment(sketch, "E1533", {"start": v(-498.26, 663.48) * mm, "end": v(-498.28, 663.04) * mm});
            skLineSegment(sketch, "E1534", {"start": v(-498.28, 663.04) * mm, "end": v(-498.32, 662.6) * mm});
            skLineSegment(sketch, "E1535", {"start": v(-498.32, 662.6) * mm, "end": v(-498.38, 662.18) * mm});
            skLineSegment(sketch, "E1536", {"start": v(-498.38, 662.18) * mm, "end": v(-498.47, 661.75) * mm});
            skLineSegment(sketch, "E1537", {"start": v(-498.47, 661.75) * mm, "end": v(-498.58, 661.33) * mm});
            skLineSegment(sketch, "E1538", {"start": v(-498.58, 661.33) * mm, "end": v(-498.7, 660.92) * mm});
            skLineSegment(sketch, "E1539", {"start": v(-498.7, 660.92) * mm, "end": v(-498.85, 660.51) * mm});
            skLineSegment(sketch, "E1540", {"start": v(-498.85, 660.51) * mm, "end": v(-499.02, 660.12) * mm});
            skLineSegment(sketch, "E1541", {"start": v(-499.02, 660.12) * mm, "end": v(-499.2, 659.73) * mm});
            skLineSegment(sketch, "E1542", {"start": v(-499.2, 659.73) * mm, "end": v(-499.42, 659.35) * mm});
            skLineSegment(sketch, "E1543", {"start": v(-499.42, 659.35) * mm, "end": v(-499.65, 658.98) * mm});
            skLineSegment(sketch, "E1544", {"start": v(-499.65, 658.98) * mm, "end": v(-499.9, 658.62) * mm});
            skLineSegment(sketch, "E1545", {"start": v(-499.9, 658.62) * mm, "end": v(-500.16, 658.27) * mm});
            skLineSegment(sketch, "E1546", {"start": v(-500.16, 658.27) * mm, "end": v(-500.44, 657.94) * mm});
            skLineSegment(sketch, "E1547", {"start": v(-500.44, 657.94) * mm, "end": v(-500.74, 657.62) * mm});
            skLineSegment(sketch, "E1548", {"start": v(-500.74, 657.62) * mm, "end": v(-501.06, 657.32) * mm});
            skLineSegment(sketch, "E1549", {"start": v(-501.06, 657.32) * mm, "end": v(-501.39, 657.04) * mm});
            skLineSegment(sketch, "E1550", {"start": v(-501.39, 657.04) * mm, "end": v(-501.73, 656.77) * mm});
            skLineSegment(sketch, "E1551", {"start": v(-501.73, 656.77) * mm, "end": v(-502.08, 656.52) * mm});
            skLineSegment(sketch, "E1552", {"start": v(-502.08, 656.52) * mm, "end": v(-502.45, 656.3) * mm});
            skLineSegment(sketch, "E1553", {"start": v(-502.45, 656.3) * mm, "end": v(-502.82, 656.08) * mm});
            skLineSegment(sketch, "E1554", {"start": v(-502.82, 656.08) * mm, "end": v(-503.2, 655.9) * mm});
            skLineSegment(sketch, "E1555", {"start": v(-503.2, 655.9) * mm, "end": v(-503.6, 655.72) * mm});
            skLineSegment(sketch, "E1556", {"start": v(-503.6, 655.72) * mm, "end": v(-504, 655.57) * mm});
            skLineSegment(sketch, "E1557", {"start": v(-504, 655.57) * mm, "end": v(-504.41, 655.44) * mm});
            skLineSegment(sketch, "E1558", {"start": v(-504.41, 655.44) * mm, "end": v(-504.83, 655.33) * mm});
            skLineSegment(sketch, "E1559", {"start": v(-504.83, 655.33) * mm, "end": v(-505.25, 655.24) * mm});
            skLineSegment(sketch, "E1560", {"start": v(-505.25, 655.24) * mm, "end": v(-505.67, 655.17) * mm});
            skLineSegment(sketch, "E1561", {"start": v(-505.67, 655.17) * mm, "end": v(-506.1, 655.12) * mm});
            skLineSegment(sketch, "E1562", {"start": v(-506.1, 655.12) * mm, "end": v(-506.54, 655.1) * mm});
            skLineSegment(sketch, "E1563", {"start": v(-506.54, 655.1) * mm, "end": v(-506.97, 655.09) * mm});
            skLineSegment(sketch, "E1564", {"start": v(-506.97, 655.09) * mm, "end": v(-522.34, 655.09) * mm});
            skLineSegment(sketch, "E1565", {"start": v(-506.97, 655.09) * mm, "end": v(-506.62, 655.08) * mm});
            skLineSegment(sketch, "E1566", {"start": v(-506.62, 655.08) * mm, "end": v(-506.26, 655.06) * mm});
            skLineSegment(sketch, "E1567", {"start": v(-506.26, 655.06) * mm, "end": v(-505.9, 655.03) * mm});
            skLineSegment(sketch, "E1568", {"start": v(-505.9, 655.03) * mm, "end": v(-505.55, 654.97) * mm});
            skLineSegment(sketch, "E1569", {"start": v(-505.55, 654.97) * mm, "end": v(-505.2, 654.9) * mm});
            skLineSegment(sketch, "E1570", {"start": v(-505.2, 654.9) * mm, "end": v(-504.87, 654.8) * mm});
            skLineSegment(sketch, "E1571", {"start": v(-504.87, 654.8) * mm, "end": v(-504.53, 654.7) * mm});
            skLineSegment(sketch, "E1572", {"start": v(-504.53, 654.7) * mm, "end": v(-504.2, 654.57) * mm});
            skLineSegment(sketch, "E1573", {"start": v(-504.2, 654.57) * mm, "end": v(-503.88, 654.43) * mm});
            skLineSegment(sketch, "E1574", {"start": v(-503.88, 654.43) * mm, "end": v(-503.56, 654.27) * mm});
            skLineSegment(sketch, "E1575", {"start": v(-503.56, 654.27) * mm, "end": v(-503.25, 654.1) * mm});
            skLineSegment(sketch, "E1576", {"start": v(-503.25, 654.1) * mm, "end": v(-502.95, 653.9) * mm});
            skLineSegment(sketch, "E1577", {"start": v(-502.95, 653.9) * mm, "end": v(-502.66, 653.7) * mm});
            skLineSegment(sketch, "E1578", {"start": v(-502.66, 653.7) * mm, "end": v(-502.38, 653.48) * mm});
            skLineSegment(sketch, "E1579", {"start": v(-502.38, 653.48) * mm, "end": v(-502.11, 653.25) * mm});
            skLineSegment(sketch, "E1580", {"start": v(-502.11, 653.25) * mm, "end": v(-501.85, 653) * mm});
            skLineSegment(sketch, "E1581", {"start": v(-501.85, 653) * mm, "end": v(-501.56, 652.56) * mm});
            skLineSegment(sketch, "E1582", {"start": v(-501.56, 652.56) * mm, "end": v(-501.28, 652.11) * mm});
            skLineSegment(sketch, "E1583", {"start": v(-501.28, 652.11) * mm, "end": v(-501.02, 651.65) * mm});
            skLineSegment(sketch, "E1584", {"start": v(-501.02, 651.65) * mm, "end": v(-500.79, 651.18) * mm});
            skLineSegment(sketch, "E1585", {"start": v(-500.79, 651.18) * mm, "end": v(-500.57, 650.7) * mm});
            skLineSegment(sketch, "E1586", {"start": v(-500.57, 650.7) * mm, "end": v(-500.38, 650.22) * mm});
            skLineSegment(sketch, "E1587", {"start": v(-500.38, 650.22) * mm, "end": v(-500.21, 649.72) * mm});
            skLineSegment(sketch, "E1588", {"start": v(-500.21, 649.72) * mm, "end": v(-500.06, 649.22) * mm});
            skLineSegment(sketch, "E1589", {"start": v(-500.06, 649.22) * mm, "end": v(-499.94, 648.71) * mm});
            skLineSegment(sketch, "E1590", {"start": v(-499.94, 648.71) * mm, "end": v(-499.83, 648.2) * mm});
            skLineSegment(sketch, "E1591", {"start": v(-499.83, 648.2) * mm, "end": v(-499.75, 647.68) * mm});
            skLineSegment(sketch, "E1592", {"start": v(-499.75, 647.68) * mm, "end": v(-499.7, 647.16) * mm});
            skLineSegment(sketch, "E1593", {"start": v(-499.7, 647.16) * mm, "end": v(-499.66, 646.63) * mm});
            skLineSegment(sketch, "E1594", {"start": v(-499.66, 646.63) * mm, "end": v(-499.65, 646.1) * mm});
            skLineSegment(sketch, "E1595", {"start": v(-499.65, 646.1) * mm, "end": v(-499.66, 645.58) * mm});
            skLineSegment(sketch, "E1596", {"start": v(-499.66, 645.58) * mm, "end": v(-499.7, 645.05) * mm});
            skLineSegment(sketch, "E1597", {"start": v(-499.7, 645.05) * mm, "end": v(-499.7, 644.58) * mm});
            skLineSegment(sketch, "E1598", {"start": v(-499.7, 644.58) * mm, "end": v(-499.7, 644.1) * mm});
            skLineSegment(sketch, "E1599", {"start": v(-499.7, 644.1) * mm, "end": v(-499.7, 643.64) * mm});
            skLineSegment(sketch, "E1600", {"start": v(-499.7, 643.64) * mm, "end": v(-499.68, 643.17) * mm});
            skLineSegment(sketch, "E1601", {"start": v(-499.68, 643.17) * mm, "end": v(-499.65, 642.7) * mm});
            skLineSegment(sketch, "E1602", {"start": v(-499.65, 642.7) * mm, "end": v(-499.62, 642.23) * mm});
            skLineSegment(sketch, "E1603", {"start": v(-499.62, 642.23) * mm, "end": v(-499.57, 641.76) * mm});
            skLineSegment(sketch, "E1604", {"start": v(-499.57, 641.76) * mm, "end": v(-499.52, 641.3) * mm});
            skLineSegment(sketch, "E1605", {"start": v(-499.52, 641.3) * mm, "end": v(-499.46, 640.82) * mm});
            skLineSegment(sketch, "E1606", {"start": v(-499.46, 640.82) * mm, "end": v(-499.39, 640.36) * mm});
            skLineSegment(sketch, "E1607", {"start": v(-499.39, 640.36) * mm, "end": v(-499.31, 639.9) * mm});
            skLineSegment(sketch, "E1608", {"start": v(-499.31, 639.9) * mm, "end": v(-499.23, 639.43) * mm});
            skLineSegment(sketch, "E1609", {"start": v(-499.23, 639.43) * mm, "end": v(-499.13, 638.97) * mm});
            skLineSegment(sketch, "E1610", {"start": v(-499.13, 638.97) * mm, "end": v(-499.03, 638.5) * mm});
            skLineSegment(sketch, "E1611", {"start": v(-499.03, 638.5) * mm, "end": v(-498.92, 638.05) * mm});
            skLineSegment(sketch, "E1612", {"start": v(-498.92, 638.05) * mm, "end": v(-498.8, 637.6) * mm});
            skLineSegment(sketch, "E1613", {"start": v(-476.13, 637.1) * mm, "end": v(-476.5, 637.1) * mm});
            skLineSegment(sketch, "E1614", {"start": v(-476.5, 637.1) * mm, "end": v(-476.87, 637.1) * mm});
            skLineSegment(sketch, "E1615", {"start": v(-476.87, 637.1) * mm, "end": v(-477.23, 637.12) * mm});
            skLineSegment(sketch, "E1616", {"start": v(-477.23, 637.12) * mm, "end": v(-477.6, 637.15) * mm});
            skLineSegment(sketch, "E1617", {"start": v(-477.6, 637.15) * mm, "end": v(-477.96, 637.18) * mm});
            skLineSegment(sketch, "E1618", {"start": v(-477.96, 637.18) * mm, "end": v(-478.32, 637.23) * mm});
            skLineSegment(sketch, "E1619", {"start": v(-478.32, 637.23) * mm, "end": v(-478.68, 637.28) * mm});
            skLineSegment(sketch, "E1620", {"start": v(-478.68, 637.28) * mm, "end": v(-479.04, 637.34) * mm});
            skLineSegment(sketch, "E1621", {"start": v(-479.04, 637.34) * mm, "end": v(-479.4, 637.4) * mm});
            skLineSegment(sketch, "E1622", {"start": v(-479.4, 637.4) * mm, "end": v(-479.75, 637.49) * mm});
            skLineSegment(sketch, "E1623", {"start": v(-479.75, 637.49) * mm, "end": v(-480.1, 637.57) * mm});
            skLineSegment(sketch, "E1624", {"start": v(-480.1, 637.57) * mm, "end": v(-480.45, 637.67) * mm});
            skLineSegment(sketch, "E1625", {"start": v(-480.45, 637.67) * mm, "end": v(-480.8, 637.77) * mm});
            skLineSegment(sketch, "E1626", {"start": v(-480.8, 637.77) * mm, "end": v(-481.14, 637.89) * mm});
            skLineSegment(sketch, "E1627", {"start": v(-481.14, 637.89) * mm, "end": v(-481.48, 638) * mm});
            skLineSegment(sketch, "E1628", {"start": v(-481.48, 638) * mm, "end": v(-481.82, 638.14) * mm});
            skLineSegment(sketch, "E1629", {"start": v(-481.82, 638.14) * mm, "end": v(-482.16, 638.28) * mm});
            skLineSegment(sketch, "E1630", {"start": v(-482.16, 638.28) * mm, "end": v(-482.49, 638.42) * mm});
            skLineSegment(sketch, "E1631", {"start": v(-482.49, 638.42) * mm, "end": v(-482.81, 638.58) * mm});
            skLineSegment(sketch, "E1632", {"start": v(-482.81, 638.58) * mm, "end": v(-483.14, 638.74) * mm});
            skLineSegment(sketch, "E1633", {"start": v(-483.14, 638.74) * mm, "end": v(-483.46, 638.91) * mm});
            skLineSegment(sketch, "E1634", {"start": v(-483.46, 638.91) * mm, "end": v(-483.77, 639.09) * mm});
            skLineSegment(sketch, "E1635", {"start": v(-483.77, 639.09) * mm, "end": v(-484.08, 639.28) * mm});
            skLineSegment(sketch, "E1636", {"start": v(-484.08, 639.28) * mm, "end": v(-484.4, 639.47) * mm});
            skLineSegment(sketch, "E1637", {"start": v(-484.4, 639.47) * mm, "end": v(-484.7, 639.67) * mm});
            skLineSegment(sketch, "E1638", {"start": v(-484.7, 639.67) * mm, "end": v(-485, 639.88) * mm});
            skLineSegment(sketch, "E1639", {"start": v(-485, 639.88) * mm, "end": v(-485.28, 640.1) * mm});
            skLineSegment(sketch, "E1640", {"start": v(-485.28, 640.1) * mm, "end": v(-485.57, 640.33) * mm});
            skLineSegment(sketch, "E1641", {"start": v(-485.57, 640.33) * mm, "end": v(-485.85, 640.56) * mm});
            skLineSegment(sketch, "E1642", {"start": v(-485.85, 640.56) * mm, "end": v(-486.13, 640.8) * mm});
            skLineSegment(sketch, "E1643", {"start": v(-486.13, 640.8) * mm, "end": v(-486.4, 641.05) * mm});
            skLineSegment(sketch, "E1644", {"start": v(-486.4, 641.05) * mm, "end": v(-486.66, 641.3) * mm});
            skLineSegment(sketch, "E1645", {"start": v(-486.66, 641.3) * mm, "end": v(-486.97, 641.63) * mm});
            skLineSegment(sketch, "E1646", {"start": v(-486.97, 641.63) * mm, "end": v(-487.27, 641.97) * mm});
            skLineSegment(sketch, "E1647", {"start": v(-487.27, 641.97) * mm, "end": v(-487.55, 642.32) * mm});
            skLineSegment(sketch, "E1648", {"start": v(-487.55, 642.32) * mm, "end": v(-487.83, 642.67) * mm});
            skLineSegment(sketch, "E1649", {"start": v(-487.83, 642.67) * mm, "end": v(-488.1, 643.03) * mm});
            skLineSegment(sketch, "E1650", {"start": v(-488.1, 643.03) * mm, "end": v(-488.36, 643.4) * mm});
            skLineSegment(sketch, "E1651", {"start": v(-488.36, 643.4) * mm, "end": v(-488.61, 643.77) * mm});
            skLineSegment(sketch, "E1652", {"start": v(-488.61, 643.77) * mm, "end": v(-488.85, 644.14) * mm});
            skLineSegment(sketch, "E1653", {"start": v(-488.85, 644.14) * mm, "end": v(-489.09, 644.53) * mm});
            skLineSegment(sketch, "E1654", {"start": v(-489.09, 644.53) * mm, "end": v(-489.3, 644.91) * mm});
            skLineSegment(sketch, "E1655", {"start": v(-489.3, 644.91) * mm, "end": v(-489.52, 645.3) * mm});
            skLineSegment(sketch, "E1656", {"start": v(-489.52, 645.3) * mm, "end": v(-489.72, 645.7) * mm});
            skLineSegment(sketch, "E1657", {"start": v(-489.72, 645.7) * mm, "end": v(-489.91, 646.1) * mm});
            skLineSegment(sketch, "E1658", {"start": v(-489.91, 646.1) * mm, "end": v(-490.1, 646.51) * mm});
            skLineSegment(sketch, "E1659", {"start": v(-490.1, 646.51) * mm, "end": v(-490.27, 646.93) * mm});
            skLineSegment(sketch, "E1660", {"start": v(-490.27, 646.93) * mm, "end": v(-490.43, 647.34) * mm});
            skLineSegment(sketch, "E1661", {"start": v(-490.43, 647.34) * mm, "end": v(-490.58, 647.76) * mm});
            skLineSegment(sketch, "E1662", {"start": v(-490.58, 647.76) * mm, "end": v(-490.72, 648.18) * mm});
            skLineSegment(sketch, "E1663", {"start": v(-490.72, 648.18) * mm, "end": v(-490.86, 648.6) * mm});
            skLineSegment(sketch, "E1664", {"start": v(-490.86, 648.6) * mm, "end": v(-490.98, 649.04) * mm});
            skLineSegment(sketch, "E1665", {"start": v(-490.98, 649.04) * mm, "end": v(-491.09, 649.47) * mm});
            skLineSegment(sketch, "E1666", {"start": v(-491.09, 649.47) * mm, "end": v(-491.19, 649.9) * mm});
            skLineSegment(sketch, "E1667", {"start": v(-491.19, 649.9) * mm, "end": v(-491.28, 650.34) * mm});
            skLineSegment(sketch, "E1668", {"start": v(-491.28, 650.34) * mm, "end": v(-491.36, 650.78) * mm});
            skLineSegment(sketch, "E1669", {"start": v(-491.36, 650.78) * mm, "end": v(-491.42, 651.22) * mm});
            skLineSegment(sketch, "E1670", {"start": v(-491.42, 651.22) * mm, "end": v(-491.48, 651.67) * mm});
            skLineSegment(sketch, "E1671", {"start": v(-491.48, 651.67) * mm, "end": v(-491.52, 652.11) * mm});
            skLineSegment(sketch, "E1672", {"start": v(-491.52, 652.11) * mm, "end": v(-491.56, 652.56) * mm});
            skLineSegment(sketch, "E1673", {"start": v(-491.56, 652.56) * mm, "end": v(-491.58, 653.01) * mm});
            skLineSegment(sketch, "E1674", {"start": v(-491.58, 653.01) * mm, "end": v(-491.6, 653.46) * mm});
            skLineSegment(sketch, "E1675", {"start": v(-491.6, 653.46) * mm, "end": v(-491.6, 653.91) * mm});
            skLineSegment(sketch, "E1676", {"start": v(-491.6, 653.91) * mm, "end": v(-491.59, 654.37) * mm});
            skLineSegment(sketch, "E1677", {"start": v(-491.59, 654.37) * mm, "end": v(-491.6, 654.86) * mm});
            skLineSegment(sketch, "E1678", {"start": v(-491.6, 654.86) * mm, "end": v(-491.6, 655.35) * mm});
            skLineSegment(sketch, "E1679", {"start": v(-491.6, 655.35) * mm, "end": v(-491.6, 655.84) * mm});
            skLineSegment(sketch, "E1680", {"start": v(-491.6, 655.84) * mm, "end": v(-491.57, 656.32) * mm});
            skLineSegment(sketch, "E1681", {"start": v(-491.57, 656.32) * mm, "end": v(-491.53, 656.8) * mm});
            skLineSegment(sketch, "E1682", {"start": v(-491.53, 656.8) * mm, "end": v(-491.48, 657.3) * mm});
            skLineSegment(sketch, "E1683", {"start": v(-491.48, 657.3) * mm, "end": v(-491.42, 657.78) * mm});
            skLineSegment(sketch, "E1684", {"start": v(-491.42, 657.78) * mm, "end": v(-491.35, 658.26) * mm});
            skLineSegment(sketch, "E1685", {"start": v(-491.35, 658.26) * mm, "end": v(-491.27, 658.74) * mm});
            skLineSegment(sketch, "E1686", {"start": v(-491.27, 658.74) * mm, "end": v(-491.17, 659.21) * mm});
            skLineSegment(sketch, "E1687", {"start": v(-491.17, 659.21) * mm, "end": v(-491.07, 659.68) * mm});
            skLineSegment(sketch, "E1688", {"start": v(-491.07, 659.68) * mm, "end": v(-490.95, 660.15) * mm});
            skLineSegment(sketch, "E1689", {"start": v(-490.95, 660.15) * mm, "end": v(-490.82, 660.62) * mm});
            skLineSegment(sketch, "E1690", {"start": v(-490.82, 660.62) * mm, "end": v(-490.68, 661.08) * mm});
            skLineSegment(sketch, "E1691", {"start": v(-490.68, 661.08) * mm, "end": v(-490.52, 661.54) * mm});
            skLineSegment(sketch, "E1692", {"start": v(-490.52, 661.54) * mm, "end": v(-490.36, 662) * mm});
            skLineSegment(sketch, "E1693", {"start": v(-490.36, 662) * mm, "end": v(-490.18, 662.45) * mm});
            skLineSegment(sketch, "E1694", {"start": v(-490.18, 662.45) * mm, "end": v(-490, 662.9) * mm});
            skLineSegment(sketch, "E1695", {"start": v(-490, 662.9) * mm, "end": v(-489.8, 663.33) * mm});
            skLineSegment(sketch, "E1696", {"start": v(-489.8, 663.33) * mm, "end": v(-489.59, 663.77) * mm});
            skLineSegment(sketch, "E1697", {"start": v(-489.59, 663.77) * mm, "end": v(-489.37, 664.2) * mm});
            skLineSegment(sketch, "E1698", {"start": v(-489.37, 664.2) * mm, "end": v(-489.14, 664.63) * mm});
            skLineSegment(sketch, "E1699", {"start": v(-489.14, 664.63) * mm, "end": v(-488.9, 665.05) * mm});
            skLineSegment(sketch, "E1700", {"start": v(-488.9, 665.05) * mm, "end": v(-488.64, 665.46) * mm});
            skLineSegment(sketch, "E1701", {"start": v(-488.64, 665.46) * mm, "end": v(-488.38, 665.87) * mm});
            skLineSegment(sketch, "E1702", {"start": v(-488.38, 665.87) * mm, "end": v(-488.1, 666.28) * mm});
            skLineSegment(sketch, "E1703", {"start": v(-488.1, 666.28) * mm, "end": v(-487.83, 666.67) * mm});
            skLineSegment(sketch, "E1704", {"start": v(-487.83, 666.67) * mm, "end": v(-487.53, 667.06) * mm});
            skLineSegment(sketch, "E1705", {"start": v(-487.53, 667.06) * mm, "end": v(-487.23, 667.44) * mm});
            skLineSegment(sketch, "E1706", {"start": v(-487.23, 667.44) * mm, "end": v(-486.91, 667.82) * mm});
            skLineSegment(sketch, "E1707", {"start": v(-486.91, 667.82) * mm, "end": v(-486.6, 668.19) * mm});
            skLineSegment(sketch, "E1708", {"start": v(-486.6, 668.19) * mm, "end": v(-486.26, 668.55) * mm});
            skLineSegment(sketch, "E1709", {"start": v(-486.26, 668.55) * mm, "end": v(-486, 668.8) * mm});
            skLineSegment(sketch, "E1710", {"start": v(-486, 668.8) * mm, "end": v(-485.75, 669.05) * mm});
            skLineSegment(sketch, "E1711", {"start": v(-485.75, 669.05) * mm, "end": v(-485.49, 669.29) * mm});
            skLineSegment(sketch, "E1712", {"start": v(-485.49, 669.29) * mm, "end": v(-485.22, 669.52) * mm});
            skLineSegment(sketch, "E1713", {"start": v(-485.22, 669.52) * mm, "end": v(-484.95, 669.75) * mm});
            skLineSegment(sketch, "E1714", {"start": v(-484.95, 669.75) * mm, "end": v(-484.67, 669.96) * mm});
            skLineSegment(sketch, "E1715", {"start": v(-484.67, 669.96) * mm, "end": v(-484.39, 670.17) * mm});
            skLineSegment(sketch, "E1716", {"start": v(-484.39, 670.17) * mm, "end": v(-484.1, 670.38) * mm});
            skLineSegment(sketch, "E1717", {"start": v(-484.1, 670.38) * mm, "end": v(-483.8, 670.57) * mm});
            skLineSegment(sketch, "E1718", {"start": v(-483.8, 670.57) * mm, "end": v(-483.5, 670.76) * mm});
            skLineSegment(sketch, "E1719", {"start": v(-483.5, 670.76) * mm, "end": v(-483.2, 670.94) * mm});
            skLineSegment(sketch, "E1720", {"start": v(-483.2, 670.94) * mm, "end": v(-482.9, 671.1) * mm});
            skLineSegment(sketch, "E1721", {"start": v(-482.9, 671.1) * mm, "end": v(-482.59, 671.27) * mm});
            skLineSegment(sketch, "E1722", {"start": v(-482.59, 671.27) * mm, "end": v(-482.27, 671.43) * mm});
            skLineSegment(sketch, "E1723", {"start": v(-482.27, 671.43) * mm, "end": v(-481.95, 671.58) * mm});
            skLineSegment(sketch, "E1724", {"start": v(-481.95, 671.58) * mm, "end": v(-481.63, 671.71) * mm});
            skLineSegment(sketch, "E1725", {"start": v(-481.63, 671.71) * mm, "end": v(-481.3, 671.85) * mm});
            skLineSegment(sketch, "E1726", {"start": v(-481.3, 671.85) * mm, "end": v(-480.98, 671.97) * mm});
            skLineSegment(sketch, "E1727", {"start": v(-480.98, 671.97) * mm, "end": v(-480.64, 672.08) * mm});
            skLineSegment(sketch, "E1728", {"start": v(-480.64, 672.08) * mm, "end": v(-480.3, 672.19) * mm});
            skLineSegment(sketch, "E1729", {"start": v(-480.3, 672.19) * mm, "end": v(-479.97, 672.29) * mm});
            skLineSegment(sketch, "E1730", {"start": v(-479.97, 672.29) * mm, "end": v(-479.63, 672.37) * mm});
            skLineSegment(sketch, "E1731", {"start": v(-479.63, 672.37) * mm, "end": v(-479.29, 672.45) * mm});
            skLineSegment(sketch, "E1732", {"start": v(-479.29, 672.45) * mm, "end": v(-478.94, 672.52) * mm});
            skLineSegment(sketch, "E1733", {"start": v(-478.94, 672.52) * mm, "end": v(-478.6, 672.59) * mm});
            skLineSegment(sketch, "E1734", {"start": v(-478.6, 672.59) * mm, "end": v(-478.25, 672.64) * mm});
            skLineSegment(sketch, "E1735", {"start": v(-478.25, 672.64) * mm, "end": v(-477.9, 672.69) * mm});
            skLineSegment(sketch, "E1736", {"start": v(-477.9, 672.69) * mm, "end": v(-477.55, 672.72) * mm});
            skLineSegment(sketch, "E1737", {"start": v(-477.55, 672.72) * mm, "end": v(-477.2, 672.75) * mm});
            skLineSegment(sketch, "E1738", {"start": v(-477.2, 672.75) * mm, "end": v(-476.84, 672.76) * mm});
            skLineSegment(sketch, "E1739", {"start": v(-476.84, 672.76) * mm, "end": v(-476.48, 672.77) * mm});
            skLineSegment(sketch, "E1740", {"start": v(-476.48, 672.77) * mm, "end": v(-476.12, 672.77) * mm});
            skLineSegment(sketch, "E1741", {"start": v(-476.12, 672.77) * mm, "end": v(-475.76, 672.77) * mm});
            skLineSegment(sketch, "E1742", {"start": v(-475.76, 672.77) * mm, "end": v(-475.4, 672.75) * mm});
            skLineSegment(sketch, "E1743", {"start": v(-475.4, 672.75) * mm, "end": v(-475.04, 672.73) * mm});
            skLineSegment(sketch, "E1744", {"start": v(-475.04, 672.73) * mm, "end": v(-474.68, 672.7) * mm});
            skLineSegment(sketch, "E1745", {"start": v(-474.68, 672.7) * mm, "end": v(-474.32, 672.66) * mm});
            skLineSegment(sketch, "E1746", {"start": v(-474.32, 672.66) * mm, "end": v(-473.97, 672.61) * mm});
            skLineSegment(sketch, "E1747", {"start": v(-473.97, 672.61) * mm, "end": v(-473.61, 672.55) * mm});
            skLineSegment(sketch, "E1748", {"start": v(-473.61, 672.55) * mm, "end": v(-473.26, 672.48) * mm});
            skLineSegment(sketch, "E1749", {"start": v(-473.26, 672.48) * mm, "end": v(-472.91, 672.4) * mm});
            skLineSegment(sketch, "E1750", {"start": v(-472.91, 672.4) * mm, "end": v(-472.57, 672.32) * mm});
            skLineSegment(sketch, "E1751", {"start": v(-472.57, 672.32) * mm, "end": v(-472.22, 672.23) * mm});
            skLineSegment(sketch, "E1752", {"start": v(-472.22, 672.23) * mm, "end": v(-471.88, 672.12) * mm});
            skLineSegment(sketch, "E1753", {"start": v(-471.88, 672.12) * mm, "end": v(-471.54, 672.01) * mm});
            skLineSegment(sketch, "E1754", {"start": v(-471.54, 672.01) * mm, "end": v(-471.2, 671.9) * mm});
            skLineSegment(sketch, "E1755", {"start": v(-471.2, 671.9) * mm, "end": v(-470.87, 671.76) * mm});
            skLineSegment(sketch, "E1756", {"start": v(-470.87, 671.76) * mm, "end": v(-470.54, 671.63) * mm});
            skLineSegment(sketch, "E1757", {"start": v(-470.54, 671.63) * mm, "end": v(-470.22, 671.48) * mm});
            skLineSegment(sketch, "E1758", {"start": v(-470.22, 671.48) * mm, "end": v(-469.9, 671.33) * mm});
            skLineSegment(sketch, "E1759", {"start": v(-469.9, 671.33) * mm, "end": v(-469.58, 671.17) * mm});
            skLineSegment(sketch, "E1760", {"start": v(-469.58, 671.17) * mm, "end": v(-469.26, 671) * mm});
            skLineSegment(sketch, "E1761", {"start": v(-469.26, 671) * mm, "end": v(-468.95, 670.82) * mm});
            skLineSegment(sketch, "E1762", {"start": v(-468.95, 670.82) * mm, "end": v(-468.65, 670.63) * mm});
            skLineSegment(sketch, "E1763", {"start": v(-468.65, 670.63) * mm, "end": v(-468.35, 670.44) * mm});
            skLineSegment(sketch, "E1764", {"start": v(-468.35, 670.44) * mm, "end": v(-468.05, 670.24) * mm});
            skLineSegment(sketch, "E1765", {"start": v(-468.05, 670.24) * mm, "end": v(-467.76, 670.03) * mm});
            skLineSegment(sketch, "E1766", {"start": v(-467.76, 670.03) * mm, "end": v(-467.47, 669.81) * mm});
            skLineSegment(sketch, "E1767", {"start": v(-467.47, 669.81) * mm, "end": v(-467.2, 669.59) * mm});
            skLineSegment(sketch, "E1768", {"start": v(-467.2, 669.59) * mm, "end": v(-466.92, 669.35) * mm});
            skLineSegment(sketch, "E1769", {"start": v(-466.92, 669.35) * mm, "end": v(-466.65, 669.11) * mm});
            skLineSegment(sketch, "E1770", {"start": v(-466.65, 669.11) * mm, "end": v(-466.39, 668.87) * mm});
            skLineSegment(sketch, "E1771", {"start": v(-466.39, 668.87) * mm, "end": v(-466.13, 668.61) * mm});
            skLineSegment(sketch, "E1772", {"start": v(-466.13, 668.61) * mm, "end": v(-465.88, 668.35) * mm});
            skLineSegment(sketch, "E1773", {"start": v(-465.88, 668.35) * mm, "end": v(-465.56, 668) * mm});
            skLineSegment(sketch, "E1774", {"start": v(-465.56, 668) * mm, "end": v(-465.24, 667.63) * mm});
            skLineSegment(sketch, "E1775", {"start": v(-465.24, 667.63) * mm, "end": v(-464.94, 667.25) * mm});
            skLineSegment(sketch, "E1776", {"start": v(-464.94, 667.25) * mm, "end": v(-464.64, 666.87) * mm});
            skLineSegment(sketch, "E1777", {"start": v(-464.64, 666.87) * mm, "end": v(-464.36, 666.49) * mm});
            skLineSegment(sketch, "E1778", {"start": v(-464.36, 666.49) * mm, "end": v(-464.08, 666.1) * mm});
            skLineSegment(sketch, "E1779", {"start": v(-464.08, 666.1) * mm, "end": v(-463.82, 665.7) * mm});
            skLineSegment(sketch, "E1780", {"start": v(-463.82, 665.7) * mm, "end": v(-463.57, 665.3) * mm});
            skLineSegment(sketch, "E1781", {"start": v(-463.57, 665.3) * mm, "end": v(-463.32, 664.88) * mm});
            skLineSegment(sketch, "E1782", {"start": v(-463.32, 664.88) * mm, "end": v(-463.1, 664.46) * mm});
            skLineSegment(sketch, "E1783", {"start": v(-463.1, 664.46) * mm, "end": v(-462.87, 664.04) * mm});
            skLineSegment(sketch, "E1784", {"start": v(-462.87, 664.04) * mm, "end": v(-462.66, 663.62) * mm});
            skLineSegment(sketch, "E1785", {"start": v(-462.66, 663.62) * mm, "end": v(-462.46, 663.18) * mm});
            skLineSegment(sketch, "E1786", {"start": v(-462.46, 663.18) * mm, "end": v(-462.27, 662.75) * mm});
            skLineSegment(sketch, "E1787", {"start": v(-462.27, 662.75) * mm, "end": v(-462.09, 662.3) * mm});
            skLineSegment(sketch, "E1788", {"start": v(-462.09, 662.3) * mm, "end": v(-461.92, 661.86) * mm});
            skLineSegment(sketch, "E1789", {"start": v(-461.92, 661.86) * mm, "end": v(-461.76, 661.41) * mm});
            skLineSegment(sketch, "E1790", {"start": v(-461.76, 661.41) * mm, "end": v(-461.61, 660.96) * mm});
            skLineSegment(sketch, "E1791", {"start": v(-461.61, 660.96) * mm, "end": v(-461.48, 660.5) * mm});
            skLineSegment(sketch, "E1792", {"start": v(-461.48, 660.5) * mm, "end": v(-461.35, 660.04) * mm});
            skLineSegment(sketch, "E1793", {"start": v(-461.35, 660.04) * mm, "end": v(-461.24, 659.58) * mm});
            skLineSegment(sketch, "E1794", {"start": v(-461.24, 659.58) * mm, "end": v(-461.14, 659.11) * mm});
            skLineSegment(sketch, "E1795", {"start": v(-461.14, 659.11) * mm, "end": v(-461.05, 658.65) * mm});
            skLineSegment(sketch, "E1796", {"start": v(-461.05, 658.65) * mm, "end": v(-460.97, 658.17) * mm});
            skLineSegment(sketch, "E1797", {"start": v(-460.97, 658.17) * mm, "end": v(-460.9, 657.7) * mm});
            skLineSegment(sketch, "E1798", {"start": v(-460.9, 657.7) * mm, "end": v(-460.85, 657.23) * mm});
            skLineSegment(sketch, "E1799", {"start": v(-460.85, 657.23) * mm, "end": v(-460.8, 656.75) * mm});
            skLineSegment(sketch, "E1800", {"start": v(-460.8, 656.75) * mm, "end": v(-460.78, 656.27) * mm});
            skLineSegment(sketch, "E1801", {"start": v(-460.78, 656.27) * mm, "end": v(-460.76, 655.79) * mm});
            skLineSegment(sketch, "E1802", {"start": v(-460.76, 655.79) * mm, "end": v(-460.75, 655.3) * mm});
            skLineSegment(sketch, "E1803", {"start": v(-460.75, 655.3) * mm, "end": v(-460.76, 654.83) * mm});
            skLineSegment(sketch, "E1804", {"start": v(-460.76, 654.83) * mm, "end": v(-460.77, 654.34) * mm});
            skLineSegment(sketch, "E1805", {"start": v(-460.77, 654.34) * mm, "end": v(-460.77, 653.9) * mm});
            skLineSegment(sketch, "E1806", {"start": v(-460.77, 653.9) * mm, "end": v(-460.77, 653.44) * mm});
            skLineSegment(sketch, "E1807", {"start": v(-460.77, 653.44) * mm, "end": v(-460.79, 653) * mm});
            skLineSegment(sketch, "E1808", {"start": v(-460.79, 653) * mm, "end": v(-460.81, 652.55) * mm});
            skLineSegment(sketch, "E1809", {"start": v(-460.81, 652.55) * mm, "end": v(-460.85, 652.1) * mm});
            skLineSegment(sketch, "E1810", {"start": v(-460.85, 652.1) * mm, "end": v(-460.9, 651.66) * mm});
            skLineSegment(sketch, "E1811", {"start": v(-460.9, 651.66) * mm, "end": v(-460.96, 651.22) * mm});
            skLineSegment(sketch, "E1812", {"start": v(-460.96, 651.22) * mm, "end": v(-461.03, 650.78) * mm});
            skLineSegment(sketch, "E1813", {"start": v(-461.03, 650.78) * mm, "end": v(-461.11, 650.34) * mm});
            skLineSegment(sketch, "E1814", {"start": v(-461.11, 650.34) * mm, "end": v(-461.2, 649.9) * mm});
            skLineSegment(sketch, "E1815", {"start": v(-461.2, 649.9) * mm, "end": v(-461.3, 649.47) * mm});
            skLineSegment(sketch, "E1816", {"start": v(-461.3, 649.47) * mm, "end": v(-461.42, 649.04) * mm});
            skLineSegment(sketch, "E1817", {"start": v(-461.42, 649.04) * mm, "end": v(-461.55, 648.62) * mm});
            skLineSegment(sketch, "E1818", {"start": v(-461.55, 648.62) * mm, "end": v(-461.68, 648.2) * mm});
            skLineSegment(sketch, "E1819", {"start": v(-461.68, 648.2) * mm, "end": v(-461.83, 647.77) * mm});
            skLineSegment(sketch, "E1820", {"start": v(-461.83, 647.77) * mm, "end": v(-461.98, 647.36) * mm});
            skLineSegment(sketch, "E1821", {"start": v(-461.98, 647.36) * mm, "end": v(-462.15, 646.95) * mm});
            skLineSegment(sketch, "E1822", {"start": v(-462.15, 646.95) * mm, "end": v(-462.33, 646.54) * mm});
            skLineSegment(sketch, "E1823", {"start": v(-462.33, 646.54) * mm, "end": v(-462.51, 646.14) * mm});
            skLineSegment(sketch, "E1824", {"start": v(-462.51, 646.14) * mm, "end": v(-462.7, 645.74) * mm});
            skLineSegment(sketch, "E1825", {"start": v(-462.7, 645.74) * mm, "end": v(-462.92, 645.34) * mm});
            skLineSegment(sketch, "E1826", {"start": v(-462.92, 645.34) * mm, "end": v(-463.13, 644.96) * mm});
            skLineSegment(sketch, "E1827", {"start": v(-463.13, 644.96) * mm, "end": v(-463.36, 644.57) * mm});
            skLineSegment(sketch, "E1828", {"start": v(-463.36, 644.57) * mm, "end": v(-463.6, 644.2) * mm});
            skLineSegment(sketch, "E1829", {"start": v(-463.6, 644.2) * mm, "end": v(-463.84, 643.82) * mm});
            skLineSegment(sketch, "E1830", {"start": v(-463.84, 643.82) * mm, "end": v(-464.1, 643.46) * mm});
            skLineSegment(sketch, "E1831", {"start": v(-464.1, 643.46) * mm, "end": v(-464.36, 643.1) * mm});
            skLineSegment(sketch, "E1832", {"start": v(-464.36, 643.1) * mm, "end": v(-464.63, 642.74) * mm});
            skLineSegment(sketch, "E1833", {"start": v(-464.63, 642.74) * mm, "end": v(-464.91, 642.4) * mm});
            skLineSegment(sketch, "E1834", {"start": v(-464.91, 642.4) * mm, "end": v(-465.2, 642.05) * mm});
            skLineSegment(sketch, "E1835", {"start": v(-465.2, 642.05) * mm, "end": v(-465.5, 641.72) * mm});
            skLineSegment(sketch, "E1836", {"start": v(-465.5, 641.72) * mm, "end": v(-465.82, 641.4) * mm});
            skLineSegment(sketch, "E1837", {"start": v(-465.82, 641.4) * mm, "end": v(-466.07, 641.14) * mm});
            skLineSegment(sketch, "E1838", {"start": v(-466.07, 641.14) * mm, "end": v(-466.34, 640.89) * mm});
            skLineSegment(sketch, "E1839", {"start": v(-466.34, 640.89) * mm, "end": v(-466.6, 640.65) * mm});
            skLineSegment(sketch, "E1840", {"start": v(-466.6, 640.65) * mm, "end": v(-466.88, 640.42) * mm});
            skLineSegment(sketch, "E1841", {"start": v(-466.88, 640.42) * mm, "end": v(-467.16, 640.19) * mm});
            skLineSegment(sketch, "E1842", {"start": v(-467.16, 640.19) * mm, "end": v(-467.44, 639.97) * mm});
            skLineSegment(sketch, "E1843", {"start": v(-467.44, 639.97) * mm, "end": v(-467.73, 639.76) * mm});
            skLineSegment(sketch, "E1844", {"start": v(-467.73, 639.76) * mm, "end": v(-468.03, 639.56) * mm});
            skLineSegment(sketch, "E1845", {"start": v(-468.03, 639.56) * mm, "end": v(-468.33, 639.36) * mm});
            skLineSegment(sketch, "E1846", {"start": v(-468.33, 639.36) * mm, "end": v(-468.63, 639.17) * mm});
            skLineSegment(sketch, "E1847", {"start": v(-468.63, 639.17) * mm, "end": v(-468.94, 639) * mm});
            skLineSegment(sketch, "E1848", {"start": v(-468.94, 639) * mm, "end": v(-469.25, 638.82) * mm});
            skLineSegment(sketch, "E1849", {"start": v(-469.25, 638.82) * mm, "end": v(-469.57, 638.65) * mm});
            skLineSegment(sketch, "E1850", {"start": v(-469.57, 638.65) * mm, "end": v(-469.89, 638.5) * mm});
            skLineSegment(sketch, "E1851", {"start": v(-469.89, 638.5) * mm, "end": v(-470.21, 638.35) * mm});
            skLineSegment(sketch, "E1852", {"start": v(-470.21, 638.35) * mm, "end": v(-470.54, 638.2) * mm});
            skLineSegment(sketch, "E1853", {"start": v(-470.54, 638.2) * mm, "end": v(-470.87, 638.07) * mm});
            skLineSegment(sketch, "E1854", {"start": v(-470.87, 638.07) * mm, "end": v(-471.2, 637.95) * mm});
            skLineSegment(sketch, "E1855", {"start": v(-471.2, 637.95) * mm, "end": v(-471.54, 637.83) * mm});
            skLineSegment(sketch, "E1856", {"start": v(-471.54, 637.83) * mm, "end": v(-471.88, 637.72) * mm});
            skLineSegment(sketch, "E1857", {"start": v(-471.88, 637.72) * mm, "end": v(-472.23, 637.63) * mm});
            skLineSegment(sketch, "E1858", {"start": v(-472.23, 637.63) * mm, "end": v(-472.57, 637.53) * mm});
            skLineSegment(sketch, "E1859", {"start": v(-472.57, 637.53) * mm, "end": v(-472.92, 637.45) * mm});
            skLineSegment(sketch, "E1860", {"start": v(-472.92, 637.45) * mm, "end": v(-473.27, 637.38) * mm});
            skLineSegment(sketch, "E1861", {"start": v(-473.27, 637.38) * mm, "end": v(-473.62, 637.31) * mm});
            skLineSegment(sketch, "E1862", {"start": v(-473.62, 637.31) * mm, "end": v(-473.98, 637.26) * mm});
            skLineSegment(sketch, "E1863", {"start": v(-473.98, 637.26) * mm, "end": v(-474.33, 637.2) * mm});
            skLineSegment(sketch, "E1864", {"start": v(-474.33, 637.2) * mm, "end": v(-474.69, 637.17) * mm});
            skLineSegment(sketch, "E1865", {"start": v(-474.69, 637.17) * mm, "end": v(-475.05, 637.14) * mm});
            skLineSegment(sketch, "E1866", {"start": v(-475.05, 637.14) * mm, "end": v(-475.4, 637.12) * mm});
            skLineSegment(sketch, "E1867", {"start": v(-475.4, 637.12) * mm, "end": v(-475.77, 637.1) * mm});
            skLineSegment(sketch, "E1868", {"start": v(-475.77, 637.1) * mm, "end": v(-476.13, 637.1) * mm});
            skLineSegment(sketch, "E1869", {"start": v(-437.42, 637.1) * mm, "end": v(-437.78, 637.1) * mm});
            skLineSegment(sketch, "E1870", {"start": v(-437.78, 637.1) * mm, "end": v(-438.15, 637.1) * mm});
            skLineSegment(sketch, "E1871", {"start": v(-438.15, 637.1) * mm, "end": v(-438.52, 637.12) * mm});
            skLineSegment(sketch, "E1872", {"start": v(-438.52, 637.12) * mm, "end": v(-438.88, 637.15) * mm});
            skLineSegment(sketch, "E1873", {"start": v(-438.88, 637.15) * mm, "end": v(-439.24, 637.18) * mm});
            skLineSegment(sketch, "E1874", {"start": v(-439.24, 637.18) * mm, "end": v(-439.6, 637.23) * mm});
            skLineSegment(sketch, "E1875", {"start": v(-439.6, 637.23) * mm, "end": v(-439.97, 637.28) * mm});
            skLineSegment(sketch, "E1876", {"start": v(-439.97, 637.28) * mm, "end": v(-440.32, 637.34) * mm});
            skLineSegment(sketch, "E1877", {"start": v(-440.32, 637.34) * mm, "end": v(-440.68, 637.4) * mm});
            skLineSegment(sketch, "E1878", {"start": v(-440.68, 637.4) * mm, "end": v(-441.04, 637.49) * mm});
            skLineSegment(sketch, "E1879", {"start": v(-441.04, 637.49) * mm, "end": v(-441.39, 637.57) * mm});
            skLineSegment(sketch, "E1880", {"start": v(-441.39, 637.57) * mm, "end": v(-441.74, 637.67) * mm});
            skLineSegment(sketch, "E1881", {"start": v(-441.74, 637.67) * mm, "end": v(-442.08, 637.77) * mm});
            skLineSegment(sketch, "E1882", {"start": v(-442.08, 637.77) * mm, "end": v(-442.43, 637.89) * mm});
            skLineSegment(sketch, "E1883", {"start": v(-442.43, 637.89) * mm, "end": v(-442.77, 638) * mm});
            skLineSegment(sketch, "E1884", {"start": v(-442.77, 638) * mm, "end": v(-443.1, 638.14) * mm});
            skLineSegment(sketch, "E1885", {"start": v(-443.1, 638.14) * mm, "end": v(-443.44, 638.28) * mm});
            skLineSegment(sketch, "E1886", {"start": v(-443.44, 638.28) * mm, "end": v(-443.77, 638.42) * mm});
            skLineSegment(sketch, "E1887", {"start": v(-443.77, 638.42) * mm, "end": v(-444.1, 638.58) * mm});
            skLineSegment(sketch, "E1888", {"start": v(-444.1, 638.58) * mm, "end": v(-444.42, 638.74) * mm});
            skLineSegment(sketch, "E1889", {"start": v(-444.42, 638.74) * mm, "end": v(-444.74, 638.91) * mm});
            skLineSegment(sketch, "E1890", {"start": v(-444.74, 638.91) * mm, "end": v(-445.06, 639.09) * mm});
            skLineSegment(sketch, "E1891", {"start": v(-445.06, 639.09) * mm, "end": v(-445.37, 639.28) * mm});
            skLineSegment(sketch, "E1892", {"start": v(-445.37, 639.28) * mm, "end": v(-445.68, 639.47) * mm});
            skLineSegment(sketch, "E1893", {"start": v(-445.68, 639.47) * mm, "end": v(-445.98, 639.67) * mm});
            skLineSegment(sketch, "E1894", {"start": v(-445.98, 639.67) * mm, "end": v(-446.28, 639.88) * mm});
            skLineSegment(sketch, "E1895", {"start": v(-446.28, 639.88) * mm, "end": v(-446.57, 640.1) * mm});
            skLineSegment(sketch, "E1896", {"start": v(-446.57, 640.1) * mm, "end": v(-446.85, 640.33) * mm});
            skLineSegment(sketch, "E1897", {"start": v(-446.85, 640.33) * mm, "end": v(-447.14, 640.56) * mm});
            skLineSegment(sketch, "E1898", {"start": v(-447.14, 640.56) * mm, "end": v(-447.41, 640.8) * mm});
            skLineSegment(sketch, "E1899", {"start": v(-447.41, 640.8) * mm, "end": v(-447.68, 641.05) * mm});
            skLineSegment(sketch, "E1900", {"start": v(-447.68, 641.05) * mm, "end": v(-447.95, 641.3) * mm});
            skLineSegment(sketch, "E1901", {"start": v(-447.95, 641.3) * mm, "end": v(-448.25, 641.63) * mm});
            skLineSegment(sketch, "E1902", {"start": v(-448.25, 641.63) * mm, "end": v(-448.55, 641.97) * mm});
            skLineSegment(sketch, "E1903", {"start": v(-448.55, 641.97) * mm, "end": v(-448.84, 642.32) * mm});
            skLineSegment(sketch, "E1904", {"start": v(-448.84, 642.32) * mm, "end": v(-449.12, 642.67) * mm});
            skLineSegment(sketch, "E1905", {"start": v(-449.12, 642.67) * mm, "end": v(-449.39, 643.03) * mm});
            skLineSegment(sketch, "E1906", {"start": v(-449.39, 643.03) * mm, "end": v(-449.65, 643.4) * mm});
            skLineSegment(sketch, "E1907", {"start": v(-449.65, 643.4) * mm, "end": v(-449.9, 643.77) * mm});
            skLineSegment(sketch, "E1908", {"start": v(-449.9, 643.77) * mm, "end": v(-450.14, 644.14) * mm});
            skLineSegment(sketch, "E1909", {"start": v(-450.14, 644.14) * mm, "end": v(-450.37, 644.53) * mm});
            skLineSegment(sketch, "E1910", {"start": v(-450.37, 644.53) * mm, "end": v(-450.6, 644.91) * mm});
            skLineSegment(sketch, "E1911", {"start": v(-450.6, 644.91) * mm, "end": v(-450.8, 645.3) * mm});
            skLineSegment(sketch, "E1912", {"start": v(-450.8, 645.3) * mm, "end": v(-451, 645.7) * mm});
            skLineSegment(sketch, "E1913", {"start": v(-451, 645.7) * mm, "end": v(-451.2, 646.1) * mm});
            skLineSegment(sketch, "E1914", {"start": v(-451.2, 646.1) * mm, "end": v(-451.38, 646.51) * mm});
            skLineSegment(sketch, "E1915", {"start": v(-451.38, 646.51) * mm, "end": v(-451.55, 646.93) * mm});
            skLineSegment(sketch, "E1916", {"start": v(-451.55, 646.93) * mm, "end": v(-451.72, 647.34) * mm});
            skLineSegment(sketch, "E1917", {"start": v(-451.72, 647.34) * mm, "end": v(-451.87, 647.76) * mm});
            skLineSegment(sketch, "E1918", {"start": v(-451.87, 647.76) * mm, "end": v(-452.01, 648.18) * mm});
            skLineSegment(sketch, "E1919", {"start": v(-452.01, 648.18) * mm, "end": v(-452.14, 648.6) * mm});
            skLineSegment(sketch, "E1920", {"start": v(-452.14, 648.6) * mm, "end": v(-452.26, 649.04) * mm});
            skLineSegment(sketch, "E1921", {"start": v(-452.26, 649.04) * mm, "end": v(-452.37, 649.47) * mm});
            skLineSegment(sketch, "E1922", {"start": v(-452.37, 649.47) * mm, "end": v(-452.47, 649.9) * mm});
            skLineSegment(sketch, "E1923", {"start": v(-452.47, 649.9) * mm, "end": v(-452.56, 650.34) * mm});
            skLineSegment(sketch, "E1924", {"start": v(-452.56, 650.34) * mm, "end": v(-452.64, 650.78) * mm});
            skLineSegment(sketch, "E1925", {"start": v(-452.64, 650.78) * mm, "end": v(-452.7, 651.22) * mm});
            skLineSegment(sketch, "E1926", {"start": v(-452.7, 651.22) * mm, "end": v(-452.76, 651.67) * mm});
            skLineSegment(sketch, "E1927", {"start": v(-452.76, 651.67) * mm, "end": v(-452.81, 652.11) * mm});
            skLineSegment(sketch, "E1928", {"start": v(-452.81, 652.11) * mm, "end": v(-452.84, 652.56) * mm});
            skLineSegment(sketch, "E1929", {"start": v(-452.84, 652.56) * mm, "end": v(-452.87, 653.01) * mm});
            skLineSegment(sketch, "E1930", {"start": v(-452.87, 653.01) * mm, "end": v(-452.88, 653.46) * mm});
            skLineSegment(sketch, "E1931", {"start": v(-452.88, 653.46) * mm, "end": v(-452.88, 653.91) * mm});
            skLineSegment(sketch, "E1932", {"start": v(-452.88, 653.91) * mm, "end": v(-452.87, 654.37) * mm});
            skLineSegment(sketch, "E1933", {"start": v(-452.87, 654.37) * mm, "end": v(-452.88, 654.86) * mm});
            skLineSegment(sketch, "E1934", {"start": v(-452.88, 654.86) * mm, "end": v(-452.89, 655.35) * mm});
            skLineSegment(sketch, "E1935", {"start": v(-452.89, 655.35) * mm, "end": v(-452.88, 655.84) * mm});
            skLineSegment(sketch, "E1936", {"start": v(-452.88, 655.84) * mm, "end": v(-452.85, 656.32) * mm});
            skLineSegment(sketch, "E1937", {"start": v(-452.85, 656.32) * mm, "end": v(-452.82, 656.8) * mm});
            skLineSegment(sketch, "E1938", {"start": v(-452.82, 656.8) * mm, "end": v(-452.77, 657.3) * mm});
            skLineSegment(sketch, "E1939", {"start": v(-452.77, 657.3) * mm, "end": v(-452.7, 657.78) * mm});
            skLineSegment(sketch, "E1940", {"start": v(-452.7, 657.78) * mm, "end": v(-452.64, 658.26) * mm});
            skLineSegment(sketch, "E1941", {"start": v(-452.64, 658.26) * mm, "end": v(-452.55, 658.74) * mm});
            skLineSegment(sketch, "E1942", {"start": v(-452.55, 658.74) * mm, "end": v(-452.46, 659.21) * mm});
            skLineSegment(sketch, "E1943", {"start": v(-452.46, 659.21) * mm, "end": v(-452.35, 659.68) * mm});
            skLineSegment(sketch, "E1944", {"start": v(-452.35, 659.68) * mm, "end": v(-452.23, 660.15) * mm});
            skLineSegment(sketch, "E1945", {"start": v(-452.23, 660.15) * mm, "end": v(-452.1, 660.62) * mm});
            skLineSegment(sketch, "E1946", {"start": v(-452.1, 660.62) * mm, "end": v(-451.96, 661.08) * mm});
            skLineSegment(sketch, "E1947", {"start": v(-451.96, 661.08) * mm, "end": v(-451.8, 661.54) * mm});
            skLineSegment(sketch, "E1948", {"start": v(-451.8, 661.54) * mm, "end": v(-451.64, 662) * mm});
            skLineSegment(sketch, "E1949", {"start": v(-451.64, 662) * mm, "end": v(-451.47, 662.45) * mm});
            skLineSegment(sketch, "E1950", {"start": v(-451.47, 662.45) * mm, "end": v(-451.28, 662.9) * mm});
            skLineSegment(sketch, "E1951", {"start": v(-451.28, 662.9) * mm, "end": v(-451.08, 663.33) * mm});
            skLineSegment(sketch, "E1952", {"start": v(-451.08, 663.33) * mm, "end": v(-450.87, 663.77) * mm});
            skLineSegment(sketch, "E1953", {"start": v(-450.87, 663.77) * mm, "end": v(-450.65, 664.2) * mm});
            skLineSegment(sketch, "E1954", {"start": v(-450.65, 664.2) * mm, "end": v(-450.42, 664.63) * mm});
            skLineSegment(sketch, "E1955", {"start": v(-450.42, 664.63) * mm, "end": v(-450.18, 665.05) * mm});
            skLineSegment(sketch, "E1956", {"start": v(-450.18, 665.05) * mm, "end": v(-449.93, 665.46) * mm});
            skLineSegment(sketch, "E1957", {"start": v(-449.93, 665.46) * mm, "end": v(-449.67, 665.87) * mm});
            skLineSegment(sketch, "E1958", {"start": v(-449.67, 665.87) * mm, "end": v(-449.4, 666.28) * mm});
            skLineSegment(sketch, "E1959", {"start": v(-449.4, 666.28) * mm, "end": v(-449.11, 666.67) * mm});
            skLineSegment(sketch, "E1960", {"start": v(-449.11, 666.67) * mm, "end": v(-448.82, 667.06) * mm});
            skLineSegment(sketch, "E1961", {"start": v(-448.82, 667.06) * mm, "end": v(-448.51, 667.44) * mm});
            skLineSegment(sketch, "E1962", {"start": v(-448.51, 667.44) * mm, "end": v(-448.2, 667.82) * mm});
            skLineSegment(sketch, "E1963", {"start": v(-448.2, 667.82) * mm, "end": v(-447.88, 668.19) * mm});
            skLineSegment(sketch, "E1964", {"start": v(-447.88, 668.19) * mm, "end": v(-447.54, 668.55) * mm});
            skLineSegment(sketch, "E1965", {"start": v(-447.54, 668.55) * mm, "end": v(-447.3, 668.8) * mm});
            skLineSegment(sketch, "E1966", {"start": v(-447.3, 668.8) * mm, "end": v(-447.04, 669.05) * mm});
            skLineSegment(sketch, "E1967", {"start": v(-447.04, 669.05) * mm, "end": v(-446.77, 669.29) * mm});
            skLineSegment(sketch, "E1968", {"start": v(-446.77, 669.29) * mm, "end": v(-446.5, 669.52) * mm});
            skLineSegment(sketch, "E1969", {"start": v(-446.5, 669.52) * mm, "end": v(-446.23, 669.75) * mm});
            skLineSegment(sketch, "E1970", {"start": v(-446.23, 669.75) * mm, "end": v(-445.95, 669.96) * mm});
            skLineSegment(sketch, "E1971", {"start": v(-445.95, 669.96) * mm, "end": v(-445.67, 670.17) * mm});
            skLineSegment(sketch, "E1972", {"start": v(-445.67, 670.17) * mm, "end": v(-445.38, 670.38) * mm});
            skLineSegment(sketch, "E1973", {"start": v(-445.38, 670.38) * mm, "end": v(-445.09, 670.57) * mm});
            skLineSegment(sketch, "E1974", {"start": v(-445.09, 670.57) * mm, "end": v(-444.8, 670.76) * mm});
            skLineSegment(sketch, "E1975", {"start": v(-444.8, 670.76) * mm, "end": v(-444.49, 670.94) * mm});
            skLineSegment(sketch, "E1976", {"start": v(-444.49, 670.94) * mm, "end": v(-444.18, 671.1) * mm});
            skLineSegment(sketch, "E1977", {"start": v(-444.18, 671.1) * mm, "end": v(-443.87, 671.27) * mm});
            skLineSegment(sketch, "E1978", {"start": v(-443.87, 671.27) * mm, "end": v(-443.56, 671.43) * mm});
            skLineSegment(sketch, "E1979", {"start": v(-443.56, 671.43) * mm, "end": v(-443.24, 671.58) * mm});
            skLineSegment(sketch, "E1980", {"start": v(-443.24, 671.58) * mm, "end": v(-442.92, 671.71) * mm});
            skLineSegment(sketch, "E1981", {"start": v(-442.92, 671.71) * mm, "end": v(-442.6, 671.85) * mm});
            skLineSegment(sketch, "E1982", {"start": v(-442.6, 671.85) * mm, "end": v(-442.26, 671.97) * mm});
            skLineSegment(sketch, "E1983", {"start": v(-442.26, 671.97) * mm, "end": v(-441.93, 672.08) * mm});
            skLineSegment(sketch, "E1984", {"start": v(-441.93, 672.08) * mm, "end": v(-441.6, 672.19) * mm});
            skLineSegment(sketch, "E1985", {"start": v(-441.6, 672.19) * mm, "end": v(-441.26, 672.29) * mm});
            skLineSegment(sketch, "E1986", {"start": v(-441.26, 672.29) * mm, "end": v(-440.92, 672.37) * mm});
            skLineSegment(sketch, "E1987", {"start": v(-440.92, 672.37) * mm, "end": v(-440.57, 672.45) * mm});
            skLineSegment(sketch, "E1988", {"start": v(-440.57, 672.45) * mm, "end": v(-440.23, 672.52) * mm});
            skLineSegment(sketch, "E1989", {"start": v(-440.23, 672.52) * mm, "end": v(-439.88, 672.59) * mm});
            skLineSegment(sketch, "E1990", {"start": v(-439.88, 672.59) * mm, "end": v(-439.53, 672.64) * mm});
            skLineSegment(sketch, "E1991", {"start": v(-439.53, 672.64) * mm, "end": v(-439.18, 672.69) * mm});
            skLineSegment(sketch, "E1992", {"start": v(-439.18, 672.69) * mm, "end": v(-438.83, 672.72) * mm});
            skLineSegment(sketch, "E1993", {"start": v(-438.83, 672.72) * mm, "end": v(-438.48, 672.75) * mm});
            skLineSegment(sketch, "E1994", {"start": v(-438.48, 672.75) * mm, "end": v(-438.12, 672.76) * mm});
            skLineSegment(sketch, "E1995", {"start": v(-438.12, 672.76) * mm, "end": v(-437.77, 672.77) * mm});
            skLineSegment(sketch, "E1996", {"start": v(-437.77, 672.77) * mm, "end": v(-437.41, 672.77) * mm});
            skLineSegment(sketch, "E1997", {"start": v(-437.41, 672.77) * mm, "end": v(-437.05, 672.77) * mm});
            skLineSegment(sketch, "E1998", {"start": v(-437.05, 672.77) * mm, "end": v(-436.69, 672.75) * mm});
            skLineSegment(sketch, "E1999", {"start": v(-436.69, 672.75) * mm, "end": v(-436.33, 672.73) * mm});
            skLineSegment(sketch, "E2000", {"start": v(-436.33, 672.73) * mm, "end": v(-435.97, 672.7) * mm});
            skLineSegment(sketch, "E2001", {"start": v(-435.97, 672.7) * mm, "end": v(-435.6, 672.66) * mm});
            skLineSegment(sketch, "E2002", {"start": v(-435.6, 672.66) * mm, "end": v(-435.25, 672.61) * mm});
            skLineSegment(sketch, "E2003", {"start": v(-435.25, 672.61) * mm, "end": v(-434.9, 672.55) * mm});
            skLineSegment(sketch, "E2004", {"start": v(-434.9, 672.55) * mm, "end": v(-434.55, 672.48) * mm});
            skLineSegment(sketch, "E2005", {"start": v(-434.55, 672.48) * mm, "end": v(-434.2, 672.4) * mm});
            skLineSegment(sketch, "E2006", {"start": v(-434.2, 672.4) * mm, "end": v(-433.85, 672.32) * mm});
            skLineSegment(sketch, "E2007", {"start": v(-433.85, 672.32) * mm, "end": v(-433.5, 672.23) * mm});
            skLineSegment(sketch, "E2008", {"start": v(-433.5, 672.23) * mm, "end": v(-433.16, 672.12) * mm});
            skLineSegment(sketch, "E2009", {"start": v(-433.16, 672.12) * mm, "end": v(-432.83, 672.01) * mm});
            skLineSegment(sketch, "E2010", {"start": v(-432.83, 672.01) * mm, "end": v(-432.49, 671.9) * mm});
            skLineSegment(sketch, "E2011", {"start": v(-432.49, 671.9) * mm, "end": v(-432.16, 671.76) * mm});
            skLineSegment(sketch, "E2012", {"start": v(-432.16, 671.76) * mm, "end": v(-431.83, 671.63) * mm});
            skLineSegment(sketch, "E2013", {"start": v(-431.83, 671.63) * mm, "end": v(-431.5, 671.48) * mm});
            skLineSegment(sketch, "E2014", {"start": v(-431.5, 671.48) * mm, "end": v(-431.18, 671.33) * mm});
            skLineSegment(sketch, "E2015", {"start": v(-431.18, 671.33) * mm, "end": v(-430.86, 671.17) * mm});
            skLineSegment(sketch, "E2016", {"start": v(-430.86, 671.17) * mm, "end": v(-430.55, 671) * mm});
            skLineSegment(sketch, "E2017", {"start": v(-430.55, 671) * mm, "end": v(-430.24, 670.82) * mm});
            skLineSegment(sketch, "E2018", {"start": v(-430.24, 670.82) * mm, "end": v(-429.93, 670.63) * mm});
            skLineSegment(sketch, "E2019", {"start": v(-429.93, 670.63) * mm, "end": v(-429.63, 670.44) * mm});
            skLineSegment(sketch, "E2020", {"start": v(-429.63, 670.44) * mm, "end": v(-429.34, 670.24) * mm});
            skLineSegment(sketch, "E2021", {"start": v(-429.34, 670.24) * mm, "end": v(-429.05, 670.03) * mm});
            skLineSegment(sketch, "E2022", {"start": v(-429.05, 670.03) * mm, "end": v(-428.76, 669.81) * mm});
            skLineSegment(sketch, "E2023", {"start": v(-428.76, 669.81) * mm, "end": v(-428.48, 669.59) * mm});
            skLineSegment(sketch, "E2024", {"start": v(-428.48, 669.59) * mm, "end": v(-428.2, 669.35) * mm});
            skLineSegment(sketch, "E2025", {"start": v(-428.2, 669.35) * mm, "end": v(-427.94, 669.11) * mm});
            skLineSegment(sketch, "E2026", {"start": v(-427.94, 669.11) * mm, "end": v(-427.67, 668.87) * mm});
            skLineSegment(sketch, "E2027", {"start": v(-427.67, 668.87) * mm, "end": v(-427.42, 668.61) * mm});
            skLineSegment(sketch, "E2028", {"start": v(-427.42, 668.61) * mm, "end": v(-427.16, 668.35) * mm});
            skLineSegment(sketch, "E2029", {"start": v(-427.16, 668.35) * mm, "end": v(-426.84, 668) * mm});
            skLineSegment(sketch, "E2030", {"start": v(-426.84, 668) * mm, "end": v(-426.53, 667.63) * mm});
            skLineSegment(sketch, "E2031", {"start": v(-426.53, 667.63) * mm, "end": v(-426.22, 667.25) * mm});
            skLineSegment(sketch, "E2032", {"start": v(-426.22, 667.25) * mm, "end": v(-425.93, 666.87) * mm});
            skLineSegment(sketch, "E2033", {"start": v(-425.93, 666.87) * mm, "end": v(-425.64, 666.49) * mm});
            skLineSegment(sketch, "E2034", {"start": v(-425.64, 666.49) * mm, "end": v(-425.37, 666.1) * mm});
            skLineSegment(sketch, "E2035", {"start": v(-425.37, 666.1) * mm, "end": v(-425.1, 665.7) * mm});
            skLineSegment(sketch, "E2036", {"start": v(-425.1, 665.7) * mm, "end": v(-424.85, 665.3) * mm});
            skLineSegment(sketch, "E2037", {"start": v(-424.85, 665.3) * mm, "end": v(-424.6, 664.88) * mm});
            skLineSegment(sketch, "E2038", {"start": v(-424.6, 664.88) * mm, "end": v(-424.38, 664.46) * mm});
            skLineSegment(sketch, "E2039", {"start": v(-424.38, 664.46) * mm, "end": v(-424.15, 664.04) * mm});
            skLineSegment(sketch, "E2040", {"start": v(-424.15, 664.04) * mm, "end": v(-423.94, 663.62) * mm});
            skLineSegment(sketch, "E2041", {"start": v(-423.94, 663.62) * mm, "end": v(-423.74, 663.18) * mm});
            skLineSegment(sketch, "E2042", {"start": v(-423.74, 663.18) * mm, "end": v(-423.55, 662.75) * mm});
            skLineSegment(sketch, "E2043", {"start": v(-423.55, 662.75) * mm, "end": v(-423.37, 662.3) * mm});
            skLineSegment(sketch, "E2044", {"start": v(-423.37, 662.3) * mm, "end": v(-423.2, 661.86) * mm});
            skLineSegment(sketch, "E2045", {"start": v(-423.2, 661.86) * mm, "end": v(-423.05, 661.41) * mm});
            skLineSegment(sketch, "E2046", {"start": v(-423.05, 661.41) * mm, "end": v(-422.9, 660.96) * mm});
            skLineSegment(sketch, "E2047", {"start": v(-422.9, 660.96) * mm, "end": v(-422.76, 660.5) * mm});
            skLineSegment(sketch, "E2048", {"start": v(-422.76, 660.5) * mm, "end": v(-422.64, 660.04) * mm});
            skLineSegment(sketch, "E2049", {"start": v(-422.64, 660.04) * mm, "end": v(-422.53, 659.58) * mm});
            skLineSegment(sketch, "E2050", {"start": v(-422.53, 659.58) * mm, "end": v(-422.43, 659.11) * mm});
            skLineSegment(sketch, "E2051", {"start": v(-422.43, 659.11) * mm, "end": v(-422.34, 658.65) * mm});
            skLineSegment(sketch, "E2052", {"start": v(-422.34, 658.65) * mm, "end": v(-422.26, 658.17) * mm});
            skLineSegment(sketch, "E2053", {"start": v(-422.26, 658.17) * mm, "end": v(-422.2, 657.7) * mm});
            skLineSegment(sketch, "E2054", {"start": v(-422.2, 657.7) * mm, "end": v(-422.14, 657.23) * mm});
            skLineSegment(sketch, "E2055", {"start": v(-422.14, 657.23) * mm, "end": v(-422.1, 656.75) * mm});
            skLineSegment(sketch, "E2056", {"start": v(-422.1, 656.75) * mm, "end": v(-422.06, 656.27) * mm});
            skLineSegment(sketch, "E2057", {"start": v(-422.06, 656.27) * mm, "end": v(-422.04, 655.79) * mm});
            skLineSegment(sketch, "E2058", {"start": v(-422.04, 655.79) * mm, "end": v(-422.04, 655.3) * mm});
            skLineSegment(sketch, "E2059", {"start": v(-422.04, 655.3) * mm, "end": v(-422.04, 654.83) * mm});
            skLineSegment(sketch, "E2060", {"start": v(-422.04, 654.83) * mm, "end": v(-422.06, 654.34) * mm});
            skLineSegment(sketch, "E2061", {"start": v(-422.06, 654.34) * mm, "end": v(-422.05, 653.9) * mm});
            skLineSegment(sketch, "E2062", {"start": v(-422.05, 653.9) * mm, "end": v(-422.06, 653.44) * mm});
            skLineSegment(sketch, "E2063", {"start": v(-422.06, 653.44) * mm, "end": v(-422.07, 653) * mm});
            skLineSegment(sketch, "E2064", {"start": v(-422.07, 653) * mm, "end": v(-422.1, 652.55) * mm});
            skLineSegment(sketch, "E2065", {"start": v(-422.1, 652.55) * mm, "end": v(-422.14, 652.1) * mm});
            skLineSegment(sketch, "E2066", {"start": v(-422.14, 652.1) * mm, "end": v(-422.19, 651.66) * mm});
            skLineSegment(sketch, "E2067", {"start": v(-422.19, 651.66) * mm, "end": v(-422.25, 651.22) * mm});
            skLineSegment(sketch, "E2068", {"start": v(-422.25, 651.22) * mm, "end": v(-422.32, 650.78) * mm});
            skLineSegment(sketch, "E2069", {"start": v(-422.32, 650.78) * mm, "end": v(-422.4, 650.34) * mm});
            skLineSegment(sketch, "E2070", {"start": v(-422.4, 650.34) * mm, "end": v(-422.5, 649.9) * mm});
            skLineSegment(sketch, "E2071", {"start": v(-422.5, 649.9) * mm, "end": v(-422.6, 649.47) * mm});
            skLineSegment(sketch, "E2072", {"start": v(-422.6, 649.47) * mm, "end": v(-422.7, 649.04) * mm});
            skLineSegment(sketch, "E2073", {"start": v(-422.7, 649.04) * mm, "end": v(-422.83, 648.62) * mm});
            skLineSegment(sketch, "E2074", {"start": v(-422.83, 648.62) * mm, "end": v(-422.97, 648.2) * mm});
            skLineSegment(sketch, "E2075", {"start": v(-422.97, 648.2) * mm, "end": v(-423.11, 647.77) * mm});
            skLineSegment(sketch, "E2076", {"start": v(-423.11, 647.77) * mm, "end": v(-423.27, 647.36) * mm});
            skLineSegment(sketch, "E2077", {"start": v(-423.27, 647.36) * mm, "end": v(-423.44, 646.95) * mm});
            skLineSegment(sketch, "E2078", {"start": v(-423.44, 646.95) * mm, "end": v(-423.61, 646.54) * mm});
            skLineSegment(sketch, "E2079", {"start": v(-423.61, 646.54) * mm, "end": v(-423.8, 646.14) * mm});
            skLineSegment(sketch, "E2080", {"start": v(-423.8, 646.14) * mm, "end": v(-424, 645.74) * mm});
            skLineSegment(sketch, "E2081", {"start": v(-424, 645.74) * mm, "end": v(-424.2, 645.34) * mm});
            skLineSegment(sketch, "E2082", {"start": v(-424.2, 645.34) * mm, "end": v(-424.42, 644.96) * mm});
            skLineSegment(sketch, "E2083", {"start": v(-424.42, 644.96) * mm, "end": v(-424.64, 644.57) * mm});
            skLineSegment(sketch, "E2084", {"start": v(-424.64, 644.57) * mm, "end": v(-424.88, 644.2) * mm});
            skLineSegment(sketch, "E2085", {"start": v(-424.88, 644.2) * mm, "end": v(-425.12, 643.82) * mm});
            skLineSegment(sketch, "E2086", {"start": v(-425.12, 643.82) * mm, "end": v(-425.38, 643.46) * mm});
            skLineSegment(sketch, "E2087", {"start": v(-425.38, 643.46) * mm, "end": v(-425.64, 643.1) * mm});
            skLineSegment(sketch, "E2088", {"start": v(-425.64, 643.1) * mm, "end": v(-425.92, 642.74) * mm});
            skLineSegment(sketch, "E2089", {"start": v(-425.92, 642.74) * mm, "end": v(-426.2, 642.4) * mm});
            skLineSegment(sketch, "E2090", {"start": v(-426.2, 642.4) * mm, "end": v(-426.5, 642.05) * mm});
            skLineSegment(sketch, "E2091", {"start": v(-426.5, 642.05) * mm, "end": v(-426.8, 641.72) * mm});
            skLineSegment(sketch, "E2092", {"start": v(-426.8, 641.72) * mm, "end": v(-427.1, 641.4) * mm});
            skLineSegment(sketch, "E2093", {"start": v(-427.1, 641.4) * mm, "end": v(-427.36, 641.14) * mm});
            skLineSegment(sketch, "E2094", {"start": v(-427.36, 641.14) * mm, "end": v(-427.62, 640.89) * mm});
            skLineSegment(sketch, "E2095", {"start": v(-427.62, 640.89) * mm, "end": v(-427.9, 640.65) * mm});
            skLineSegment(sketch, "E2096", {"start": v(-427.9, 640.65) * mm, "end": v(-428.16, 640.42) * mm});
            skLineSegment(sketch, "E2097", {"start": v(-428.16, 640.42) * mm, "end": v(-428.44, 640.19) * mm});
            skLineSegment(sketch, "E2098", {"start": v(-428.44, 640.19) * mm, "end": v(-428.73, 639.97) * mm});
            skLineSegment(sketch, "E2099", {"start": v(-428.73, 639.97) * mm, "end": v(-429.02, 639.76) * mm});
            skLineSegment(sketch, "E2100", {"start": v(-429.02, 639.76) * mm, "end": v(-429.31, 639.56) * mm});
            skLineSegment(sketch, "E2101", {"start": v(-429.31, 639.56) * mm, "end": v(-429.61, 639.36) * mm});
            skLineSegment(sketch, "E2102", {"start": v(-429.61, 639.36) * mm, "end": v(-429.92, 639.17) * mm});
            skLineSegment(sketch, "E2103", {"start": v(-429.92, 639.17) * mm, "end": v(-430.23, 639) * mm});
            skLineSegment(sketch, "E2104", {"start": v(-430.23, 639) * mm, "end": v(-430.54, 638.82) * mm});
            skLineSegment(sketch, "E2105", {"start": v(-430.54, 638.82) * mm, "end": v(-430.85, 638.65) * mm});
            skLineSegment(sketch, "E2106", {"start": v(-430.85, 638.65) * mm, "end": v(-431.17, 638.5) * mm});
            skLineSegment(sketch, "E2107", {"start": v(-431.17, 638.5) * mm, "end": v(-431.5, 638.35) * mm});
            skLineSegment(sketch, "E2108", {"start": v(-431.5, 638.35) * mm, "end": v(-431.83, 638.2) * mm});
            skLineSegment(sketch, "E2109", {"start": v(-431.83, 638.2) * mm, "end": v(-432.16, 638.07) * mm});
            skLineSegment(sketch, "E2110", {"start": v(-432.16, 638.07) * mm, "end": v(-432.5, 637.95) * mm});
            skLineSegment(sketch, "E2111", {"start": v(-432.5, 637.95) * mm, "end": v(-432.83, 637.83) * mm});
            skLineSegment(sketch, "E2112", {"start": v(-432.83, 637.83) * mm, "end": v(-433.17, 637.72) * mm});
            skLineSegment(sketch, "E2113", {"start": v(-433.17, 637.72) * mm, "end": v(-433.51, 637.63) * mm});
            skLineSegment(sketch, "E2114", {"start": v(-433.51, 637.63) * mm, "end": v(-433.86, 637.53) * mm});
            skLineSegment(sketch, "E2115", {"start": v(-433.86, 637.53) * mm, "end": v(-434.2, 637.45) * mm});
            skLineSegment(sketch, "E2116", {"start": v(-434.2, 637.45) * mm, "end": v(-434.56, 637.38) * mm});
            skLineSegment(sketch, "E2117", {"start": v(-434.56, 637.38) * mm, "end": v(-434.9, 637.31) * mm});
            skLineSegment(sketch, "E2118", {"start": v(-434.9, 637.31) * mm, "end": v(-435.26, 637.26) * mm});
            skLineSegment(sketch, "E2119", {"start": v(-435.26, 637.26) * mm, "end": v(-435.62, 637.2) * mm});
            skLineSegment(sketch, "E2120", {"start": v(-435.62, 637.2) * mm, "end": v(-435.98, 637.17) * mm});
            skLineSegment(sketch, "E2121", {"start": v(-435.98, 637.17) * mm, "end": v(-436.33, 637.14) * mm});
            skLineSegment(sketch, "E2122", {"start": v(-436.33, 637.14) * mm, "end": v(-436.7, 637.12) * mm});
            skLineSegment(sketch, "E2123", {"start": v(-436.7, 637.12) * mm, "end": v(-437.06, 637.1) * mm});
            skLineSegment(sketch, "E2124", {"start": v(-437.06, 637.1) * mm, "end": v(-437.42, 637.1) * mm});
            skLineSegment(sketch, "E2125", {"start": v(-414.16, 637.57) * mm, "end": v(-414.16, 672.57) * mm});
            skLineSegment(sketch, "E2126", {"start": v(-414.16, 672.57) * mm, "end": v(-392.4, 672.57) * mm});
            skLineSegment(sketch, "E2127", {"start": v(-414.16, 655.85) * mm, "end": v(-393.98, 655.85) * mm});
            skLineSegment(sketch, "E2128", {"start": v(71, 662.71) * mm, "end": v(70.86, 663.1) * mm});
            skLineSegment(sketch, "E2129", {"start": v(70.86, 663.1) * mm, "end": v(70.72, 663.49) * mm});
            skLineSegment(sketch, "E2130", {"start": v(70.72, 663.49) * mm, "end": v(70.56, 663.87) * mm});
            skLineSegment(sketch, "E2131", {"start": v(70.56, 663.87) * mm, "end": v(70.4, 664.25) * mm});
            skLineSegment(sketch, "E2132", {"start": v(70.4, 664.25) * mm, "end": v(70.21, 664.62) * mm});
            skLineSegment(sketch, "E2133", {"start": v(70.21, 664.62) * mm, "end": v(70.02, 664.99) * mm});
            skLineSegment(sketch, "E2134", {"start": v(70.02, 664.99) * mm, "end": v(69.82, 665.34) * mm});
            skLineSegment(sketch, "E2135", {"start": v(69.82, 665.34) * mm, "end": v(69.6, 665.7) * mm});
            skLineSegment(sketch, "E2136", {"start": v(69.6, 665.7) * mm, "end": v(69.38, 666.04) * mm});
            skLineSegment(sketch, "E2137", {"start": v(69.38, 666.04) * mm, "end": v(69.15, 666.38) * mm});
            skLineSegment(sketch, "E2138", {"start": v(69.15, 666.38) * mm, "end": v(68.9, 666.71) * mm});
            skLineSegment(sketch, "E2139", {"start": v(68.9, 666.71) * mm, "end": v(68.64, 667.03) * mm});
            skLineSegment(sketch, "E2140", {"start": v(68.64, 667.03) * mm, "end": v(68.38, 667.35) * mm});
            skLineSegment(sketch, "E2141", {"start": v(68.38, 667.35) * mm, "end": v(68.1, 667.65) * mm});
            skLineSegment(sketch, "E2142", {"start": v(68.1, 667.65) * mm, "end": v(67.81, 667.95) * mm});
            skLineSegment(sketch, "E2143", {"start": v(67.81, 667.95) * mm, "end": v(67.52, 668.24) * mm});
            skLineSegment(sketch, "E2144", {"start": v(67.52, 668.24) * mm, "end": v(67.27, 668.47) * mm});
            skLineSegment(sketch, "E2145", {"start": v(67.27, 668.47) * mm, "end": v(67.02, 668.7) * mm});
            skLineSegment(sketch, "E2146", {"start": v(67.02, 668.7) * mm, "end": v(66.76, 668.9) * mm});
            skLineSegment(sketch, "E2147", {"start": v(66.76, 668.9) * mm, "end": v(66.5, 669.12) * mm});
            skLineSegment(sketch, "E2148", {"start": v(66.5, 669.12) * mm, "end": v(66.23, 669.32) * mm});
            skLineSegment(sketch, "E2149", {"start": v(66.23, 669.32) * mm, "end": v(65.96, 669.51) * mm});
            skLineSegment(sketch, "E2150", {"start": v(65.96, 669.51) * mm, "end": v(65.68, 669.7) * mm});
            skLineSegment(sketch, "E2151", {"start": v(65.68, 669.7) * mm, "end": v(65.4, 669.88) * mm});
            skLineSegment(sketch, "E2152", {"start": v(65.4, 669.88) * mm, "end": v(65.12, 670.05) * mm});
            skLineSegment(sketch, "E2153", {"start": v(65.12, 670.05) * mm, "end": v(64.83, 670.22) * mm});
            skLineSegment(sketch, "E2154", {"start": v(64.83, 670.22) * mm, "end": v(64.54, 670.37) * mm});
            skLineSegment(sketch, "E2155", {"start": v(64.54, 670.37) * mm, "end": v(64.24, 670.52) * mm});
            skLineSegment(sketch, "E2156", {"start": v(64.24, 670.52) * mm, "end": v(63.94, 670.67) * mm});
            skLineSegment(sketch, "E2157", {"start": v(63.94, 670.67) * mm, "end": v(63.64, 670.8) * mm});
            skLineSegment(sketch, "E2158", {"start": v(63.64, 670.8) * mm, "end": v(63.33, 670.93) * mm});
            skLineSegment(sketch, "E2159", {"start": v(63.33, 670.93) * mm, "end": v(63.02, 671.05) * mm});
            skLineSegment(sketch, "E2160", {"start": v(63.02, 671.05) * mm, "end": v(62.7, 671.16) * mm});
            skLineSegment(sketch, "E2161", {"start": v(62.7, 671.16) * mm, "end": v(62.4, 671.26) * mm});
            skLineSegment(sketch, "E2162", {"start": v(62.4, 671.26) * mm, "end": v(62.07, 671.35) * mm});
            skLineSegment(sketch, "E2163", {"start": v(62.07, 671.35) * mm, "end": v(61.75, 671.44) * mm});
            skLineSegment(sketch, "E2164", {"start": v(61.75, 671.44) * mm, "end": v(61.43, 671.52) * mm});
            skLineSegment(sketch, "E2165", {"start": v(61.43, 671.52) * mm, "end": v(61.1, 671.59) * mm});
            skLineSegment(sketch, "E2166", {"start": v(61.1, 671.59) * mm, "end": v(60.78, 671.65) * mm});
            skLineSegment(sketch, "E2167", {"start": v(60.78, 671.65) * mm, "end": v(60.45, 671.7) * mm});
            skLineSegment(sketch, "E2168", {"start": v(60.45, 671.7) * mm, "end": v(60.12, 671.75) * mm});
            skLineSegment(sketch, "E2169", {"start": v(60.12, 671.75) * mm, "end": v(59.79, 671.79) * mm});
            skLineSegment(sketch, "E2170", {"start": v(59.79, 671.79) * mm, "end": v(59.45, 671.82) * mm});
            skLineSegment(sketch, "E2171", {"start": v(59.45, 671.82) * mm, "end": v(59.12, 671.84) * mm});
            skLineSegment(sketch, "E2172", {"start": v(59.12, 671.84) * mm, "end": v(58.79, 671.85) * mm});
            skLineSegment(sketch, "E2173", {"start": v(58.79, 671.85) * mm, "end": v(58.45, 671.85) * mm});
            skLineSegment(sketch, "E2174", {"start": v(58.45, 671.85) * mm, "end": v(58.11, 671.84) * mm});
            skLineSegment(sketch, "E2175", {"start": v(58.11, 671.84) * mm, "end": v(57.78, 671.83) * mm});
            skLineSegment(sketch, "E2176", {"start": v(57.78, 671.83) * mm, "end": v(57.47, 671.84) * mm});
            skLineSegment(sketch, "E2177", {"start": v(57.47, 671.84) * mm, "end": v(57.16, 671.84) * mm});
            skLineSegment(sketch, "E2178", {"start": v(57.16, 671.84) * mm, "end": v(56.85, 671.83) * mm});
            skLineSegment(sketch, "E2179", {"start": v(56.85, 671.83) * mm, "end": v(56.54, 671.82) * mm});
            skLineSegment(sketch, "E2180", {"start": v(56.54, 671.82) * mm, "end": v(56.23, 671.8) * mm});
            skLineSegment(sketch, "E2181", {"start": v(56.23, 671.8) * mm, "end": v(55.93, 671.76) * mm});
            skLineSegment(sketch, "E2182", {"start": v(55.93, 671.76) * mm, "end": v(55.63, 671.73) * mm});
            skLineSegment(sketch, "E2183", {"start": v(55.63, 671.73) * mm, "end": v(55.32, 671.68) * mm});
            skLineSegment(sketch, "E2184", {"start": v(55.32, 671.68) * mm, "end": v(55.02, 671.63) * mm});
            skLineSegment(sketch, "E2185", {"start": v(55.02, 671.63) * mm, "end": v(54.72, 671.56) * mm});
            skLineSegment(sketch, "E2186", {"start": v(54.72, 671.56) * mm, "end": v(54.42, 671.5) * mm});
            skLineSegment(sketch, "E2187", {"start": v(54.42, 671.5) * mm, "end": v(54.13, 671.42) * mm});
            skLineSegment(sketch, "E2188", {"start": v(54.13, 671.42) * mm, "end": v(53.84, 671.33) * mm});
            skLineSegment(sketch, "E2189", {"start": v(53.84, 671.33) * mm, "end": v(53.54, 671.24) * mm});
            skLineSegment(sketch, "E2190", {"start": v(53.54, 671.24) * mm, "end": v(53.26, 671.14) * mm});
            skLineSegment(sketch, "E2191", {"start": v(53.26, 671.14) * mm, "end": v(52.97, 671.04) * mm});
            skLineSegment(sketch, "E2192", {"start": v(52.97, 671.04) * mm, "end": v(52.69, 670.92) * mm});
            skLineSegment(sketch, "E2193", {"start": v(52.69, 670.92) * mm, "end": v(52.4, 670.8) * mm});
            skLineSegment(sketch, "E2194", {"start": v(52.4, 670.8) * mm, "end": v(52.13, 670.68) * mm});
            skLineSegment(sketch, "E2195", {"start": v(52.13, 670.68) * mm, "end": v(51.86, 670.54) * mm});
            skLineSegment(sketch, "E2196", {"start": v(51.86, 670.54) * mm, "end": v(51.59, 670.4) * mm});
            skLineSegment(sketch, "E2197", {"start": v(51.59, 670.4) * mm, "end": v(51.32, 670.25) * mm});
            skLineSegment(sketch, "E2198", {"start": v(51.32, 670.25) * mm, "end": v(51.06, 670.1) * mm});
            skLineSegment(sketch, "E2199", {"start": v(51.06, 670.1) * mm, "end": v(50.8, 669.93) * mm});
            skLineSegment(sketch, "E2200", {"start": v(50.8, 669.93) * mm, "end": v(50.54, 669.76) * mm});
            skLineSegment(sketch, "E2201", {"start": v(50.54, 669.76) * mm, "end": v(50.3, 669.59) * mm});
            skLineSegment(sketch, "E2202", {"start": v(50.3, 669.59) * mm, "end": v(50.04, 669.4) * mm});
            skLineSegment(sketch, "E2203", {"start": v(50.04, 669.4) * mm, "end": v(49.8, 669.22) * mm});
            skLineSegment(sketch, "E2204", {"start": v(49.8, 669.22) * mm, "end": v(49.56, 669.02) * mm});
            skLineSegment(sketch, "E2205", {"start": v(49.56, 669.02) * mm, "end": v(49.33, 668.82) * mm});
            skLineSegment(sketch, "E2206", {"start": v(49.33, 668.82) * mm, "end": v(49.1, 668.6) * mm});
            skLineSegment(sketch, "E2207", {"start": v(49.1, 668.6) * mm, "end": v(48.88, 668.4) * mm});
            skLineSegment(sketch, "E2208", {"start": v(48.88, 668.4) * mm, "end": v(48.58, 668.1) * mm});
            skLineSegment(sketch, "E2209", {"start": v(48.58, 668.1) * mm, "end": v(48.3, 667.78) * mm});
            skLineSegment(sketch, "E2210", {"start": v(48.3, 667.78) * mm, "end": v(48.02, 667.46) * mm});
            skLineSegment(sketch, "E2211", {"start": v(48.02, 667.46) * mm, "end": v(47.77, 667.13) * mm});
            skLineSegment(sketch, "E2212", {"start": v(47.77, 667.13) * mm, "end": v(47.54, 666.8) * mm});
            skLineSegment(sketch, "E2213", {"start": v(47.54, 666.8) * mm, "end": v(47.32, 666.44) * mm});
            skLineSegment(sketch, "E2214", {"start": v(47.32, 666.44) * mm, "end": v(47.13, 666.09) * mm});
            skLineSegment(sketch, "E2215", {"start": v(47.13, 666.09) * mm, "end": v(46.95, 665.72) * mm});
            skLineSegment(sketch, "E2216", {"start": v(46.95, 665.72) * mm, "end": v(46.78, 665.35) * mm});
            skLineSegment(sketch, "E2217", {"start": v(46.78, 665.35) * mm, "end": v(46.64, 664.97) * mm});
            skLineSegment(sketch, "E2218", {"start": v(46.64, 664.97) * mm, "end": v(46.51, 664.6) * mm});
            skLineSegment(sketch, "E2219", {"start": v(46.51, 664.6) * mm, "end": v(46.4, 664.2) * mm});
            skLineSegment(sketch, "E2220", {"start": v(46.4, 664.2) * mm, "end": v(46.3, 663.81) * mm});
            skLineSegment(sketch, "E2221", {"start": v(46.3, 663.81) * mm, "end": v(46.24, 663.42) * mm});
            skLineSegment(sketch, "E2222", {"start": v(46.24, 663.42) * mm, "end": v(46.18, 663.02) * mm});
            skLineSegment(sketch, "E2223", {"start": v(46.18, 663.02) * mm, "end": v(46.14, 662.62) * mm});
            skLineSegment(sketch, "E2224", {"start": v(46.14, 662.62) * mm, "end": v(46.12, 662.22) * mm});
            skLineSegment(sketch, "E2225", {"start": v(46.12, 662.22) * mm, "end": v(46.12, 661.82) * mm});
            skLineSegment(sketch, "E2226", {"start": v(46.12, 661.82) * mm, "end": v(46.14, 661.42) * mm});
            skLineSegment(sketch, "E2227", {"start": v(46.14, 661.42) * mm, "end": v(46.17, 661.02) * mm});
            skLineSegment(sketch, "E2228", {"start": v(46.17, 661.02) * mm, "end": v(46.22, 660.62) * mm});
            skLineSegment(sketch, "E2229", {"start": v(46.22, 660.62) * mm, "end": v(46.3, 660.23) * mm});
            skLineSegment(sketch, "E2230", {"start": v(46.3, 660.23) * mm, "end": v(46.38, 659.83) * mm});
            skLineSegment(sketch, "E2231", {"start": v(46.38, 659.83) * mm, "end": v(46.5, 659.44) * mm});
            skLineSegment(sketch, "E2232", {"start": v(46.5, 659.44) * mm, "end": v(46.62, 659.05) * mm});
            skLineSegment(sketch, "E2233", {"start": v(46.62, 659.05) * mm, "end": v(46.76, 658.67) * mm});
            skLineSegment(sketch, "E2234", {"start": v(46.76, 658.67) * mm, "end": v(46.92, 658.3) * mm});
            skLineSegment(sketch, "E2235", {"start": v(46.92, 658.3) * mm, "end": v(47.1, 657.93) * mm});
            skLineSegment(sketch, "E2236", {"start": v(47.1, 657.93) * mm, "end": v(47.3, 657.56) * mm});
            skLineSegment(sketch, "E2237", {"start": v(47.3, 657.56) * mm, "end": v(47.53, 657.2) * mm});
            skLineSegment(sketch, "E2238", {"start": v(47.53, 657.2) * mm, "end": v(47.76, 656.86) * mm});
            skLineSegment(sketch, "E2239", {"start": v(47.76, 656.86) * mm, "end": v(48.02, 656.52) * mm});
            skLineSegment(sketch, "E2240", {"start": v(48.02, 656.52) * mm, "end": v(48.28, 656.25) * mm});
            skLineSegment(sketch, "E2241", {"start": v(48.28, 656.25) * mm, "end": v(48.54, 656) * mm});
            skLineSegment(sketch, "E2242", {"start": v(48.54, 656) * mm, "end": v(48.81, 655.75) * mm});
            skLineSegment(sketch, "E2243", {"start": v(48.81, 655.75) * mm, "end": v(49.09, 655.51) * mm});
            skLineSegment(sketch, "E2244", {"start": v(49.09, 655.51) * mm, "end": v(49.37, 655.28) * mm});
            skLineSegment(sketch, "E2245", {"start": v(49.37, 655.28) * mm, "end": v(49.66, 655.06) * mm});
            skLineSegment(sketch, "E2246", {"start": v(49.66, 655.06) * mm, "end": v(49.96, 654.84) * mm});
            skLineSegment(sketch, "E2247", {"start": v(49.96, 654.84) * mm, "end": v(50.25, 654.64) * mm});
            skLineSegment(sketch, "E2248", {"start": v(50.25, 654.64) * mm, "end": v(50.56, 654.44) * mm});
            skLineSegment(sketch, "E2249", {"start": v(50.56, 654.44) * mm, "end": v(50.87, 654.25) * mm});
            skLineSegment(sketch, "E2250", {"start": v(50.87, 654.25) * mm, "end": v(51.18, 654.07) * mm});
            skLineSegment(sketch, "E2251", {"start": v(51.18, 654.07) * mm, "end": v(51.5, 653.9) * mm});
            skLineSegment(sketch, "E2252", {"start": v(51.5, 653.9) * mm, "end": v(51.82, 653.73) * mm});
            skLineSegment(sketch, "E2253", {"start": v(51.82, 653.73) * mm, "end": v(52.15, 653.58) * mm});
            skLineSegment(sketch, "E2254", {"start": v(52.15, 653.58) * mm, "end": v(52.48, 653.43) * mm});
            skLineSegment(sketch, "E2255", {"start": v(52.48, 653.43) * mm, "end": v(52.82, 653.3) * mm});
            skLineSegment(sketch, "E2256", {"start": v(52.82, 653.3) * mm, "end": v(53.15, 653.16) * mm});
            skLineSegment(sketch, "E2257", {"start": v(53.15, 653.16) * mm, "end": v(53.5, 653.05) * mm});
            skLineSegment(sketch, "E2258", {"start": v(53.5, 653.05) * mm, "end": v(53.84, 652.93) * mm});
            skLineSegment(sketch, "E2259", {"start": v(53.84, 652.93) * mm, "end": v(54.19, 652.83) * mm});
            skLineSegment(sketch, "E2260", {"start": v(54.19, 652.83) * mm, "end": v(54.54, 652.74) * mm});
            skLineSegment(sketch, "E2261", {"start": v(54.54, 652.74) * mm, "end": v(54.9, 652.66) * mm});
            skLineSegment(sketch, "E2262", {"start": v(54.9, 652.66) * mm, "end": v(55.25, 652.59) * mm});
            skLineSegment(sketch, "E2263", {"start": v(55.25, 652.59) * mm, "end": v(55.6, 652.52) * mm});
            skLineSegment(sketch, "E2264", {"start": v(55.6, 652.52) * mm, "end": v(55.96, 652.47) * mm});
            skLineSegment(sketch, "E2265", {"start": v(55.96, 652.47) * mm, "end": v(56.33, 652.42) * mm});
            skLineSegment(sketch, "E2266", {"start": v(56.33, 652.42) * mm, "end": v(56.69, 652.39) * mm});
            skLineSegment(sketch, "E2267", {"start": v(56.69, 652.39) * mm, "end": v(57.05, 652.36) * mm});
            skLineSegment(sketch, "E2268", {"start": v(57.05, 652.36) * mm, "end": v(57.42, 652.35) * mm});
            skLineSegment(sketch, "E2269", {"start": v(57.42, 652.35) * mm, "end": v(57.79, 652.34) * mm});
            skLineSegment(sketch, "E2270", {"start": v(57.79, 652.34) * mm, "end": v(58.15, 652.35) * mm});
            skLineSegment(sketch, "E2271", {"start": v(58.15, 652.35) * mm, "end": v(58.52, 652.36) * mm});
            skLineSegment(sketch, "E2272", {"start": v(58.52, 652.36) * mm, "end": v(59.01, 652.42) * mm});
            skLineSegment(sketch, "E2273", {"start": v(59.01, 652.42) * mm, "end": v(59.5, 652.45) * mm});
            skLineSegment(sketch, "E2274", {"start": v(59.5, 652.45) * mm, "end": v(59.99, 652.46) * mm});
            skLineSegment(sketch, "E2275", {"start": v(59.99, 652.46) * mm, "end": v(60.47, 652.44) * mm});
            skLineSegment(sketch, "E2276", {"start": v(60.47, 652.44) * mm, "end": v(60.94, 652.4) * mm});
            skLineSegment(sketch, "E2277", {"start": v(60.94, 652.4) * mm, "end": v(61.42, 652.34) * mm});
            skLineSegment(sketch, "E2278", {"start": v(61.42, 652.34) * mm, "end": v(61.88, 652.25) * mm});
            skLineSegment(sketch, "E2279", {"start": v(61.88, 652.25) * mm, "end": v(62.34, 652.15) * mm});
            skLineSegment(sketch, "E2280", {"start": v(62.34, 652.15) * mm, "end": v(62.8, 652.02) * mm});
            skLineSegment(sketch, "E2281", {"start": v(62.8, 652.02) * mm, "end": v(63.24, 651.87) * mm});
            skLineSegment(sketch, "E2282", {"start": v(63.24, 651.87) * mm, "end": v(63.67, 651.7) * mm});
            skLineSegment(sketch, "E2283", {"start": v(63.67, 651.7) * mm, "end": v(64.1, 651.52) * mm});
            skLineSegment(sketch, "E2284", {"start": v(64.1, 651.52) * mm, "end": v(64.52, 651.31) * mm});
            skLineSegment(sketch, "E2285", {"start": v(64.52, 651.31) * mm, "end": v(64.93, 651.08) * mm});
            skLineSegment(sketch, "E2286", {"start": v(64.93, 651.08) * mm, "end": v(65.32, 650.84) * mm});
            skLineSegment(sketch, "E2287", {"start": v(65.32, 650.84) * mm, "end": v(65.7, 650.58) * mm});
            skLineSegment(sketch, "E2288", {"start": v(65.7, 650.58) * mm, "end": v(66.08, 650.3) * mm});
            skLineSegment(sketch, "E2289", {"start": v(66.08, 650.3) * mm, "end": v(66.43, 650) * mm});
            skLineSegment(sketch, "E2290", {"start": v(66.43, 650) * mm, "end": v(66.78, 649.7) * mm});
            skLineSegment(sketch, "E2291", {"start": v(66.78, 649.7) * mm, "end": v(67.1, 649.36) * mm});
            skLineSegment(sketch, "E2292", {"start": v(67.1, 649.36) * mm, "end": v(67.42, 649.02) * mm});
            skLineSegment(sketch, "E2293", {"start": v(67.42, 649.02) * mm, "end": v(67.72, 648.66) * mm});
            skLineSegment(sketch, "E2294", {"start": v(67.72, 648.66) * mm, "end": v(68, 648.29) * mm});
            skLineSegment(sketch, "E2295", {"start": v(68, 648.29) * mm, "end": v(68.27, 647.9) * mm});
            skLineSegment(sketch, "E2296", {"start": v(68.27, 647.9) * mm, "end": v(68.52, 647.5) * mm});
            skLineSegment(sketch, "E2297", {"start": v(68.52, 647.5) * mm, "end": v(68.75, 647.08) * mm});
            skLineSegment(sketch, "E2298", {"start": v(68.75, 647.08) * mm, "end": v(68.96, 646.66) * mm});
            skLineSegment(sketch, "E2299", {"start": v(68.96, 646.66) * mm, "end": v(69.15, 646.22) * mm});
            skLineSegment(sketch, "E2300", {"start": v(69.15, 646.22) * mm, "end": v(69.32, 645.77) * mm});
            skLineSegment(sketch, "E2301", {"start": v(69.32, 645.77) * mm, "end": v(69.47, 645.3) * mm});
            skLineSegment(sketch, "E2302", {"start": v(69.47, 645.3) * mm, "end": v(69.6, 644.83) * mm});
            skLineSegment(sketch, "E2303", {"start": v(69.6, 644.83) * mm, "end": v(69.7, 644.35) * mm});
            skLineSegment(sketch, "E2304", {"start": v(69.7, 644.35) * mm, "end": v(69.7, 643.95) * mm});
            skLineSegment(sketch, "E2305", {"start": v(69.7, 643.95) * mm, "end": v(69.68, 643.55) * mm});
            skLineSegment(sketch, "E2306", {"start": v(69.68, 643.55) * mm, "end": v(69.63, 643.16) * mm});
            skLineSegment(sketch, "E2307", {"start": v(69.63, 643.16) * mm, "end": v(69.57, 642.77) * mm});
            skLineSegment(sketch, "E2308", {"start": v(69.57, 642.77) * mm, "end": v(69.48, 642.39) * mm});
            skLineSegment(sketch, "E2309", {"start": v(69.48, 642.39) * mm, "end": v(69.37, 642.01) * mm});
            skLineSegment(sketch, "E2310", {"start": v(69.37, 642.01) * mm, "end": v(69.24, 641.64) * mm});
            skLineSegment(sketch, "E2311", {"start": v(69.24, 641.64) * mm, "end": v(69.09, 641.28) * mm});
            skLineSegment(sketch, "E2312", {"start": v(69.09, 641.28) * mm, "end": v(68.92, 640.93) * mm});
            skLineSegment(sketch, "E2313", {"start": v(68.92, 640.93) * mm, "end": v(68.73, 640.58) * mm});
            skLineSegment(sketch, "E2314", {"start": v(68.73, 640.58) * mm, "end": v(68.52, 640.25) * mm});
            skLineSegment(sketch, "E2315", {"start": v(68.52, 640.25) * mm, "end": v(68.3, 639.93) * mm});
            skLineSegment(sketch, "E2316", {"start": v(68.3, 639.93) * mm, "end": v(68.05, 639.62) * mm});
            skLineSegment(sketch, "E2317", {"start": v(68.05, 639.62) * mm, "end": v(67.78, 639.32) * mm});
            skLineSegment(sketch, "E2318", {"start": v(67.78, 639.32) * mm, "end": v(67.5, 639.04) * mm});
            skLineSegment(sketch, "E2319", {"start": v(67.5, 639.04) * mm, "end": v(67.2, 638.77) * mm});
            skLineSegment(sketch, "E2320", {"start": v(67.2, 638.77) * mm, "end": v(66.96, 638.56) * mm});
            skLineSegment(sketch, "E2321", {"start": v(66.96, 638.56) * mm, "end": v(66.7, 638.35) * mm});
            skLineSegment(sketch, "E2322", {"start": v(66.7, 638.35) * mm, "end": v(66.46, 638.14) * mm});
            skLineSegment(sketch, "E2323", {"start": v(66.46, 638.14) * mm, "end": v(66.2, 637.95) * mm});
            skLineSegment(sketch, "E2324", {"start": v(66.2, 637.95) * mm, "end": v(65.93, 637.76) * mm});
            skLineSegment(sketch, "E2325", {"start": v(65.93, 637.76) * mm, "end": v(65.67, 637.57) * mm});
            skLineSegment(sketch, "E2326", {"start": v(65.67, 637.57) * mm, "end": v(65.4, 637.4) * mm});
            skLineSegment(sketch, "E2327", {"start": v(65.4, 637.4) * mm, "end": v(65.12, 637.23) * mm});
            skLineSegment(sketch, "E2328", {"start": v(65.12, 637.23) * mm, "end": v(64.84, 637.07) * mm});
            skLineSegment(sketch, "E2329", {"start": v(64.84, 637.07) * mm, "end": v(64.56, 636.91) * mm});
            skLineSegment(sketch, "E2330", {"start": v(64.56, 636.91) * mm, "end": v(64.27, 636.76) * mm});
            skLineSegment(sketch, "E2331", {"start": v(64.27, 636.76) * mm, "end": v(63.98, 636.62) * mm});
            skLineSegment(sketch, "E2332", {"start": v(63.98, 636.62) * mm, "end": v(63.69, 636.5) * mm});
            skLineSegment(sketch, "E2333", {"start": v(63.69, 636.5) * mm, "end": v(63.39, 636.37) * mm});
            skLineSegment(sketch, "E2334", {"start": v(63.39, 636.37) * mm, "end": v(63.09, 636.25) * mm});
            skLineSegment(sketch, "E2335", {"start": v(63.09, 636.25) * mm, "end": v(62.79, 636.14) * mm});
            skLineSegment(sketch, "E2336", {"start": v(62.79, 636.14) * mm, "end": v(62.48, 636.03) * mm});
            skLineSegment(sketch, "E2337", {"start": v(62.48, 636.03) * mm, "end": v(62.17, 635.94) * mm});
            skLineSegment(sketch, "E2338", {"start": v(62.17, 635.94) * mm, "end": v(61.86, 635.85) * mm});
            skLineSegment(sketch, "E2339", {"start": v(61.86, 635.85) * mm, "end": v(61.55, 635.77) * mm});
            skLineSegment(sketch, "E2340", {"start": v(61.55, 635.77) * mm, "end": v(61.24, 635.7) * mm});
            skLineSegment(sketch, "E2341", {"start": v(61.24, 635.7) * mm, "end": v(60.92, 635.64) * mm});
            skLineSegment(sketch, "E2342", {"start": v(60.92, 635.64) * mm, "end": v(60.6, 635.58) * mm});
            skLineSegment(sketch, "E2343", {"start": v(60.6, 635.58) * mm, "end": v(60.28, 635.53) * mm});
            skLineSegment(sketch, "E2344", {"start": v(60.28, 635.53) * mm, "end": v(59.96, 635.5) * mm});
            skLineSegment(sketch, "E2345", {"start": v(59.96, 635.5) * mm, "end": v(59.64, 635.46) * mm});
            skLineSegment(sketch, "E2346", {"start": v(59.64, 635.46) * mm, "end": v(59.32, 635.43) * mm});
            skLineSegment(sketch, "E2347", {"start": v(59.32, 635.43) * mm, "end": v(59, 635.42) * mm});
            skLineSegment(sketch, "E2348", {"start": v(59, 635.42) * mm, "end": v(58.67, 635.4) * mm});
            skLineSegment(sketch, "E2349", {"start": v(58.67, 635.4) * mm, "end": v(58.34, 635.41) * mm});
            skLineSegment(sketch, "E2350", {"start": v(58.34, 635.41) * mm, "end": v(58.02, 635.42) * mm});
            skLineSegment(sketch, "E2351", {"start": v(58.02, 635.42) * mm, "end": v(57.7, 635.44) * mm});
            skLineSegment(sketch, "E2352", {"start": v(57.7, 635.44) * mm, "end": v(57.12, 635.44) * mm});
            skLineSegment(sketch, "E2353", {"start": v(57.12, 635.44) * mm, "end": v(56.54, 635.46) * mm});
            skLineSegment(sketch, "E2354", {"start": v(56.54, 635.46) * mm, "end": v(55.98, 635.52) * mm});
            skLineSegment(sketch, "E2355", {"start": v(55.98, 635.52) * mm, "end": v(55.41, 635.6) * mm});
            skLineSegment(sketch, "E2356", {"start": v(55.41, 635.6) * mm, "end": v(54.85, 635.71) * mm});
            skLineSegment(sketch, "E2357", {"start": v(54.85, 635.71) * mm, "end": v(54.3, 635.85) * mm});
            skLineSegment(sketch, "E2358", {"start": v(54.3, 635.85) * mm, "end": v(53.76, 636) * mm});
            skLineSegment(sketch, "E2359", {"start": v(53.76, 636) * mm, "end": v(53.22, 636.2) * mm});
            skLineSegment(sketch, "E2360", {"start": v(53.22, 636.2) * mm, "end": v(52.7, 636.4) * mm});
            skLineSegment(sketch, "E2361", {"start": v(52.7, 636.4) * mm, "end": v(52.18, 636.65) * mm});
            skLineSegment(sketch, "E2362", {"start": v(52.18, 636.65) * mm, "end": v(51.68, 636.9) * mm});
            skLineSegment(sketch, "E2363", {"start": v(51.68, 636.9) * mm, "end": v(51.19, 637.2) * mm});
            skLineSegment(sketch, "E2364", {"start": v(51.19, 637.2) * mm, "end": v(50.71, 637.5) * mm});
            skLineSegment(sketch, "E2365", {"start": v(50.71, 637.5) * mm, "end": v(50.25, 637.84) * mm});
            skLineSegment(sketch, "E2366", {"start": v(50.25, 637.84) * mm, "end": v(49.8, 638.2) * mm});
            skLineSegment(sketch, "E2367", {"start": v(49.8, 638.2) * mm, "end": v(49.37, 638.58) * mm});
            skLineSegment(sketch, "E2368", {"start": v(49.37, 638.58) * mm, "end": v(49.1, 638.86) * mm});
            skLineSegment(sketch, "E2369", {"start": v(49.1, 638.86) * mm, "end": v(48.86, 639.16) * mm});
            skLineSegment(sketch, "E2370", {"start": v(48.86, 639.16) * mm, "end": v(48.62, 639.46) * mm});
            skLineSegment(sketch, "E2371", {"start": v(48.62, 639.46) * mm, "end": v(48.39, 639.77) * mm});
            skLineSegment(sketch, "E2372", {"start": v(48.39, 639.77) * mm, "end": v(48.17, 640.1) * mm});
            skLineSegment(sketch, "E2373", {"start": v(48.17, 640.1) * mm, "end": v(47.96, 640.42) * mm});
            skLineSegment(sketch, "E2374", {"start": v(47.96, 640.42) * mm, "end": v(47.77, 640.75) * mm});
            skLineSegment(sketch, "E2375", {"start": v(47.77, 640.75) * mm, "end": v(47.59, 641.09) * mm});
            skLineSegment(sketch, "E2376", {"start": v(47.59, 641.09) * mm, "end": v(47.41, 641.43) * mm});
            skLineSegment(sketch, "E2377", {"start": v(47.41, 641.43) * mm, "end": v(47.25, 641.78) * mm});
            skLineSegment(sketch, "E2378", {"start": v(47.25, 641.78) * mm, "end": v(47.1, 642.14) * mm});
            skLineSegment(sketch, "E2379", {"start": v(47.1, 642.14) * mm, "end": v(46.97, 642.5) * mm});
            skLineSegment(sketch, "E2380", {"start": v(46.97, 642.5) * mm, "end": v(46.85, 642.87) * mm});
            skLineSegment(sketch, "E2381", {"start": v(46.85, 642.87) * mm, "end": v(46.74, 643.24) * mm});
            skLineSegment(sketch, "E2382", {"start": v(46.74, 643.24) * mm, "end": v(46.64, 643.61) * mm});
            skLineSegment(sketch, "E2383", {"start": v(46.64, 643.61) * mm, "end": v(46.56, 643.99) * mm});
            skLineSegment(sketch, "E2384", {"start": v(38.27, 671.1) * mm, "end": v(38.27, 636.15) * mm});
            skLineSegment(sketch, "E2385", {"start": v(30.57, 671.1) * mm, "end": v(30.57, 636.13) * mm});
            skLineSegment(sketch, "E2386", {"start": v(30.57, 636.13) * mm, "end": v(17.75, 636.13) * mm});
            skLineSegment(sketch, "E2387", {"start": v(17.75, 636.13) * mm, "end": v(17.44, 636.14) * mm});
            skLineSegment(sketch, "E2388", {"start": v(17.44, 636.14) * mm, "end": v(17.14, 636.17) * mm});
            skLineSegment(sketch, "E2389", {"start": v(17.14, 636.17) * mm, "end": v(16.84, 636.2) * mm});
            skLineSegment(sketch, "E2390", {"start": v(16.84, 636.2) * mm, "end": v(16.54, 636.23) * mm});
            skLineSegment(sketch, "E2391", {"start": v(16.54, 636.23) * mm, "end": v(16.24, 636.28) * mm});
            skLineSegment(sketch, "E2392", {"start": v(16.24, 636.28) * mm, "end": v(15.94, 636.33) * mm});
            skLineSegment(sketch, "E2393", {"start": v(15.94, 636.33) * mm, "end": v(15.65, 636.39) * mm});
            skLineSegment(sketch, "E2394", {"start": v(15.65, 636.39) * mm, "end": v(15.36, 636.46) * mm});
            skLineSegment(sketch, "E2395", {"start": v(15.36, 636.46) * mm, "end": v(15.06, 636.53) * mm});
            skLineSegment(sketch, "E2396", {"start": v(15.06, 636.53) * mm, "end": v(14.77, 636.61) * mm});
            skLineSegment(sketch, "E2397", {"start": v(14.77, 636.61) * mm, "end": v(14.49, 636.7) * mm});
            skLineSegment(sketch, "E2398", {"start": v(14.49, 636.7) * mm, "end": v(14.2, 636.8) * mm});
            skLineSegment(sketch, "E2399", {"start": v(14.2, 636.8) * mm, "end": v(13.64, 637.01) * mm});
            skLineSegment(sketch, "E2400", {"start": v(13.64, 637.01) * mm, "end": v(13.1, 637.25) * mm});
            skLineSegment(sketch, "E2401", {"start": v(13.1, 637.25) * mm, "end": v(12.56, 637.52) * mm});
            skLineSegment(sketch, "E2402", {"start": v(12.56, 637.52) * mm, "end": v(12.04, 637.81) * mm});
            skLineSegment(sketch, "E2403", {"start": v(12.04, 637.81) * mm, "end": v(11.78, 637.97) * mm});
            skLineSegment(sketch, "E2404", {"start": v(11.78, 637.97) * mm, "end": v(11.53, 638.13) * mm});
            skLineSegment(sketch, "E2405", {"start": v(11.53, 638.13) * mm, "end": v(11.28, 638.3) * mm});
            skLineSegment(sketch, "E2406", {"start": v(11.28, 638.3) * mm, "end": v(11.04, 638.48) * mm});
            skLineSegment(sketch, "E2407", {"start": v(11.04, 638.48) * mm, "end": v(10.8, 638.66) * mm});
            skLineSegment(sketch, "E2408", {"start": v(10.8, 638.66) * mm, "end": v(10.56, 638.85) * mm});
            skLineSegment(sketch, "E2409", {"start": v(10.56, 638.85) * mm, "end": v(10.33, 639.04) * mm});
            skLineSegment(sketch, "E2410", {"start": v(10.33, 639.04) * mm, "end": v(10.1, 639.25) * mm});
            skLineSegment(sketch, "E2411", {"start": v(10.1, 639.25) * mm, "end": v(9.89, 639.45) * mm});
            skLineSegment(sketch, "E2412", {"start": v(9.89, 639.45) * mm, "end": v(9.67, 639.66) * mm});
            skLineSegment(sketch, "E2413", {"start": v(9.67, 639.66) * mm, "end": v(9.46, 639.88) * mm});
            skLineSegment(sketch, "E2414", {"start": v(9.46, 639.88) * mm, "end": v(9.25, 640.1) * mm});
            skLineSegment(sketch, "E2415", {"start": v(9.25, 640.1) * mm, "end": v(8.9, 640.47) * mm});
            skLineSegment(sketch, "E2416", {"start": v(8.9, 640.47) * mm, "end": v(8.56, 640.84) * mm});
            skLineSegment(sketch, "E2417", {"start": v(8.56, 640.84) * mm, "end": v(8.23, 641.21) * mm});
            skLineSegment(sketch, "E2418", {"start": v(8.23, 641.21) * mm, "end": v(7.91, 641.6) * mm});
            skLineSegment(sketch, "E2419", {"start": v(7.91, 641.6) * mm, "end": v(7.6, 641.99) * mm});
            skLineSegment(sketch, "E2420", {"start": v(7.6, 641.99) * mm, "end": v(7.3, 642.39) * mm});
            skLineSegment(sketch, "E2421", {"start": v(7.3, 642.39) * mm, "end": v(7.01, 642.8) * mm});
            skLineSegment(sketch, "E2422", {"start": v(7.01, 642.8) * mm, "end": v(6.73, 643.2) * mm});
            skLineSegment(sketch, "E2423", {"start": v(6.73, 643.2) * mm, "end": v(6.46, 643.63) * mm});
            skLineSegment(sketch, "E2424", {"start": v(6.46, 643.63) * mm, "end": v(6.2, 644.05) * mm});
            skLineSegment(sketch, "E2425", {"start": v(6.2, 644.05) * mm, "end": v(5.96, 644.48) * mm});
            skLineSegment(sketch, "E2426", {"start": v(5.96, 644.48) * mm, "end": v(5.73, 644.92) * mm});
            skLineSegment(sketch, "E2427", {"start": v(5.73, 644.92) * mm, "end": v(5.5, 645.36) * mm});
            skLineSegment(sketch, "E2428", {"start": v(5.5, 645.36) * mm, "end": v(5.29, 645.8) * mm});
            skLineSegment(sketch, "E2429", {"start": v(5.29, 645.8) * mm, "end": v(5.09, 646.26) * mm});
            skLineSegment(sketch, "E2430", {"start": v(5.09, 646.26) * mm, "end": v(4.9, 646.72) * mm});
            skLineSegment(sketch, "E2431", {"start": v(4.9, 646.72) * mm, "end": v(4.72, 647.18) * mm});
            skLineSegment(sketch, "E2432", {"start": v(4.72, 647.18) * mm, "end": v(4.55, 647.65) * mm});
            skLineSegment(sketch, "E2433", {"start": v(4.55, 647.65) * mm, "end": v(4.4, 648.12) * mm});
            skLineSegment(sketch, "E2434", {"start": v(4.4, 648.12) * mm, "end": v(4.25, 648.6) * mm});
            skLineSegment(sketch, "E2435", {"start": v(4.25, 648.6) * mm, "end": v(4.12, 649.07) * mm});
            skLineSegment(sketch, "E2436", {"start": v(4.12, 649.07) * mm, "end": v(4, 649.55) * mm});
            skLineSegment(sketch, "E2437", {"start": v(4, 649.55) * mm, "end": v(3.89, 650.04) * mm});
            skLineSegment(sketch, "E2438", {"start": v(3.89, 650.04) * mm, "end": v(3.8, 650.52) * mm});
            skLineSegment(sketch, "E2439", {"start": v(3.8, 650.52) * mm, "end": v(3.7, 651.01) * mm});
            skLineSegment(sketch, "E2440", {"start": v(3.7, 651.01) * mm, "end": v(3.63, 651.5) * mm});
            skLineSegment(sketch, "E2441", {"start": v(3.63, 651.5) * mm, "end": v(3.57, 652) * mm});
            skLineSegment(sketch, "E2442", {"start": v(3.57, 652) * mm, "end": v(3.53, 652.5) * mm});
            skLineSegment(sketch, "E2443", {"start": v(3.53, 652.5) * mm, "end": v(3.5, 653) * mm});
            skLineSegment(sketch, "E2444", {"start": v(3.5, 653) * mm, "end": v(3.47, 653.5) * mm});
            skLineSegment(sketch, "E2445", {"start": v(3.47, 653.5) * mm, "end": v(3.46, 654) * mm});
            skLineSegment(sketch, "E2446", {"start": v(3.46, 654) * mm, "end": v(3.46, 654.5) * mm});
            skLineSegment(sketch, "E2447", {"start": v(3.46, 654.5) * mm, "end": v(3.45, 654.93) * mm});
            skLineSegment(sketch, "E2448", {"start": v(3.45, 654.93) * mm, "end": v(3.45, 655.35) * mm});
            skLineSegment(sketch, "E2449", {"start": v(3.45, 655.35) * mm, "end": v(3.46, 655.77) * mm});
            skLineSegment(sketch, "E2450", {"start": v(3.46, 655.77) * mm, "end": v(3.49, 656.19) * mm});
            skLineSegment(sketch, "E2451", {"start": v(3.49, 656.19) * mm, "end": v(3.52, 656.6) * mm});
            skLineSegment(sketch, "E2452", {"start": v(3.52, 656.6) * mm, "end": v(3.56, 657.02) * mm});
            skLineSegment(sketch, "E2453", {"start": v(3.56, 657.02) * mm, "end": v(3.61, 657.44) * mm});
            skLineSegment(sketch, "E2454", {"start": v(3.61, 657.44) * mm, "end": v(3.67, 657.85) * mm});
            skLineSegment(sketch, "E2455", {"start": v(3.67, 657.85) * mm, "end": v(3.75, 658.26) * mm});
            skLineSegment(sketch, "E2456", {"start": v(3.75, 658.26) * mm, "end": v(3.83, 658.67) * mm});
            skLineSegment(sketch, "E2457", {"start": v(3.83, 658.67) * mm, "end": v(3.92, 659.07) * mm});
            skLineSegment(sketch, "E2458", {"start": v(3.92, 659.07) * mm, "end": v(4.02, 659.48) * mm});
            skLineSegment(sketch, "E2459", {"start": v(4.02, 659.48) * mm, "end": v(4.13, 659.88) * mm});
            skLineSegment(sketch, "E2460", {"start": v(4.13, 659.88) * mm, "end": v(4.26, 660.28) * mm});
            skLineSegment(sketch, "E2461", {"start": v(4.26, 660.28) * mm, "end": v(4.39, 660.67) * mm});
            skLineSegment(sketch, "E2462", {"start": v(4.39, 660.67) * mm, "end": v(4.53, 661.06) * mm});
            skLineSegment(sketch, "E2463", {"start": v(4.53, 661.06) * mm, "end": v(4.68, 661.45) * mm});
            skLineSegment(sketch, "E2464", {"start": v(4.68, 661.45) * mm, "end": v(4.84, 661.83) * mm});
            skLineSegment(sketch, "E2465", {"start": v(4.84, 661.83) * mm, "end": v(5, 662.21) * mm});
            skLineSegment(sketch, "E2466", {"start": v(5, 662.21) * mm, "end": v(5.18, 662.59) * mm});
            skLineSegment(sketch, "E2467", {"start": v(5.18, 662.59) * mm, "end": v(5.37, 662.96) * mm});
            skLineSegment(sketch, "E2468", {"start": v(5.37, 662.96) * mm, "end": v(5.57, 663.33) * mm});
            skLineSegment(sketch, "E2469", {"start": v(5.57, 663.33) * mm, "end": v(5.77, 663.7) * mm});
            skLineSegment(sketch, "E2470", {"start": v(5.77, 663.7) * mm, "end": v(5.99, 664.05) * mm});
            skLineSegment(sketch, "E2471", {"start": v(5.99, 664.05) * mm, "end": v(6.21, 664.4) * mm});
            skLineSegment(sketch, "E2472", {"start": v(6.21, 664.4) * mm, "end": v(6.45, 664.75) * mm});
            skLineSegment(sketch, "E2473", {"start": v(6.45, 664.75) * mm, "end": v(6.69, 665.09) * mm});
            skLineSegment(sketch, "E2474", {"start": v(6.69, 665.09) * mm, "end": v(6.94, 665.43) * mm});
            skLineSegment(sketch, "E2475", {"start": v(6.94, 665.43) * mm, "end": v(7.2, 665.76) * mm});
            skLineSegment(sketch, "E2476", {"start": v(7.2, 665.76) * mm, "end": v(7.46, 666.08) * mm});
            skLineSegment(sketch, "E2477", {"start": v(7.46, 666.08) * mm, "end": v(7.74, 666.4) * mm});
            skLineSegment(sketch, "E2478", {"start": v(7.74, 666.4) * mm, "end": v(8.02, 666.7) * mm});
            skLineSegment(sketch, "E2479", {"start": v(8.02, 666.7) * mm, "end": v(8.26, 666.96) * mm});
            skLineSegment(sketch, "E2480", {"start": v(8.26, 666.96) * mm, "end": v(8.5, 667.2) * mm});
            skLineSegment(sketch, "E2481", {"start": v(8.5, 667.2) * mm, "end": v(8.76, 667.44) * mm});
            skLineSegment(sketch, "E2482", {"start": v(8.76, 667.44) * mm, "end": v(9.01, 667.67) * mm});
            skLineSegment(sketch, "E2483", {"start": v(9.01, 667.67) * mm, "end": v(9.28, 667.89) * mm});
            skLineSegment(sketch, "E2484", {"start": v(9.28, 667.89) * mm, "end": v(9.54, 668.1) * mm});
            skLineSegment(sketch, "E2485", {"start": v(9.54, 668.1) * mm, "end": v(9.81, 668.31) * mm});
            skLineSegment(sketch, "E2486", {"start": v(9.81, 668.31) * mm, "end": v(10.09, 668.51) * mm});
            skLineSegment(sketch, "E2487", {"start": v(10.09, 668.51) * mm, "end": v(10.37, 668.7) * mm});
            skLineSegment(sketch, "E2488", {"start": v(10.37, 668.7) * mm, "end": v(10.65, 668.9) * mm});
            skLineSegment(sketch, "E2489", {"start": v(10.65, 668.9) * mm, "end": v(10.94, 669.08) * mm});
            skLineSegment(sketch, "E2490", {"start": v(10.94, 669.08) * mm, "end": v(11.24, 669.25) * mm});
            skLineSegment(sketch, "E2491", {"start": v(11.24, 669.25) * mm, "end": v(11.54, 669.42) * mm});
            skLineSegment(sketch, "E2492", {"start": v(11.54, 669.42) * mm, "end": v(11.84, 669.58) * mm});
            skLineSegment(sketch, "E2493", {"start": v(11.84, 669.58) * mm, "end": v(12.14, 669.73) * mm});
            skLineSegment(sketch, "E2494", {"start": v(12.14, 669.73) * mm, "end": v(12.45, 669.87) * mm});
            skLineSegment(sketch, "E2495", {"start": v(12.45, 669.87) * mm, "end": v(12.76, 670) * mm});
            skLineSegment(sketch, "E2496", {"start": v(12.76, 670) * mm, "end": v(13.08, 670.14) * mm});
            skLineSegment(sketch, "E2497", {"start": v(13.08, 670.14) * mm, "end": v(13.4, 670.26) * mm});
            skLineSegment(sketch, "E2498", {"start": v(13.4, 670.26) * mm, "end": v(13.72, 670.37) * mm});
            skLineSegment(sketch, "E2499", {"start": v(13.72, 670.37) * mm, "end": v(14.04, 670.48) * mm});
            skLineSegment(sketch, "E2500", {"start": v(14.04, 670.48) * mm, "end": v(14.37, 670.58) * mm});
            skLineSegment(sketch, "E2501", {"start": v(14.37, 670.58) * mm, "end": v(14.7, 670.67) * mm});
            skLineSegment(sketch, "E2502", {"start": v(14.7, 670.67) * mm, "end": v(15.03, 670.75) * mm});
            skLineSegment(sketch, "E2503", {"start": v(15.03, 670.75) * mm, "end": v(15.36, 670.82) * mm});
            skLineSegment(sketch, "E2504", {"start": v(15.36, 670.82) * mm, "end": v(15.7, 670.89) * mm});
            skLineSegment(sketch, "E2505", {"start": v(15.7, 670.89) * mm, "end": v(16.04, 670.94) * mm});
            skLineSegment(sketch, "E2506", {"start": v(16.04, 670.94) * mm, "end": v(16.38, 671) * mm});
            skLineSegment(sketch, "E2507", {"start": v(16.38, 671) * mm, "end": v(16.72, 671.04) * mm});
            skLineSegment(sketch, "E2508", {"start": v(16.72, 671.04) * mm, "end": v(17.06, 671.07) * mm});
            skLineSegment(sketch, "E2509", {"start": v(17.06, 671.07) * mm, "end": v(17.4, 671.1) * mm});
            skLineSegment(sketch, "E2510", {"start": v(17.4, 671.1) * mm, "end": v(17.75, 671.1) * mm});
            skLineSegment(sketch, "E2511", {"start": v(17.75, 671.1) * mm, "end": v(30.57, 671.1) * mm});
            skLineSegment(sketch, "E2512", {"start": v(-27.46, 671.1) * mm, "end": v(-4.43, 671.1) * mm});
            skLineSegment(sketch, "E2513", {"start": v(-4.43, 671.1) * mm, "end": v(-4.43, 636.14) * mm});
            skLineSegment(sketch, "E2514", {"start": v(-4.43, 636.14) * mm, "end": v(-27.46, 636.14) * mm});
            skLineSegment(sketch, "E2515", {"start": v(-4.43, 652.99) * mm, "end": v(-24.57, 652.99) * mm});
            skArc(sketch, "E2516", {"start": v(228.25, -951.25) * mm, "mid": v(230.37, -950.37) * mm, "end": v(231.25, -948.25) * mm});
            skArc(sketch, "E2517", {"start": v(231.25, -948.25) * mm, "mid": v(230.37, -946.13) * mm, "end": v(228.25, -945.25) * mm});
            skArc(sketch, "E2518", {"start": v(228.25, -945.25) * mm, "mid": v(226.13, -946.13) * mm, "end": v(225.25, -948.25) * mm});
            skArc(sketch, "E2519", {"start": v(225.25, -948.25) * mm, "mid": v(226.13, -950.37) * mm, "end": v(228.25, -951.25) * mm});
            skArc(sketch, "E2520", {"start": v(282.25, -951.25) * mm, "mid": v(284.37, -950.37) * mm, "end": v(285.25, -948.25) * mm});
            skArc(sketch, "E2521", {"start": v(285.25, -948.25) * mm, "mid": v(284.37, -946.13) * mm, "end": v(282.25, -945.25) * mm});
            skArc(sketch, "E2522", {"start": v(282.25, -945.25) * mm, "mid": v(280.13, -946.13) * mm, "end": v(279.25, -948.25) * mm});
            skArc(sketch, "E2523", {"start": v(279.25, -948.25) * mm, "mid": v(280.13, -950.37) * mm, "end": v(282.25, -951.25) * mm});
            skArc(sketch, "E2524", {"start": v(228.25, -1101.25) * mm, "mid": v(230.37, -1100.37) * mm, "end": v(231.25, -1098.25) * mm});
            skArc(sketch, "E2525", {"start": v(231.25, -1098.25) * mm, "mid": v(230.37, -1096.13) * mm, "end": v(228.25, -1095.25) * mm});
            skArc(sketch, "E2526", {"start": v(228.25, -1095.25) * mm, "mid": v(226.13, -1096.13) * mm, "end": v(225.25, -1098.25) * mm});
            skArc(sketch, "E2527", {"start": v(225.25, -1098.25) * mm, "mid": v(226.13, -1100.37) * mm, "end": v(228.25, -1101.25) * mm});
            skArc(sketch, "E2528", {"start": v(282.25, -1101.25) * mm, "mid": v(284.37, -1100.37) * mm, "end": v(285.25, -1098.25) * mm});
            skArc(sketch, "E2529", {"start": v(285.25, -1098.25) * mm, "mid": v(284.37, -1096.13) * mm, "end": v(282.25, -1095.25) * mm});
            skArc(sketch, "E2530", {"start": v(282.25, -1095.25) * mm, "mid": v(280.13, -1096.13) * mm, "end": v(279.25, -1098.25) * mm});
            skArc(sketch, "E2531", {"start": v(279.25, -1098.25) * mm, "mid": v(280.13, -1100.37) * mm, "end": v(282.25, -1101.25) * mm});
            skArc(sketch, "E2532", {"start": v(228.25, -801.25) * mm, "mid": v(230.37, -800.37) * mm, "end": v(231.25, -798.25) * mm});
            skArc(sketch, "E2533", {"start": v(231.25, -798.25) * mm, "mid": v(230.37, -796.13) * mm, "end": v(228.25, -795.25) * mm});
            skArc(sketch, "E2534", {"start": v(228.25, -795.25) * mm, "mid": v(226.13, -796.13) * mm, "end": v(225.25, -798.25) * mm});
            skArc(sketch, "E2535", {"start": v(225.25, -798.25) * mm, "mid": v(226.13, -800.37) * mm, "end": v(228.25, -801.25) * mm});
            skArc(sketch, "E2536", {"start": v(282.25, -801.25) * mm, "mid": v(284.37, -800.37) * mm, "end": v(285.25, -798.25) * mm});
            skArc(sketch, "E2537", {"start": v(285.25, -798.25) * mm, "mid": v(284.37, -796.13) * mm, "end": v(282.25, -795.25) * mm});
            skArc(sketch, "E2538", {"start": v(282.25, -795.25) * mm, "mid": v(280.13, -796.13) * mm, "end": v(279.25, -798.25) * mm});
            skArc(sketch, "E2539", {"start": v(279.25, -798.25) * mm, "mid": v(280.13, -800.37) * mm, "end": v(282.25, -801.25) * mm});
            skArc(sketch, "E2540", {"start": v(228.25, -651.25) * mm, "mid": v(230.37, -650.37) * mm, "end": v(231.25, -648.25) * mm});
            skArc(sketch, "E2541", {"start": v(231.25, -648.25) * mm, "mid": v(230.37, -646.13) * mm, "end": v(228.25, -645.25) * mm});
            skArc(sketch, "E2542", {"start": v(228.25, -645.25) * mm, "mid": v(226.13, -646.13) * mm, "end": v(225.25, -648.25) * mm});
            skArc(sketch, "E2543", {"start": v(225.25, -648.25) * mm, "mid": v(226.13, -650.37) * mm, "end": v(228.25, -651.25) * mm});
            skArc(sketch, "E2544", {"start": v(282.25, -651.25) * mm, "mid": v(284.37, -650.37) * mm, "end": v(285.25, -648.25) * mm});
            skArc(sketch, "E2545", {"start": v(285.25, -648.25) * mm, "mid": v(284.37, -646.13) * mm, "end": v(282.25, -645.25) * mm});
            skArc(sketch, "E2546", {"start": v(282.25, -645.25) * mm, "mid": v(280.13, -646.13) * mm, "end": v(279.25, -648.25) * mm});
            skArc(sketch, "E2547", {"start": v(279.25, -648.25) * mm, "mid": v(280.13, -650.37) * mm, "end": v(282.25, -651.25) * mm});
            skArc(sketch, "E2548", {"start": v(228.25, -501.25) * mm, "mid": v(230.37, -500.37) * mm, "end": v(231.25, -498.25) * mm});
            skArc(sketch, "E2549", {"start": v(231.25, -498.25) * mm, "mid": v(230.37, -496.13) * mm, "end": v(228.25, -495.25) * mm});
            skArc(sketch, "E2550", {"start": v(228.25, -495.25) * mm, "mid": v(226.13, -496.13) * mm, "end": v(225.25, -498.25) * mm});
            skArc(sketch, "E2551", {"start": v(225.25, -498.25) * mm, "mid": v(226.13, -500.37) * mm, "end": v(228.25, -501.25) * mm});
            skArc(sketch, "E2552", {"start": v(282.25, -501.25) * mm, "mid": v(284.37, -500.37) * mm, "end": v(285.25, -498.25) * mm});
            skArc(sketch, "E2553", {"start": v(285.25, -498.25) * mm, "mid": v(284.37, -496.13) * mm, "end": v(282.25, -495.25) * mm});
            skArc(sketch, "E2554", {"start": v(282.25, -495.25) * mm, "mid": v(280.13, -496.13) * mm, "end": v(279.25, -498.25) * mm});
            skArc(sketch, "E2555", {"start": v(279.25, -498.25) * mm, "mid": v(280.13, -500.37) * mm, "end": v(282.25, -501.25) * mm});
            skArc(sketch, "E2556", {"start": v(228.25, -351.25) * mm, "mid": v(230.37, -350.37) * mm, "end": v(231.25, -348.25) * mm});
            skArc(sketch, "E2557", {"start": v(231.25, -348.25) * mm, "mid": v(230.37, -346.13) * mm, "end": v(228.25, -345.25) * mm});
            skArc(sketch, "E2558", {"start": v(228.25, -345.25) * mm, "mid": v(226.13, -346.13) * mm, "end": v(225.25, -348.25) * mm});
            skArc(sketch, "E2559", {"start": v(225.25, -348.25) * mm, "mid": v(226.13, -350.37) * mm, "end": v(228.25, -351.25) * mm});
            skArc(sketch, "E2560", {"start": v(282.25, -351.25) * mm, "mid": v(284.37, -350.37) * mm, "end": v(285.25, -348.25) * mm});
            skArc(sketch, "E2561", {"start": v(285.25, -348.25) * mm, "mid": v(284.37, -346.13) * mm, "end": v(282.25, -345.25) * mm});
            skArc(sketch, "E2562", {"start": v(282.25, -345.25) * mm, "mid": v(280.13, -346.13) * mm, "end": v(279.25, -348.25) * mm});
            skArc(sketch, "E2563", {"start": v(279.25, -348.25) * mm, "mid": v(280.13, -350.37) * mm, "end": v(282.25, -351.25) * mm});
            skArc(sketch, "E2564", {"start": v(228.25, -201.25) * mm, "mid": v(230.37, -200.37) * mm, "end": v(231.25, -198.25) * mm});
            skArc(sketch, "E2565", {"start": v(231.25, -198.25) * mm, "mid": v(230.37, -196.13) * mm, "end": v(228.25, -195.25) * mm});
            skArc(sketch, "E2566", {"start": v(228.25, -195.25) * mm, "mid": v(226.13, -196.13) * mm, "end": v(225.25, -198.25) * mm});
            skArc(sketch, "E2567", {"start": v(225.25, -198.25) * mm, "mid": v(226.13, -200.37) * mm, "end": v(228.25, -201.25) * mm});
            skArc(sketch, "E2568", {"start": v(282.25, -201.25) * mm, "mid": v(284.37, -200.37) * mm, "end": v(285.25, -198.25) * mm});
            skArc(sketch, "E2569", {"start": v(285.25, -198.25) * mm, "mid": v(284.37, -196.13) * mm, "end": v(282.25, -195.25) * mm});
            skArc(sketch, "E2570", {"start": v(282.25, -195.25) * mm, "mid": v(280.13, -196.13) * mm, "end": v(279.25, -198.25) * mm});
            skArc(sketch, "E2571", {"start": v(279.25, -198.25) * mm, "mid": v(280.13, -200.37) * mm, "end": v(282.25, -201.25) * mm});
            skArc(sketch, "E2572", {"start": v(228.25, -21.25) * mm, "mid": v(230.37, -20.37) * mm, "end": v(231.25, -18.25) * mm});
            skArc(sketch, "E2573", {"start": v(231.25, -18.25) * mm, "mid": v(230.37, -16.13) * mm, "end": v(228.25, -15.25) * mm});
            skArc(sketch, "E2574", {"start": v(228.25, -15.25) * mm, "mid": v(226.13, -16.13) * mm, "end": v(225.25, -18.25) * mm});
            skArc(sketch, "E2575", {"start": v(225.25, -18.25) * mm, "mid": v(226.13, -20.37) * mm, "end": v(228.25, -21.25) * mm});
            skArc(sketch, "E2576", {"start": v(282.25, -21.25) * mm, "mid": v(284.37, -20.37) * mm, "end": v(285.25, -18.25) * mm});
            skArc(sketch, "E2577", {"start": v(285.25, -18.25) * mm, "mid": v(284.37, -16.13) * mm, "end": v(282.25, -15.25) * mm});
            skArc(sketch, "E2578", {"start": v(282.25, -15.25) * mm, "mid": v(280.13, -16.13) * mm, "end": v(279.25, -18.25) * mm});
            skArc(sketch, "E2579", {"start": v(279.25, -18.25) * mm, "mid": v(280.13, -20.37) * mm, "end": v(282.25, -21.25) * mm});
            skArc(sketch, "E2580", {"start": v(228.25, 98.75) * mm, "mid": v(230.37, 99.63) * mm, "end": v(231.25, 101.75) * mm});
            skArc(sketch, "E2581", {"start": v(231.25, 101.75) * mm, "mid": v(230.37, 103.87) * mm, "end": v(228.25, 104.75) * mm});
            skArc(sketch, "E2582", {"start": v(228.25, 104.75) * mm, "mid": v(226.13, 103.87) * mm, "end": v(225.25, 101.75) * mm});
            skArc(sketch, "E2583", {"start": v(225.25, 101.75) * mm, "mid": v(226.13, 99.63) * mm, "end": v(228.25, 98.75) * mm});
            skArc(sketch, "E2584", {"start": v(282.25, 98.75) * mm, "mid": v(284.37, 99.63) * mm, "end": v(285.25, 101.75) * mm});
            skArc(sketch, "E2585", {"start": v(285.25, 101.75) * mm, "mid": v(284.37, 103.87) * mm, "end": v(282.25, 104.75) * mm});
            skArc(sketch, "E2586", {"start": v(282.25, 104.75) * mm, "mid": v(280.13, 103.87) * mm, "end": v(279.25, 101.75) * mm});
            skArc(sketch, "E2587", {"start": v(279.25, 101.75) * mm, "mid": v(280.13, 99.63) * mm, "end": v(282.25, 98.75) * mm});
            skArc(sketch, "E2588", {"start": v(228.25, 248.75) * mm, "mid": v(230.37, 249.63) * mm, "end": v(231.25, 251.75) * mm});
            skArc(sketch, "E2589", {"start": v(231.25, 251.75) * mm, "mid": v(230.37, 253.87) * mm, "end": v(228.25, 254.75) * mm});
            skArc(sketch, "E2590", {"start": v(228.25, 254.75) * mm, "mid": v(226.13, 253.87) * mm, "end": v(225.25, 251.75) * mm});
            skArc(sketch, "E2591", {"start": v(225.25, 251.75) * mm, "mid": v(226.13, 249.63) * mm, "end": v(228.25, 248.75) * mm});
            skArc(sketch, "E2592", {"start": v(282.25, 248.75) * mm, "mid": v(284.37, 249.63) * mm, "end": v(285.25, 251.75) * mm});
            skArc(sketch, "E2593", {"start": v(285.25, 251.75) * mm, "mid": v(284.37, 253.87) * mm, "end": v(282.25, 254.75) * mm});
            skArc(sketch, "E2594", {"start": v(282.25, 254.75) * mm, "mid": v(280.13, 253.87) * mm, "end": v(279.25, 251.75) * mm});
            skArc(sketch, "E2595", {"start": v(279.25, 251.75) * mm, "mid": v(280.13, 249.63) * mm, "end": v(282.25, 248.75) * mm});
            skArc(sketch, "E2596", {"start": v(228.25, 398.75) * mm, "mid": v(230.37, 399.63) * mm, "end": v(231.25, 401.75) * mm});
            skArc(sketch, "E2597", {"start": v(231.25, 401.75) * mm, "mid": v(230.37, 403.87) * mm, "end": v(228.25, 404.75) * mm});
            skArc(sketch, "E2598", {"start": v(228.25, 404.75) * mm, "mid": v(226.13, 403.87) * mm, "end": v(225.25, 401.75) * mm});
            skArc(sketch, "E2599", {"start": v(225.25, 401.75) * mm, "mid": v(226.13, 399.63) * mm, "end": v(228.25, 398.75) * mm});
            skArc(sketch, "E2600", {"start": v(282.25, 398.75) * mm, "mid": v(284.37, 399.63) * mm, "end": v(285.25, 401.75) * mm});
            skArc(sketch, "E2601", {"start": v(285.25, 401.75) * mm, "mid": v(284.37, 403.87) * mm, "end": v(282.25, 404.75) * mm});
            skArc(sketch, "E2602", {"start": v(282.25, 404.75) * mm, "mid": v(280.13, 403.87) * mm, "end": v(279.25, 401.75) * mm});
            skArc(sketch, "E2603", {"start": v(279.25, 401.75) * mm, "mid": v(280.13, 399.63) * mm, "end": v(282.25, 398.75) * mm});
            skArc(sketch, "E2604", {"start": v(228.25, 548.75) * mm, "mid": v(230.37, 549.63) * mm, "end": v(231.25, 551.75) * mm});
            skArc(sketch, "E2605", {"start": v(231.25, 551.75) * mm, "mid": v(230.37, 553.87) * mm, "end": v(228.25, 554.75) * mm});
            skArc(sketch, "E2606", {"start": v(228.25, 554.75) * mm, "mid": v(226.13, 553.87) * mm, "end": v(225.25, 551.75) * mm});
            skArc(sketch, "E2607", {"start": v(225.25, 551.75) * mm, "mid": v(226.13, 549.63) * mm, "end": v(228.25, 548.75) * mm});
            skArc(sketch, "E2608", {"start": v(282.25, 548.75) * mm, "mid": v(284.37, 549.63) * mm, "end": v(285.25, 551.75) * mm});
            skArc(sketch, "E2609", {"start": v(285.25, 551.75) * mm, "mid": v(284.37, 553.87) * mm, "end": v(282.25, 554.75) * mm});
            skArc(sketch, "E2610", {"start": v(282.25, 554.75) * mm, "mid": v(280.13, 553.87) * mm, "end": v(279.25, 551.75) * mm});
            skArc(sketch, "E2611", {"start": v(279.25, 551.75) * mm, "mid": v(280.13, 549.63) * mm, "end": v(282.25, 548.75) * mm});
            skArc(sketch, "E2612", {"start": v(228.25, 698.75) * mm, "mid": v(230.37, 699.63) * mm, "end": v(231.25, 701.75) * mm});
            skArc(sketch, "E2613", {"start": v(231.25, 701.75) * mm, "mid": v(230.37, 703.87) * mm, "end": v(228.25, 704.75) * mm});
            skArc(sketch, "E2614", {"start": v(228.25, 704.75) * mm, "mid": v(226.13, 703.87) * mm, "end": v(225.25, 701.75) * mm});
            skArc(sketch, "E2615", {"start": v(225.25, 701.75) * mm, "mid": v(226.13, 699.63) * mm, "end": v(228.25, 698.75) * mm});
            skArc(sketch, "E2616", {"start": v(282.25, 698.75) * mm, "mid": v(284.37, 699.63) * mm, "end": v(285.25, 701.75) * mm});
            skArc(sketch, "E2617", {"start": v(285.25, 701.75) * mm, "mid": v(284.37, 703.87) * mm, "end": v(282.25, 704.75) * mm});
            skArc(sketch, "E2618", {"start": v(282.25, 704.75) * mm, "mid": v(280.13, 703.87) * mm, "end": v(279.25, 701.75) * mm});
            skArc(sketch, "E2619", {"start": v(279.25, 701.75) * mm, "mid": v(280.13, 699.63) * mm, "end": v(282.25, 698.75) * mm});
            skArc(sketch, "E2620", {"start": v(228.25, -81.24) * mm, "mid": v(230.37, -80.36) * mm, "end": v(231.25, -78.24) * mm});
            skArc(sketch, "E2621", {"start": v(231.25, -78.24) * mm, "mid": v(230.37, -76.12) * mm, "end": v(228.25, -75.24) * mm});
            skArc(sketch, "E2622", {"start": v(228.25, -75.24) * mm, "mid": v(226.13, -76.12) * mm, "end": v(225.25, -78.24) * mm});
            skArc(sketch, "E2623", {"start": v(225.25, -78.24) * mm, "mid": v(226.13, -80.36) * mm, "end": v(228.25, -81.24) * mm});
            skArc(sketch, "E2624", {"start": v(282.25, -81.24) * mm, "mid": v(284.37, -80.36) * mm, "end": v(285.25, -78.24) * mm});
            skArc(sketch, "E2625", {"start": v(285.25, -78.24) * mm, "mid": v(284.37, -76.12) * mm, "end": v(282.25, -75.24) * mm});
            skArc(sketch, "E2626", {"start": v(282.25, -75.24) * mm, "mid": v(280.13, -76.12) * mm, "end": v(279.25, -78.24) * mm});
            skArc(sketch, "E2627", {"start": v(279.25, -78.24) * mm, "mid": v(280.13, -80.36) * mm, "end": v(282.25, -81.24) * mm});
            skArc(sketch, "E2628", {"start": v(-11.25, -951.25) * mm, "mid": v(-9.13, -950.37) * mm, "end": v(-8.25, -948.25) * mm});
            skArc(sketch, "E2629", {"start": v(-8.25, -948.25) * mm, "mid": v(-9.13, -946.13) * mm, "end": v(-11.25, -945.25) * mm});
            skArc(sketch, "E2630", {"start": v(-11.25, -945.25) * mm, "mid": v(-13.37, -946.13) * mm, "end": v(-14.25, -948.25) * mm});
            skArc(sketch, "E2631", {"start": v(-14.25, -948.25) * mm, "mid": v(-13.37, -950.37) * mm, "end": v(-11.25, -951.25) * mm});
            skArc(sketch, "E2632", {"start": v(42.75, -951.25) * mm, "mid": v(44.87, -950.37) * mm, "end": v(45.75, -948.25) * mm});
            skArc(sketch, "E2633", {"start": v(45.75, -948.25) * mm, "mid": v(44.87, -946.13) * mm, "end": v(42.75, -945.25) * mm});
            skArc(sketch, "E2634", {"start": v(42.75, -945.25) * mm, "mid": v(40.63, -946.13) * mm, "end": v(39.75, -948.25) * mm});
            skArc(sketch, "E2635", {"start": v(39.75, -948.25) * mm, "mid": v(40.63, -950.37) * mm, "end": v(42.75, -951.25) * mm});
            skArc(sketch, "E2636", {"start": v(-11.25, -1101.25) * mm, "mid": v(-9.13, -1100.37) * mm, "end": v(-8.25, -1098.25) * mm});
            skArc(sketch, "E2637", {"start": v(-8.25, -1098.25) * mm, "mid": v(-9.13, -1096.13) * mm, "end": v(-11.25, -1095.25) * mm});
            skArc(sketch, "E2638", {"start": v(-11.25, -1095.25) * mm, "mid": v(-13.37, -1096.13) * mm, "end": v(-14.25, -1098.25) * mm});
            skArc(sketch, "E2639", {"start": v(-14.25, -1098.25) * mm, "mid": v(-13.37, -1100.37) * mm, "end": v(-11.25, -1101.25) * mm});
            skArc(sketch, "E2640", {"start": v(42.75, -1101.25) * mm, "mid": v(44.87, -1100.37) * mm, "end": v(45.75, -1098.25) * mm});
            skArc(sketch, "E2641", {"start": v(45.75, -1098.25) * mm, "mid": v(44.87, -1096.13) * mm, "end": v(42.75, -1095.25) * mm});
            skArc(sketch, "E2642", {"start": v(42.75, -1095.25) * mm, "mid": v(40.63, -1096.13) * mm, "end": v(39.75, -1098.25) * mm});
            skArc(sketch, "E2643", {"start": v(39.75, -1098.25) * mm, "mid": v(40.63, -1100.37) * mm, "end": v(42.75, -1101.25) * mm});
            skArc(sketch, "E2644", {"start": v(-11.25, -801.25) * mm, "mid": v(-9.13, -800.37) * mm, "end": v(-8.25, -798.25) * mm});
            skArc(sketch, "E2645", {"start": v(-8.25, -798.25) * mm, "mid": v(-9.13, -796.13) * mm, "end": v(-11.25, -795.25) * mm});
            skArc(sketch, "E2646", {"start": v(-11.25, -795.25) * mm, "mid": v(-13.37, -796.13) * mm, "end": v(-14.25, -798.25) * mm});
            skArc(sketch, "E2647", {"start": v(-14.25, -798.25) * mm, "mid": v(-13.37, -800.37) * mm, "end": v(-11.25, -801.25) * mm});
            skArc(sketch, "E2648", {"start": v(42.75, -801.25) * mm, "mid": v(44.87, -800.37) * mm, "end": v(45.75, -798.25) * mm});
            skArc(sketch, "E2649", {"start": v(45.75, -798.25) * mm, "mid": v(44.87, -796.13) * mm, "end": v(42.75, -795.25) * mm});
            skArc(sketch, "E2650", {"start": v(42.75, -795.25) * mm, "mid": v(40.63, -796.13) * mm, "end": v(39.75, -798.25) * mm});
            skArc(sketch, "E2651", {"start": v(39.75, -798.25) * mm, "mid": v(40.63, -800.37) * mm, "end": v(42.75, -801.25) * mm});
            skArc(sketch, "E2652", {"start": v(-11.25, -651.25) * mm, "mid": v(-9.13, -650.37) * mm, "end": v(-8.25, -648.25) * mm});
            skArc(sketch, "E2653", {"start": v(-8.25, -648.25) * mm, "mid": v(-9.13, -646.13) * mm, "end": v(-11.25, -645.25) * mm});
            skArc(sketch, "E2654", {"start": v(-11.25, -645.25) * mm, "mid": v(-13.37, -646.13) * mm, "end": v(-14.25, -648.25) * mm});
            skArc(sketch, "E2655", {"start": v(-14.25, -648.25) * mm, "mid": v(-13.37, -650.37) * mm, "end": v(-11.25, -651.25) * mm});
            skArc(sketch, "E2656", {"start": v(42.75, -651.25) * mm, "mid": v(44.87, -650.37) * mm, "end": v(45.75, -648.25) * mm});
            skArc(sketch, "E2657", {"start": v(45.75, -648.25) * mm, "mid": v(44.87, -646.13) * mm, "end": v(42.75, -645.25) * mm});
            skArc(sketch, "E2658", {"start": v(42.75, -645.25) * mm, "mid": v(40.63, -646.13) * mm, "end": v(39.75, -648.25) * mm});
            skArc(sketch, "E2659", {"start": v(39.75, -648.25) * mm, "mid": v(40.63, -650.37) * mm, "end": v(42.75, -651.25) * mm});
            skArc(sketch, "E2660", {"start": v(-11.25, -501.25) * mm, "mid": v(-9.13, -500.37) * mm, "end": v(-8.25, -498.25) * mm});
            skArc(sketch, "E2661", {"start": v(-8.25, -498.25) * mm, "mid": v(-9.13, -496.13) * mm, "end": v(-11.25, -495.25) * mm});
            skArc(sketch, "E2662", {"start": v(-11.25, -495.25) * mm, "mid": v(-13.37, -496.13) * mm, "end": v(-14.25, -498.25) * mm});
            skArc(sketch, "E2663", {"start": v(-14.25, -498.25) * mm, "mid": v(-13.37, -500.37) * mm, "end": v(-11.25, -501.25) * mm});
            skArc(sketch, "E2664", {"start": v(42.75, -501.25) * mm, "mid": v(44.87, -500.37) * mm, "end": v(45.75, -498.25) * mm});
            skArc(sketch, "E2665", {"start": v(45.75, -498.25) * mm, "mid": v(44.87, -496.13) * mm, "end": v(42.75, -495.25) * mm});
            skArc(sketch, "E2666", {"start": v(42.75, -495.25) * mm, "mid": v(40.63, -496.13) * mm, "end": v(39.75, -498.25) * mm});
            skArc(sketch, "E2667", {"start": v(39.75, -498.25) * mm, "mid": v(40.63, -500.37) * mm, "end": v(42.75, -501.25) * mm});
            skArc(sketch, "E2668", {"start": v(-11.25, -351.25) * mm, "mid": v(-9.13, -350.37) * mm, "end": v(-8.25, -348.25) * mm});
            skArc(sketch, "E2669", {"start": v(-8.25, -348.25) * mm, "mid": v(-9.13, -346.13) * mm, "end": v(-11.25, -345.25) * mm});
            skArc(sketch, "E2670", {"start": v(-11.25, -345.25) * mm, "mid": v(-13.37, -346.13) * mm, "end": v(-14.25, -348.25) * mm});
            skArc(sketch, "E2671", {"start": v(-14.25, -348.25) * mm, "mid": v(-13.37, -350.37) * mm, "end": v(-11.25, -351.25) * mm});
            skArc(sketch, "E2672", {"start": v(42.75, -351.25) * mm, "mid": v(44.87, -350.37) * mm, "end": v(45.75, -348.25) * mm});
            skArc(sketch, "E2673", {"start": v(45.75, -348.25) * mm, "mid": v(44.87, -346.13) * mm, "end": v(42.75, -345.25) * mm});
            skArc(sketch, "E2674", {"start": v(42.75, -345.25) * mm, "mid": v(40.63, -346.13) * mm, "end": v(39.75, -348.25) * mm});
            skArc(sketch, "E2675", {"start": v(39.75, -348.25) * mm, "mid": v(40.63, -350.37) * mm, "end": v(42.75, -351.25) * mm});
            skArc(sketch, "E2676", {"start": v(-11.25, -201.25) * mm, "mid": v(-9.13, -200.37) * mm, "end": v(-8.25, -198.25) * mm});
            skArc(sketch, "E2677", {"start": v(-8.25, -198.25) * mm, "mid": v(-9.13, -196.13) * mm, "end": v(-11.25, -195.25) * mm});
            skArc(sketch, "E2678", {"start": v(-11.25, -195.25) * mm, "mid": v(-13.37, -196.13) * mm, "end": v(-14.25, -198.25) * mm});
            skArc(sketch, "E2679", {"start": v(-14.25, -198.25) * mm, "mid": v(-13.37, -200.37) * mm, "end": v(-11.25, -201.25) * mm});
            skArc(sketch, "E2680", {"start": v(42.75, -201.25) * mm, "mid": v(44.87, -200.37) * mm, "end": v(45.75, -198.25) * mm});
            skArc(sketch, "E2681", {"start": v(45.75, -198.25) * mm, "mid": v(44.87, -196.13) * mm, "end": v(42.75, -195.25) * mm});
            skArc(sketch, "E2682", {"start": v(42.75, -195.25) * mm, "mid": v(40.63, -196.13) * mm, "end": v(39.75, -198.25) * mm});
            skArc(sketch, "E2683", {"start": v(39.75, -198.25) * mm, "mid": v(40.63, -200.37) * mm, "end": v(42.75, -201.25) * mm});
            skArc(sketch, "E2684", {"start": v(-11.25, -21.25) * mm, "mid": v(-9.13, -20.37) * mm, "end": v(-8.25, -18.25) * mm});
            skArc(sketch, "E2685", {"start": v(-8.25, -18.25) * mm, "mid": v(-9.13, -16.13) * mm, "end": v(-11.25, -15.25) * mm});
            skArc(sketch, "E2686", {"start": v(-11.25, -15.25) * mm, "mid": v(-13.37, -16.13) * mm, "end": v(-14.25, -18.25) * mm});
            skArc(sketch, "E2687", {"start": v(-14.25, -18.25) * mm, "mid": v(-13.37, -20.37) * mm, "end": v(-11.25, -21.25) * mm});
            skArc(sketch, "E2688", {"start": v(42.75, -21.25) * mm, "mid": v(44.87, -20.37) * mm, "end": v(45.75, -18.25) * mm});
            skArc(sketch, "E2689", {"start": v(45.75, -18.25) * mm, "mid": v(44.87, -16.13) * mm, "end": v(42.75, -15.25) * mm});
            skArc(sketch, "E2690", {"start": v(42.75, -15.25) * mm, "mid": v(40.63, -16.13) * mm, "end": v(39.75, -18.25) * mm});
            skArc(sketch, "E2691", {"start": v(39.75, -18.25) * mm, "mid": v(40.63, -20.37) * mm, "end": v(42.75, -21.25) * mm});
            skArc(sketch, "E2692", {"start": v(-11.25, 98.75) * mm, "mid": v(-9.13, 99.63) * mm, "end": v(-8.25, 101.75) * mm});
            skArc(sketch, "E2693", {"start": v(-8.25, 101.75) * mm, "mid": v(-9.13, 103.87) * mm, "end": v(-11.25, 104.75) * mm});
            skArc(sketch, "E2694", {"start": v(-11.25, 104.75) * mm, "mid": v(-13.37, 103.87) * mm, "end": v(-14.25, 101.75) * mm});
            skArc(sketch, "E2695", {"start": v(-14.25, 101.75) * mm, "mid": v(-13.37, 99.63) * mm, "end": v(-11.25, 98.75) * mm});
            skArc(sketch, "E2696", {"start": v(42.75, 98.75) * mm, "mid": v(44.87, 99.63) * mm, "end": v(45.75, 101.75) * mm});
            skArc(sketch, "E2697", {"start": v(45.75, 101.75) * mm, "mid": v(44.87, 103.87) * mm, "end": v(42.75, 104.75) * mm});
            skArc(sketch, "E2698", {"start": v(42.75, 104.75) * mm, "mid": v(40.63, 103.87) * mm, "end": v(39.75, 101.75) * mm});
            skArc(sketch, "E2699", {"start": v(39.75, 101.75) * mm, "mid": v(40.63, 99.63) * mm, "end": v(42.75, 98.75) * mm});
            skArc(sketch, "E2700", {"start": v(-11.25, 248.75) * mm, "mid": v(-9.13, 249.63) * mm, "end": v(-8.25, 251.75) * mm});
            skArc(sketch, "E2701", {"start": v(-8.25, 251.75) * mm, "mid": v(-9.13, 253.87) * mm, "end": v(-11.25, 254.75) * mm});
            skArc(sketch, "E2702", {"start": v(-11.25, 254.75) * mm, "mid": v(-13.37, 253.87) * mm, "end": v(-14.25, 251.75) * mm});
            skArc(sketch, "E2703", {"start": v(-14.25, 251.75) * mm, "mid": v(-13.37, 249.63) * mm, "end": v(-11.25, 248.75) * mm});
            skArc(sketch, "E2704", {"start": v(42.75, 248.75) * mm, "mid": v(44.87, 249.63) * mm, "end": v(45.75, 251.75) * mm});
            skArc(sketch, "E2705", {"start": v(45.75, 251.75) * mm, "mid": v(44.87, 253.87) * mm, "end": v(42.75, 254.75) * mm});
            skArc(sketch, "E2706", {"start": v(42.75, 254.75) * mm, "mid": v(40.63, 253.87) * mm, "end": v(39.75, 251.75) * mm});
            skArc(sketch, "E2707", {"start": v(39.75, 251.75) * mm, "mid": v(40.63, 249.63) * mm, "end": v(42.75, 248.75) * mm});
            skArc(sketch, "E2708", {"start": v(-11.25, 398.75) * mm, "mid": v(-9.13, 399.63) * mm, "end": v(-8.25, 401.75) * mm});
            skArc(sketch, "E2709", {"start": v(-8.25, 401.75) * mm, "mid": v(-9.13, 403.87) * mm, "end": v(-11.25, 404.75) * mm});
            skArc(sketch, "E2710", {"start": v(-11.25, 404.75) * mm, "mid": v(-13.37, 403.87) * mm, "end": v(-14.25, 401.75) * mm});
            skArc(sketch, "E2711", {"start": v(-14.25, 401.75) * mm, "mid": v(-13.37, 399.63) * mm, "end": v(-11.25, 398.75) * mm});
            skArc(sketch, "E2712", {"start": v(42.75, 398.75) * mm, "mid": v(44.87, 399.63) * mm, "end": v(45.75, 401.75) * mm});
            skArc(sketch, "E2713", {"start": v(45.75, 401.75) * mm, "mid": v(44.87, 403.87) * mm, "end": v(42.75, 404.75) * mm});
            skArc(sketch, "E2714", {"start": v(42.75, 404.75) * mm, "mid": v(40.63, 403.87) * mm, "end": v(39.75, 401.75) * mm});
            skArc(sketch, "E2715", {"start": v(39.75, 401.75) * mm, "mid": v(40.63, 399.63) * mm, "end": v(42.75, 398.75) * mm});
            skArc(sketch, "E2716", {"start": v(-11.25, 548.75) * mm, "mid": v(-9.13, 549.63) * mm, "end": v(-8.25, 551.75) * mm});
            skArc(sketch, "E2717", {"start": v(-8.25, 551.75) * mm, "mid": v(-9.13, 553.87) * mm, "end": v(-11.25, 554.75) * mm});
            skArc(sketch, "E2718", {"start": v(-11.25, 554.75) * mm, "mid": v(-13.37, 553.87) * mm, "end": v(-14.25, 551.75) * mm});
            skArc(sketch, "E2719", {"start": v(-14.25, 551.75) * mm, "mid": v(-13.37, 549.63) * mm, "end": v(-11.25, 548.75) * mm});
            skArc(sketch, "E2720", {"start": v(42.75, 548.75) * mm, "mid": v(44.87, 549.63) * mm, "end": v(45.75, 551.75) * mm});
            skArc(sketch, "E2721", {"start": v(45.75, 551.75) * mm, "mid": v(44.87, 553.87) * mm, "end": v(42.75, 554.75) * mm});
            skArc(sketch, "E2722", {"start": v(42.75, 554.75) * mm, "mid": v(40.63, 553.87) * mm, "end": v(39.75, 551.75) * mm});
            skArc(sketch, "E2723", {"start": v(39.75, 551.75) * mm, "mid": v(40.63, 549.63) * mm, "end": v(42.75, 548.75) * mm});
            skArc(sketch, "E2724", {"start": v(-11.25, 698.75) * mm, "mid": v(-9.13, 699.63) * mm, "end": v(-8.25, 701.75) * mm});
            skArc(sketch, "E2725", {"start": v(-8.25, 701.75) * mm, "mid": v(-9.13, 703.87) * mm, "end": v(-11.25, 704.75) * mm});
            skArc(sketch, "E2726", {"start": v(-11.25, 704.75) * mm, "mid": v(-13.37, 703.87) * mm, "end": v(-14.25, 701.75) * mm});
            skArc(sketch, "E2727", {"start": v(-14.25, 701.75) * mm, "mid": v(-13.37, 699.63) * mm, "end": v(-11.25, 698.75) * mm});
            skArc(sketch, "E2728", {"start": v(42.75, 698.75) * mm, "mid": v(44.87, 699.63) * mm, "end": v(45.75, 701.75) * mm});
            skArc(sketch, "E2729", {"start": v(45.75, 701.75) * mm, "mid": v(44.87, 703.87) * mm, "end": v(42.75, 704.75) * mm});
            skArc(sketch, "E2730", {"start": v(42.75, 704.75) * mm, "mid": v(40.63, 703.87) * mm, "end": v(39.75, 701.75) * mm});
            skArc(sketch, "E2731", {"start": v(39.75, 701.75) * mm, "mid": v(40.63, 699.63) * mm, "end": v(42.75, 698.75) * mm});
            skArc(sketch, "E2732", {"start": v(-11.25, -81.24) * mm, "mid": v(-9.13, -80.36) * mm, "end": v(-8.25, -78.24) * mm});
            skArc(sketch, "E2733", {"start": v(-8.25, -78.24) * mm, "mid": v(-9.13, -76.12) * mm, "end": v(-11.25, -75.24) * mm});
            skArc(sketch, "E2734", {"start": v(-11.25, -75.24) * mm, "mid": v(-13.37, -76.12) * mm, "end": v(-14.25, -78.24) * mm});
            skArc(sketch, "E2735", {"start": v(-14.25, -78.24) * mm, "mid": v(-13.37, -80.36) * mm, "end": v(-11.25, -81.24) * mm});
            skArc(sketch, "E2736", {"start": v(42.75, -81.24) * mm, "mid": v(44.87, -80.36) * mm, "end": v(45.75, -78.24) * mm});
            skArc(sketch, "E2737", {"start": v(45.75, -78.24) * mm, "mid": v(44.87, -76.12) * mm, "end": v(42.75, -75.24) * mm});
            skArc(sketch, "E2738", {"start": v(42.75, -75.24) * mm, "mid": v(40.63, -76.12) * mm, "end": v(39.75, -78.24) * mm});
            skArc(sketch, "E2739", {"start": v(39.75, -78.24) * mm, "mid": v(40.63, -80.36) * mm, "end": v(42.75, -81.24) * mm});
            skArc(sketch, "E2740", {"start": v(-494, -948) * mm, "mid": v(-493.12, -950.12) * mm, "end": v(-491, -951) * mm});
            skArc(sketch, "E2741", {"start": v(-491, -951) * mm, "mid": v(-488.88, -950.12) * mm, "end": v(-488, -948) * mm});
            skArc(sketch, "E2742", {"start": v(-488, -948) * mm, "mid": v(-488.88, -945.88) * mm, "end": v(-491, -945) * mm});
            skArc(sketch, "E2743", {"start": v(-491, -945) * mm, "mid": v(-493.12, -945.88) * mm, "end": v(-494, -948) * mm});
            skArc(sketch, "E2744", {"start": v(-440, -948) * mm, "mid": v(-439.12, -950.12) * mm, "end": v(-437, -951) * mm});
            skArc(sketch, "E2745", {"start": v(-437, -951) * mm, "mid": v(-434.88, -950.12) * mm, "end": v(-434, -948) * mm});
            skArc(sketch, "E2746", {"start": v(-434, -948) * mm, "mid": v(-434.88, -945.88) * mm, "end": v(-437, -945) * mm});
            skArc(sketch, "E2747", {"start": v(-437, -945) * mm, "mid": v(-439.12, -945.88) * mm, "end": v(-440, -948) * mm});
            skArc(sketch, "E2748", {"start": v(-494, -1098) * mm, "mid": v(-493.12, -1100.12) * mm, "end": v(-491, -1101) * mm});
            skArc(sketch, "E2749", {"start": v(-491, -1101) * mm, "mid": v(-488.88, -1100.12) * mm, "end": v(-488, -1098) * mm});
            skArc(sketch, "E2750", {"start": v(-488, -1098) * mm, "mid": v(-488.88, -1095.88) * mm, "end": v(-491, -1095) * mm});
            skArc(sketch, "E2751", {"start": v(-491, -1095) * mm, "mid": v(-493.12, -1095.88) * mm, "end": v(-494, -1098) * mm});
            skArc(sketch, "E2752", {"start": v(-440, -1098) * mm, "mid": v(-439.12, -1100.12) * mm, "end": v(-437, -1101) * mm});
            skArc(sketch, "E2753", {"start": v(-437, -1101) * mm, "mid": v(-434.88, -1100.12) * mm, "end": v(-434, -1098) * mm});
            skArc(sketch, "E2754", {"start": v(-434, -1098) * mm, "mid": v(-434.88, -1095.88) * mm, "end": v(-437, -1095) * mm});
            skArc(sketch, "E2755", {"start": v(-437, -1095) * mm, "mid": v(-439.12, -1095.88) * mm, "end": v(-440, -1098) * mm});
            skArc(sketch, "E2756", {"start": v(-494, -798) * mm, "mid": v(-493.12, -800.12) * mm, "end": v(-491, -801) * mm});
            skArc(sketch, "E2757", {"start": v(-491, -801) * mm, "mid": v(-488.88, -800.12) * mm, "end": v(-488, -798) * mm});
            skArc(sketch, "E2758", {"start": v(-488, -798) * mm, "mid": v(-488.88, -795.88) * mm, "end": v(-491, -795) * mm});
            skArc(sketch, "E2759", {"start": v(-491, -795) * mm, "mid": v(-493.12, -795.88) * mm, "end": v(-494, -798) * mm});
            skArc(sketch, "E2760", {"start": v(-440, -798) * mm, "mid": v(-439.12, -800.12) * mm, "end": v(-437, -801) * mm});
            skArc(sketch, "E2761", {"start": v(-437, -801) * mm, "mid": v(-434.88, -800.12) * mm, "end": v(-434, -798) * mm});
            skArc(sketch, "E2762", {"start": v(-434, -798) * mm, "mid": v(-434.88, -795.88) * mm, "end": v(-437, -795) * mm});
            skArc(sketch, "E2763", {"start": v(-437, -795) * mm, "mid": v(-439.12, -795.88) * mm, "end": v(-440, -798) * mm});
            skArc(sketch, "E2764", {"start": v(-494, -648) * mm, "mid": v(-493.12, -650.12) * mm, "end": v(-491, -651) * mm});
            skArc(sketch, "E2765", {"start": v(-491, -651) * mm, "mid": v(-488.88, -650.12) * mm, "end": v(-488, -648) * mm});
            skArc(sketch, "E2766", {"start": v(-488, -648) * mm, "mid": v(-488.88, -645.88) * mm, "end": v(-491, -645) * mm});
            skArc(sketch, "E2767", {"start": v(-491, -645) * mm, "mid": v(-493.12, -645.88) * mm, "end": v(-494, -648) * mm});
            skArc(sketch, "E2768", {"start": v(-440, -648) * mm, "mid": v(-439.12, -650.12) * mm, "end": v(-437, -651) * mm});
            skArc(sketch, "E2769", {"start": v(-437, -651) * mm, "mid": v(-434.88, -650.12) * mm, "end": v(-434, -648) * mm});
            skArc(sketch, "E2770", {"start": v(-434, -648) * mm, "mid": v(-434.88, -645.88) * mm, "end": v(-437, -645) * mm});
            skArc(sketch, "E2771", {"start": v(-437, -645) * mm, "mid": v(-439.12, -645.88) * mm, "end": v(-440, -648) * mm});
            skArc(sketch, "E2772", {"start": v(-494, -498) * mm, "mid": v(-493.12, -500.12) * mm, "end": v(-491, -501) * mm});
            skArc(sketch, "E2773", {"start": v(-491, -501) * mm, "mid": v(-488.88, -500.12) * mm, "end": v(-488, -498) * mm});
            skArc(sketch, "E2774", {"start": v(-488, -498) * mm, "mid": v(-488.88, -495.88) * mm, "end": v(-491, -495) * mm});
            skArc(sketch, "E2775", {"start": v(-491, -495) * mm, "mid": v(-493.12, -495.88) * mm, "end": v(-494, -498) * mm});
            skArc(sketch, "E2776", {"start": v(-440, -498) * mm, "mid": v(-439.12, -500.12) * mm, "end": v(-437, -501) * mm});
            skArc(sketch, "E2777", {"start": v(-437, -501) * mm, "mid": v(-434.88, -500.12) * mm, "end": v(-434, -498) * mm});
            skArc(sketch, "E2778", {"start": v(-434, -498) * mm, "mid": v(-434.88, -495.88) * mm, "end": v(-437, -495) * mm});
            skArc(sketch, "E2779", {"start": v(-437, -495) * mm, "mid": v(-439.12, -495.88) * mm, "end": v(-440, -498) * mm});
            skArc(sketch, "E2780", {"start": v(-494, -348) * mm, "mid": v(-493.12, -350.12) * mm, "end": v(-491, -351) * mm});
            skArc(sketch, "E2781", {"start": v(-491, -351) * mm, "mid": v(-488.88, -350.12) * mm, "end": v(-488, -348) * mm});
            skArc(sketch, "E2782", {"start": v(-488, -348) * mm, "mid": v(-488.88, -345.88) * mm, "end": v(-491, -345) * mm});
            skArc(sketch, "E2783", {"start": v(-491, -345) * mm, "mid": v(-493.12, -345.88) * mm, "end": v(-494, -348) * mm});
            skArc(sketch, "E2784", {"start": v(-440, -348) * mm, "mid": v(-439.12, -350.12) * mm, "end": v(-437, -351) * mm});
            skArc(sketch, "E2785", {"start": v(-437, -351) * mm, "mid": v(-434.88, -350.12) * mm, "end": v(-434, -348) * mm});
            skArc(sketch, "E2786", {"start": v(-434, -348) * mm, "mid": v(-434.88, -345.88) * mm, "end": v(-437, -345) * mm});
            skArc(sketch, "E2787", {"start": v(-437, -345) * mm, "mid": v(-439.12, -345.88) * mm, "end": v(-440, -348) * mm});
            skArc(sketch, "E2788", {"start": v(-494, -198) * mm, "mid": v(-493.12, -200.12) * mm, "end": v(-491, -201) * mm});
            skArc(sketch, "E2789", {"start": v(-491, -201) * mm, "mid": v(-488.88, -200.12) * mm, "end": v(-488, -198) * mm});
            skArc(sketch, "E2790", {"start": v(-488, -198) * mm, "mid": v(-488.88, -195.88) * mm, "end": v(-491, -195) * mm});
            skArc(sketch, "E2791", {"start": v(-491, -195) * mm, "mid": v(-493.12, -195.88) * mm, "end": v(-494, -198) * mm});
            skArc(sketch, "E2792", {"start": v(-440, -198) * mm, "mid": v(-439.12, -200.12) * mm, "end": v(-437, -201) * mm});
            skArc(sketch, "E2793", {"start": v(-437, -201) * mm, "mid": v(-434.88, -200.12) * mm, "end": v(-434, -198) * mm});
            skArc(sketch, "E2794", {"start": v(-434, -198) * mm, "mid": v(-434.88, -195.88) * mm, "end": v(-437, -195) * mm});
            skArc(sketch, "E2795", {"start": v(-437, -195) * mm, "mid": v(-439.12, -195.88) * mm, "end": v(-440, -198) * mm});
            skArc(sketch, "E2796", {"start": v(-494, -18) * mm, "mid": v(-493.12, -20.12) * mm, "end": v(-491, -21) * mm});
            skArc(sketch, "E2797", {"start": v(-491, -21) * mm, "mid": v(-488.88, -20.12) * mm, "end": v(-488, -18) * mm});
            skArc(sketch, "E2798", {"start": v(-488, -18) * mm, "mid": v(-488.88, -15.88) * mm, "end": v(-491, -15) * mm});
            skArc(sketch, "E2799", {"start": v(-491, -15) * mm, "mid": v(-493.12, -15.88) * mm, "end": v(-494, -18) * mm});
            skArc(sketch, "E2800", {"start": v(-440, -18) * mm, "mid": v(-439.12, -20.12) * mm, "end": v(-437, -21) * mm});
            skArc(sketch, "E2801", {"start": v(-437, -21) * mm, "mid": v(-434.88, -20.12) * mm, "end": v(-434, -18) * mm});
            skArc(sketch, "E2802", {"start": v(-434, -18) * mm, "mid": v(-434.88, -15.88) * mm, "end": v(-437, -15) * mm});
            skArc(sketch, "E2803", {"start": v(-437, -15) * mm, "mid": v(-439.12, -15.88) * mm, "end": v(-440, -18) * mm});
            skArc(sketch, "E2804", {"start": v(-494, 102) * mm, "mid": v(-493.12, 99.88) * mm, "end": v(-491, 99) * mm});
            skArc(sketch, "E2805", {"start": v(-491, 99) * mm, "mid": v(-488.88, 99.88) * mm, "end": v(-488, 102) * mm});
            skArc(sketch, "E2806", {"start": v(-488, 102) * mm, "mid": v(-488.88, 104.12) * mm, "end": v(-491, 105) * mm});
            skArc(sketch, "E2807", {"start": v(-491, 105) * mm, "mid": v(-493.12, 104.12) * mm, "end": v(-494, 102) * mm});
            skArc(sketch, "E2808", {"start": v(-440, 102) * mm, "mid": v(-439.12, 99.88) * mm, "end": v(-437, 99) * mm});
            skArc(sketch, "E2809", {"start": v(-437, 99) * mm, "mid": v(-434.88, 99.88) * mm, "end": v(-434, 102) * mm});
            skArc(sketch, "E2810", {"start": v(-434, 102) * mm, "mid": v(-434.88, 104.12) * mm, "end": v(-437, 105) * mm});
            skArc(sketch, "E2811", {"start": v(-437, 105) * mm, "mid": v(-439.12, 104.12) * mm, "end": v(-440, 102) * mm});
            skArc(sketch, "E2812", {"start": v(-494, 252) * mm, "mid": v(-493.12, 249.88) * mm, "end": v(-491, 249) * mm});
            skArc(sketch, "E2813", {"start": v(-491, 249) * mm, "mid": v(-488.88, 249.88) * mm, "end": v(-488, 252) * mm});
            skArc(sketch, "E2814", {"start": v(-488, 252) * mm, "mid": v(-488.88, 254.12) * mm, "end": v(-491, 255) * mm});
            skArc(sketch, "E2815", {"start": v(-491, 255) * mm, "mid": v(-493.12, 254.12) * mm, "end": v(-494, 252) * mm});
            skArc(sketch, "E2816", {"start": v(-440, 252) * mm, "mid": v(-439.12, 249.88) * mm, "end": v(-437, 249) * mm});
            skArc(sketch, "E2817", {"start": v(-437, 249) * mm, "mid": v(-434.88, 249.88) * mm, "end": v(-434, 252) * mm});
            skArc(sketch, "E2818", {"start": v(-434, 252) * mm, "mid": v(-434.88, 254.12) * mm, "end": v(-437, 255) * mm});
            skArc(sketch, "E2819", {"start": v(-437, 255) * mm, "mid": v(-439.12, 254.12) * mm, "end": v(-440, 252) * mm});
            skArc(sketch, "E2820", {"start": v(-494, 402) * mm, "mid": v(-493.12, 399.88) * mm, "end": v(-491, 399) * mm});
            skArc(sketch, "E2821", {"start": v(-491, 399) * mm, "mid": v(-488.88, 399.88) * mm, "end": v(-488, 402) * mm});
            skArc(sketch, "E2822", {"start": v(-488, 402) * mm, "mid": v(-488.88, 404.12) * mm, "end": v(-491, 405) * mm});
            skArc(sketch, "E2823", {"start": v(-491, 405) * mm, "mid": v(-493.12, 404.12) * mm, "end": v(-494, 402) * mm});
            skArc(sketch, "E2824", {"start": v(-440, 402) * mm, "mid": v(-439.12, 399.88) * mm, "end": v(-437, 399) * mm});
            skArc(sketch, "E2825", {"start": v(-437, 399) * mm, "mid": v(-434.88, 399.88) * mm, "end": v(-434, 402) * mm});
            skArc(sketch, "E2826", {"start": v(-434, 402) * mm, "mid": v(-434.88, 404.12) * mm, "end": v(-437, 405) * mm});
            skArc(sketch, "E2827", {"start": v(-437, 405) * mm, "mid": v(-439.12, 404.12) * mm, "end": v(-440, 402) * mm});
            skArc(sketch, "E2828", {"start": v(-494, 552) * mm, "mid": v(-493.12, 549.88) * mm, "end": v(-491, 549) * mm});
            skArc(sketch, "E2829", {"start": v(-491, 549) * mm, "mid": v(-488.88, 549.88) * mm, "end": v(-488, 552) * mm});
            skArc(sketch, "E2830", {"start": v(-488, 552) * mm, "mid": v(-488.88, 554.12) * mm, "end": v(-491, 555) * mm});
            skArc(sketch, "E2831", {"start": v(-491, 555) * mm, "mid": v(-493.12, 554.12) * mm, "end": v(-494, 552) * mm});
            skArc(sketch, "E2832", {"start": v(-440, 552) * mm, "mid": v(-439.12, 549.88) * mm, "end": v(-437, 549) * mm});
            skArc(sketch, "E2833", {"start": v(-437, 549) * mm, "mid": v(-434.88, 549.88) * mm, "end": v(-434, 552) * mm});
            skArc(sketch, "E2834", {"start": v(-434, 552) * mm, "mid": v(-434.88, 554.12) * mm, "end": v(-437, 555) * mm});
            skArc(sketch, "E2835", {"start": v(-437, 555) * mm, "mid": v(-439.12, 554.12) * mm, "end": v(-440, 552) * mm});
            skArc(sketch, "E2836", {"start": v(-494, 702) * mm, "mid": v(-493.12, 699.88) * mm, "end": v(-491, 699) * mm});
            skArc(sketch, "E2837", {"start": v(-491, 699) * mm, "mid": v(-488.88, 699.88) * mm, "end": v(-488, 702) * mm});
            skArc(sketch, "E2838", {"start": v(-488, 702) * mm, "mid": v(-488.88, 704.12) * mm, "end": v(-491, 705) * mm});
            skArc(sketch, "E2839", {"start": v(-491, 705) * mm, "mid": v(-493.12, 704.12) * mm, "end": v(-494, 702) * mm});
            skArc(sketch, "E2840", {"start": v(-440, 702) * mm, "mid": v(-439.12, 699.88) * mm, "end": v(-437, 699) * mm});
            skArc(sketch, "E2841", {"start": v(-437, 699) * mm, "mid": v(-434.88, 699.88) * mm, "end": v(-434, 702) * mm});
            skArc(sketch, "E2842", {"start": v(-434, 702) * mm, "mid": v(-434.88, 704.12) * mm, "end": v(-437, 705) * mm});
            skArc(sketch, "E2843", {"start": v(-437, 705) * mm, "mid": v(-439.12, 704.12) * mm, "end": v(-440, 702) * mm});
            skArc(sketch, "E2844", {"start": v(-494, -77.99) * mm, "mid": v(-493.12, -80.1) * mm, "end": v(-491, -80.99) * mm});
            skArc(sketch, "E2845", {"start": v(-491, -80.99) * mm, "mid": v(-488.88, -80.1) * mm, "end": v(-488, -77.99) * mm});
            skArc(sketch, "E2846", {"start": v(-488, -77.99) * mm, "mid": v(-488.88, -75.87) * mm, "end": v(-491, -74.99) * mm});
            skArc(sketch, "E2847", {"start": v(-491, -74.99) * mm, "mid": v(-493.12, -75.87) * mm, "end": v(-494, -77.99) * mm});
            skArc(sketch, "E2848", {"start": v(-440, -77.99) * mm, "mid": v(-439.12, -80.1) * mm, "end": v(-437, -80.99) * mm});
            skArc(sketch, "E2849", {"start": v(-437, -80.99) * mm, "mid": v(-434.88, -80.1) * mm, "end": v(-434, -77.99) * mm});
            skArc(sketch, "E2850", {"start": v(-434, -77.99) * mm, "mid": v(-434.88, -75.87) * mm, "end": v(-437, -74.99) * mm});
            skArc(sketch, "E2851", {"start": v(-437, -74.99) * mm, "mid": v(-439.12, -75.87) * mm, "end": v(-440, -77.99) * mm});
            skArc(sketch, "E2852", {"start": v(-254, -948) * mm, "mid": v(-253.12, -950.12) * mm, "end": v(-251, -951) * mm});
            skArc(sketch, "E2853", {"start": v(-251, -951) * mm, "mid": v(-248.88, -950.12) * mm, "end": v(-248, -948) * mm});
            skArc(sketch, "E2854", {"start": v(-248, -948) * mm, "mid": v(-248.88, -945.88) * mm, "end": v(-251, -945) * mm});
            skArc(sketch, "E2855", {"start": v(-251, -945) * mm, "mid": v(-253.12, -945.88) * mm, "end": v(-254, -948) * mm});
            skArc(sketch, "E2856", {"start": v(-200, -948) * mm, "mid": v(-199.12, -950.12) * mm, "end": v(-197, -951) * mm});
            skArc(sketch, "E2857", {"start": v(-197, -951) * mm, "mid": v(-194.88, -950.12) * mm, "end": v(-194, -948) * mm});
            skArc(sketch, "E2858", {"start": v(-194, -948) * mm, "mid": v(-194.88, -945.88) * mm, "end": v(-197, -945) * mm});
            skArc(sketch, "E2859", {"start": v(-197, -945) * mm, "mid": v(-199.12, -945.88) * mm, "end": v(-200, -948) * mm});
            skArc(sketch, "E2860", {"start": v(-254, -1098) * mm, "mid": v(-253.12, -1100.12) * mm, "end": v(-251, -1101) * mm});
            skArc(sketch, "E2861", {"start": v(-251, -1101) * mm, "mid": v(-248.88, -1100.12) * mm, "end": v(-248, -1098) * mm});
            skArc(sketch, "E2862", {"start": v(-248, -1098) * mm, "mid": v(-248.88, -1095.88) * mm, "end": v(-251, -1095) * mm});
            skArc(sketch, "E2863", {"start": v(-251, -1095) * mm, "mid": v(-253.12, -1095.88) * mm, "end": v(-254, -1098) * mm});
            skArc(sketch, "E2864", {"start": v(-200, -1098) * mm, "mid": v(-199.12, -1100.12) * mm, "end": v(-197, -1101) * mm});
            skArc(sketch, "E2865", {"start": v(-197, -1101) * mm, "mid": v(-194.88, -1100.12) * mm, "end": v(-194, -1098) * mm});
            skArc(sketch, "E2866", {"start": v(-194, -1098) * mm, "mid": v(-194.88, -1095.88) * mm, "end": v(-197, -1095) * mm});
            skArc(sketch, "E2867", {"start": v(-197, -1095) * mm, "mid": v(-199.12, -1095.88) * mm, "end": v(-200, -1098) * mm});
            skArc(sketch, "E2868", {"start": v(-254, -798) * mm, "mid": v(-253.12, -800.12) * mm, "end": v(-251, -801) * mm});
            skArc(sketch, "E2869", {"start": v(-251, -801) * mm, "mid": v(-248.88, -800.12) * mm, "end": v(-248, -798) * mm});
            skArc(sketch, "E2870", {"start": v(-248, -798) * mm, "mid": v(-248.88, -795.88) * mm, "end": v(-251, -795) * mm});
            skArc(sketch, "E2871", {"start": v(-251, -795) * mm, "mid": v(-253.12, -795.88) * mm, "end": v(-254, -798) * mm});
            skArc(sketch, "E2872", {"start": v(-200, -798) * mm, "mid": v(-199.12, -800.12) * mm, "end": v(-197, -801) * mm});
            skArc(sketch, "E2873", {"start": v(-197, -801) * mm, "mid": v(-194.88, -800.12) * mm, "end": v(-194, -798) * mm});
            skArc(sketch, "E2874", {"start": v(-194, -798) * mm, "mid": v(-194.88, -795.88) * mm, "end": v(-197, -795) * mm});
            skArc(sketch, "E2875", {"start": v(-197, -795) * mm, "mid": v(-199.12, -795.88) * mm, "end": v(-200, -798) * mm});
            skArc(sketch, "E2876", {"start": v(-254, -648) * mm, "mid": v(-253.12, -650.12) * mm, "end": v(-251, -651) * mm});
            skArc(sketch, "E2877", {"start": v(-251, -651) * mm, "mid": v(-248.88, -650.12) * mm, "end": v(-248, -648) * mm});
            skArc(sketch, "E2878", {"start": v(-248, -648) * mm, "mid": v(-248.88, -645.88) * mm, "end": v(-251, -645) * mm});
            skArc(sketch, "E2879", {"start": v(-251, -645) * mm, "mid": v(-253.12, -645.88) * mm, "end": v(-254, -648) * mm});
            skArc(sketch, "E2880", {"start": v(-200, -648) * mm, "mid": v(-199.12, -650.12) * mm, "end": v(-197, -651) * mm});
            skArc(sketch, "E2881", {"start": v(-197, -651) * mm, "mid": v(-194.88, -650.12) * mm, "end": v(-194, -648) * mm});
            skArc(sketch, "E2882", {"start": v(-194, -648) * mm, "mid": v(-194.88, -645.88) * mm, "end": v(-197, -645) * mm});
            skArc(sketch, "E2883", {"start": v(-197, -645) * mm, "mid": v(-199.12, -645.88) * mm, "end": v(-200, -648) * mm});
            skArc(sketch, "E2884", {"start": v(-254, -498) * mm, "mid": v(-253.12, -500.12) * mm, "end": v(-251, -501) * mm});
            skArc(sketch, "E2885", {"start": v(-251, -501) * mm, "mid": v(-248.88, -500.12) * mm, "end": v(-248, -498) * mm});
            skArc(sketch, "E2886", {"start": v(-248, -498) * mm, "mid": v(-248.88, -495.88) * mm, "end": v(-251, -495) * mm});
            skArc(sketch, "E2887", {"start": v(-251, -495) * mm, "mid": v(-253.12, -495.88) * mm, "end": v(-254, -498) * mm});
            skArc(sketch, "E2888", {"start": v(-200, -498) * mm, "mid": v(-199.12, -500.12) * mm, "end": v(-197, -501) * mm});
            skArc(sketch, "E2889", {"start": v(-197, -501) * mm, "mid": v(-194.88, -500.12) * mm, "end": v(-194, -498) * mm});
            skArc(sketch, "E2890", {"start": v(-194, -498) * mm, "mid": v(-194.88, -495.88) * mm, "end": v(-197, -495) * mm});
            skArc(sketch, "E2891", {"start": v(-197, -495) * mm, "mid": v(-199.12, -495.88) * mm, "end": v(-200, -498) * mm});
            skArc(sketch, "E2892", {"start": v(-254, -348) * mm, "mid": v(-253.12, -350.12) * mm, "end": v(-251, -351) * mm});
            skArc(sketch, "E2893", {"start": v(-251, -351) * mm, "mid": v(-248.88, -350.12) * mm, "end": v(-248, -348) * mm});
            skArc(sketch, "E2894", {"start": v(-248, -348) * mm, "mid": v(-248.88, -345.88) * mm, "end": v(-251, -345) * mm});
            skArc(sketch, "E2895", {"start": v(-251, -345) * mm, "mid": v(-253.12, -345.88) * mm, "end": v(-254, -348) * mm});
            skArc(sketch, "E2896", {"start": v(-200, -348) * mm, "mid": v(-199.12, -350.12) * mm, "end": v(-197, -351) * mm});
            skArc(sketch, "E2897", {"start": v(-197, -351) * mm, "mid": v(-194.88, -350.12) * mm, "end": v(-194, -348) * mm});
            skArc(sketch, "E2898", {"start": v(-194, -348) * mm, "mid": v(-194.88, -345.88) * mm, "end": v(-197, -345) * mm});
            skArc(sketch, "E2899", {"start": v(-197, -345) * mm, "mid": v(-199.12, -345.88) * mm, "end": v(-200, -348) * mm});
            skArc(sketch, "E2900", {"start": v(-254, -198) * mm, "mid": v(-253.12, -200.12) * mm, "end": v(-251, -201) * mm});
            skArc(sketch, "E2901", {"start": v(-251, -201) * mm, "mid": v(-248.88, -200.12) * mm, "end": v(-248, -198) * mm});
            skArc(sketch, "E2902", {"start": v(-248, -198) * mm, "mid": v(-248.88, -195.88) * mm, "end": v(-251, -195) * mm});
            skArc(sketch, "E2903", {"start": v(-251, -195) * mm, "mid": v(-253.12, -195.88) * mm, "end": v(-254, -198) * mm});
            skArc(sketch, "E2904", {"start": v(-200, -198) * mm, "mid": v(-199.12, -200.12) * mm, "end": v(-197, -201) * mm});
            skArc(sketch, "E2905", {"start": v(-197, -201) * mm, "mid": v(-194.88, -200.12) * mm, "end": v(-194, -198) * mm});
            skArc(sketch, "E2906", {"start": v(-194, -198) * mm, "mid": v(-194.88, -195.88) * mm, "end": v(-197, -195) * mm});
            skArc(sketch, "E2907", {"start": v(-197, -195) * mm, "mid": v(-199.12, -195.88) * mm, "end": v(-200, -198) * mm});
            skArc(sketch, "E2908", {"start": v(-254, -18) * mm, "mid": v(-253.12, -20.12) * mm, "end": v(-251, -21) * mm});
            skArc(sketch, "E2909", {"start": v(-251, -21) * mm, "mid": v(-248.88, -20.12) * mm, "end": v(-248, -18) * mm});
            skArc(sketch, "E2910", {"start": v(-248, -18) * mm, "mid": v(-248.88, -15.88) * mm, "end": v(-251, -15) * mm});
            skArc(sketch, "E2911", {"start": v(-251, -15) * mm, "mid": v(-253.12, -15.88) * mm, "end": v(-254, -18) * mm});
            skArc(sketch, "E2912", {"start": v(-200, -18) * mm, "mid": v(-199.12, -20.12) * mm, "end": v(-197, -21) * mm});
            skArc(sketch, "E2913", {"start": v(-197, -21) * mm, "mid": v(-194.88, -20.12) * mm, "end": v(-194, -18) * mm});
            skArc(sketch, "E2914", {"start": v(-194, -18) * mm, "mid": v(-194.88, -15.88) * mm, "end": v(-197, -15) * mm});
            skArc(sketch, "E2915", {"start": v(-197, -15) * mm, "mid": v(-199.12, -15.88) * mm, "end": v(-200, -18) * mm});
            skArc(sketch, "E2916", {"start": v(-254, 102) * mm, "mid": v(-253.12, 99.88) * mm, "end": v(-251, 99) * mm});
            skArc(sketch, "E2917", {"start": v(-251, 99) * mm, "mid": v(-248.88, 99.88) * mm, "end": v(-248, 102) * mm});
            skArc(sketch, "E2918", {"start": v(-248, 102) * mm, "mid": v(-248.88, 104.12) * mm, "end": v(-251, 105) * mm});
            skArc(sketch, "E2919", {"start": v(-251, 105) * mm, "mid": v(-253.12, 104.12) * mm, "end": v(-254, 102) * mm});
            skArc(sketch, "E2920", {"start": v(-200, 102) * mm, "mid": v(-199.12, 99.88) * mm, "end": v(-197, 99) * mm});
            skArc(sketch, "E2921", {"start": v(-197, 99) * mm, "mid": v(-194.88, 99.88) * mm, "end": v(-194, 102) * mm});
            skArc(sketch, "E2922", {"start": v(-194, 102) * mm, "mid": v(-194.88, 104.12) * mm, "end": v(-197, 105) * mm});
            skArc(sketch, "E2923", {"start": v(-197, 105) * mm, "mid": v(-199.12, 104.12) * mm, "end": v(-200, 102) * mm});
            skArc(sketch, "E2924", {"start": v(-254, 252) * mm, "mid": v(-253.12, 249.88) * mm, "end": v(-251, 249) * mm});
            skArc(sketch, "E2925", {"start": v(-251, 249) * mm, "mid": v(-248.88, 249.88) * mm, "end": v(-248, 252) * mm});
            skArc(sketch, "E2926", {"start": v(-248, 252) * mm, "mid": v(-248.88, 254.12) * mm, "end": v(-251, 255) * mm});
            skArc(sketch, "E2927", {"start": v(-251, 255) * mm, "mid": v(-253.12, 254.12) * mm, "end": v(-254, 252) * mm});
            skArc(sketch, "E2928", {"start": v(-200, 252) * mm, "mid": v(-199.12, 249.88) * mm, "end": v(-197, 249) * mm});
            skArc(sketch, "E2929", {"start": v(-197, 249) * mm, "mid": v(-194.88, 249.88) * mm, "end": v(-194, 252) * mm});
            skArc(sketch, "E2930", {"start": v(-194, 252) * mm, "mid": v(-194.88, 254.12) * mm, "end": v(-197, 255) * mm});
            skArc(sketch, "E2931", {"start": v(-197, 255) * mm, "mid": v(-199.12, 254.12) * mm, "end": v(-200, 252) * mm});
            skArc(sketch, "E2932", {"start": v(-254, 402) * mm, "mid": v(-253.12, 399.88) * mm, "end": v(-251, 399) * mm});
            skArc(sketch, "E2933", {"start": v(-251, 399) * mm, "mid": v(-248.88, 399.88) * mm, "end": v(-248, 402) * mm});
            skArc(sketch, "E2934", {"start": v(-248, 402) * mm, "mid": v(-248.88, 404.12) * mm, "end": v(-251, 405) * mm});
            skArc(sketch, "E2935", {"start": v(-251, 405) * mm, "mid": v(-253.12, 404.12) * mm, "end": v(-254, 402) * mm});
            skArc(sketch, "E2936", {"start": v(-200, 402) * mm, "mid": v(-199.12, 399.88) * mm, "end": v(-197, 399) * mm});
            skArc(sketch, "E2937", {"start": v(-197, 399) * mm, "mid": v(-194.88, 399.88) * mm, "end": v(-194, 402) * mm});
            skArc(sketch, "E2938", {"start": v(-194, 402) * mm, "mid": v(-194.88, 404.12) * mm, "end": v(-197, 405) * mm});
            skArc(sketch, "E2939", {"start": v(-197, 405) * mm, "mid": v(-199.12, 404.12) * mm, "end": v(-200, 402) * mm});
            skArc(sketch, "E2940", {"start": v(-254, 552) * mm, "mid": v(-253.12, 549.88) * mm, "end": v(-251, 549) * mm});
            skArc(sketch, "E2941", {"start": v(-251, 549) * mm, "mid": v(-248.88, 549.88) * mm, "end": v(-248, 552) * mm});
            skArc(sketch, "E2942", {"start": v(-248, 552) * mm, "mid": v(-248.88, 554.12) * mm, "end": v(-251, 555) * mm});
            skArc(sketch, "E2943", {"start": v(-251, 555) * mm, "mid": v(-253.12, 554.12) * mm, "end": v(-254, 552) * mm});
            skArc(sketch, "E2944", {"start": v(-200, 552) * mm, "mid": v(-199.12, 549.88) * mm, "end": v(-197, 549) * mm});
            skArc(sketch, "E2945", {"start": v(-197, 549) * mm, "mid": v(-194.88, 549.88) * mm, "end": v(-194, 552) * mm});
            skArc(sketch, "E2946", {"start": v(-194, 552) * mm, "mid": v(-194.88, 554.12) * mm, "end": v(-197, 555) * mm});
            skArc(sketch, "E2947", {"start": v(-197, 555) * mm, "mid": v(-199.12, 554.12) * mm, "end": v(-200, 552) * mm});
            skArc(sketch, "E2948", {"start": v(-254, 702) * mm, "mid": v(-253.12, 699.88) * mm, "end": v(-251, 699) * mm});
            skArc(sketch, "E2949", {"start": v(-251, 699) * mm, "mid": v(-248.88, 699.88) * mm, "end": v(-248, 702) * mm});
            skArc(sketch, "E2950", {"start": v(-248, 702) * mm, "mid": v(-248.88, 704.12) * mm, "end": v(-251, 705) * mm});
            skArc(sketch, "E2951", {"start": v(-251, 705) * mm, "mid": v(-253.12, 704.12) * mm, "end": v(-254, 702) * mm});
            skArc(sketch, "E2952", {"start": v(-200, 702) * mm, "mid": v(-199.12, 699.88) * mm, "end": v(-197, 699) * mm});
            skArc(sketch, "E2953", {"start": v(-197, 699) * mm, "mid": v(-194.88, 699.88) * mm, "end": v(-194, 702) * mm});
            skArc(sketch, "E2954", {"start": v(-194, 702) * mm, "mid": v(-194.88, 704.12) * mm, "end": v(-197, 705) * mm});
            skArc(sketch, "E2955", {"start": v(-197, 705) * mm, "mid": v(-199.12, 704.12) * mm, "end": v(-200, 702) * mm});
            skArc(sketch, "E2956", {"start": v(-254, -77.99) * mm, "mid": v(-253.12, -80.1) * mm, "end": v(-251, -80.99) * mm});
            skArc(sketch, "E2957", {"start": v(-251, -80.99) * mm, "mid": v(-248.88, -80.1) * mm, "end": v(-248, -77.99) * mm});
            skArc(sketch, "E2958", {"start": v(-248, -77.99) * mm, "mid": v(-248.88, -75.87) * mm, "end": v(-251, -74.99) * mm});
            skArc(sketch, "E2959", {"start": v(-251, -74.99) * mm, "mid": v(-253.12, -75.87) * mm, "end": v(-254, -77.99) * mm});
            skArc(sketch, "E2960", {"start": v(-200, -77.99) * mm, "mid": v(-199.12, -80.1) * mm, "end": v(-197, -80.99) * mm});
            skArc(sketch, "E2961", {"start": v(-197, -80.99) * mm, "mid": v(-194.88, -80.1) * mm, "end": v(-194, -77.99) * mm});
            skArc(sketch, "E2962", {"start": v(-194, -77.99) * mm, "mid": v(-194.88, -75.87) * mm, "end": v(-197, -74.99) * mm});
            skArc(sketch, "E2963", {"start": v(-197, -74.99) * mm, "mid": v(-199.12, -75.87) * mm, "end": v(-200, -77.99) * mm});
            skSolve(sketch);
        }
        {
            var Q0;
            Q0=makeQuery(id+"F0.imprint","IMPRINT",FACE,{"disambiguationData":[TD([[makeQuery(id+"F0.imprint","IMPRINT",EDGE,{"derivedFrom":sQuery(id+"F0.wireOp",EDGE,"E36")}),1.0]])]});
            var Q1;
            {var subQ0=sQuery(id+"F0.wireOp",EDGE,"E1499");Q1=makeQuery(id+"F0.imprint","IMPRINT",FACE,{"disambiguationData":[TD([[makeQuery(id+"F0.imprint","IMPRINT",EDGE,{"derivedFrom":subQ0}),-1.0]])]});}
            var Q2;
            Q2=makeQuery(id+"F0.imprint","IMPRINT",FACE,{"disambiguationData":[TD([[makeQuery(id+"F0.imprint","IMPRINT",EDGE,{"derivedFrom":sQuery(id+"F0.wireOp",EDGE,"E1613")}),-1.0]])]});
            var Q3;
            Q3=makeQuery(id+"F0.imprint","IMPRINT",FACE,{"disambiguationData":[TD([[makeQuery(id+"F0.imprint","IMPRINT",EDGE,{"derivedFrom":sQuery(id+"F0.wireOp",EDGE,"E1869")}),-1.0]])]});
            extrude(context, id + "F1", {"entities" : qUnion([Q0, Q1, Q2, Q3]), "depth" : 18 * mm});
        }
        {
            var Q0;
            Q0=makeQuery(id+"F0.imprint","IMPRINT",FACE,{"disambiguationData":[TD([[makeQuery(id+"F0.imprint","IMPRINT",EDGE,{"derivedFrom":sQuery(id+"F0.wireOp",EDGE,"E20")}),1.0]])]});
            var Q1;
            Q1=makeQuery(id+"F0.imprint","IMPRINT",FACE,{"disambiguationData":[TD([[makeQuery(id+"F0.imprint","IMPRINT",EDGE,{"derivedFrom":sQuery(id+"F0.wireOp",EDGE,"E2385")}),-1.0]])]});
            extrude(context, id + "F2", {"entities" : qUnion([Q0, Q1]), "depth" : 18 * mm});
        }
    });
